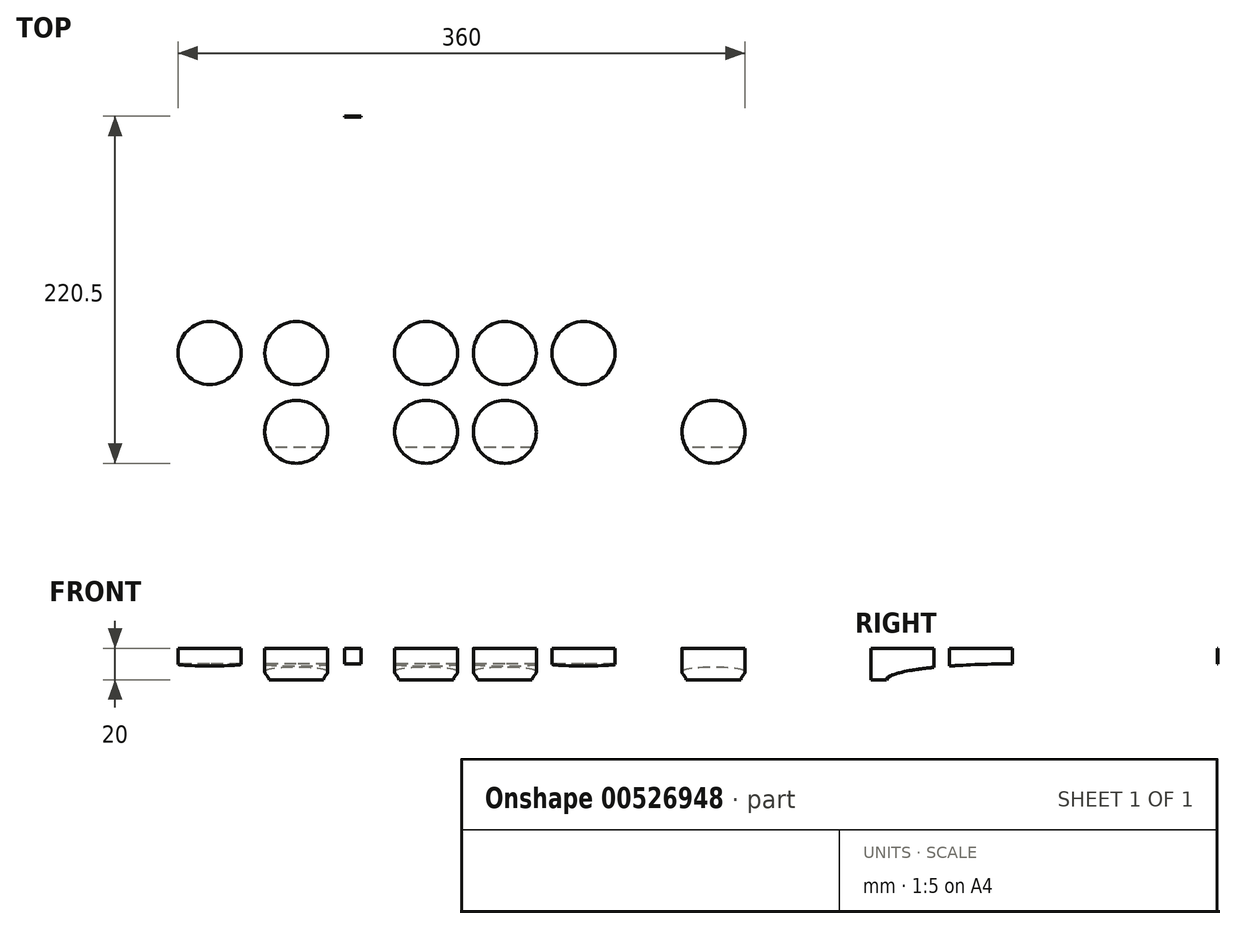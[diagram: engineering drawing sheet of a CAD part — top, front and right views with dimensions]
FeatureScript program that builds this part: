
annotation { "Feature Type Name" : "Feature", "Feature Type Description" : "" }
export const myFeature = defineFeature(function(context is Context, id is Id, definition is map)
    precondition{}
    {
        {
            var Q0;
            Q0=qCreatedBy(makeId("Top.planeOp"),FACE);
            var sketch = newSketch(context, id + "F0", { "sketchPlane" : qUnion([Q0])});
            skLineSegment(sketch, "E0.bottom", {"start": v(-365, 200) * mm, "end": v(365, 200) * mm});
            skLineSegment(sketch, "E0.top", {"start": v(-365, -200) * mm, "end": v(365, -200) * mm});
            skLineSegment(sketch, "E0.left", {"start": v(-365, 200) * mm, "end": v(-365, -200) * mm});
            skLineSegment(sketch, "E0.right", {"start": v(365, 200) * mm, "end": v(365, -200) * mm});
            skPoint(sketch, "E0.middle", {"position": v(0, 0) * mm});
            skEllipticalArc(sketch, "E1", {});
            skEllipticalArc(sketch, "E2.MirrorCS", {});
            skEllipticalArc(sketch, "E3.MirrorCS", {});
            skEllipticalArc(sketch, "E4.MirrorCS", {});
            skLineSegment(sketch, "E5", {"start": v(-365, 200) * mm, "end": v(-105, 200) * mm});
            skLineSegment(sketch, "E6", {"start": v(-365, 200) * mm, "end": v(-365, 50) * mm});
            skLineSegment(sketch, "E7", {"start": v(-365, -200) * mm, "end": v(-365, -50) * mm});
            skLineSegment(sketch, "E8", {"start": v(-365, -200) * mm, "end": v(-182.5, -200) * mm});
            skLineSegment(sketch, "E9", {"start": v(365, 200) * mm, "end": v(105, 200) * mm});
            skLineSegment(sketch, "E10", {"start": v(182.5, -200.11) * mm, "end": v(365, -200) * mm});
            skPoint(sketch, "E11", {"position": v(0, 200) * mm});
            skLineSegment(sketch, "E12", {"start": v(0, 200) * mm, "end": v(-130, 200) * mm});
            skLineSegment(sketch, "E13.MirrorCS", {"start": v(0, -200) * mm, "end": v(-130, -200) * mm});
            skLineSegment(sketch, "E14.MirrorCS", {"start": v(5, 200) * mm, "end": v(130, 200) * mm});
            skLineSegment(sketch, "E15.MirrorCS", {"start": v(-72.5, -200) * mm, "end": v(52.5, -200) * mm});
            skCircle(sketch, "E16", {"center": v(-278.75, 100) * mm, "radius": 20 * mm});
            skCircle(sketch, "E17", {"center": v(-223.75, 150) * mm, "radius": 20 * mm});
            skCircle(sketch, "E18", {"center": v(-223.75, 100) * mm, "radius": 20 * mm});
            skCircle(sketch, "E19", {"center": v(-141.25, 100) * mm, "radius": 20 * mm});
            skCircle(sketch, "E20", {"center": v(-141.25, 150) * mm, "radius": 20 * mm});
            skCircle(sketch, "E21", {"center": v(-91.25, 100) * mm, "radius": 20 * mm});
            skCircle(sketch, "E22", {"center": v(-91.25, 150) * mm, "radius": 20 * mm});
            skCircle(sketch, "E23", {"center": v(-41.25, 100) * mm, "radius": 20 * mm});
            skCircle(sketch, "E24.MirrorC", {"center": v(-41.25, 150) * mm, "radius": 20 * mm});
            skCircle(sketch, "E25.MirrorC", {"center": v(-278.75, -100) * mm, "radius": 20 * mm});
            skCircle(sketch, "E26.MirrorC", {"center": v(-223.75, -150) * mm, "radius": 20 * mm});
            skCircle(sketch, "E27.MirrorC", {"center": v(-223.75, -100) * mm, "radius": 20 * mm});
            skCircle(sketch, "E28.MirrorC", {"center": v(-141.25, -100) * mm, "radius": 20 * mm});
            skCircle(sketch, "E29.MirrorC", {"center": v(-141.25, -150) * mm, "radius": 20 * mm});
            skCircle(sketch, "E30.MirrorC", {"center": v(-91.25, -100) * mm, "radius": 20 * mm});
            skCircle(sketch, "E31.MirrorC", {"center": v(-41.25, -100) * mm, "radius": 20 * mm});
            skCircle(sketch, "E32.MirrorC", {"center": v(-91.25, -150) * mm, "radius": 20 * mm});
            skCircle(sketch, "E33.MirrorC", {"center": v(-41.25, -150) * mm, "radius": 20 * mm});
            skCircle(sketch, "E34.MirrorC", {"center": v(-222.5, -10) * mm, "radius": 20 * mm});
            skLineSegment(sketch, "E35.bottom", {"start": v(210, 15) * mm, "end": v(-210, 15) * mm});
            skLineSegment(sketch, "E35.top", {"start": v(210, -15) * mm, "end": v(-210, -15) * mm});
            skLineSegment(sketch, "E35.left", {"start": v(210, 15) * mm, "end": v(210, -15) * mm});
            skLineSegment(sketch, "E35.right", {"start": v(-210, 15) * mm, "end": v(-210, -15) * mm});
            skLineSegment(sketch, "E36", {"start": v(-365, -50) * mm, "end": v(365, -50) * mm});
            skLineSegment(sketch, "E37", {"start": v(-365, 50) * mm, "end": v(365, 50) * mm});
            skLineSegment(sketch, "E38", {"start": v(-182.5, -200) * mm, "end": v(-182.5, -40.61) * mm});
            skLineSegment(sketch, "E39", {"start": v(0, -200) * mm, "end": v(0, -50) * mm});
            skLineSegment(sketch, "E40", {"start": v(182.5, -200.11) * mm, "end": v(182.4, -40.7) * mm});
            skLineSegment(sketch, "E41.trimOffspring", {"start": v(-182.5, 40.61) * mm, "end": v(-182.5, 200) * mm});
            skLineSegment(sketch, "E42.trimOffspring", {"start": v(-182.5, -15) * mm, "end": v(-182.5, 15) * mm});
            skLineSegment(sketch, "E43.trimOffspring", {"start": v(182.39, -15) * mm, "end": v(182.37, 15) * mm});
            skLineSegment(sketch, "E44.trimOffspring", {"start": v(182.35, 40.73) * mm, "end": v(182.25, 200) * mm});
            skCircle(sketch, "E45", {"center": v(-272.5, 10) * mm, "radius": 20 * mm});
            skCircle(sketch, "E46.MirrorC", {"center": v(-322.5, -8.74) * mm, "radius": 20 * mm});
            skCircle(sketch, "E47.MirrorC", {"center": v(-142.5, -10) * mm, "radius": 20 * mm});
            skCircle(sketch, "E48.MirrorC", {"center": v(-92.5, 10) * mm, "radius": 20 * mm});
            skCircle(sketch, "E49.MirrorC", {"center": v(-42.5, -8.74) * mm, "radius": 20 * mm});
            skCircle(sketch, "E50.MirrorC", {"center": v(42.5, -8.74) * mm, "radius": 20 * mm});
            skCircle(sketch, "E51.MirrorC", {"center": v(142.5, -10) * mm, "radius": 20 * mm});
            skCircle(sketch, "E52.MirrorC", {"center": v(92.5, 10) * mm, "radius": 20 * mm});
            skCircle(sketch, "E53.MirrorC", {"center": v(222.5, -10) * mm, "radius": 20 * mm});
            skCircle(sketch, "E54.MirrorC", {"center": v(272.5, 10) * mm, "radius": 20 * mm});
            skCircle(sketch, "E55.MirrorC", {"center": v(322.5, -8.74) * mm, "radius": 20 * mm});
            skCircle(sketch, "E56.MirrorC", {"center": v(223.75, -100) * mm, "radius": 20 * mm});
            skCircle(sketch, "E57.MirrorC", {"center": v(223.75, -150) * mm, "radius": 20 * mm});
            skCircle(sketch, "E58.MirrorC", {"center": v(278.75, -100) * mm, "radius": 20 * mm});
            skCircle(sketch, "E59.MirrorC", {"center": v(141.25, -100) * mm, "radius": 20 * mm});
            skCircle(sketch, "E60.MirrorC", {"center": v(141.25, -150) * mm, "radius": 20 * mm});
            skCircle(sketch, "E61.MirrorC", {"center": v(91.25, -150) * mm, "radius": 20 * mm});
            skCircle(sketch, "E62.MirrorC", {"center": v(91.25, -100) * mm, "radius": 20 * mm});
            skCircle(sketch, "E63.MirrorC", {"center": v(41.25, -100) * mm, "radius": 20 * mm});
            skCircle(sketch, "E64.MirrorC", {"center": v(41.25, -150) * mm, "radius": 20 * mm});
            skCircle(sketch, "E65.MirrorC", {"center": v(41.25, 100) * mm, "radius": 20 * mm});
            skCircle(sketch, "E66.MirrorC", {"center": v(91.25, 100) * mm, "radius": 20 * mm});
            skCircle(sketch, "E67.MirrorC", {"center": v(141.25, 100) * mm, "radius": 20 * mm});
            skCircle(sketch, "E68.MirrorC", {"center": v(223.75, 100) * mm, "radius": 20 * mm});
            skCircle(sketch, "E69.MirrorC", {"center": v(278.75, 100) * mm, "radius": 20 * mm});
            skCircle(sketch, "E70.MirrorC", {"center": v(223.75, 150) * mm, "radius": 20 * mm});
            skCircle(sketch, "E71.MirrorC", {"center": v(141.25, 150) * mm, "radius": 20 * mm});
            skCircle(sketch, "E72.MirrorC", {"center": v(91.25, 150) * mm, "radius": 20 * mm});
            skCircle(sketch, "E73.MirrorC", {"center": v(41.25, 150) * mm, "radius": 20 * mm});
            const initialGuessF0  = {"E1": [0.215000023161019, -0.00011114199246731203, 0, -1, 0.20000000103052606, 0.15, 6.249845643425636, 1.5707963267948966], "E2.MirrorCS": [-0.215, -0.00011114199246737072, 0, -1, 0.2, 0.15, 4.711833270393751, 0.03333950926130193], "E3.MirrorCS": [-0.215, 0.00011114199246727815, 0, 1, 0.2, 0.15, 6.249845797918284, 1.5707963267948966], "E4.MirrorCS": [0.215, 0.00011114199246735796, 0, 1, 0.2, 0.15, 4.711277560231201, 0.03333950926130226]};
            skSetInitialGuess(sketch, initialGuessF0);
            skSolve(sketch);
        }
        {
            var Q0;
            Q0=qCreatedBy(makeId("Top.planeOp"),FACE);
            cPlane(context, id + "F1", {"entities" : qUnion([Q0]), "cplaneType" : CPlaneType.OFFSET, "offset" : 20 * mm, "width" : 150 * mm, "height" : 150 * mm});
        }
        {
            var Q0;
            Q0=qCreatedBy(id+"F1.planeOp",FACE);
            var sketch = newSketch(context, id + "F2", { "sketchPlane" : qUnion([Q0])});
            skLineSegment(sketch, "E74.bottom", {"start": v(0, 0) * mm, "end": v(365, 0) * mm});
            skLineSegment(sketch, "E74.top", {"start": v(0, -200) * mm, "end": v(210, -200) * mm});
            skLineSegment(sketch, "E74.left", {"start": v(0, 0) * mm, "end": v(0, -200) * mm});
            skLineSegment(sketch, "E75", {"start": v(0, -15) * mm, "end": v(364.58, -15) * mm});
            skLineSegment(sketch, "E76", {"start": v(0, -170) * mm, "end": v(294.02, -170) * mm});
            skLineSegment(sketch, "E77", {"start": v(330, 0) * mm, "end": v(330, -128.4) * mm});
            skLineSegment(sketch, "E78", {"start": v(215, 0) * mm, "end": v(215, -200) * mm});
            skPoint(sketch, "E79", {"position": v(215, -200) * mm});
            skPoint(sketch, "E80", {"position": v(365, 0) * mm});
            skLineSegment(sketch, "E81", {"start": v(275, 0) * mm, "end": v(275, -183.3) * mm});
            skLineSegment(sketch, "E82", {"start": v(275, -140) * mm, "end": v(322.12, -140) * mm});
            skPoint(sketch, "E83", {"position": v(215, -170) * mm});
            skPoint(sketch, "E84", {"position": v(330, 0) * mm});
            skPoint(sketch, "E85", {"position": v(275, -140) * mm});
            skPoint(sketch, "E86", {"position": v(330, -140) * mm});
            skPoint(sketch, "E87", {"position": v(275, -185) * mm});
            skLineSegment(sketch, "E88", {"start": v(315, -149.07) * mm, "end": v(315, 0) * mm});
            skLineSegment(sketch, "E89", {"start": v(210, 0) * mm, "end": v(210, -200) * mm});
            skEllipticalArc(sketch, "E90.trimOffspring", {});
            skEllipticalArc(sketch, "E91", {});
            skPoint(sketch, "E92.orphan", {"position": v(365, -170) * mm});
            skPoint(sketch, "E93.trimOffspring.end.orphan", {"position": v(330, -200) * mm});
            skPoint(sketch, "E94.orphan", {"position": v(365, -200) * mm});
            skPoint(sketch, "E95.orphan", {"position": v(365, -15) * mm});
            skLineSegment(sketch, "E96.MirrorCS", {"start": v(0, 0) * mm, "end": v(-365, 0) * mm});
            skLineSegment(sketch, "E97.MirrorCS", {"start": v(0, -15) * mm, "end": v(-364.58, -15) * mm});
            skLineSegment(sketch, "E98.MirrorCS", {"start": v(0, -170) * mm, "end": v(-294.02, -170) * mm});
            skLineSegment(sketch, "E99.MirrorCS", {"start": v(0, -200) * mm, "end": v(-210, -200) * mm});
            skLineSegment(sketch, "E100.MirrorCS", {"start": v(-210, 0) * mm, "end": v(-210, -200) * mm});
            skLineSegment(sketch, "E101.MirrorCS", {"start": v(-215, 0) * mm, "end": v(-215, -200) * mm});
            skEllipticalArc(sketch, "E102.MirrorCS", {});
            skEllipticalArc(sketch, "E103.MirrorCS", {});
            skLineSegment(sketch, "E104.MirrorCS", {"start": v(-275, 0) * mm, "end": v(-275, -183.3) * mm});
            skLineSegment(sketch, "E105.MirrorCS", {"start": v(-275, -140) * mm, "end": v(-322.12, -140) * mm});
            skLineSegment(sketch, "E106.MirrorCS", {"start": v(-315, -149.07) * mm, "end": v(-315, 0) * mm});
            skLineSegment(sketch, "E107.MirrorCS", {"start": v(-330, 0) * mm, "end": v(-330, -128.4) * mm});
            skLineSegment(sketch, "E108.MirrorCS", {"start": v(0, 15) * mm, "end": v(-364.58, 15) * mm});
            skLineSegment(sketch, "E109.MirrorCS", {"start": v(0, 15) * mm, "end": v(364.58, 15) * mm});
            skEllipticalArc(sketch, "E110.MirrorCS", {});
            skLineSegment(sketch, "E111.MirrorCS", {"start": v(-330, 0) * mm, "end": v(-330, 128.4) * mm});
            skLineSegment(sketch, "E112.MirrorCS", {"start": v(-315, 149.07) * mm, "end": v(-315, 0) * mm});
            skLineSegment(sketch, "E113.MirrorCS", {"start": v(-275, 0) * mm, "end": v(-275, 183.3) * mm});
            skLineSegment(sketch, "E114.MirrorCS", {"start": v(-215, 0) * mm, "end": v(-215, 200) * mm});
            skLineSegment(sketch, "E115.MirrorCS", {"start": v(-210, 0) * mm, "end": v(-210, 200) * mm});
            skLineSegment(sketch, "E116.MirrorCS", {"start": v(0, 0) * mm, "end": v(0, 200) * mm});
            skLineSegment(sketch, "E117.MirrorCS", {"start": v(210, 0) * mm, "end": v(210, 200) * mm});
            skLineSegment(sketch, "E118.MirrorCS", {"start": v(215, 0) * mm, "end": v(215, 200) * mm});
            skLineSegment(sketch, "E119.MirrorCS", {"start": v(275, 0) * mm, "end": v(275, 183.3) * mm});
            skLineSegment(sketch, "E120.MirrorCS", {"start": v(315, 149.07) * mm, "end": v(315, 0) * mm});
            skLineSegment(sketch, "E121.MirrorCS", {"start": v(330, 0) * mm, "end": v(330, 128.4) * mm});
            skEllipticalArc(sketch, "E122.MirrorCS", {});
            skEllipticalArc(sketch, "E123.MirrorCS", {});
            skEllipticalArc(sketch, "E124.MirrorCS", {});
            skLineSegment(sketch, "E125.MirrorCS", {"start": v(-275, 140) * mm, "end": v(-322.12, 140) * mm});
            skLineSegment(sketch, "E126.MirrorCS", {"start": v(0, 170) * mm, "end": v(-294.02, 170) * mm});
            skLineSegment(sketch, "E127.MirrorCS", {"start": v(0, 170) * mm, "end": v(294.02, 170) * mm});
            skLineSegment(sketch, "E128.MirrorCS", {"start": v(0, 200) * mm, "end": v(210, 200) * mm});
            skLineSegment(sketch, "E129.MirrorCS", {"start": v(0, 200) * mm, "end": v(-210, 200) * mm});
            skLineSegment(sketch, "E130.MirrorCS", {"start": v(275, 140) * mm, "end": v(322.12, 140) * mm});
            const initialGuessF2  = {"E90.trimOffspring": [0.215, 0, 1, 0, 0.115, 0.17, 4.71238898038469, 6.283185307179586], "E91": [0.215, 0, 0, -1, 0.2, 0.15, 6.249845797918284, 1.5707963267948966], "E102.MirrorCS": [-0.215, 0, -1, 0, 0.115, 0.17, 6.283185307179586, 1.5707963267948966], "E103.MirrorCS": [-0.215, 0, 0, -1, 0.2, 0.15, 4.71238898038469, 0.03333950926130225], "E110.MirrorCS": [-0.215, 0, 0, 1, 0.2, 0.15, 6.249845797918284, 1.5707963267948966], "E122.MirrorCS": [0.215, 0, 0, 1, 0.2, 0.15, 4.71238898038469, 0.03333950926130225], "E123.MirrorCS": [0.215, 0, 1, 0, 0.115, 0.17, 6.283185307179586, 1.5707963267948966], "E124.MirrorCS": [-0.215, 0, -1, 0, 0.115, 0.17, 4.71238898038469, 6.283185307179586]};
            skSetInitialGuess(sketch, initialGuessF2);
            skSolve(sketch);
        }
        {
            var Q0;
            Q0=qCreatedBy(makeId("Right.planeOp"),FACE);
            var sketch = newSketch(context, id + "F3", { "sketchPlane" : qUnion([Q0])});
            skPoint(sketch, "E131.middle", {"position": v(0, 20) * mm});
            skPoint(sketch, "E132", {"position": v(170, 0) * mm});
            skPoint(sketch, "E133", {"position": v(160, 0) * mm});
            skLineSegment(sketch, "E134.bottom", {"start": v(15, 10.07) * mm, "end": v(80, 10.07) * mm});
            skPoint(sketch, "E135", {"position": v(80, 10.07) * mm});
            skEllipticalArc(sketch, "E136", {});
            skEllipticalArc(sketch, "E137", {});
            skLineSegment(sketch, "E138", {"start": v(0, 20) * mm, "end": v(0, 10.04) * mm});
            skLineSegment(sketch, "E139", {"start": v(0, 20) * mm, "end": v(200, 20) * mm});
            skLineSegment(sketch, "E140", {"start": v(200, 20) * mm, "end": v(0, 20) * mm});
            skLineSegment(sketch, "E141", {"start": v(160, 0) * mm, "end": v(170, 0) * mm});
            skPoint(sketch, "E142.orphan", {"position": v(-200, 20) * mm});
            skLineSegment(sketch, "E143.MirrorCS", {"start": v(-200, 20) * mm, "end": v(0, 20) * mm});
            skLineSegment(sketch, "E144.MirrorCS", {"start": v(-15, 10.07) * mm, "end": v(-80, 10.07) * mm});
            skEllipticalArc(sketch, "E145.MirrorCS", {});
            skLineSegment(sketch, "E146.MirrorCS", {"start": v(-160, 0) * mm, "end": v(-170, 0) * mm});
            skEllipticalArc(sketch, "E147.MirrorCS", {});
            skLineSegment(sketch, "E148.top", {"start": v(-15, 12) * mm, "end": v(15, 12) * mm});
            skLineSegment(sketch, "E148.left", {"start": v(-15, 10.07) * mm, "end": v(-15, 12) * mm});
            skLineSegment(sketch, "E148.right", {"start": v(15, 10.07) * mm, "end": v(15, 12) * mm});
            skLineSegment(sketch, "E149.bottom", {"start": v(15, 18) * mm, "end": v(-15, 18) * mm});
            skLineSegment(sketch, "E149.top", {"start": v(15, 12) * mm, "end": v(-15, 12) * mm});
            skLineSegment(sketch, "E149.left", {"start": v(15, 18) * mm, "end": v(15, 12) * mm});
            skLineSegment(sketch, "E149.right", {"start": v(-15, 18) * mm, "end": v(-15, 12) * mm});
            skLineSegment(sketch, "E150", {"start": v(170, 0) * mm, "end": v(170.12, 20) * mm});
            skLineSegment(sketch, "E151", {"start": v(-170, 0) * mm, "end": v(-170.12, 20) * mm});
            skLineSegment(sketch, "E152", {"start": v(-15, 12) * mm, "end": v(-15, 10.07) * mm});
            skLineSegment(sketch, "E153.bottom", {"start": v(-200, 20) * mm, "end": v(-170, 20) * mm});
            skLineSegment(sketch, "E153.top", {"start": v(-200, 0) * mm, "end": v(-170, 0) * mm});
            skLineSegment(sketch, "E153.left", {"start": v(-200, 20) * mm, "end": v(-200, 0) * mm});
            skLineSegment(sketch, "E153.right", {"start": v(-170, 20) * mm, "end": v(-170, 0) * mm});
            skLineSegment(sketch, "E154.MirrorCS", {"start": v(200, 0) * mm, "end": v(170, 0) * mm});
            skLineSegment(sketch, "E155.MirrorCS", {"start": v(200, 20) * mm, "end": v(200, 0) * mm});
            skLineSegment(sketch, "E156", {"start": v(80, 10.07) * mm, "end": v(80, 20) * mm});
            skLineSegment(sketch, "E157", {"start": v(160, 0) * mm, "end": v(160, 20) * mm});
            skLineSegment(sketch, "E158", {"start": v(149.2, 20) * mm, "end": v(149.2, 5.05) * mm});
            skLineSegment(sketch, "E159", {"start": v(140.08, 20) * mm, "end": v(140.08, 6.65) * mm});
            skLineSegment(sketch, "E160", {"start": v(128.23, 20) * mm, "end": v(128.23, 8.04) * mm});
            skLineSegment(sketch, "E161", {"start": v(102.69, 20) * mm, "end": v(102.69, 9.66) * mm});
            skLineSegment(sketch, "E162.MirrorCS", {"start": v(-80, 10.07) * mm, "end": v(-80, 20) * mm});
            skLineSegment(sketch, "E163.MirrorCS", {"start": v(-102.69, 20) * mm, "end": v(-102.69, 9.66) * mm});
            skLineSegment(sketch, "E164.MirrorCS", {"start": v(-128.23, 20) * mm, "end": v(-128.23, 8.04) * mm});
            skLineSegment(sketch, "E165.MirrorCS", {"start": v(-140.08, 20) * mm, "end": v(-140.08, 6.65) * mm});
            skLineSegment(sketch, "E166.MirrorCS", {"start": v(-149.2, 20) * mm, "end": v(-149.2, 5.05) * mm});
            skLineSegment(sketch, "E167.MirrorCS", {"start": v(-160, 0) * mm, "end": v(-160, 20) * mm});
            skLineSegment(sketch, "E168", {"start": v(45, 20) * mm, "end": v(45, 10.07) * mm});
            skLineSegment(sketch, "E169.MirrorCS", {"start": v(-45, 20) * mm, "end": v(-45, 10.07) * mm});
            const initialGuessF3  = {"E136": [0.17012490332126617, 0.02, -0.006245044279577429, -0.9999804995208388, 0.020000390017188747, 0.02987581400604767, 6.283185307179586, 1.580124845260153], "E137": [0.08, 0, 0, 1, 0.01007139225942586, 0.08, 4.71238898038469, 6.283185307179586], "E145.MirrorCS": [-0.08, 0, 0, 1, 0.01007139225942586, 0.08, 6.283185307179586, 1.5707963267948966], "E147.MirrorCS": [-0.17012490332126617, 0.02, 0.006245044279579518, -0.9999804995208388, 0.020000390017188747, 0.02987581400604767, 4.703060461919433, 6.283185307179586]};
            skSetInitialGuess(sketch, initialGuessF3);
            skSolve(sketch);
        }
        {
            var Q0;
            Q0=qCreatedBy(makeId("Front.planeOp"),FACE);
            var sketch = newSketch(context, id + "F4", { "sketchPlane" : qUnion([Q0])});
            skLineSegment(sketch, "E170", {"start": v(0, 20) * mm, "end": v(365, 20) * mm});
            skPoint(sketch, "E171", {"position": v(210, 20) * mm});
            skLineSegment(sketch, "E172", {"start": v(210, 18) * mm, "end": v(210, 12) * mm});
            skPoint(sketch, "E173", {"position": v(315, 20) * mm});
            skLineSegment(sketch, "E174", {"start": v(315, 18) * mm, "end": v(315, 0) * mm});
            skLineSegment(sketch, "E175", {"start": v(0, 12) * mm, "end": v(0, 20) * mm});
            skLineSegment(sketch, "E176", {"start": v(210, 12) * mm, "end": v(0, 12) * mm});
            skPoint(sketch, "E177", {"position": v(365.07, 0) * mm});
            skPoint(sketch, "E178", {"position": v(365, 20) * mm});
            skEllipticalArc(sketch, "E179", {});
            skLineSegment(sketch, "E180", {"start": v(315, 18) * mm, "end": v(210, 18) * mm});
            skLineSegment(sketch, "E181.MirrorCS", {"start": v(0, 20) * mm, "end": v(-365, 20) * mm});
            skLineSegment(sketch, "E182.MirrorCS", {"start": v(-210, 12) * mm, "end": v(0, 12) * mm});
            skLineSegment(sketch, "E183.MirrorCS", {"start": v(-210, 18) * mm, "end": v(-210, 12) * mm});
            skLineSegment(sketch, "E184.MirrorCS", {"start": v(-315, 18) * mm, "end": v(-210, 18) * mm});
            skLineSegment(sketch, "E185.MirrorCS", {"start": v(-315, 18) * mm, "end": v(-315, 0) * mm});
            skEllipticalArc(sketch, "E186.MirrorCS", {});
            skPoint(sketch, "E187", {"position": v(245, 20) * mm});
            skPoint(sketch, "E188", {"position": v(245, 10.07) * mm});
            skPoint(sketch, "E189", {"position": v(325, 20) * mm});
            skPoint(sketch, "E190", {"position": v(335, 20) * mm});
            skLineSegment(sketch, "E191", {"start": v(335, 20) * mm, "end": v(335, 10.07) * mm});
            skLineSegment(sketch, "E192", {"start": v(335, 10.07) * mm, "end": v(0, 10.07) * mm});
            skLineSegment(sketch, "E193.MirrorCS", {"start": v(-335, 10.07) * mm, "end": v(0, 10.07) * mm});
            skLineSegment(sketch, "E194.MirrorCS", {"start": v(-335, 20) * mm, "end": v(-335, 10.07) * mm});
            skLineSegment(sketch, "E195", {"start": v(365, 20) * mm, "end": v(365.07, 0) * mm});
            skLineSegment(sketch, "E196", {"start": v(315, 0) * mm, "end": v(365.07, 0) * mm});
            skLineSegment(sketch, "E197.MirrorCS", {"start": v(-365, 20) * mm, "end": v(-365.07, 0) * mm});
            skLineSegment(sketch, "E198.MirrorCS", {"start": v(-315, 0) * mm, "end": v(-365.07, 0) * mm});
            skLineSegment(sketch, "E199", {"start": v(335, 10.07) * mm, "end": v(335, 1.67) * mm});
            skLineSegment(sketch, "E200.MirrorCS", {"start": v(-335, 10.07) * mm, "end": v(-335, 1.67) * mm});
            skLineSegment(sketch, "E201", {"start": v(-315, 18) * mm, "end": v(-315, 20) * mm});
            skLineSegment(sketch, "E202", {"start": v(-210, 18) * mm, "end": v(-210, 20) * mm});
            skLineSegment(sketch, "E203.MirrorCS", {"start": v(210, 18) * mm, "end": v(210, 20) * mm});
            skLineSegment(sketch, "E204.MirrorCS", {"start": v(315, 18) * mm, "end": v(315, 20) * mm});
            skPoint(sketch, "E205", {"position": v(275, 20) * mm});
            skPoint(sketch, "E206.MirrorP", {"position": v(-275, 20) * mm});
            skLineSegment(sketch, "E207", {"start": v(275, 20) * mm, "end": v(275, 18) * mm});
            skLineSegment(sketch, "E208.MirrorCS", {"start": v(-275, 20) * mm, "end": v(-275, 18) * mm});
            skPoint(sketch, "E209", {"position": v(-333.25, 14.9) * mm});
            skPoint(sketch, "E210", {"position": v(-218.12, 14.9) * mm});
            skPoint(sketch, "E211", {"position": v(-78.75, 14.9) * mm});
            const initialGuessF4  = {"E179": [0.315, 0.02, 1, 0, 0.05, 0.02, 4.71238898038469, 0], "E186.MirrorCS": [-0.315, 0.02, -1, 0, 0.05, 0.02, 0, 1.5707963267948966]};
            skSetInitialGuess(sketch, initialGuessF4);
            skSolve(sketch);
        }
        {
            var Q0;
            Q0=qSketchRegion(id+"F2",true);
            var Q1;
            {var subQ0=sQuery(id+"F2.wireOp",EDGE,"E125.MirrorCS");var subQ1=sQuery(id+"F2.wireOp",EDGE,"E112.MirrorCS");var subQ2=makeQuery(id+"F2.imprint","INTERSECT",VERTEX,{"derivedFrom":[subQ1,subQ0]});Q1=makeQuery(id+"F2.imprint","IMPRINT",FACE,{"disambiguationData":[TD([[makeQuery(id+"F2.imprint","IMPRINT",EDGE,{"disambiguationData":[TD([[subQ2,-1.0]])],"derivedFrom":subQ1}),1.0]])]});}
            var Q2;
            {var subQ0=sQuery(id+"F2.wireOp",EDGE,"E124.MirrorCS");var subQ1=sQuery(id+"F2.wireOp",EDGE,"E113.MirrorCS");var subQ2=makeQuery(id+"F2.imprint","INTERSECT",VERTEX,{"derivedFrom":[subQ1,subQ0]});Q2=makeQuery(id+"F2.imprint","IMPRINT",FACE,{"disambiguationData":[TD([[makeQuery(id+"F2.imprint","IMPRINT",EDGE,{"disambiguationData":[TD([[subQ2,-1.0]])],"derivedFrom":subQ1}),-1.0]])]});}
            var Q3;
            {var subQ0=sQuery(id+"F2.wireOp",EDGE,"E123.MirrorCS");var subQ1=sQuery(id+"F2.wireOp",EDGE,"E119.MirrorCS");var subQ2=makeQuery(id+"F2.imprint","INTERSECT",VERTEX,{"derivedFrom":[subQ1,subQ0]});Q3=makeQuery(id+"F2.imprint","IMPRINT",FACE,{"disambiguationData":[TD([[makeQuery(id+"F2.imprint","IMPRINT",EDGE,{"disambiguationData":[TD([[subQ2,-1.0]])],"derivedFrom":subQ1}),1.0]])]});}
            var Q4;
            {var subQ0=sQuery(id+"F2.wireOp",EDGE,"E130.MirrorCS");var subQ1=sQuery(id+"F2.wireOp",EDGE,"E120.MirrorCS");var subQ2=makeQuery(id+"F2.imprint","INTERSECT",VERTEX,{"derivedFrom":[subQ1,subQ0]});Q4=makeQuery(id+"F2.imprint","IMPRINT",FACE,{"disambiguationData":[TD([[makeQuery(id+"F2.imprint","IMPRINT",EDGE,{"disambiguationData":[TD([[subQ2,-1.0]])],"derivedFrom":subQ1}),-1.0]])]});}
            var Q5;
            {var subQ0=sQuery(id+"F2.wireOp",EDGE,"E90.trimOffspring");var subQ1=sQuery(id+"F2.wireOp",EDGE,"E82");var subQ2=makeQuery(id+"F2.imprint","INTERSECT",VERTEX,{"derivedFrom":[subQ1,subQ0]});Q5=makeQuery(id+"F2.imprint","IMPRINT",FACE,{"disambiguationData":[TD([[makeQuery(id+"F2.imprint","IMPRINT",EDGE,{"disambiguationData":[TD([[subQ2,-1.0]])],"derivedFrom":subQ1}),1.0]])]});}
            var Q6;
            {var subQ1=sQuery(id+"F2.wireOp",EDGE,"E76");var subQ3=sQuery(id+"F2.wireOp",EDGE,"E81");var subQ4=makeQuery(id+"F2.imprint","INTERSECT",VERTEX,{"derivedFrom":[subQ1,subQ3]});Q6=makeQuery(id+"F2.imprint","IMPRINT",FACE,{"disambiguationData":[TD([[makeQuery(id+"F2.imprint","IMPRINT",EDGE,{"disambiguationData":[TD([[subQ4,1.0]])],"derivedFrom":subQ3}),-1.0]])]});}
            var Q7;
            {var subQ1=sQuery(id+"F2.wireOp",EDGE,"E98.MirrorCS");var subQ3=sQuery(id+"F2.wireOp",EDGE,"E104.MirrorCS");var subQ4=makeQuery(id+"F2.imprint","INTERSECT",VERTEX,{"derivedFrom":[subQ1,subQ3]});Q7=makeQuery(id+"F2.imprint","IMPRINT",FACE,{"disambiguationData":[TD([[makeQuery(id+"F2.imprint","IMPRINT",EDGE,{"disambiguationData":[TD([[subQ4,1.0]])],"derivedFrom":subQ3}),1.0]])]});}
            var Q8;
            {var subQ0=sQuery(id+"F2.wireOp",EDGE,"E106.MirrorCS");var subQ1=sQuery(id+"F2.wireOp",EDGE,"E102.MirrorCS");var subQ2=makeQuery(id+"F2.imprint","INTERSECT",VERTEX,{"derivedFrom":[subQ1,subQ0]});Q8=makeQuery(id+"F2.imprint","IMPRINT",FACE,{"disambiguationData":[TD([[makeQuery(id+"F2.imprint","IMPRINT",EDGE,{"disambiguationData":[TD([[subQ2,-1.0]])],"derivedFrom":subQ1}),-1.0]])]});}
            extrude(context, id + "F5", {"entities" : qUnion([Q0, Q1, Q2, Q3, Q4, Q5, Q6, Q7, Q8]), "oppositeDirection" : true, "depth" : 20 * mm, "offsetDistance" : 25 * mm});
        }
        {
            var Q0;
            {var subQ0=sQuery(id+"F3.wireOp",EDGE,"E149.right");Q0=makeQuery(id+"F3.imprint","IMPRINT",FACE,{"disambiguationData":[TD([[makeQuery(id+"F3.imprint","IMPRINT",EDGE,{"derivedFrom":subQ0}),-1.0]])]});}
            var Q1;
            {var subQ0=sQuery(id+"F3.wireOp",EDGE,"E149.left");Q1=makeQuery(id+"F3.imprint","IMPRINT",FACE,{"disambiguationData":[TD([[makeQuery(id+"F3.imprint","IMPRINT",EDGE,{"derivedFrom":subQ0}),1.0]])]});}
            extrude(context, id + "F6", {"entities" : qUnion([Q0, Q1]), "operationType" : NewBodyOperationType.ADD, "depth" : 420 * mm, "offsetDistance" : 25 * mm, "symmetric" : true});
        }
        {
            var Q0;
            {var subQ0=sQuery(id+"F3.wireOp",EDGE,"E156");Q0=makeQuery(id+"F3.imprint","IMPRINT",FACE,{"disambiguationData":[TD([[makeQuery(id+"F3.imprint","IMPRINT",EDGE,{"derivedFrom":subQ0}),-1.0]])]});}
            var Q1;
            {var subQ0=sQuery(id+"F3.wireOp",EDGE,"E160");Q1=makeQuery(id+"F3.imprint","IMPRINT",FACE,{"disambiguationData":[TD([[makeQuery(id+"F3.imprint","IMPRINT",EDGE,{"derivedFrom":subQ0}),-1.0]])]});}
            var Q2;
            {var subQ0=sQuery(id+"F3.wireOp",EDGE,"E159");Q2=makeQuery(id+"F3.imprint","IMPRINT",FACE,{"disambiguationData":[TD([[makeQuery(id+"F3.imprint","IMPRINT",EDGE,{"derivedFrom":subQ0}),-1.0]])]});}
            var Q3;
            {var subQ0=sQuery(id+"F3.wireOp",EDGE,"E158");Q3=makeQuery(id+"F3.imprint","IMPRINT",FACE,{"disambiguationData":[TD([[makeQuery(id+"F3.imprint","IMPRINT",EDGE,{"derivedFrom":subQ0}),-1.0]])]});}
            var Q4;
            {var subQ0=sQuery(id+"F3.wireOp",EDGE,"E157");Q4=makeQuery(id+"F3.imprint","IMPRINT",FACE,{"disambiguationData":[TD([[makeQuery(id+"F3.imprint","IMPRINT",EDGE,{"derivedFrom":subQ0}),1.0]])]});}
            var Q5;
            Q5=makeQuery(id+"F3.imprint","IMPRINT",FACE,{"disambiguationData":[TD([[makeQuery(id+"F3.imprint","IMPRINT",EDGE,{"derivedFrom":sQuery(id+"F3.wireOp",EDGE,"E141")}),1.0]])]});
            var Q6;
            {var subQ0=sQuery(id+"F3.wireOp",EDGE,"E162.MirrorCS");Q6=makeQuery(id+"F3.imprint","IMPRINT",FACE,{"disambiguationData":[TD([[makeQuery(id+"F3.imprint","IMPRINT",EDGE,{"derivedFrom":subQ0}),1.0]])]});}
            var Q7;
            {var subQ0=sQuery(id+"F3.wireOp",EDGE,"E163.MirrorCS");Q7=makeQuery(id+"F3.imprint","IMPRINT",FACE,{"disambiguationData":[TD([[makeQuery(id+"F3.imprint","IMPRINT",EDGE,{"derivedFrom":subQ0}),-1.0]])]});}
            var Q8;
            {var subQ0=sQuery(id+"F3.wireOp",EDGE,"E164.MirrorCS");Q8=makeQuery(id+"F3.imprint","IMPRINT",FACE,{"disambiguationData":[TD([[makeQuery(id+"F3.imprint","IMPRINT",EDGE,{"derivedFrom":subQ0}),-1.0]])]});}
            var Q9;
            {var subQ0=sQuery(id+"F3.wireOp",EDGE,"E165.MirrorCS");Q9=makeQuery(id+"F3.imprint","IMPRINT",FACE,{"disambiguationData":[TD([[makeQuery(id+"F3.imprint","IMPRINT",EDGE,{"derivedFrom":subQ0}),-1.0]])]});}
            var Q10;
            {var subQ0=sQuery(id+"F3.wireOp",EDGE,"E166.MirrorCS");Q10=makeQuery(id+"F3.imprint","IMPRINT",FACE,{"disambiguationData":[TD([[makeQuery(id+"F3.imprint","IMPRINT",EDGE,{"derivedFrom":subQ0}),-1.0]])]});}
            var Q11;
            Q11=makeQuery(id+"F3.imprint","IMPRINT",FACE,{"disambiguationData":[TD([[makeQuery(id+"F3.imprint","IMPRINT",EDGE,{"derivedFrom":sQuery(id+"F3.wireOp",EDGE,"E146.MirrorCS")}),-1.0]])]});
            var Q12;
            {var subQ0=sQuery(id+"F3.wireOp",EDGE,"E156");Q12=makeQuery(id+"F3.imprint","IMPRINT",FACE,{"disambiguationData":[TD([[makeQuery(id+"F3.imprint","IMPRINT",EDGE,{"derivedFrom":subQ0}),1.0]])]});}
            var Q13;
            {var subQ0=sQuery(id+"F3.wireOp",EDGE,"E162.MirrorCS");Q13=makeQuery(id+"F3.imprint","IMPRINT",FACE,{"disambiguationData":[TD([[makeQuery(id+"F3.imprint","IMPRINT",EDGE,{"derivedFrom":subQ0}),-1.0]])]});}
            extrude(context, id + "F7", {"entities" : qUnion([Q0, Q1, Q2, Q3, Q4, Q5, Q6, Q7, Q8, Q9, Q10, Q11, Q12, Q13]), "operationType" : NewBodyOperationType.ADD, "depth" : 520 * mm, "offsetDistance" : 25 * mm, "symmetric" : true});
        }
        {
            var Q0;
            Q0=makeQuery(id+"F4.imprint","IMPRINT",FACE,{"disambiguationData":[TD([[makeQuery(id+"F4.imprint","IMPRINT",EDGE,{"derivedFrom":sQuery(id+"F4.wireOp",EDGE,"E172")}),-1.0]])]});
            var Q1;
            {var subQ1=sQuery(id+"F4.wireOp",EDGE,"E179");Q1=makeQuery(id+"F4.imprint","IMPRINT",FACE,{"disambiguationData":[TD([[makeQuery(id+"F4.imprint","IMPRINT",EDGE,{"derivedFrom":subQ1}),1.0]])]});}
            var Q2;
            {var subQ2=sQuery(id+"F4.wireOp",EDGE,"E175");Q2=makeQuery(id+"F4.imprint","IMPRINT",FACE,{"disambiguationData":[TD([[makeQuery(id+"F4.imprint","IMPRINT",EDGE,{"derivedFrom":subQ2}),1.0]])]});}
            var Q3;
            {var subQ0=sQuery(id+"F4.wireOp",EDGE,"E186.MirrorCS");Q3=makeQuery(id+"F4.imprint","IMPRINT",FACE,{"disambiguationData":[TD([[makeQuery(id+"F4.imprint","IMPRINT",EDGE,{"derivedFrom":subQ0}),1.0]])]});}
            extrude(context, id + "F8", {"entities" : qUnion([Q0, Q1, Q2, Q3]), "operationType" : NewBodyOperationType.ADD, "depth" : 30 * mm, "offsetDistance" : 25 * mm, "symmetric" : true});
        }
        {
            var Q0;
            {var subQ0=sQuery(id+"F3.wireOp",EDGE,"E153.left");var subQ1=sQuery(id+"F3.wireOp",EDGE,"E147.MirrorCS");var subQ2=makeQuery(id+"F3.imprint","INTERSECT",VERTEX,{"derivedFrom":[subQ1,subQ0]});Q0=makeQuery(id+"F3.imprint","IMPRINT",FACE,{"disambiguationData":[TD([[makeQuery(id+"F3.imprint","IMPRINT",EDGE,{"disambiguationData":[TD([[subQ2,-1.0]])],"derivedFrom":subQ1}),-1.0]])]});}
            var Q1;
            {var subQ0=sQuery(id+"F3.wireOp",EDGE,"E155.MirrorCS");var subQ1=sQuery(id+"F3.wireOp",EDGE,"E136");var subQ2=makeQuery(id+"F3.imprint","INTERSECT",VERTEX,{"derivedFrom":[subQ1,subQ0]});Q1=makeQuery(id+"F3.imprint","IMPRINT",FACE,{"disambiguationData":[TD([[makeQuery(id+"F3.imprint","IMPRINT",EDGE,{"disambiguationData":[TD([[subQ2,1.0]])],"derivedFrom":subQ1}),-1.0]])]});}
            var Q2;
            Q2=sQuery(id+"F3.wireOp",EDGE,"E153.left");
            var Q3;
            Q3=sQuery(id+"F3.wireOp",EDGE,"E153.top");
            var Q4;
            Q4=sQuery(id+"F3.wireOp",EDGE,"E147.MirrorCS");
            extrude(context, id + "F9", {"entities" : qUnion([Q0, Q1]), "operationType" : NewBodyOperationType.REMOVE, "surfaceEntities" : qUnion([Q2, Q3, Q4]), "oppositeDirection" : true, "depth" : 730 * mm, "offsetDistance" : 25 * mm, "symmetric" : true});
        }
        {
            var Q0;
            Q0=makeQuery(id+"F4.imprint","IMPRINT",FACE,{"disambiguationData":[TD([[makeQuery(id+"F4.imprint","IMPRINT",EDGE,{"derivedFrom":sQuery(id+"F4.wireOp",EDGE,"E186.MirrorCS")}),-1.0]])]});
            var Q1;
            Q1=makeQuery(id+"F4.imprint","IMPRINT",FACE,{"disambiguationData":[TD([[makeQuery(id+"F4.imprint","IMPRINT",EDGE,{"derivedFrom":sQuery(id+"F4.wireOp",EDGE,"E179")}),-1.0]])]});
            extrude(context, id + "F10", {"entities" : qUnion([Q0, Q1]), "operationType" : NewBodyOperationType.REMOVE, "oppositeDirection" : true, "depth" : 400 * mm, "offsetDistance" : 25 * mm, "symmetric" : true});
        }
        {
            var Q0;
            Q0=makeQuery(id+"F4.imprint","IMPRINT",FACE,{"disambiguationData":[TD([[makeQuery(id+"F4.imprint","IMPRINT",EDGE,{"derivedFrom":sQuery(id+"F4.wireOp",EDGE,"E172")}),-1.0]])]});
            var Q1;
            {var subQ5=sQuery(id+"F4.wireOp",EDGE,"E199");Q1=makeQuery(id+"F4.imprint","IMPRINT",FACE,{"disambiguationData":[TD([[makeQuery(id+"F4.imprint","IMPRINT",EDGE,{"derivedFrom":subQ5}),-1.0]])]});}
            var Q2;
            {var subQ5=sQuery(id+"F4.wireOp",EDGE,"E200.MirrorCS");Q2=makeQuery(id+"F4.imprint","IMPRINT",FACE,{"disambiguationData":[TD([[makeQuery(id+"F4.imprint","IMPRINT",EDGE,{"derivedFrom":subQ5}),1.0]])]});}
            var Q3;
            {var subQ2=sQuery(id+"F4.wireOp",EDGE,"E175");Q3=makeQuery(id+"F4.imprint","IMPRINT",FACE,{"disambiguationData":[TD([[makeQuery(id+"F4.imprint","IMPRINT",EDGE,{"derivedFrom":subQ2}),1.0]])]});}
            var Q4;
            {var subQ0=sQuery(id+"F4.wireOp",EDGE,"E194.MirrorCS");Q4=makeQuery(id+"F4.imprint","IMPRINT",FACE,{"disambiguationData":[TD([[makeQuery(id+"F4.imprint","IMPRINT",EDGE,{"derivedFrom":subQ0}),1.0]])]});}
            var Q5;
            {var subQ1=sQuery(id+"F4.wireOp",EDGE,"E191");Q5=makeQuery(id+"F4.imprint","IMPRINT",FACE,{"disambiguationData":[TD([[makeQuery(id+"F4.imprint","IMPRINT",EDGE,{"derivedFrom":subQ1}),-1.0]])]});}
            extrude(context, id + "F11", {"entities" : qUnion([Q0, Q1, Q2, Q3, Q4, Q5]), "operationType" : NewBodyOperationType.ADD, "depth" : 169 * mm, "offsetDistance" : 25 * mm, "symmetric" : true});
        }
        {
            var Q0;
            Q0=makeQuery(id+"F4.imprint","IMPRINT",FACE,{"disambiguationData":[TD([[makeQuery(id+"F4.imprint","IMPRINT",EDGE,{"derivedFrom":sQuery(id+"F4.wireOp",EDGE,"E180")}),-1.0]])]});
            var Q1;
            Q1=makeQuery(id+"F4.imprint","IMPRINT",FACE,{"disambiguationData":[TD([[makeQuery(id+"F4.imprint","IMPRINT",EDGE,{"derivedFrom":sQuery(id+"F4.wireOp",EDGE,"E184.MirrorCS")}),1.0]])]});
            extrude(context, id + "F12", {"entities" : qUnion([Q0, Q1]), "operationType" : NewBodyOperationType.ADD, "depth" : 295 * mm, "offsetDistance" : 25 * mm, "symmetric" : true});
        }
        {
            var Q0;
            {var subQ0=sQuery(id+"F4.wireOp",EDGE,"E203.MirrorCS");Q0=makeQuery(id+"F4.imprint","IMPRINT",FACE,{"disambiguationData":[TD([[makeQuery(id+"F4.imprint","IMPRINT",EDGE,{"derivedFrom":subQ0}),-1.0]])]});}
            var Q1;
            {var subQ0=sQuery(id+"F4.wireOp",EDGE,"E202");Q1=makeQuery(id+"F4.imprint","IMPRINT",FACE,{"disambiguationData":[TD([[makeQuery(id+"F4.imprint","IMPRINT",EDGE,{"derivedFrom":subQ0}),1.0]])]});}
            extrude(context, id + "F13", {"entities" : qUnion([Q0, Q1]), "operationType" : NewBodyOperationType.ADD, "depth" : 350 * mm, "offsetDistance" : 25 * mm, "symmetric" : true});
        }
        {
            var Q0;
            {var subQ0=sQuery(id+"F2.wireOp",EDGE,"E122.MirrorCS");var subQ1=sQuery(id+"F2.wireOp",EDGE,"E91");Q0=makeQuery(id+"F10.boolean.opBoolean","SPLIT",EDGE,{"disambiguationData":[TD([makeQuery(id+"F9.boolean.opBoolean","COPY",FACE,{"derivedFrom":makeQuery(id+"F9.opExtrude","SWEPT_FACE",FACE,{"disambiguationData":[OSD([sQuery(id+"F3.wireOp",EDGE,"E136")])]})})])],"derivedFrom":makeQuery(id+"F5.opExtrude","CAP_EDGE",EDGE,{"disambiguationData":[OSD([subQ1,subQ0])],"isStart":false})});}
            var Q1;
            {var subQ0=sQuery(id+"F2.wireOp",EDGE,"E122.MirrorCS");var subQ1=sQuery(id+"F2.wireOp",EDGE,"E91");Q1=makeQuery(id+"F10.boolean.opBoolean","SPLIT",EDGE,{"disambiguationData":[TD([makeQuery(id+"F9.boolean.opBoolean","COPY",FACE,{"derivedFrom":makeQuery(id+"F9.opExtrude","SWEPT_FACE",FACE,{"disambiguationData":[OSD([sQuery(id+"F3.wireOp",EDGE,"E147.MirrorCS")])]})})])],"derivedFrom":makeQuery(id+"F5.opExtrude","CAP_EDGE",EDGE,{"disambiguationData":[OSD([subQ1,subQ0])],"isStart":false})});}
            var Q2;
            {var subQ0=sQuery(id+"F2.wireOp",EDGE,"E110.MirrorCS");var subQ1=sQuery(id+"F2.wireOp",EDGE,"E103.MirrorCS");Q2=makeQuery(id+"F10.boolean.opBoolean","SPLIT",EDGE,{"disambiguationData":[TD([makeQuery(id+"F9.boolean.opBoolean","COPY",FACE,{"derivedFrom":makeQuery(id+"F9.opExtrude","SWEPT_FACE",FACE,{"disambiguationData":[OSD([sQuery(id+"F3.wireOp",EDGE,"E147.MirrorCS")])]})})])],"derivedFrom":makeQuery(id+"F5.opExtrude","CAP_EDGE",EDGE,{"disambiguationData":[OSD([subQ1,subQ0])],"isStart":false})});}
            var Q3;
            {var subQ0=sQuery(id+"F2.wireOp",EDGE,"E110.MirrorCS");var subQ1=sQuery(id+"F2.wireOp",EDGE,"E103.MirrorCS");Q3=makeQuery(id+"F10.boolean.opBoolean","SPLIT",EDGE,{"disambiguationData":[TD([makeQuery(id+"F9.boolean.opBoolean","COPY",FACE,{"derivedFrom":makeQuery(id+"F9.opExtrude","SWEPT_FACE",FACE,{"disambiguationData":[OSD([sQuery(id+"F3.wireOp",EDGE,"E136")])]})})])],"derivedFrom":makeQuery(id+"F5.opExtrude","CAP_EDGE",EDGE,{"disambiguationData":[OSD([subQ1,subQ0])],"isStart":false})});}
            fillet(context, id + "F14", {"entities" : qUnion([Q0, Q1, Q2, Q3]), "radius" : 18 * mm, "tangentPropagation" : true, "allowEdgeOverflow" : false});
        }
        {
            var Q0;
            {var subQ0=sQuery(id+"F3.wireOp",EDGE,"E162.MirrorCS");Q0=makeQuery(id+"F3.imprint","IMPRINT",FACE,{"disambiguationData":[TD([[makeQuery(id+"F3.imprint","IMPRINT",EDGE,{"derivedFrom":subQ0}),-1.0]])]});}
            var Q1;
            {var subQ0=sQuery(id+"F3.wireOp",EDGE,"E156");Q1=makeQuery(id+"F3.imprint","IMPRINT",FACE,{"disambiguationData":[TD([[makeQuery(id+"F3.imprint","IMPRINT",EDGE,{"derivedFrom":subQ0}),1.0]])]});}
            extrude(context, id + "F15", {"entities" : qUnion([Q0, Q1]), "operationType" : NewBodyOperationType.ADD, "depth" : 670 * mm, "offsetDistance" : 25 * mm, "symmetric" : true});
        }
        {
            var Q0;
            {var subQ0=sQuery(id+"F3.wireOp",EDGE,"E156");Q0=makeQuery(id+"F3.imprint","IMPRINT",FACE,{"disambiguationData":[TD([[makeQuery(id+"F3.imprint","IMPRINT",EDGE,{"derivedFrom":subQ0}),-1.0]])]});}
            var Q1;
            {var subQ0=sQuery(id+"F3.wireOp",EDGE,"E162.MirrorCS");Q1=makeQuery(id+"F3.imprint","IMPRINT",FACE,{"disambiguationData":[TD([[makeQuery(id+"F3.imprint","IMPRINT",EDGE,{"derivedFrom":subQ0}),1.0]])]});}
            extrude(context, id + "F16", {"entities" : qUnion([Q0, Q1]), "operationType" : NewBodyOperationType.ADD, "depth" : 630 * mm, "offsetDistance" : 25 * mm, "symmetric" : true});
        }
        {
            var Q0;
            {var subQ0=sQuery(id+"F3.wireOp",EDGE,"E166.MirrorCS");Q0=makeQuery(id+"F3.imprint","IMPRINT",FACE,{"disambiguationData":[TD([[makeQuery(id+"F3.imprint","IMPRINT",EDGE,{"derivedFrom":subQ0}),-1.0]])]});}
            var Q1;
            {var subQ0=sQuery(id+"F3.wireOp",EDGE,"E157");Q1=makeQuery(id+"F3.imprint","IMPRINT",FACE,{"disambiguationData":[TD([[makeQuery(id+"F3.imprint","IMPRINT",EDGE,{"derivedFrom":subQ0}),1.0]])]});}
            extrude(context, id + "F17", {"entities" : qUnion([Q0, Q1]), "operationType" : NewBodyOperationType.ADD, "depth" : 550 * mm, "offsetDistance" : 25 * mm, "symmetric" : true});
        }
        {
            var Q0;
            {var subQ0=sQuery(id+"F3.wireOp",EDGE,"E158");Q0=makeQuery(id+"F3.imprint","IMPRINT",FACE,{"disambiguationData":[TD([[makeQuery(id+"F3.imprint","IMPRINT",EDGE,{"derivedFrom":subQ0}),-1.0]])]});}
            var Q1;
            {var subQ0=sQuery(id+"F3.wireOp",EDGE,"E165.MirrorCS");Q1=makeQuery(id+"F3.imprint","IMPRINT",FACE,{"disambiguationData":[TD([[makeQuery(id+"F3.imprint","IMPRINT",EDGE,{"derivedFrom":subQ0}),-1.0]])]});}
            extrude(context, id + "F18", {"entities" : qUnion([Q0, Q1]), "operationType" : NewBodyOperationType.ADD, "depth" : 600 * mm, "offsetDistance" : 25 * mm, "symmetric" : true});
        }
        {
            var Q0;
            {var subQ0=sQuery(id+"F3.wireOp",EDGE,"E159");Q0=makeQuery(id+"F3.imprint","IMPRINT",FACE,{"disambiguationData":[TD([[makeQuery(id+"F3.imprint","IMPRINT",EDGE,{"derivedFrom":subQ0}),-1.0]])]});}
            var Q1;
            {var subQ0=sQuery(id+"F3.wireOp",EDGE,"E164.MirrorCS");Q1=makeQuery(id+"F3.imprint","IMPRINT",FACE,{"disambiguationData":[TD([[makeQuery(id+"F3.imprint","IMPRINT",EDGE,{"derivedFrom":subQ0}),-1.0]])]});}
            extrude(context, id + "F19", {"entities" : qUnion([Q0, Q1]), "operationType" : NewBodyOperationType.ADD, "depth" : 620 * mm, "offsetDistance" : 25 * mm, "symmetric" : true});
        }
        {
            var Q0;
            {var subQ0=sQuery(id+"F3.wireOp",EDGE,"E163.MirrorCS");Q0=makeQuery(id+"F3.imprint","IMPRINT",FACE,{"disambiguationData":[TD([[makeQuery(id+"F3.imprint","IMPRINT",EDGE,{"derivedFrom":subQ0}),-1.0]])]});}
            var Q1;
            {var subQ0=sQuery(id+"F3.wireOp",EDGE,"E160");Q1=makeQuery(id+"F3.imprint","IMPRINT",FACE,{"disambiguationData":[TD([[makeQuery(id+"F3.imprint","IMPRINT",EDGE,{"derivedFrom":subQ0}),-1.0]])]});}
            extrude(context, id + "F20", {"entities" : qUnion([Q0, Q1]), "operationType" : NewBodyOperationType.ADD, "depth" : 620 * mm, "offsetDistance" : 25 * mm, "symmetric" : true});
        }
        {
            var Q0;
            Q0=makeQuery(id+"F5.opExtrude","CAP_EDGE",EDGE,{"disambiguationData":[OSD([sQuery(id+"F2.wireOp",EDGE,"E124.MirrorCS")])],"isStart":false});
            var Q1;
            Q1=makeQuery(id+"F5.opExtrude","CAP_EDGE",EDGE,{"disambiguationData":[OSD([sQuery(id+"F2.wireOp",EDGE,"E123.MirrorCS")])],"isStart":false});
            var Q2;
            Q2=makeQuery(id+"F5.opExtrude","CAP_EDGE",EDGE,{"disambiguationData":[OSD([sQuery(id+"F2.wireOp",EDGE,"E90.trimOffspring")])],"isStart":false});
            var Q3;
            Q3=makeQuery(id+"F5.opExtrude","CAP_EDGE",EDGE,{"disambiguationData":[OSD([sQuery(id+"F2.wireOp",EDGE,"E102.MirrorCS")])],"isStart":false});
            chamfer(context, id + "F21", {"entities" : qUnion([Q0, Q1, Q2, Q3]), "chamferType" : ChamferType.OFFSET_ANGLE, "width" : 15 * mm, "oppositeDirection" : false, "angle" : 35 * degree, "tangentPropagation" : true});
        }
        {
            var Q0;
            {var subQ0=sQuery(id+"F4.wireOp",EDGE,"E198.MirrorCS");var subQ1=sQuery(id+"F4.wireOp",EDGE,"E186.MirrorCS");var subQ2=sQuery(id+"F4.wireOp",EDGE,"E185.MirrorCS");Q0=makeQuery(id+"F11.boolean.opBoolean","MERGE",EDGE,{"derivedFrom":[makeQuery(id+"F8.opExtrude","SWEPT_EDGE",EDGE,{"disambiguationData":[OSD([subQ2,subQ1,subQ0])]}),makeQuery(id+"F11.opExtrude","SWEPT_EDGE",EDGE,{"disambiguationData":[OSD([subQ2,subQ1,subQ0])]})]});}
            chamfer(context, id + "F22", {"entities" : qUnion([Q0]), "chamferType" : ChamferType.OFFSET_ANGLE, "width" : 10 * mm, "oppositeDirection" : false, "angle" : 42 * degree, "tangentPropagation" : true});
        }
        {
            var Q0;
            {var subQ0=sQuery(id+"F4.wireOp",EDGE,"E196");var subQ1=sQuery(id+"F4.wireOp",EDGE,"E179");var subQ2=sQuery(id+"F4.wireOp",EDGE,"E174");Q0=makeQuery(id+"F11.boolean.opBoolean","MERGE",EDGE,{"derivedFrom":[makeQuery(id+"F8.opExtrude","SWEPT_EDGE",EDGE,{"disambiguationData":[OSD([subQ2,subQ1,subQ0])]}),makeQuery(id+"F11.opExtrude","SWEPT_EDGE",EDGE,{"disambiguationData":[OSD([subQ2,subQ1,subQ0])]})]});}
            chamfer(context, id + "F23", {"entities" : qUnion([Q0]), "chamferType" : ChamferType.OFFSET_ANGLE, "width" : 10 * mm, "oppositeDirection" : false, "angle" : 42 * degree, "tangentPropagation" : true});
        }
        {
            var Q0;
            {var subQ0=sQuery(id+"F0.wireOp",EDGE,"E35.top");var subQ1=sQuery(id+"F0.wireOp",EDGE,"E34.MirrorC");var subQ2=makeQuery(id+"F0.imprint","INTERSECT",VERTEX,{"derivedFrom":[subQ1,subQ0]});Q0=makeQuery(id+"F0.imprint","IMPRINT",FACE,{"disambiguationData":[TD([[makeQuery(id+"F0.imprint","IMPRINT",EDGE,{"disambiguationData":[TD([[subQ2,1.0]])],"derivedFrom":subQ1}),1.0]])]});}
            var Q1;
            {var subQ0=sQuery(id+"F0.wireOp",EDGE,"E10");var subQ3=sQuery(id+"F0.wireOp",EDGE,"E1");var subQ5=makeQuery(id+"F0.imprint","INTERSECT",VERTEX,{"disambiguationData":[OD(0.0)],"derivedFrom":[subQ3,subQ0]});Q1=makeQuery(id+"F0.imprint","IMPRINT",FACE,{"disambiguationData":[TD([[makeQuery(id+"F0.imprint","IMPRINT",EDGE,{"disambiguationData":[TD([[subQ5,-1.0]])],"derivedFrom":subQ3}),-1.0]])]});}
            var Q2;
            {var subQ0=sQuery(id+"F0.wireOp",EDGE,"E36");var subQ1=sQuery(id+"F0.wireOp",EDGE,"E0.right");var subQ2=makeQuery(id+"F0.imprint","INTERSECT",VERTEX,{"derivedFrom":[subQ1,subQ0]});Q2=makeQuery(id+"F0.imprint","IMPRINT",FACE,{"disambiguationData":[TD([[makeQuery(id+"F0.imprint","IMPRINT",EDGE,{"disambiguationData":[TD([[subQ2,1.0]])],"derivedFrom":subQ1}),-1.0]])]});}
            var Q3;
            {var subQ1=sQuery(id+"F0.wireOp",EDGE,"E0.left");var subQ3=sQuery(id+"F0.wireOp",EDGE,"E2.MirrorCS");var subQ4=makeQuery(id+"F0.imprint","INTERSECT",VERTEX,{"disambiguationData":[OD(1.0)],"derivedFrom":[subQ1,subQ3]});Q3=makeQuery(id+"F0.imprint","IMPRINT",FACE,{"disambiguationData":[TD([[makeQuery(id+"F0.imprint","IMPRINT",EDGE,{"disambiguationData":[TD([[subQ4,-1.0]])],"derivedFrom":subQ3}),-1.0]])]});}
            var Q4;
            {var subQ1=sQuery(id+"F0.wireOp",EDGE,"E0.left");var subQ3=sQuery(id+"F0.wireOp",EDGE,"E3.MirrorCS");var subQ4=makeQuery(id+"F0.imprint","INTERSECT",VERTEX,{"derivedFrom":[subQ1,subQ3]});Q4=makeQuery(id+"F0.imprint","IMPRINT",FACE,{"disambiguationData":[TD([[makeQuery(id+"F0.imprint","IMPRINT",EDGE,{"disambiguationData":[TD([[subQ4,1.0]])],"derivedFrom":subQ3}),-1.0]])]});}
            var Q5;
            {var subQ0=sQuery(id+"F0.wireOp",EDGE,"E9");var subQ1=sQuery(id+"F0.wireOp",EDGE,"E0.right");var subQ2=makeQuery(id+"F0.imprint","INTERSECT",VERTEX,{"derivedFrom":[subQ1,subQ0]});Q5=makeQuery(id+"F0.imprint","IMPRINT",FACE,{"disambiguationData":[TD([[makeQuery(id+"F0.imprint","IMPRINT",EDGE,{"disambiguationData":[TD([[subQ2,-1.0]])],"derivedFrom":subQ1}),-1.0]])]});}
            var Q6;
            Q6=makeQuery(id+"F0.imprint","IMPRINT",FACE,{"disambiguationData":[TD([[makeQuery(id+"F0.imprint","IMPRINT",EDGE,{"derivedFrom":sQuery(id+"F0.wireOp",EDGE,"E23")}),1.0]])]});
            var Q7;
            Q7=makeQuery(id+"F0.imprint","IMPRINT",FACE,{"disambiguationData":[TD([[makeQuery(id+"F0.imprint","IMPRINT",EDGE,{"derivedFrom":sQuery(id+"F0.wireOp",EDGE,"E21")}),1.0]])]});
            var Q8;
            Q8=makeQuery(id+"F0.imprint","IMPRINT",FACE,{"disambiguationData":[TD([[makeQuery(id+"F0.imprint","IMPRINT",EDGE,{"derivedFrom":sQuery(id+"F0.wireOp",EDGE,"E22")}),1.0]])]});
            var Q9;
            Q9=makeQuery(id+"F0.imprint","IMPRINT",FACE,{"disambiguationData":[TD([[makeQuery(id+"F0.imprint","IMPRINT",EDGE,{"derivedFrom":sQuery(id+"F0.wireOp",EDGE,"E24.MirrorC")}),-1.0]])]});
            var Q10;
            Q10=makeQuery(id+"F0.imprint","IMPRINT",FACE,{"disambiguationData":[TD([[makeQuery(id+"F0.imprint","IMPRINT",EDGE,{"derivedFrom":sQuery(id+"F0.wireOp",EDGE,"E30.MirrorC")}),-1.0]])]});
            var Q11;
            Q11=makeQuery(id+"F0.imprint","IMPRINT",FACE,{"disambiguationData":[TD([[makeQuery(id+"F0.imprint","IMPRINT",EDGE,{"derivedFrom":sQuery(id+"F0.wireOp",EDGE,"E31.MirrorC")}),-1.0]])]});
            var Q12;
            Q12=makeQuery(id+"F0.imprint","IMPRINT",FACE,{"disambiguationData":[TD([[makeQuery(id+"F0.imprint","IMPRINT",EDGE,{"derivedFrom":sQuery(id+"F0.wireOp",EDGE,"E33.MirrorC")}),1.0]])]});
            var Q13;
            Q13=makeQuery(id+"F0.imprint","IMPRINT",FACE,{"disambiguationData":[TD([[makeQuery(id+"F0.imprint","IMPRINT",EDGE,{"derivedFrom":sQuery(id+"F0.wireOp",EDGE,"E32.MirrorC")}),-1.0]])]});
            var Q14;
            Q14=makeQuery(id+"F0.imprint","IMPRINT",FACE,{"disambiguationData":[TD([[makeQuery(id+"F0.imprint","IMPRINT",EDGE,{"derivedFrom":sQuery(id+"F0.wireOp",EDGE,"E19")}),1.0]])]});
            var Q15;
            Q15=makeQuery(id+"F0.imprint","IMPRINT",FACE,{"disambiguationData":[TD([[makeQuery(id+"F0.imprint","IMPRINT",EDGE,{"derivedFrom":sQuery(id+"F0.wireOp",EDGE,"E20")}),1.0]])]});
            var Q16;
            Q16=makeQuery(id+"F0.imprint","IMPRINT",FACE,{"disambiguationData":[TD([[makeQuery(id+"F0.imprint","IMPRINT",EDGE,{"derivedFrom":sQuery(id+"F0.wireOp",EDGE,"E17")}),1.0]])]});
            var Q17;
            Q17=makeQuery(id+"F0.imprint","IMPRINT",FACE,{"disambiguationData":[TD([[makeQuery(id+"F0.imprint","IMPRINT",EDGE,{"derivedFrom":sQuery(id+"F0.wireOp",EDGE,"E18")}),1.0]])]});
            var Q18;
            Q18=makeQuery(id+"F0.imprint","IMPRINT",FACE,{"disambiguationData":[TD([[makeQuery(id+"F0.imprint","IMPRINT",EDGE,{"derivedFrom":sQuery(id+"F0.wireOp",EDGE,"E16")}),1.0]])]});
            var Q19;
            Q19=makeQuery(id+"F0.imprint","IMPRINT",FACE,{"disambiguationData":[TD([[makeQuery(id+"F0.imprint","IMPRINT",EDGE,{"derivedFrom":sQuery(id+"F0.wireOp",EDGE,"E28.MirrorC")}),-1.0]])]});
            var Q20;
            Q20=makeQuery(id+"F0.imprint","IMPRINT",FACE,{"disambiguationData":[TD([[makeQuery(id+"F0.imprint","IMPRINT",EDGE,{"derivedFrom":sQuery(id+"F0.wireOp",EDGE,"E27.MirrorC")}),-1.0]])]});
            var Q21;
            Q21=makeQuery(id+"F0.imprint","IMPRINT",FACE,{"disambiguationData":[TD([[makeQuery(id+"F0.imprint","IMPRINT",EDGE,{"derivedFrom":sQuery(id+"F0.wireOp",EDGE,"E25.MirrorC")}),-1.0]])]});
            var Q22;
            Q22=makeQuery(id+"F0.imprint","IMPRINT",FACE,{"disambiguationData":[TD([[makeQuery(id+"F0.imprint","IMPRINT",EDGE,{"derivedFrom":sQuery(id+"F0.wireOp",EDGE,"E26.MirrorC")}),-1.0]])]});
            var Q23;
            Q23=makeQuery(id+"F0.imprint","IMPRINT",FACE,{"disambiguationData":[TD([[makeQuery(id+"F0.imprint","IMPRINT",EDGE,{"derivedFrom":sQuery(id+"F0.wireOp",EDGE,"E29.MirrorC")}),-1.0]])]});
            var Q24;
            {var subQ5=sQuery(id+"F0.wireOp",EDGE,"E7");Q24=makeQuery(id+"F0.imprint","IMPRINT",FACE,{"disambiguationData":[TD([[makeQuery(id+"F0.imprint","IMPRINT",EDGE,{"derivedFrom":subQ5}),-1.0]])]});}
            var Q25;
            {var subQ0=sQuery(id+"F0.wireOp",EDGE,"E37");var subQ1=sQuery(id+"F0.wireOp",EDGE,"E0.right");var subQ2=makeQuery(id+"F0.imprint","INTERSECT",VERTEX,{"derivedFrom":[subQ1,subQ0]});Q25=makeQuery(id+"F0.imprint","IMPRINT",FACE,{"disambiguationData":[TD([[makeQuery(id+"F0.imprint","IMPRINT",EDGE,{"disambiguationData":[TD([[subQ2,-1.0]])],"derivedFrom":subQ1}),-1.0]])]});}
            var Q26;
            {var subQ5=sQuery(id+"F0.wireOp",EDGE,"E6");Q26=makeQuery(id+"F0.imprint","IMPRINT",FACE,{"disambiguationData":[TD([[makeQuery(id+"F0.imprint","IMPRINT",EDGE,{"derivedFrom":subQ5}),1.0]])]});}
            var Q27;
            Q27=makeQuery(id+"F0.imprint","IMPRINT",FACE,{"disambiguationData":[TD([[makeQuery(id+"F0.imprint","IMPRINT",EDGE,{"derivedFrom":sQuery(id+"F0.wireOp",EDGE,"E46.MirrorC")}),-1.0]])]});
            var Q28;
            Q28=makeQuery(id+"F0.imprint","IMPRINT",FACE,{"disambiguationData":[TD([[makeQuery(id+"F0.imprint","IMPRINT",EDGE,{"derivedFrom":sQuery(id+"F0.wireOp",EDGE,"E45")}),1.0]])]});
            var Q29;
            {var subQ0=sQuery(id+"F0.wireOp",EDGE,"E47.MirrorC");var subQ1=sQuery(id+"F0.wireOp",EDGE,"E35.top");var subQ2=makeQuery(id+"F0.imprint","INTERSECT",VERTEX,{"disambiguationData":[OD(0.0)],"derivedFrom":[subQ1,subQ0]});Q29=makeQuery(id+"F0.imprint","IMPRINT",FACE,{"disambiguationData":[TD([[makeQuery(id+"F0.imprint","IMPRINT",EDGE,{"disambiguationData":[TD([[subQ2,-1.0]])],"derivedFrom":subQ1}),1.0]])]});}
            var Q30;
            {var subQ0=sQuery(id+"F0.wireOp",EDGE,"E48.MirrorC");var subQ1=sQuery(id+"F0.wireOp",EDGE,"E35.bottom");var subQ2=makeQuery(id+"F0.imprint","INTERSECT",VERTEX,{"disambiguationData":[OD(0.0)],"derivedFrom":[subQ1,subQ0]});Q30=makeQuery(id+"F0.imprint","IMPRINT",FACE,{"disambiguationData":[TD([[makeQuery(id+"F0.imprint","IMPRINT",EDGE,{"disambiguationData":[TD([[subQ2,-1.0]])],"derivedFrom":subQ1}),-1.0]])]});}
            var Q31;
            {var subQ0=sQuery(id+"F0.wireOp",EDGE,"E49.MirrorC");var subQ1=sQuery(id+"F0.wireOp",EDGE,"E35.top");var subQ2=makeQuery(id+"F0.imprint","INTERSECT",VERTEX,{"disambiguationData":[OD(0.0)],"derivedFrom":[subQ1,subQ0]});Q31=makeQuery(id+"F0.imprint","IMPRINT",FACE,{"disambiguationData":[TD([[makeQuery(id+"F0.imprint","IMPRINT",EDGE,{"disambiguationData":[TD([[subQ2,-1.0]])],"derivedFrom":subQ1}),1.0]])]});}
            var Q32;
            {var subQ0=sQuery(id+"F0.wireOp",EDGE,"E50.MirrorC");var subQ1=sQuery(id+"F0.wireOp",EDGE,"E35.top");var subQ2=makeQuery(id+"F0.imprint","INTERSECT",VERTEX,{"disambiguationData":[OD(0.0)],"derivedFrom":[subQ1,subQ0]});Q32=makeQuery(id+"F0.imprint","IMPRINT",FACE,{"disambiguationData":[TD([[makeQuery(id+"F0.imprint","IMPRINT",EDGE,{"disambiguationData":[TD([[subQ2,-1.0]])],"derivedFrom":subQ1}),1.0]])]});}
            var Q33;
            {var subQ0=sQuery(id+"F0.wireOp",EDGE,"E52.MirrorC");var subQ1=sQuery(id+"F0.wireOp",EDGE,"E35.bottom");var subQ2=makeQuery(id+"F0.imprint","INTERSECT",VERTEX,{"disambiguationData":[OD(0.0)],"derivedFrom":[subQ1,subQ0]});Q33=makeQuery(id+"F0.imprint","IMPRINT",FACE,{"disambiguationData":[TD([[makeQuery(id+"F0.imprint","IMPRINT",EDGE,{"disambiguationData":[TD([[subQ2,-1.0]])],"derivedFrom":subQ1}),-1.0]])]});}
            var Q34;
            {var subQ0=sQuery(id+"F0.wireOp",EDGE,"E51.MirrorC");var subQ1=sQuery(id+"F0.wireOp",EDGE,"E35.top");var subQ2=makeQuery(id+"F0.imprint","INTERSECT",VERTEX,{"disambiguationData":[OD(0.0)],"derivedFrom":[subQ1,subQ0]});Q34=makeQuery(id+"F0.imprint","IMPRINT",FACE,{"disambiguationData":[TD([[makeQuery(id+"F0.imprint","IMPRINT",EDGE,{"disambiguationData":[TD([[subQ2,-1.0]])],"derivedFrom":subQ1}),1.0]])]});}
            var Q35;
            {var subQ0=sQuery(id+"F0.wireOp",EDGE,"E35.left");var subQ1=sQuery(id+"F0.wireOp",EDGE,"E35.top");var subQ2=makeQuery(id+"F0.imprint","INTERSECT",VERTEX,{"derivedFrom":[subQ1,subQ0]});Q35=makeQuery(id+"F0.imprint","IMPRINT",FACE,{"disambiguationData":[TD([[makeQuery(id+"F0.imprint","IMPRINT",EDGE,{"disambiguationData":[TD([[subQ2,-1.0]])],"derivedFrom":subQ1}),1.0]])]});}
            var Q36;
            Q36=makeQuery(id+"F0.imprint","IMPRINT",FACE,{"disambiguationData":[TD([[makeQuery(id+"F0.imprint","IMPRINT",EDGE,{"derivedFrom":sQuery(id+"F0.wireOp",EDGE,"E54.MirrorC")}),-1.0]])]});
            var Q37;
            Q37=makeQuery(id+"F0.imprint","IMPRINT",FACE,{"disambiguationData":[TD([[makeQuery(id+"F0.imprint","IMPRINT",EDGE,{"derivedFrom":sQuery(id+"F0.wireOp",EDGE,"E55.MirrorC")}),1.0]])]});
            var Q38;
            Q38=makeQuery(id+"F0.imprint","IMPRINT",FACE,{"disambiguationData":[TD([[makeQuery(id+"F0.imprint","IMPRINT",EDGE,{"derivedFrom":sQuery(id+"F0.wireOp",EDGE,"E64.MirrorC")}),-1.0]])]});
            var Q39;
            Q39=makeQuery(id+"F0.imprint","IMPRINT",FACE,{"disambiguationData":[TD([[makeQuery(id+"F0.imprint","IMPRINT",EDGE,{"derivedFrom":sQuery(id+"F0.wireOp",EDGE,"E63.MirrorC")}),1.0]])]});
            var Q40;
            Q40=makeQuery(id+"F0.imprint","IMPRINT",FACE,{"disambiguationData":[TD([[makeQuery(id+"F0.imprint","IMPRINT",EDGE,{"derivedFrom":sQuery(id+"F0.wireOp",EDGE,"E62.MirrorC")}),1.0]])]});
            var Q41;
            Q41=makeQuery(id+"F0.imprint","IMPRINT",FACE,{"disambiguationData":[TD([[makeQuery(id+"F0.imprint","IMPRINT",EDGE,{"derivedFrom":sQuery(id+"F0.wireOp",EDGE,"E61.MirrorC")}),1.0]])]});
            var Q42;
            Q42=makeQuery(id+"F0.imprint","IMPRINT",FACE,{"disambiguationData":[TD([[makeQuery(id+"F0.imprint","IMPRINT",EDGE,{"derivedFrom":sQuery(id+"F0.wireOp",EDGE,"E60.MirrorC")}),1.0]])]});
            var Q43;
            Q43=makeQuery(id+"F0.imprint","IMPRINT",FACE,{"disambiguationData":[TD([[makeQuery(id+"F0.imprint","IMPRINT",EDGE,{"derivedFrom":sQuery(id+"F0.wireOp",EDGE,"E59.MirrorC")}),1.0]])]});
            var Q44;
            Q44=makeQuery(id+"F0.imprint","IMPRINT",FACE,{"disambiguationData":[TD([[makeQuery(id+"F0.imprint","IMPRINT",EDGE,{"derivedFrom":sQuery(id+"F0.wireOp",EDGE,"E57.MirrorC")}),1.0]])]});
            var Q45;
            Q45=makeQuery(id+"F0.imprint","IMPRINT",FACE,{"disambiguationData":[TD([[makeQuery(id+"F0.imprint","IMPRINT",EDGE,{"derivedFrom":sQuery(id+"F0.wireOp",EDGE,"E56.MirrorC")}),1.0]])]});
            var Q46;
            Q46=makeQuery(id+"F0.imprint","IMPRINT",FACE,{"disambiguationData":[TD([[makeQuery(id+"F0.imprint","IMPRINT",EDGE,{"derivedFrom":sQuery(id+"F0.wireOp",EDGE,"E58.MirrorC")}),1.0]])]});
            var Q47;
            Q47=makeQuery(id+"F0.imprint","IMPRINT",FACE,{"disambiguationData":[TD([[makeQuery(id+"F0.imprint","IMPRINT",EDGE,{"derivedFrom":sQuery(id+"F0.wireOp",EDGE,"E69.MirrorC")}),-1.0]])]});
            var Q48;
            Q48=makeQuery(id+"F0.imprint","IMPRINT",FACE,{"disambiguationData":[TD([[makeQuery(id+"F0.imprint","IMPRINT",EDGE,{"derivedFrom":sQuery(id+"F0.wireOp",EDGE,"E68.MirrorC")}),-1.0]])]});
            var Q49;
            Q49=makeQuery(id+"F0.imprint","IMPRINT",FACE,{"disambiguationData":[TD([[makeQuery(id+"F0.imprint","IMPRINT",EDGE,{"derivedFrom":sQuery(id+"F0.wireOp",EDGE,"E70.MirrorC")}),-1.0]])]});
            var Q50;
            Q50=makeQuery(id+"F0.imprint","IMPRINT",FACE,{"disambiguationData":[TD([[makeQuery(id+"F0.imprint","IMPRINT",EDGE,{"derivedFrom":sQuery(id+"F0.wireOp",EDGE,"E67.MirrorC")}),-1.0]])]});
            var Q51;
            Q51=makeQuery(id+"F0.imprint","IMPRINT",FACE,{"disambiguationData":[TD([[makeQuery(id+"F0.imprint","IMPRINT",EDGE,{"derivedFrom":sQuery(id+"F0.wireOp",EDGE,"E71.MirrorC")}),-1.0]])]});
            var Q52;
            Q52=makeQuery(id+"F0.imprint","IMPRINT",FACE,{"disambiguationData":[TD([[makeQuery(id+"F0.imprint","IMPRINT",EDGE,{"derivedFrom":sQuery(id+"F0.wireOp",EDGE,"E72.MirrorC")}),-1.0]])]});
            var Q53;
            Q53=makeQuery(id+"F0.imprint","IMPRINT",FACE,{"disambiguationData":[TD([[makeQuery(id+"F0.imprint","IMPRINT",EDGE,{"derivedFrom":sQuery(id+"F0.wireOp",EDGE,"E66.MirrorC")}),-1.0]])]});
            var Q54;
            Q54=makeQuery(id+"F0.imprint","IMPRINT",FACE,{"disambiguationData":[TD([[makeQuery(id+"F0.imprint","IMPRINT",EDGE,{"derivedFrom":sQuery(id+"F0.wireOp",EDGE,"E65.MirrorC")}),-1.0]])]});
            var Q55;
            Q55=makeQuery(id+"F0.imprint","IMPRINT",FACE,{"disambiguationData":[TD([[makeQuery(id+"F0.imprint","IMPRINT",EDGE,{"derivedFrom":sQuery(id+"F0.wireOp",EDGE,"E73.MirrorC")}),1.0]])]});
            extrude(context, id + "F24", {"entities" : qUnion([Q0, Q1, Q2, Q3, Q4, Q5, Q6, Q7, Q8, Q9, Q10, Q11, Q12, Q13, Q14, Q15, Q16, Q17, Q18, Q19, Q20, Q21, Q22, Q23, Q24, Q25, Q26, Q27, Q28, Q29, Q30, Q31, Q32, Q33, Q34, Q35, Q36, Q37, Q38, Q39, Q40, Q41, Q42, Q43, Q44, Q45, Q46, Q47, Q48, Q49, Q50, Q51, Q52, Q53, Q54, Q55]), "operationType" : NewBodyOperationType.REMOVE, "depth" : 25 * mm, "offsetDistance" : 25 * mm});
        }
        {
            var Q0;
            Q0=qCreatedBy(makeId("Top.planeOp"),FACE);
            var sketch = newSketch(context, id + "F25", { "sketchPlane" : qUnion([Q0])});
            skLineSegment(sketch, "E212.bottom", {"start": v(-365, -200) * mm, "end": v(365, -200) * mm});
            skLineSegment(sketch, "E212.top", {"start": v(-365, 200) * mm, "end": v(365, 200) * mm});
            skLineSegment(sketch, "E212.left", {"start": v(-365, -200) * mm, "end": v(-365, 200) * mm});
            skLineSegment(sketch, "E212.right", {"start": v(365, -200) * mm, "end": v(365, 200) * mm});
            skPoint(sketch, "E213", {"position": v(0, -200) * mm});
            skPoint(sketch, "E214", {"position": v(-182.5, -200) * mm});
            skPoint(sketch, "E215", {"position": v(182.5, -200) * mm});
            skPoint(sketch, "E216", {"position": v(-365, -50) * mm});
            skPoint(sketch, "E217", {"position": v(-365, 50) * mm});
            skPoint(sketch, "E218", {"position": v(-365, 0) * mm});
            skPoint(sketch, "E219", {"position": v(-365, -125) * mm});
            skPoint(sketch, "E220", {"position": v(-365, -162.5) * mm});
            skPoint(sketch, "E221", {"position": v(-365, -87.5) * mm});
            skLineSegment(sketch, "E222.bottom", {"start": v(-193, 0) * mm, "end": v(-172, 0) * mm});
            skLineSegment(sketch, "E222.right", {"start": v(0, 0) * mm, "end": v(0, -0.5) * mm});
            skLineSegment(sketch, "E223.right", {"start": v(0, -20) * mm, "end": v(0, -20.5) * mm});
            skLineSegment(sketch, "E224.right", {"start": v(0, -20) * mm, "end": v(0, -19.5) * mm});
            skPoint(sketch, "E225", {"position": v(-192.5, -200) * mm});
            skPoint(sketch, "E226", {"position": v(-172.5, -200) * mm});
            skPoint(sketch, "E227", {"position": v(-10, -200) * mm});
            skPoint(sketch, "E228", {"position": v(-365, -60) * mm});
            skPoint(sketch, "E229", {"position": v(-365, -40) * mm});
            skPoint(sketch, "E230", {"position": v(-365, 40) * mm});
            skPoint(sketch, "E231", {"position": v(-365, 60) * mm});
            skLineSegment(sketch, "E232.bottom", {"start": v(-365, -40) * mm, "end": v(-274.25, -40) * mm});
            skLineSegment(sketch, "E232.top", {"start": v(-365, -39.5) * mm, "end": v(-318.88, -39.5) * mm});
            skLineSegment(sketch, "E232.left", {"start": v(-365, -40) * mm, "end": v(-365, -39.5) * mm});
            skLineSegment(sketch, "E232.right", {"start": v(0, -40) * mm, "end": v(0, -39.5) * mm});
            skLineSegment(sketch, "E233.bottom", {"start": v(-193, 0) * mm, "end": v(0, 0) * mm});
            skLineSegment(sketch, "E233.right", {"start": v(0, 0) * mm, "end": v(0, 0.5) * mm});
            skLineSegment(sketch, "E234.bottom", {"start": v(-365, -40) * mm, "end": v(-318.88, -40) * mm});
            skLineSegment(sketch, "E234.top", {"start": v(-365, -40.5) * mm, "end": v(-318.88, -40.5) * mm});
            skLineSegment(sketch, "E234.left", {"start": v(-365, -40) * mm, "end": v(-365, -40.5) * mm});
            skLineSegment(sketch, "E234.right", {"start": v(0, -40) * mm, "end": v(0, -40.5) * mm});
            skLineSegment(sketch, "E235.bottom", {"start": v(-319.87, -60) * mm, "end": v(-273.25, -60) * mm});
            skLineSegment(sketch, "E235.top", {"start": v(-319.87, -59.5) * mm, "end": v(-228.62, -59.5) * mm});
            skLineSegment(sketch, "E235.left", {"start": v(-365, -60) * mm, "end": v(-365, -59.5) * mm});
            skLineSegment(sketch, "E235.right", {"start": v(0, -60) * mm, "end": v(0, -59.5) * mm});
            skLineSegment(sketch, "E236.bottom", {"start": v(-319.87, -60) * mm, "end": v(-228.62, -60) * mm});
            skLineSegment(sketch, "E236.top", {"start": v(-319.87, -60.5) * mm, "end": v(-228.62, -60.5) * mm});
            skLineSegment(sketch, "E236.left", {"start": v(-365, -60) * mm, "end": v(-365, -60.5) * mm});
            skLineSegment(sketch, "E236.right", {"start": v(0, -60) * mm, "end": v(0, -60.5) * mm});
            skLineSegment(sketch, "E237.left", {"start": v(-365, -87.5) * mm, "end": v(-365, -87) * mm});
            skLineSegment(sketch, "E237.right", {"start": v(0, -87.5) * mm, "end": v(0, -87) * mm});
            skLineSegment(sketch, "E238.left", {"start": v(-365, -87.5) * mm, "end": v(-365, -88) * mm});
            skLineSegment(sketch, "E238.right", {"start": v(0, -87.5) * mm, "end": v(0, -88) * mm});
            skLineSegment(sketch, "E239.left", {"start": v(-365, -125) * mm, "end": v(-365, -124.5) * mm});
            skLineSegment(sketch, "E239.right", {"start": v(0, -125) * mm, "end": v(0, -124.5) * mm});
            skLineSegment(sketch, "E240.left", {"start": v(-365, -125) * mm, "end": v(-365, -125.5) * mm});
            skLineSegment(sketch, "E240.right", {"start": v(0, -125) * mm, "end": v(0, -125.5) * mm});
            skLineSegment(sketch, "E241.left", {"start": v(-365, -162.5) * mm, "end": v(-365, -162) * mm});
            skLineSegment(sketch, "E241.right", {"start": v(0, -162.5) * mm, "end": v(0, -162) * mm});
            skLineSegment(sketch, "E242.left", {"start": v(-365, -162.5) * mm, "end": v(-365, -163) * mm});
            skLineSegment(sketch, "E242.right", {"start": v(0, -162.5) * mm, "end": v(0, -163) * mm});
            skLineSegment(sketch, "E243.bottom", {"start": v(-192.5, -200) * mm, "end": v(-193, -200) * mm});
            skLineSegment(sketch, "E243.top", {"start": v(-192.5, 0) * mm, "end": v(-193, 0) * mm});
            skLineSegment(sketch, "E243.left", {"start": v(-192.5, -200) * mm, "end": v(-192.5, -87) * mm});
            skLineSegment(sketch, "E243.right", {"start": v(-193, -200) * mm, "end": v(-193, -87) * mm});
            skLineSegment(sketch, "E244.bottom", {"start": v(-192.5, -200) * mm, "end": v(-192, -200) * mm});
            skLineSegment(sketch, "E244.top", {"start": v(-192.5, 0) * mm, "end": v(-192, 0) * mm});
            skLineSegment(sketch, "E244.right", {"start": v(-192, -200) * mm, "end": v(-192, -87) * mm});
            skLineSegment(sketch, "E245.bottom", {"start": v(-182.5, -200) * mm, "end": v(-183, -200) * mm});
            skLineSegment(sketch, "E245.top", {"start": v(-182.5, 0) * mm, "end": v(-183, 0) * mm});
            skLineSegment(sketch, "E245.left", {"start": v(-182.5, -200) * mm, "end": v(-182.5, -87) * mm});
            skLineSegment(sketch, "E245.right", {"start": v(-183, -200) * mm, "end": v(-183, -87.5) * mm});
            skLineSegment(sketch, "E246.bottom", {"start": v(-182.5, -200) * mm, "end": v(-182, -200) * mm});
            skLineSegment(sketch, "E246.top", {"start": v(-182.5, 0) * mm, "end": v(-182, 0) * mm});
            skLineSegment(sketch, "E246.right", {"start": v(-182, -200) * mm, "end": v(-182, -87) * mm});
            skLineSegment(sketch, "E247.bottom", {"start": v(-172.5, -200) * mm, "end": v(-173, -200) * mm});
            skLineSegment(sketch, "E247.top", {"start": v(-172.5, 0) * mm, "end": v(-173, 0) * mm});
            skLineSegment(sketch, "E247.left", {"start": v(-172.5, -200) * mm, "end": v(-172.5, -59.5) * mm});
            skLineSegment(sketch, "E248.bottom", {"start": v(-172.5, -200) * mm, "end": v(-172, -200) * mm});
            skLineSegment(sketch, "E248.top", {"start": v(-172.5, 0) * mm, "end": v(-172, 0) * mm});
            skLineSegment(sketch, "E248.left", {"start": v(-172.5, -163.05) * mm, "end": v(-172.5, -60) * mm});
            skLineSegment(sketch, "E248.right", {"start": v(-172, -200) * mm, "end": v(-172, -59.5) * mm});
            skLineSegment(sketch, "E249.bottom", {"start": v(0, -200) * mm, "end": v(-0.5, -200) * mm});
            skLineSegment(sketch, "E249.top", {"start": v(0, 0) * mm, "end": v(-0.5, 0) * mm});
            skLineSegment(sketch, "E249.left", {"start": v(0, -200) * mm, "end": v(0, 0) * mm});
            skLineSegment(sketch, "E249.right", {"start": v(-0.5, -200) * mm, "end": v(-0.5, 0) * mm});
            skLineSegment(sketch, "E250.bottom", {"start": v(-10, -200) * mm, "end": v(-9.5, -200) * mm});
            skLineSegment(sketch, "E250.top", {"start": v(-10, 0) * mm, "end": v(-9.5, 0) * mm});
            skLineSegment(sketch, "E250.left", {"start": v(-10, -200) * mm, "end": v(-10, 0) * mm});
            skLineSegment(sketch, "E250.right", {"start": v(-9.5, -200) * mm, "end": v(-9.5, 0) * mm});
            skLineSegment(sketch, "E251.bottom", {"start": v(-10, -200) * mm, "end": v(-10.5, -200) * mm});
            skLineSegment(sketch, "E251.top", {"start": v(-10, 0) * mm, "end": v(-10.5, 0) * mm});
            skLineSegment(sketch, "E251.right", {"start": v(-10.5, -200) * mm, "end": v(-10.5, 0) * mm});
            skLineSegment(sketch, "E252.top", {"start": v(-319.87, -50.5) * mm, "end": v(-318.87, -50.5) * mm});
            skLineSegment(sketch, "E252.left", {"start": v(-365, -50) * mm, "end": v(-365, -50.5) * mm});
            skLineSegment(sketch, "E252.right", {"start": v(0, -50) * mm, "end": v(0, -50.5) * mm});
            skLineSegment(sketch, "E253.bottom", {"start": v(-319.87, -50) * mm, "end": v(-318.87, -50) * mm});
            skLineSegment(sketch, "E253.top", {"start": v(-319.87, -49.5) * mm, "end": v(-318.87, -49.5) * mm});
            skLineSegment(sketch, "E253.left", {"start": v(-365, -50) * mm, "end": v(-365, -49.5) * mm});
            skLineSegment(sketch, "E253.right", {"start": v(0, -50) * mm, "end": v(0, -49.5) * mm});
            skLineSegment(sketch, "E254.trimOffspring", {"start": v(-318.87, -60.5) * mm, "end": v(-318.88, -39.5) * mm});
            skLineSegment(sketch, "E255.trimOffspring", {"start": v(-319.87, -60.5) * mm, "end": v(-319.88, -39.5) * mm});
            skLineSegment(sketch, "E256.trimOffspring", {"start": v(-319.37, -60.5) * mm, "end": v(-319.37, -39.5) * mm});
            skLineSegment(sketch, "E257.trimOffspring", {"start": v(-274.25, -60.5) * mm, "end": v(-274.25, -39.5) * mm});
            skLineSegment(sketch, "E258.trimOffspring", {"start": v(-273.25, -60.5) * mm, "end": v(-273.25, -39.5) * mm});
            skLineSegment(sketch, "E259.trimOffspring", {"start": v(-273.75, -60.5) * mm, "end": v(-273.75, -39.5) * mm});
            skLineSegment(sketch, "E260.trimOffspring", {"start": v(-227.62, -60.5) * mm, "end": v(-227.62, -39.5) * mm});
            skLineSegment(sketch, "E261.trimOffspring", {"start": v(-228.12, -60.5) * mm, "end": v(-228.12, -39.5) * mm});
            skLineSegment(sketch, "E262.trimOffspring", {"start": v(-228.62, -60.5) * mm, "end": v(-228.62, -39.5) * mm});
            skLineSegment(sketch, "E263.trimOffspring", {"start": v(-193, -20.5) * mm, "end": v(-172.5, -20.5) * mm});
            skLineSegment(sketch, "E264.trimOffspring", {"start": v(-193, -19.5) * mm, "end": v(-172, -19.5) * mm});
            skLineSegment(sketch, "E265.trimOffspring", {"start": v(-193, -0.5) * mm, "end": v(-172, -0.5) * mm});
            skLineSegment(sketch, "E266.trimOffspring", {"start": v(-193, -20) * mm, "end": v(-172, -20) * mm});
            skLineSegment(sketch, "E267.trimOffspring", {"start": v(-193, -163) * mm, "end": v(-172, -163) * mm});
            skLineSegment(sketch, "E268.trimOffspring", {"start": v(-193, -162.5) * mm, "end": v(-172, -162.5) * mm});
            skLineSegment(sketch, "E269.trimOffspring", {"start": v(-193, -162) * mm, "end": v(-172, -162) * mm});
            skLineSegment(sketch, "E270.trimOffspring", {"start": v(-193, -125) * mm, "end": v(-172, -125) * mm});
            skLineSegment(sketch, "E271.trimOffspring", {"start": v(-193, -124.5) * mm, "end": v(-172, -124.5) * mm});
            skLineSegment(sketch, "E272.trimOffspring", {"start": v(-193, -88) * mm, "end": v(-172, -88) * mm});
            skLineSegment(sketch, "E273.trimOffspring", {"start": v(-193, -87.5) * mm, "end": v(-172, -87.5) * mm});
            skLineSegment(sketch, "E274.trimOffspring", {"start": v(-193, -125.5) * mm, "end": v(-172, -125.5) * mm});
            skLineSegment(sketch, "E275.trimOffspring", {"start": v(-193, -87) * mm, "end": v(-172, -87) * mm});
            skLineSegment(sketch, "E276.trimOffspring", {"start": v(-137.37, -60.5) * mm, "end": v(-137.37, -39.5) * mm});
            skLineSegment(sketch, "E277.trimOffspring", {"start": v(-136.87, -60.5) * mm, "end": v(-136.87, -39.5) * mm});
            skLineSegment(sketch, "E278.trimOffspring", {"start": v(-91.25, -60.5) * mm, "end": v(-91.25, -40) * mm});
            skLineSegment(sketch, "E279.trimOffspring", {"start": v(-90.75, -60.5) * mm, "end": v(-90.75, -39.5) * mm});
            skLineSegment(sketch, "E280.trimOffspring", {"start": v(-91.75, -60.5) * mm, "end": v(-91.75, -39.5) * mm});
            skLineSegment(sketch, "E281.trimOffspring", {"start": v(-136.38, -60.5) * mm, "end": v(-136.38, -39.5) * mm});
            skLineSegment(sketch, "E282.trimOffspring", {"start": v(-91.25, -60.5) * mm, "end": v(-91.25, -39.5) * mm});
            skLineSegment(sketch, "E283.trimOffspring", {"start": v(-10.5, -19.5) * mm, "end": v(0, -19.5) * mm});
            skLineSegment(sketch, "E284.trimOffspring", {"start": v(-10.5, -0.5) * mm, "end": v(0, -0.5) * mm});
            skLineSegment(sketch, "E285.trimOffspring", {"start": v(-10.5, -20.5) * mm, "end": v(0, -20.5) * mm});
            skLineSegment(sketch, "E286.trimOffspring", {"start": v(-10.5, -20) * mm, "end": v(0, -20) * mm});
            skLineSegment(sketch, "E287.trimOffspring", {"start": v(-46.12, -60.5) * mm, "end": v(-46.12, -39.5) * mm});
            skLineSegment(sketch, "E288.trimOffspring", {"start": v(-10.5, -163) * mm, "end": v(0, -163) * mm});
            skLineSegment(sketch, "E289.trimOffspring", {"start": v(-10.5, -162) * mm, "end": v(0, -162) * mm});
            skLineSegment(sketch, "E290.trimOffspring", {"start": v(-45.62, -60.5) * mm, "end": v(-45.62, -39.5) * mm});
            skLineSegment(sketch, "E291.trimOffspring", {"start": v(-45.13, -60.5) * mm, "end": v(-45.13, -39.5) * mm});
            skLineSegment(sketch, "E292.trimOffspring", {"start": v(-10.5, -162.5) * mm, "end": v(0, -162.5) * mm});
            skLineSegment(sketch, "E293.trimOffspring", {"start": v(-10.5, -125.5) * mm, "end": v(0, -125.5) * mm});
            skLineSegment(sketch, "E294.trimOffspring", {"start": v(-10.5, -124.5) * mm, "end": v(0, -124.5) * mm});
            skLineSegment(sketch, "E295.trimOffspring", {"start": v(-10.5, -88) * mm, "end": v(0, -88) * mm});
            skLineSegment(sketch, "E296.trimOffspring", {"start": v(-10.5, -87.5) * mm, "end": v(0, -87.5) * mm});
            skLineSegment(sketch, "E297.trimOffspring", {"start": v(-10.5, -125) * mm, "end": v(0, -125) * mm});
            skLineSegment(sketch, "E298.trimOffspring", {"start": v(-10.5, -87) * mm, "end": v(0, -87) * mm});
            skLineSegment(sketch, "E299.MirrorCS", {"start": v(172.5, -200) * mm, "end": v(173, -200) * mm});
            skLineSegment(sketch, "E300.MirrorCS", {"start": v(182.5, -200) * mm, "end": v(183, -200) * mm});
            skLineSegment(sketch, "E301.MirrorCS", {"start": v(365, -40) * mm, "end": v(365, -39.5) * mm});
            skLineSegment(sketch, "E302.MirrorCS", {"start": v(182.5, -200) * mm, "end": v(182, -200) * mm});
            skLineSegment(sketch, "E303.MirrorCS", {"start": v(192.5, -200) * mm, "end": v(192, -200) * mm});
            skLineSegment(sketch, "E304.MirrorCS", {"start": v(172.5, -200) * mm, "end": v(172, -200) * mm});
            skLineSegment(sketch, "E305.MirrorCS", {"start": v(192.5, -200) * mm, "end": v(193, -200) * mm});
            skLineSegment(sketch, "E306.MirrorCS", {"start": v(365, -40) * mm, "end": v(365, -40.5) * mm});
            skLineSegment(sketch, "E307.MirrorCS", {"start": v(365, -50) * mm, "end": v(365, -49.5) * mm});
            skLineSegment(sketch, "E308.MirrorCS", {"start": v(365, -50) * mm, "end": v(365, -50.5) * mm});
            skLineSegment(sketch, "E309.MirrorCS", {"start": v(10, -200) * mm, "end": v(10.5, -200) * mm});
            skLineSegment(sketch, "E310.MirrorCS", {"start": v(365, -60) * mm, "end": v(365, -60.5) * mm});
            skLineSegment(sketch, "E311.MirrorCS", {"start": v(0, 0) * mm, "end": v(0.5, 0) * mm});
            skLineSegment(sketch, "E312.MirrorCS", {"start": v(10, -200) * mm, "end": v(9.5, -200) * mm});
            skLineSegment(sketch, "E313.MirrorCS", {"start": v(365, -60) * mm, "end": v(365, -59.5) * mm});
            skLineSegment(sketch, "E314.MirrorCS", {"start": v(10.5, -0.5) * mm, "end": v(0, -0.5) * mm});
            skLineSegment(sketch, "E315.MirrorCS", {"start": v(10, 0) * mm, "end": v(9.5, 0) * mm});
            skLineSegment(sketch, "E316.MirrorCS", {"start": v(10, 0) * mm, "end": v(10.5, 0) * mm});
            skLineSegment(sketch, "E317.MirrorCS", {"start": v(365, -125) * mm, "end": v(365, -125.5) * mm});
            skLineSegment(sketch, "E318.MirrorCS", {"start": v(0, -200) * mm, "end": v(0.5, -200) * mm});
            skLineSegment(sketch, "E319.MirrorCS", {"start": v(365, -87.5) * mm, "end": v(365, -87) * mm});
            skLineSegment(sketch, "E320.MirrorCS", {"start": v(365, -162.5) * mm, "end": v(365, -162) * mm});
            skLineSegment(sketch, "E321.MirrorCS", {"start": v(365, -87.5) * mm, "end": v(365, -88) * mm});
            skLineSegment(sketch, "E322.MirrorCS", {"start": v(365, -125) * mm, "end": v(365, -124.5) * mm});
            skLineSegment(sketch, "E323.MirrorCS", {"start": v(365, -162.5) * mm, "end": v(365, -163) * mm});
            skLineSegment(sketch, "E324.MirrorCS", {"start": v(10.5, -19.5) * mm, "end": v(0, -19.5) * mm});
            skLineSegment(sketch, "E325.MirrorCS", {"start": v(365, -40) * mm, "end": v(0, -40) * mm});
            skLineSegment(sketch, "E326.MirrorCS", {"start": v(318.87, -60.5) * mm, "end": v(318.87, -39.5) * mm});
            skLineSegment(sketch, "E327.MirrorCS", {"start": v(172, -200) * mm, "end": v(172, -39.5) * mm});
            skLineSegment(sketch, "E328.MirrorCS", {"start": v(192, -200) * mm, "end": v(192, -39.5) * mm});
            skLineSegment(sketch, "E329.MirrorCS", {"start": v(193, -88) * mm, "end": v(172, -88) * mm});
            skLineSegment(sketch, "E330.MirrorCS", {"start": v(45.62, -60.5) * mm, "end": v(45.62, -39.5) * mm});
            skLineSegment(sketch, "E331.MirrorCS", {"start": v(193, -125) * mm, "end": v(172, -125) * mm});
            skLineSegment(sketch, "E332.MirrorCS", {"start": v(193, -163) * mm, "end": v(172, -163) * mm});
            skLineSegment(sketch, "E333.MirrorCS", {"start": v(182.5, -200) * mm, "end": v(182.5, -40.5) * mm});
            skLineSegment(sketch, "E334.MirrorCS", {"start": v(10, -200) * mm, "end": v(10, 0) * mm});
            skLineSegment(sketch, "E335.MirrorCS", {"start": v(365, -40.5) * mm, "end": v(0, -40.5) * mm});
            skLineSegment(sketch, "E336.MirrorCS", {"start": v(273.25, -60.5) * mm, "end": v(273.25, -39.5) * mm});
            skLineSegment(sketch, "E337.MirrorCS", {"start": v(192.5, -200) * mm, "end": v(192.5, -40) * mm});
            skLineSegment(sketch, "E338.MirrorCS", {"start": v(172.5, -200) * mm, "end": v(172.5, -40.5) * mm});
            skLineSegment(sketch, "E339.MirrorCS", {"start": v(10.5, -125.5) * mm, "end": v(0, -125.5) * mm});
            skLineSegment(sketch, "E340.MirrorCS", {"start": v(193, -162.5) * mm, "end": v(172, -162.5) * mm});
            skLineSegment(sketch, "E341.MirrorCS", {"start": v(10.5, -163) * mm, "end": v(0, -163) * mm});
            skLineSegment(sketch, "E342.MirrorCS", {"start": v(183, -200) * mm, "end": v(183, -39.5) * mm});
            skLineSegment(sketch, "E343.MirrorCS", {"start": v(136.87, -60.5) * mm, "end": v(136.87, -39.5) * mm});
            skLineSegment(sketch, "E344.MirrorCS", {"start": v(365, -60) * mm, "end": v(0, -60) * mm});
            skLineSegment(sketch, "E345.MirrorCS", {"start": v(193, -87.5) * mm, "end": v(172, -87.5) * mm});
            skLineSegment(sketch, "E346.MirrorCS", {"start": v(45.12, -60.5) * mm, "end": v(45.12, -39.5) * mm});
            skLineSegment(sketch, "E347.MirrorCS", {"start": v(10.5, -88) * mm, "end": v(0, -88) * mm});
            skLineSegment(sketch, "E348.MirrorCS", {"start": v(365, -50) * mm, "end": v(0, -50) * mm});
            skLineSegment(sketch, "E349.MirrorCS", {"start": v(10.5, -20.5) * mm, "end": v(0, -20.5) * mm});
            skLineSegment(sketch, "E350.MirrorCS", {"start": v(228.12, -60.5) * mm, "end": v(228.12, -39.5) * mm});
            skLineSegment(sketch, "E351.MirrorCS", {"start": v(319.87, -60.5) * mm, "end": v(319.87, -39.5) * mm});
            skLineSegment(sketch, "E352.MirrorCS", {"start": v(91.25, -60.5) * mm, "end": v(91.25, -40) * mm});
            skLineSegment(sketch, "E353.MirrorCS", {"start": v(91.75, -60.5) * mm, "end": v(91.75, -39.5) * mm});
            skLineSegment(sketch, "E354.MirrorCS", {"start": v(193, -87) * mm, "end": v(172, -87) * mm});
            skLineSegment(sketch, "E355.MirrorCS", {"start": v(193, -124.5) * mm, "end": v(172, -124.5) * mm});
            skLineSegment(sketch, "E356.MirrorCS", {"start": v(10.5, -162.5) * mm, "end": v(0, -162.5) * mm});
            skLineSegment(sketch, "E357.MirrorCS", {"start": v(319.37, -60.5) * mm, "end": v(319.37, -39.5) * mm});
            skLineSegment(sketch, "E358.MirrorCS", {"start": v(193, -200) * mm, "end": v(193, -39.5) * mm});
            skLineSegment(sketch, "E359.MirrorCS", {"start": v(182.5, -200) * mm, "end": v(182.5, -39.5) * mm});
            skLineSegment(sketch, "E360.MirrorCS", {"start": v(273.75, -60.5) * mm, "end": v(273.75, -39.5) * mm});
            skLineSegment(sketch, "E361.MirrorCS", {"start": v(10.5, -125) * mm, "end": v(0, -125) * mm});
            skLineSegment(sketch, "E362.MirrorCS", {"start": v(10.5, -20) * mm, "end": v(0, -20) * mm});
            skLineSegment(sketch, "E363.MirrorCS", {"start": v(193, -125.5) * mm, "end": v(172, -125.5) * mm});
            skLineSegment(sketch, "E364.MirrorCS", {"start": v(173, -200) * mm, "end": v(173, -39.5) * mm});
            skLineSegment(sketch, "E365.MirrorCS", {"start": v(9.5, -200) * mm, "end": v(9.5, 0) * mm});
            skLineSegment(sketch, "E366.MirrorCS", {"start": v(10.5, -87.5) * mm, "end": v(0, -87.5) * mm});
            skLineSegment(sketch, "E367.MirrorCS", {"start": v(193, -162) * mm, "end": v(172, -162) * mm});
            skLineSegment(sketch, "E368.MirrorCS", {"start": v(365, -39.5) * mm, "end": v(0, -39.5) * mm});
            skLineSegment(sketch, "E369.MirrorCS", {"start": v(365, -49.5) * mm, "end": v(0, -49.5) * mm});
            skLineSegment(sketch, "E370.MirrorCS", {"start": v(90.75, -60.5) * mm, "end": v(90.75, -39.5) * mm});
            skPoint(sketch, "E371.MirrorP", {"position": v(365, 0) * mm});
            skLineSegment(sketch, "E372.MirrorCS", {"start": v(10.5, -124.5) * mm, "end": v(0, -124.5) * mm});
            skLineSegment(sketch, "E373.MirrorCS", {"start": v(365, -59.5) * mm, "end": v(0, -59.5) * mm});
            skLineSegment(sketch, "E374.MirrorCS", {"start": v(10.5, -162) * mm, "end": v(0, -162) * mm});
            skPoint(sketch, "E375.MirrorP", {"position": v(365, -60) * mm});
            skPoint(sketch, "E376.MirrorP", {"position": v(172.5, -200) * mm});
            skPoint(sketch, "E377.MirrorP", {"position": v(365, -50) * mm});
            skLineSegment(sketch, "E378.MirrorCS", {"start": v(365, -50.5) * mm, "end": v(0, -50.5) * mm});
            skPoint(sketch, "E379.MirrorP", {"position": v(365, -40) * mm});
            skLineSegment(sketch, "E380.MirrorCS", {"start": v(137.37, -60.5) * mm, "end": v(137.37, -39.5) * mm});
            skPoint(sketch, "E381.MirrorP", {"position": v(192.5, -200) * mm});
            skPoint(sketch, "E382.MirrorP", {"position": v(365, -87.5) * mm});
            skLineSegment(sketch, "E383.MirrorCS", {"start": v(228.62, -60.5) * mm, "end": v(228.62, -39.5) * mm});
            skLineSegment(sketch, "E384.MirrorCS", {"start": v(365, -60.5) * mm, "end": v(0, -60.5) * mm});
            skLineSegment(sketch, "E385.MirrorCS", {"start": v(46.12, -60.5) * mm, "end": v(46.12, -39.5) * mm});
            skLineSegment(sketch, "E386.MirrorCS", {"start": v(10.5, -200) * mm, "end": v(10.5, 0) * mm});
            skLineSegment(sketch, "E387.MirrorCS", {"start": v(0.5, -200) * mm, "end": v(0.5, 0) * mm});
            skLineSegment(sketch, "E388.MirrorCS", {"start": v(182, -200) * mm, "end": v(182, -39.5) * mm});
            skLineSegment(sketch, "E389.MirrorCS", {"start": v(91.25, -60.5) * mm, "end": v(91.25, -39.5) * mm});
            skLineSegment(sketch, "E390.MirrorCS", {"start": v(136.38, -60.5) * mm, "end": v(136.38, -39.5) * mm});
            skLineSegment(sketch, "E391.MirrorCS", {"start": v(192.5, -200) * mm, "end": v(192.5, -39.5) * mm});
            skLineSegment(sketch, "E392.MirrorCS", {"start": v(172.5, -200) * mm, "end": v(172.5, -39.5) * mm});
            skLineSegment(sketch, "E393.MirrorCS", {"start": v(227.62, -60.5) * mm, "end": v(227.62, -39.5) * mm});
            skLineSegment(sketch, "E394.MirrorCS", {"start": v(274.25, -60.5) * mm, "end": v(274.25, -39.5) * mm});
            skPoint(sketch, "E395.MirrorP", {"position": v(365, -162.5) * mm});
            skPoint(sketch, "E396.MirrorP", {"position": v(365, -125) * mm});
            skPoint(sketch, "E397.MirrorP", {"position": v(10, -200) * mm});
            skLineSegment(sketch, "E398.MirrorCS", {"start": v(10.5, -87) * mm, "end": v(0, -87) * mm});
            skLineSegment(sketch, "E399.MirrorCS", {"start": v(0, 50) * mm, "end": v(0, 50.5) * mm});
            skLineSegment(sketch, "E400.MirrorCS", {"start": v(0, 50) * mm, "end": v(0, 49.5) * mm});
            skLineSegment(sketch, "E401.MirrorCS", {"start": v(0, 40) * mm, "end": v(0, 40.5) * mm});
            skLineSegment(sketch, "E402.MirrorCS", {"start": v(0, 60) * mm, "end": v(0, 59.5) * mm});
            skLineSegment(sketch, "E403.MirrorCS", {"start": v(0, 20) * mm, "end": v(0, 20.5) * mm});
            skLineSegment(sketch, "E404.MirrorCS", {"start": v(0, 20) * mm, "end": v(0, 19.5) * mm});
            skLineSegment(sketch, "E405.MirrorCS", {"start": v(0, 40) * mm, "end": v(0, 39.5) * mm});
            skLineSegment(sketch, "E406.MirrorCS", {"start": v(0, 60) * mm, "end": v(0, 60.5) * mm});
            skLineSegment(sketch, "E407.MirrorCS", {"start": v(-365, 40) * mm, "end": v(-365, 40.5) * mm});
            skLineSegment(sketch, "E408.MirrorCS", {"start": v(-365, 50) * mm, "end": v(-365, 49.5) * mm});
            skLineSegment(sketch, "E409.MirrorCS", {"start": v(10.5, 0.5) * mm, "end": v(0, 0.5) * mm});
            skLineSegment(sketch, "E410.MirrorCS", {"start": v(-365, 60) * mm, "end": v(-365, 59.5) * mm});
            skLineSegment(sketch, "E411.MirrorCS", {"start": v(-365, 50) * mm, "end": v(-365, 50.5) * mm});
            skLineSegment(sketch, "E412.MirrorCS", {"start": v(-365, 60) * mm, "end": v(-365, 60.5) * mm});
            skLineSegment(sketch, "E413.MirrorCS", {"start": v(-365, 40) * mm, "end": v(-365, 39.5) * mm});
            skLineSegment(sketch, "E414.MirrorCS", {"start": v(-193, 0.5) * mm, "end": v(-172, 0.5) * mm});
            skLineSegment(sketch, "E415.MirrorCS", {"start": v(-10.5, 0.5) * mm, "end": v(0, 0.5) * mm});
            skLineSegment(sketch, "E416.MirrorCS", {"start": v(-10.5, 20.5) * mm, "end": v(0, 20.5) * mm});
            skLineSegment(sketch, "E417.MirrorCS", {"start": v(10.5, 20) * mm, "end": v(0, 20) * mm});
            skLineSegment(sketch, "E418.MirrorCS", {"start": v(-10.5, 20) * mm, "end": v(0, 20) * mm});
            skLineSegment(sketch, "E419.MirrorCS", {"start": v(10.5, 20.5) * mm, "end": v(0, 20.5) * mm});
            skLineSegment(sketch, "E420.MirrorCS", {"start": v(10.5, 19.5) * mm, "end": v(0, 19.5) * mm});
            skLineSegment(sketch, "E421.MirrorCS", {"start": v(-10.5, 19.5) * mm, "end": v(0, 19.5) * mm});
            skLineSegment(sketch, "E422.MirrorCS", {"start": v(-91.25, 60.5) * mm, "end": v(-91.25, 40) * mm});
            skLineSegment(sketch, "E423.MirrorCS", {"start": v(-137.37, 60.5) * mm, "end": v(-137.37, 39.5) * mm});
            skLineSegment(sketch, "E424.MirrorCS", {"start": v(-274.25, 60.5) * mm, "end": v(-274.25, 39.5) * mm});
            skLineSegment(sketch, "E425.MirrorCS", {"start": v(-318.87, 60.5) * mm, "end": v(-318.88, 39.5) * mm});
            skLineSegment(sketch, "E426.MirrorCS", {"start": v(-319.88, 40) * mm, "end": v(-228.62, 40) * mm});
            skLineSegment(sketch, "E427.MirrorCS", {"start": v(-136.87, 60.5) * mm, "end": v(-136.87, 39.5) * mm});
            skLineSegment(sketch, "E428.MirrorCS", {"start": v(-319.87, 60.5) * mm, "end": v(-319.88, 39.5) * mm});
            skLineSegment(sketch, "E429.MirrorCS", {"start": v(-273.25, 60.5) * mm, "end": v(-273.25, 39.5) * mm});
            skLineSegment(sketch, "E430.MirrorCS", {"start": v(-319.87, 50) * mm, "end": v(-318.87, 50) * mm});
            skLineSegment(sketch, "E431.MirrorCS", {"start": v(-90.75, 60.5) * mm, "end": v(-90.75, 39.5) * mm});
            skLineSegment(sketch, "E432.MirrorCS", {"start": v(-365, 60) * mm, "end": v(-318.87, 60) * mm});
            skLineSegment(sketch, "E433.MirrorCS", {"start": v(-193, 20.5) * mm, "end": v(-172, 20.5) * mm});
            skLineSegment(sketch, "E434.MirrorCS", {"start": v(-228.12, 60.5) * mm, "end": v(-228.12, 39.5) * mm});
            skLineSegment(sketch, "E435.MirrorCS", {"start": v(-45.62, 60.5) * mm, "end": v(-45.62, 39.5) * mm});
            skLineSegment(sketch, "E436.MirrorCS", {"start": v(-319.37, 40.5) * mm, "end": v(-228.62, 40.5) * mm});
            skLineSegment(sketch, "E437.MirrorCS", {"start": v(-319.37, 60.5) * mm, "end": v(-319.37, 39.5) * mm});
            skLineSegment(sketch, "E438.MirrorCS", {"start": v(-365, 59.5) * mm, "end": v(-318.87, 59.5) * mm});
            skLineSegment(sketch, "E439.MirrorCS", {"start": v(-273.75, 60.5) * mm, "end": v(-273.75, 39.5) * mm});
            skLineSegment(sketch, "E440.MirrorCS", {"start": v(-91.75, 60.5) * mm, "end": v(-91.75, 39.5) * mm});
            skLineSegment(sketch, "E441.MirrorCS", {"start": v(-193, 20) * mm, "end": v(-172, 20) * mm});
            skLineSegment(sketch, "E442.MirrorCS", {"start": v(-319.87, 49.5) * mm, "end": v(-318.87, 49.5) * mm});
            skLineSegment(sketch, "E443.MirrorCS", {"start": v(-227.62, 60.5) * mm, "end": v(-227.62, 39.5) * mm});
            skLineSegment(sketch, "E444.MirrorCS", {"start": v(-45.13, 60.5) * mm, "end": v(-45.13, 39.5) * mm});
            skLineSegment(sketch, "E445.MirrorCS", {"start": v(-228.62, 60.5) * mm, "end": v(-228.62, 39.5) * mm});
            skLineSegment(sketch, "E446.MirrorCS", {"start": v(-46.12, 60.5) * mm, "end": v(-46.12, 39.5) * mm});
            skLineSegment(sketch, "E447.MirrorCS", {"start": v(-365, 60.5) * mm, "end": v(-318.87, 60.5) * mm});
            skLineSegment(sketch, "E448.MirrorCS", {"start": v(-91.25, 60.5) * mm, "end": v(-91.25, 39.5) * mm});
            skLineSegment(sketch, "E449.MirrorCS", {"start": v(-319.88, 39.5) * mm, "end": v(-273.25, 39.5) * mm});
            skLineSegment(sketch, "E450.MirrorCS", {"start": v(-319.37, 40) * mm, "end": v(-273.25, 40) * mm});
            skLineSegment(sketch, "E451.MirrorCS", {"start": v(-136.38, 60.5) * mm, "end": v(-136.38, 39.5) * mm});
            skLineSegment(sketch, "E452.MirrorCS", {"start": v(-319.87, 50.5) * mm, "end": v(-318.87, 50.5) * mm});
            skLineSegment(sketch, "E453.MirrorCS", {"start": v(-365, 60) * mm, "end": v(-274.25, 60) * mm});
            skLineSegment(sketch, "E454.MirrorCS", {"start": v(-193, 19.5) * mm, "end": v(-172, 19.5) * mm});
            skLineSegment(sketch, "E455.MirrorCS", {"start": v(0, 60.5) * mm, "end": v(0, 0) * mm});
            skLineSegment(sketch, "E456.MirrorCS", {"start": v(-193, 20.5) * mm, "end": v(-172.5, 20.5) * mm});
            skLineSegment(sketch, "E457.MirrorCS", {"start": v(-319.88, 40) * mm, "end": v(-273.25, 40) * mm});
            skLineSegment(sketch, "E458.MirrorCS", {"start": v(10.5, 40) * mm, "end": v(0, 40) * mm});
            skLineSegment(sketch, "E459.MirrorCS", {"start": v(10.5, 60) * mm, "end": v(0, 60) * mm});
            skLineSegment(sketch, "E460.MirrorCS", {"start": v(-319.88, 40.5) * mm, "end": v(-273.25, 40.5) * mm});
            skLineSegment(sketch, "E461.MirrorCS", {"start": v(10.5, 50) * mm, "end": v(0, 50) * mm});
            skLineSegment(sketch, "E462.MirrorCS", {"start": v(-365, 59.5) * mm, "end": v(-274.25, 59.5) * mm});
            skLineSegment(sketch, "E463.MirrorCS", {"start": v(-365, 60.5) * mm, "end": v(-274.25, 60.5) * mm});
            skLineSegment(sketch, "E464.MirrorCS", {"start": v(-319.88, 39.5) * mm, "end": v(-228.62, 39.5) * mm});
            skLineSegment(sketch, "E465.MirrorCS", {"start": v(10.5, 49.5) * mm, "end": v(0, 49.5) * mm});
            skLineSegment(sketch, "E466.MirrorCS", {"start": v(10.5, 50.5) * mm, "end": v(0, 50.5) * mm});
            skLineSegment(sketch, "E467.MirrorCS", {"start": v(10.5, 59.5) * mm, "end": v(0, 59.5) * mm});
            skLineSegment(sketch, "E468.MirrorCS", {"start": v(10.5, 39.5) * mm, "end": v(0, 39.5) * mm});
            skLineSegment(sketch, "E469.MirrorCS", {"start": v(10.5, 60.5) * mm, "end": v(0, 60.5) * mm});
            skLineSegment(sketch, "E470.MirrorCS", {"start": v(-365, 60) * mm, "end": v(-319.37, 60) * mm});
            skLineSegment(sketch, "E471.MirrorCS", {"start": v(-319.87, 50) * mm, "end": v(-319.37, 50) * mm});
            skLineSegment(sketch, "E472.MirrorCS", {"start": v(10.5, 40.5) * mm, "end": v(0, 40.5) * mm});
            skLineSegment(sketch, "E473.trimOffspring", {"start": v(-10.5, 60.5) * mm, "end": v(-10.5, 0) * mm});
            skLineSegment(sketch, "E474.trimOffspring", {"start": v(-10, 60.5) * mm, "end": v(-10, 0) * mm});
            skLineSegment(sketch, "E475.trimOffspring", {"start": v(-0.5, 60.5) * mm, "end": v(-0.5, 0) * mm});
            skLineSegment(sketch, "E476.trimOffspring", {"start": v(-9.5, 60.5) * mm, "end": v(-9.5, 0) * mm});
            skLineSegment(sketch, "E477.trimOffspring", {"start": v(0.5, 60.5) * mm, "end": v(0.5, 0) * mm});
            skLineSegment(sketch, "E478.trimOffspring", {"start": v(10.5, 60.5) * mm, "end": v(10.5, 49.5) * mm});
            skLineSegment(sketch, "E479.trimOffspring", {"start": v(10, 60.5) * mm, "end": v(10, 49.5) * mm});
            skLineSegment(sketch, "E480.trimOffspring", {"start": v(9.5, 60.5) * mm, "end": v(9.5, 49.5) * mm});
            skLineSegment(sketch, "E481.trimOffspring", {"start": v(-173, 60.5) * mm, "end": v(-173, 49.5) * mm});
            skLineSegment(sketch, "E482.trimOffspring", {"start": v(-172.5, 60.5) * mm, "end": v(-172.5, 50) * mm});
            skLineSegment(sketch, "E483.trimOffspring", {"start": v(-172, 60.5) * mm, "end": v(-172, 49.5) * mm});
            skLineSegment(sketch, "E484.trimOffspring", {"start": v(-172.5, 60.5) * mm, "end": v(-172.5, 49.5) * mm});
            skPoint(sketch, "E485.orphan", {"position": v(365, 60.5) * mm});
            skPoint(sketch, "E486.orphan", {"position": v(365, 59.5) * mm});
            skPoint(sketch, "E487.orphan", {"position": v(365, 60) * mm});
            skPoint(sketch, "E488.orphan", {"position": v(365, 40) * mm});
            skPoint(sketch, "E489.orphan", {"position": v(365, 39.5) * mm});
            skPoint(sketch, "E490.orphan", {"position": v(365, 49.5) * mm});
            skPoint(sketch, "E491.orphan", {"position": v(365, 50) * mm});
            skPoint(sketch, "E492.orphan", {"position": v(365, 50.5) * mm});
            skPoint(sketch, "E493.orphan", {"position": v(365, 40.5) * mm});
            skPoint(sketch, "E494.orphan", {"position": v(0, 200) * mm});
            skLineSegment(sketch, "E495.trimOffspring", {"start": v(-10.5, 0) * mm, "end": v(0, 0) * mm});
            skLineSegment(sketch, "E496.trimOffspring", {"start": v(-318.88, -39.5) * mm, "end": v(-227.62, -39.5) * mm});
            skLineSegment(sketch, "E497.trimOffspring", {"start": v(-318.88, -40.5) * mm, "end": v(-227.62, -40.5) * mm});
            skLineSegment(sketch, "E498.trimOffspring", {"start": v(-274.25, -40) * mm, "end": v(-227.62, -40) * mm});
            skLineSegment(sketch, "E499.trimOffspring", {"start": v(-274.25, -49.5) * mm, "end": v(-273.25, -49.5) * mm});
            skLineSegment(sketch, "E500.trimOffspring", {"start": v(-274.25, -50) * mm, "end": v(-273.25, -50) * mm});
            skLineSegment(sketch, "E501.trimOffspring", {"start": v(-228.62, -60.5) * mm, "end": v(-192, -60.5) * mm});
            skLineSegment(sketch, "E502.trimOffspring", {"start": v(-228.62, -60) * mm, "end": v(-192, -60) * mm});
            skLineSegment(sketch, "E503.trimOffspring", {"start": v(-228.62, -59.5) * mm, "end": v(-192, -59.5) * mm});
            skLineSegment(sketch, "E504.trimOffspring", {"start": v(-228.62, -60) * mm, "end": v(-192.5, -60) * mm});
            skLineSegment(sketch, "E505.trimOffspring", {"start": v(-228.62, -50.5) * mm, "end": v(-227.62, -50.5) * mm});
            skLineSegment(sketch, "E506.trimOffspring", {"start": v(-228.62, -50) * mm, "end": v(-227.62, -50) * mm});
            skLineSegment(sketch, "E507.trimOffspring", {"start": v(-193, -50.5) * mm, "end": v(0, -50.5) * mm});
            skLineSegment(sketch, "E508.trimOffspring", {"start": v(-193, -39.5) * mm, "end": v(-182, -39.5) * mm});
            skLineSegment(sketch, "E509.trimOffspring", {"start": v(-193, -40) * mm, "end": v(-182, -40) * mm});
            skLineSegment(sketch, "E510.trimOffspring", {"start": v(-193, -49.5) * mm, "end": v(0, -49.5) * mm});
            skLineSegment(sketch, "E511.trimOffspring", {"start": v(-228.62, -49.5) * mm, "end": v(-227.62, -49.5) * mm});
            skLineSegment(sketch, "E512.trimOffspring", {"start": v(-193, -50) * mm, "end": v(0, -50) * mm});
            skLineSegment(sketch, "E513.trimOffspring", {"start": v(-193, -40.5) * mm, "end": v(-182, -40.5) * mm});
            skLineSegment(sketch, "E514.trimOffspring", {"start": v(-193, -40.5) * mm, "end": v(-193, 0) * mm});
            skLineSegment(sketch, "E515.trimOffspring", {"start": v(-192.5, -40.5) * mm, "end": v(-192.5, 0) * mm});
            skLineSegment(sketch, "E516.trimOffspring", {"start": v(-192, -40.5) * mm, "end": v(-192, 0) * mm});
            skLineSegment(sketch, "E517.trimOffspring", {"start": v(-183, -60.5) * mm, "end": v(0, -60.5) * mm});
            skLineSegment(sketch, "E518.trimOffspring", {"start": v(-183, -59.5) * mm, "end": v(0, -59.5) * mm});
            skLineSegment(sketch, "E519.trimOffspring", {"start": v(-183, -60) * mm, "end": v(0, -60) * mm});
            skLineSegment(sketch, "E520.trimOffspring", {"start": v(-172.5, -50.5) * mm, "end": v(-172.5, -39.5) * mm});
            skLineSegment(sketch, "E521.trimOffspring", {"start": v(-172.5, -40) * mm, "end": v(0, -40) * mm});
            skLineSegment(sketch, "E522.trimOffspring", {"start": v(-173, -40.5) * mm, "end": v(0, -40.5) * mm});
            skLineSegment(sketch, "E523.trimOffspring", {"start": v(-172, -50.5) * mm, "end": v(-172, -39.5) * mm});
            skLineSegment(sketch, "E524.trimOffspring", {"start": v(-173, -40) * mm, "end": v(0, -40) * mm});
            skLineSegment(sketch, "E525.trimOffspring", {"start": v(-172.5, -39.5) * mm, "end": v(0, -39.5) * mm});
            skLineSegment(sketch, "E526.trimOffspring", {"start": v(-192.5, -60.5) * mm, "end": v(-192.5, -50) * mm});
            skLineSegment(sketch, "E527.trimOffspring", {"start": v(-182.5, -60.5) * mm, "end": v(-182.5, 0) * mm});
            skLineSegment(sketch, "E528.trimOffspring", {"start": v(-172.5, -20.5) * mm, "end": v(-172.5, 0) * mm});
            skLineSegment(sketch, "E529.trimOffspring", {"start": v(-193, -60.5) * mm, "end": v(-193, -49.5) * mm});
            skLineSegment(sketch, "E530.trimOffspring", {"start": v(-192.5, -60.5) * mm, "end": v(-192.5, -49.5) * mm});
            skLineSegment(sketch, "E531.trimOffspring", {"start": v(-192, -60.5) * mm, "end": v(-192, -49.5) * mm});
            skLineSegment(sketch, "E532.trimOffspring", {"start": v(-183, -60.5) * mm, "end": v(-183, 0) * mm});
            skLineSegment(sketch, "E533.trimOffspring", {"start": v(-182, -60.5) * mm, "end": v(-182, 0) * mm});
            skLineSegment(sketch, "E534.MirrorCS", {"start": v(-173, -200) * mm, "end": v(-173, -59.5) * mm});
            skLineSegment(sketch, "E535.trimOffspring", {"start": v(-173, -50.5) * mm, "end": v(-173, -39.5) * mm});
            skLineSegment(sketch, "E536.trimOffspring", {"start": v(-172, -20) * mm, "end": v(-172, 0) * mm});
            skLineSegment(sketch, "E537.MirrorCS", {"start": v(-172, -39.5) * mm, "end": v(-173, -39.5) * mm});
            skLineSegment(sketch, "E538.trimOffspring", {"start": v(-173, -20.5) * mm, "end": v(-173, 0) * mm});
            skLineSegment(sketch, "E539.MirrorCS", {"start": v(-172, -40.5) * mm, "end": v(-172, -39.5) * mm});
            skLineSegment(sketch, "E540.MirrorCS", {"start": v(-172, -20.5) * mm, "end": v(-192.5, -20.5) * mm});
            skLineSegment(sketch, "E541.trimOffspring", {"start": v(-182, -39.5) * mm, "end": v(-183, -39.5) * mm});
            skLineSegment(sketch, "E542.trimOffspring", {"start": v(-172, -20.5) * mm, "end": v(-172, 0) * mm});
            skPoint(sketch, "E543.orphan", {"position": v(-365, 39.5) * mm});
            skLineSegment(sketch, "E544.trimOffspring", {"start": v(-274.25, 60) * mm, "end": v(-228.12, 60) * mm});
            skLineSegment(sketch, "E545.trimOffspring", {"start": v(-274.25, 50) * mm, "end": v(-273.25, 50) * mm});
            skPoint(sketch, "E546.orphan", {"position": v(-365, 40.5) * mm});
            skLineSegment(sketch, "E547.trimOffspring", {"start": v(-228.62, 50) * mm, "end": v(-227.62, 50) * mm});
            skLineSegment(sketch, "E548.trimOffspring", {"start": v(-228.62, 40) * mm, "end": v(-193, 40) * mm});
            skLineSegment(sketch, "E549.trimOffspring", {"start": v(-228.62, 50) * mm, "end": v(-228.12, 50) * mm});
            skPoint(sketch, "E550.orphan", {"position": v(-365, 49.5) * mm});
            skPoint(sketch, "E551.orphan", {"position": v(-365, 50.5) * mm});
            skLineSegment(sketch, "E552.trimOffspring", {"start": v(-274.25, 59.5) * mm, "end": v(-227.62, 59.5) * mm});
            skLineSegment(sketch, "E553.trimOffspring", {"start": v(-274.25, 49.5) * mm, "end": v(-273.25, 49.5) * mm});
            skLineSegment(sketch, "E554.trimOffspring", {"start": v(-274.25, 50.5) * mm, "end": v(-273.25, 50.5) * mm});
            skLineSegment(sketch, "E555.trimOffspring", {"start": v(-274.25, 60) * mm, "end": v(-227.62, 60) * mm});
            skLineSegment(sketch, "E556.trimOffspring", {"start": v(-274.25, 60.5) * mm, "end": v(-228.12, 60.5) * mm});
            skLineSegment(sketch, "E557.trimOffspring", {"start": v(-228.62, 49.5) * mm, "end": v(-227.62, 49.5) * mm});
            skLineSegment(sketch, "E558.trimOffspring", {"start": v(-228.62, 40) * mm, "end": v(-192, 40) * mm});
            skLineSegment(sketch, "E559.trimOffspring", {"start": v(-228.62, 39.5) * mm, "end": v(-192, 39.5) * mm});
            skLineSegment(sketch, "E560.trimOffspring", {"start": v(-228.62, 40.5) * mm, "end": v(-192, 40.5) * mm});
            skLineSegment(sketch, "E561.trimOffspring", {"start": v(-228.62, 50.5) * mm, "end": v(-228.12, 50.5) * mm});
            skLineSegment(sketch, "E562.trimOffspring", {"start": v(-274.25, 60.5) * mm, "end": v(-227.62, 60.5) * mm});
            skLineSegment(sketch, "E563.trimOffspring", {"start": v(-228.62, 49.5) * mm, "end": v(-228.12, 49.5) * mm});
            skLineSegment(sketch, "E564.trimOffspring", {"start": v(-228.62, 50.5) * mm, "end": v(-227.62, 50.5) * mm});
            skLineSegment(sketch, "E565.trimOffspring", {"start": v(-193, 49.5) * mm, "end": v(0, 49.5) * mm});
            skLineSegment(sketch, "E566.trimOffspring", {"start": v(-193, 50.5) * mm, "end": v(0, 50.5) * mm});
            skLineSegment(sketch, "E567.trimOffspring", {"start": v(-193, 50) * mm, "end": v(0, 50) * mm});
            skLineSegment(sketch, "E568.trimOffspring", {"start": v(-193, 49.5) * mm, "end": v(-173, 49.5) * mm});
            skLineSegment(sketch, "E569.trimOffspring", {"start": v(-193, 50) * mm, "end": v(-172, 50) * mm});
            skLineSegment(sketch, "E570.trimOffspring", {"start": v(-193, 50.5) * mm, "end": v(-172, 50.5) * mm});
            skLineSegment(sketch, "E571.trimOffspring", {"start": v(-193, 50.5) * mm, "end": v(-193, 39.5) * mm});
            skLineSegment(sketch, "E572.trimOffspring", {"start": v(-192.5, 50.5) * mm, "end": v(-192.5, 39.5) * mm});
            skLineSegment(sketch, "E573.trimOffspring", {"start": v(-183, 39.5) * mm, "end": v(-172.5, 39.5) * mm});
            skLineSegment(sketch, "E574.trimOffspring", {"start": v(-192, 20.5) * mm, "end": v(-192, 0) * mm});
            skLineSegment(sketch, "E575.trimOffspring", {"start": v(-183, 40) * mm, "end": v(-172, 40) * mm});
            skLineSegment(sketch, "E576.trimOffspring", {"start": v(-183, 39.5) * mm, "end": v(-172, 39.5) * mm});
            skLineSegment(sketch, "E577.trimOffspring", {"start": v(-193, 20.5) * mm, "end": v(-193, 0) * mm});
            skLineSegment(sketch, "E578.trimOffspring", {"start": v(-192.5, 20.5) * mm, "end": v(-192.5, 0) * mm});
            skLineSegment(sketch, "E579.trimOffspring", {"start": v(-182.5, 20.5) * mm, "end": v(-182.5, 0) * mm});
            skLineSegment(sketch, "E580.trimOffspring", {"start": v(-183, 20.5) * mm, "end": v(-183, 0) * mm});
            skLineSegment(sketch, "E581.trimOffspring", {"start": v(-182, 20.5) * mm, "end": v(-182, 0) * mm});
            skLineSegment(sketch, "E582.trimOffspring", {"start": v(-183, 40.5) * mm, "end": v(-172, 40.5) * mm});
            skLineSegment(sketch, "E583.trimOffspring", {"start": v(-192, 50.5) * mm, "end": v(-192, 39.5) * mm});
            skLineSegment(sketch, "E584.trimOffspring", {"start": v(-173, 59.5) * mm, "end": v(-9.5, 59.5) * mm});
            skLineSegment(sketch, "E585.trimOffspring", {"start": v(-173, 40.5) * mm, "end": v(-173, 0) * mm});
            skLineSegment(sketch, "E586.trimOffspring", {"start": v(-172.5, 40.5) * mm, "end": v(-172.5, 0) * mm});
            skLineSegment(sketch, "E587.trimOffspring", {"start": v(-173, 60) * mm, "end": v(-10, 60) * mm});
            skLineSegment(sketch, "E588.trimOffspring", {"start": v(-183, 40) * mm, "end": v(0, 40) * mm});
            skLineSegment(sketch, "E589.trimOffspring", {"start": v(-172, 40.5) * mm, "end": v(-172, 0.5) * mm});
            skLineSegment(sketch, "E590.trimOffspring", {"start": v(-137.37, 49.5) * mm, "end": v(0, 49.5) * mm});
            skLineSegment(sketch, "E591.trimOffspring", {"start": v(-137.37, 39.5) * mm, "end": v(0, 39.5) * mm});
            skLineSegment(sketch, "E592.trimOffspring", {"start": v(-183, 40) * mm, "end": v(-172.5, 40) * mm});
            skLineSegment(sketch, "E593.trimOffspring", {"start": v(-137.37, 40.5) * mm, "end": v(0, 40.5) * mm});
            skLineSegment(sketch, "E594.trimOffspring", {"start": v(-137.37, 50.5) * mm, "end": v(-136.38, 50.5) * mm});
            skLineSegment(sketch, "E595.trimOffspring", {"start": v(-137.37, 40) * mm, "end": v(0, 40) * mm});
            skLineSegment(sketch, "E596.trimOffspring", {"start": v(-183, 50.5) * mm, "end": v(-183, 39.5) * mm});
            skLineSegment(sketch, "E597.trimOffspring", {"start": v(-182, 50.5) * mm, "end": v(-182, 39.5) * mm});
            skLineSegment(sketch, "E598.trimOffspring", {"start": v(-182.5, 50.5) * mm, "end": v(-182.5, 39.5) * mm});
            skLineSegment(sketch, "E599.trimOffspring", {"start": v(-173, 59.5) * mm, "end": v(-136.38, 59.5) * mm});
            skLineSegment(sketch, "E600.trimOffspring", {"start": v(-173, 60.5) * mm, "end": v(-9.5, 60.5) * mm});
            skLineSegment(sketch, "E601.trimOffspring", {"start": v(-91.75, 50) * mm, "end": v(0, 50) * mm});
            skLineSegment(sketch, "E602.trimOffspring", {"start": v(-91.75, 50.5) * mm, "end": v(0, 50.5) * mm});
            skLineSegment(sketch, "E603.trimOffspring", {"start": v(-91.75, 59.5) * mm, "end": v(-9.5, 59.5) * mm});
            skLineSegment(sketch, "E604.trimOffspring", {"start": v(-91.75, 60) * mm, "end": v(-9.5, 60) * mm});
            skLineSegment(sketch, "E605.trimOffspring", {"start": v(-91.75, 60.5) * mm, "end": v(-9.5, 60.5) * mm});
            skLineSegment(sketch, "E606.trimOffspring", {"start": v(-173, 60) * mm, "end": v(-136.38, 60) * mm});
            skLineSegment(sketch, "E607.trimOffspring", {"start": v(-173, 60.5) * mm, "end": v(-136.38, 60.5) * mm});
            skLineSegment(sketch, "E608.trimOffspring", {"start": v(-173, 60) * mm, "end": v(-9.5, 60) * mm});
            skPoint(sketch, "E609.orphan", {"position": v(-172.5, -163) * mm});
            skPoint(sketch, "E610.orphan", {"position": v(-172.5, -125.5) * mm});
            skPoint(sketch, "E611.orphan", {"position": v(-172.5, -124.5) * mm});
            skPoint(sketch, "E612.orphan", {"position": v(-172.5, 20.5) * mm});
            skPoint(sketch, "E613.orphan", {"position": v(172.5, -125.5) * mm});
            skPoint(sketch, "E614.orphan", {"position": v(172.5, -124.5) * mm});
            skPoint(sketch, "E615.orphan", {"position": v(172.5, -163) * mm});
            skLineSegment(sketch, "E616.trimOffspring", {"start": v(9.5, 40.5) * mm, "end": v(9.5, 0) * mm});
            skLineSegment(sketch, "E617.trimOffspring", {"start": v(10, 40.5) * mm, "end": v(10, 0) * mm});
            skLineSegment(sketch, "E618.trimOffspring", {"start": v(10.5, 40.5) * mm, "end": v(10.5, 0) * mm});
            skLineSegment(sketch, "E619.trimOffspring", {"start": v(-0.5, 59.5) * mm, "end": v(0, 59.5) * mm});
            skLineSegment(sketch, "E620.trimOffspring", {"start": v(-0.5, 60) * mm, "end": v(0, 60) * mm});
            skLineSegment(sketch, "E621.trimOffspring", {"start": v(-0.5, 60.5) * mm, "end": v(0, 60.5) * mm});
            skLineSegment(sketch, "E622", {"start": v(-172, 0.5) * mm, "end": v(-172, 0) * mm});
            skSolve(sketch);
        }
        {
            var Q0;
            Q0=qCreatedBy(id+"F1.planeOp",FACE);
            var sketch = newSketch(context, id + "F26", { "sketchPlane" : qUnion([Q0])});
            skLineSegment(sketch, "E623.bottom", {"start": v(-365, 200) * mm, "end": v(365, 200) * mm});
            skLineSegment(sketch, "E623.top", {"start": v(-365, -200) * mm, "end": v(365, -200) * mm});
            skLineSegment(sketch, "E623.left", {"start": v(-365, 200) * mm, "end": v(-365, -200) * mm});
            skLineSegment(sketch, "E623.right", {"start": v(365, 200) * mm, "end": v(365, -200) * mm});
            skPoint(sketch, "E623.middle", {"position": v(0, 0) * mm});
            skLineSegment(sketch, "E624.bottom", {"start": v(0, 0) * mm, "end": v(-365, 0) * mm});
            skLineSegment(sketch, "E624.top", {"start": v(0, -200) * mm, "end": v(-365, -200) * mm});
            skLineSegment(sketch, "E624.left", {"start": v(0, 0) * mm, "end": v(0, -200) * mm});
            skLineSegment(sketch, "E624.right", {"start": v(-365, 0) * mm, "end": v(-365, -200) * mm});
            skLineSegment(sketch, "E625.top", {"start": v(0, 50) * mm, "end": v(-365, 50) * mm});
            skLineSegment(sketch, "E625.left", {"start": v(0, 0) * mm, "end": v(0, 50) * mm});
            skLineSegment(sketch, "E625.right", {"start": v(-365, 0) * mm, "end": v(-365, 50) * mm});
            skLineSegment(sketch, "E626.bottom", {"start": v(0, 0) * mm, "end": v(-182.5, 0) * mm});
            skLineSegment(sketch, "E626.top", {"start": v(0, -50) * mm, "end": v(-182.5, -50) * mm});
            skLineSegment(sketch, "E626.left", {"start": v(0, 0) * mm, "end": v(0, -50) * mm});
            skLineSegment(sketch, "E626.right", {"start": v(-182.5, 0) * mm, "end": v(-182.5, -50) * mm});
            skPoint(sketch, "E627", {"position": v(-319.37, 0) * mm});
            skPoint(sketch, "E628", {"position": v(-273.75, 0) * mm});
            skPoint(sketch, "E629", {"position": v(-228.12, 0) * mm});
            skPoint(sketch, "E630", {"position": v(-192.5, 0) * mm});
            skPoint(sketch, "E631", {"position": v(-172.5, 0) * mm});
            skPoint(sketch, "E632", {"position": v(-136.88, 0) * mm});
            skPoint(sketch, "E633", {"position": v(-91.25, 0) * mm});
            skPoint(sketch, "E634", {"position": v(-45.62, 0) * mm});
            skPoint(sketch, "E635", {"position": v(-10, 0) * mm});
            skPoint(sketch, "E636", {"position": v(10, 0) * mm});
            skPoint(sketch, "E637", {"position": v(-365, -20) * mm});
            skPoint(sketch, "E638", {"position": v(-365, -40) * mm});
            skPoint(sketch, "E639", {"position": v(-365, -60) * mm});
            skPoint(sketch, "E640", {"position": v(-365, -87.5) * mm});
            skPoint(sketch, "E641", {"position": v(-365, -125) * mm});
            skPoint(sketch, "E642", {"position": v(-365, -162.5) * mm});
            skLineSegment(sketch, "E643.bottom", {"start": v(-365, 0) * mm, "end": v(0, 0) * mm});
            skLineSegment(sketch, "E643.top", {"start": v(-365, -0.5) * mm, "end": v(0, -0.5) * mm});
            skLineSegment(sketch, "E643.left", {"start": v(-365, 0) * mm, "end": v(-365, -0.5) * mm});
            skLineSegment(sketch, "E643.right", {"start": v(0, 0) * mm, "end": v(0, -0.5) * mm});
            skLineSegment(sketch, "E644.bottom", {"start": v(-365, -20) * mm, "end": v(0, -20) * mm});
            skLineSegment(sketch, "E644.top", {"start": v(-365, -20.5) * mm, "end": v(0, -20.5) * mm});
            skLineSegment(sketch, "E644.left", {"start": v(-365, -20) * mm, "end": v(-365, -20.5) * mm});
            skLineSegment(sketch, "E644.right", {"start": v(0, -20) * mm, "end": v(0, -20.5) * mm});
            skLineSegment(sketch, "E645.top", {"start": v(-365, -19.5) * mm, "end": v(0, -19.5) * mm});
            skLineSegment(sketch, "E645.left", {"start": v(-365, -20) * mm, "end": v(-365, -19.5) * mm});
            skLineSegment(sketch, "E645.right", {"start": v(0, -20) * mm, "end": v(0, -19.5) * mm});
            skLineSegment(sketch, "E646.bottom", {"start": v(-365, -40) * mm, "end": v(0, -40) * mm});
            skLineSegment(sketch, "E646.top", {"start": v(-365, -39.5) * mm, "end": v(0, -39.5) * mm});
            skLineSegment(sketch, "E646.left", {"start": v(-365, -40) * mm, "end": v(-365, -39.5) * mm});
            skLineSegment(sketch, "E646.right", {"start": v(0, -40) * mm, "end": v(0, -39.5) * mm});
            skLineSegment(sketch, "E647.top", {"start": v(-365, -40.5) * mm, "end": v(0, -40.5) * mm});
            skLineSegment(sketch, "E647.left", {"start": v(-365, -40) * mm, "end": v(-365, -40.5) * mm});
            skLineSegment(sketch, "E647.right", {"start": v(0, -40) * mm, "end": v(0, -40.5) * mm});
            skLineSegment(sketch, "E648.bottom", {"start": v(-365, -50) * mm, "end": v(0, -50) * mm});
            skLineSegment(sketch, "E648.top", {"start": v(-365, -49.5) * mm, "end": v(0, -49.5) * mm});
            skLineSegment(sketch, "E648.left", {"start": v(-365, -50) * mm, "end": v(-365, -49.5) * mm});
            skLineSegment(sketch, "E648.right", {"start": v(0, -50) * mm, "end": v(0, -49.5) * mm});
            skLineSegment(sketch, "E649.top", {"start": v(-365, -50.5) * mm, "end": v(0, -50.5) * mm});
            skLineSegment(sketch, "E649.left", {"start": v(-365, -50) * mm, "end": v(-365, -50.5) * mm});
            skLineSegment(sketch, "E649.right", {"start": v(0, -50) * mm, "end": v(0, -50.5) * mm});
            skLineSegment(sketch, "E650.bottom", {"start": v(-365, -60) * mm, "end": v(0, -60) * mm});
            skLineSegment(sketch, "E650.top", {"start": v(-365, -59.5) * mm, "end": v(0, -59.5) * mm});
            skLineSegment(sketch, "E650.left", {"start": v(-365, -60) * mm, "end": v(-365, -59.5) * mm});
            skLineSegment(sketch, "E650.right", {"start": v(0, -60) * mm, "end": v(0, -59.5) * mm});
            skLineSegment(sketch, "E651.top", {"start": v(-365, -60.5) * mm, "end": v(0, -60.5) * mm});
            skLineSegment(sketch, "E651.left", {"start": v(-365, -60) * mm, "end": v(-365, -60.5) * mm});
            skLineSegment(sketch, "E651.right", {"start": v(0, -60) * mm, "end": v(0, -60.5) * mm});
            skLineSegment(sketch, "E652.bottom", {"start": v(-365, -87.5) * mm, "end": v(0, -87.5) * mm});
            skLineSegment(sketch, "E652.top", {"start": v(-365, -87) * mm, "end": v(0, -87) * mm});
            skLineSegment(sketch, "E652.left", {"start": v(-365, -87.5) * mm, "end": v(-365, -87) * mm});
            skLineSegment(sketch, "E652.right", {"start": v(0, -87.5) * mm, "end": v(0, -87) * mm});
            skLineSegment(sketch, "E653.top", {"start": v(-365, -88) * mm, "end": v(0, -88) * mm});
            skLineSegment(sketch, "E653.left", {"start": v(-365, -87.5) * mm, "end": v(-365, -88) * mm});
            skLineSegment(sketch, "E653.right", {"start": v(0, -87.5) * mm, "end": v(0, -88) * mm});
            skLineSegment(sketch, "E654.bottom", {"start": v(-365, -125) * mm, "end": v(0, -125) * mm});
            skLineSegment(sketch, "E654.top", {"start": v(-365, -124.5) * mm, "end": v(0, -124.5) * mm});
            skLineSegment(sketch, "E654.left", {"start": v(-365, -125) * mm, "end": v(-365, -124.5) * mm});
            skLineSegment(sketch, "E654.right", {"start": v(0, -125) * mm, "end": v(0, -124.5) * mm});
            skLineSegment(sketch, "E655.top", {"start": v(-365, -125.5) * mm, "end": v(0, -125.5) * mm});
            skLineSegment(sketch, "E655.left", {"start": v(-365, -125) * mm, "end": v(-365, -125.5) * mm});
            skLineSegment(sketch, "E655.right", {"start": v(0, -125) * mm, "end": v(0, -125.5) * mm});
            skLineSegment(sketch, "E656.bottom", {"start": v(-365, -162.5) * mm, "end": v(0, -162.5) * mm});
            skLineSegment(sketch, "E656.top", {"start": v(-365, -162) * mm, "end": v(0, -162) * mm});
            skLineSegment(sketch, "E656.left", {"start": v(-365, -162.5) * mm, "end": v(-365, -162) * mm});
            skLineSegment(sketch, "E656.right", {"start": v(0, -162.5) * mm, "end": v(0, -162) * mm});
            skLineSegment(sketch, "E657.top", {"start": v(-365, -163) * mm, "end": v(0, -163) * mm});
            skLineSegment(sketch, "E657.left", {"start": v(-365, -162.5) * mm, "end": v(-365, -163) * mm});
            skLineSegment(sketch, "E657.right", {"start": v(0, -162.5) * mm, "end": v(0, -163) * mm});
            skLineSegment(sketch, "E658.bottom", {"start": v(-319.37, 0) * mm, "end": v(-319.87, 0) * mm});
            skLineSegment(sketch, "E658.top", {"start": v(-319.37, -200) * mm, "end": v(-319.87, -200) * mm});
            skLineSegment(sketch, "E658.left", {"start": v(-319.37, 0) * mm, "end": v(-319.37, -200) * mm});
            skLineSegment(sketch, "E658.right", {"start": v(-319.87, 0) * mm, "end": v(-319.87, -200) * mm});
            skLineSegment(sketch, "E659.bottom", {"start": v(-319.37, 0) * mm, "end": v(-318.87, 0) * mm});
            skLineSegment(sketch, "E659.top", {"start": v(-319.37, -200) * mm, "end": v(-318.87, -200) * mm});
            skLineSegment(sketch, "E659.right", {"start": v(-318.87, 0) * mm, "end": v(-318.87, -200) * mm});
            skLineSegment(sketch, "E660.bottom", {"start": v(-273.75, 0) * mm, "end": v(-274.25, 0) * mm});
            skLineSegment(sketch, "E660.top", {"start": v(-273.75, -200) * mm, "end": v(-274.25, -200) * mm});
            skLineSegment(sketch, "E660.left", {"start": v(-273.75, 0) * mm, "end": v(-273.75, -200) * mm});
            skLineSegment(sketch, "E660.right", {"start": v(-274.25, 0) * mm, "end": v(-274.25, -200) * mm});
            skLineSegment(sketch, "E661.bottom", {"start": v(-273.75, 0) * mm, "end": v(-273.25, 0) * mm});
            skLineSegment(sketch, "E661.top", {"start": v(-273.75, -200) * mm, "end": v(-273.25, -200) * mm});
            skLineSegment(sketch, "E661.right", {"start": v(-273.25, 0) * mm, "end": v(-273.25, -200) * mm});
            skLineSegment(sketch, "E662.bottom", {"start": v(-228.12, 0) * mm, "end": v(-228.62, 0) * mm});
            skLineSegment(sketch, "E662.top", {"start": v(-228.12, -200) * mm, "end": v(-228.62, -200) * mm});
            skLineSegment(sketch, "E662.left", {"start": v(-228.12, 0) * mm, "end": v(-228.12, -200) * mm});
            skLineSegment(sketch, "E662.right", {"start": v(-228.62, 0) * mm, "end": v(-228.62, -200) * mm});
            skLineSegment(sketch, "E663.bottom", {"start": v(-228.12, 0) * mm, "end": v(-227.62, 0) * mm});
            skLineSegment(sketch, "E663.top", {"start": v(-228.12, -200) * mm, "end": v(-227.62, -200) * mm});
            skLineSegment(sketch, "E663.right", {"start": v(-227.62, 0) * mm, "end": v(-227.62, -200) * mm});
            skLineSegment(sketch, "E664.bottom", {"start": v(-192.5, 0) * mm, "end": v(-193, 0) * mm});
            skLineSegment(sketch, "E664.top", {"start": v(-192.5, -200) * mm, "end": v(-193, -200) * mm});
            skLineSegment(sketch, "E664.left", {"start": v(-192.5, 0) * mm, "end": v(-192.5, -200) * mm});
            skLineSegment(sketch, "E664.right", {"start": v(-193, 0) * mm, "end": v(-193, -200) * mm});
            skLineSegment(sketch, "E665.bottom", {"start": v(-192.5, 0) * mm, "end": v(-192, 0) * mm});
            skLineSegment(sketch, "E665.top", {"start": v(-192.5, -200) * mm, "end": v(-192, -200) * mm});
            skLineSegment(sketch, "E665.right", {"start": v(-192, 0) * mm, "end": v(-192, -200) * mm});
            skLineSegment(sketch, "E666.bottom", {"start": v(-182.5, 0) * mm, "end": v(-183, 0) * mm});
            skLineSegment(sketch, "E666.top", {"start": v(-182.5, -200) * mm, "end": v(-183, -200) * mm});
            skLineSegment(sketch, "E666.left", {"start": v(-182.5, 0) * mm, "end": v(-182.5, -200) * mm});
            skLineSegment(sketch, "E666.right", {"start": v(-183, 0) * mm, "end": v(-183, -200) * mm});
            skLineSegment(sketch, "E667.bottom", {"start": v(-182.5, 0) * mm, "end": v(-182, 0) * mm});
            skLineSegment(sketch, "E667.top", {"start": v(-182.5, -200) * mm, "end": v(-182, -200) * mm});
            skLineSegment(sketch, "E667.right", {"start": v(-182, 0) * mm, "end": v(-182, -200) * mm});
            skLineSegment(sketch, "E668.bottom", {"start": v(-172.5, 0) * mm, "end": v(-173, 0) * mm});
            skLineSegment(sketch, "E668.top", {"start": v(-172.5, -200) * mm, "end": v(-173, -200) * mm});
            skLineSegment(sketch, "E668.left", {"start": v(-172.5, 0) * mm, "end": v(-172.5, -200) * mm});
            skLineSegment(sketch, "E668.right", {"start": v(-173, 0) * mm, "end": v(-173, -200) * mm});
            skLineSegment(sketch, "E669.bottom", {"start": v(-172.5, 0) * mm, "end": v(-172, 0) * mm});
            skLineSegment(sketch, "E669.top", {"start": v(-172.5, -200) * mm, "end": v(-172, -200) * mm});
            skLineSegment(sketch, "E669.right", {"start": v(-172, 0) * mm, "end": v(-172, -200) * mm});
            skLineSegment(sketch, "E670.bottom", {"start": v(-136.88, 0) * mm, "end": v(-137.38, 0) * mm});
            skLineSegment(sketch, "E670.top", {"start": v(-136.87, -200) * mm, "end": v(-137.37, -200) * mm});
            skLineSegment(sketch, "E670.left", {"start": v(-136.88, 0) * mm, "end": v(-136.88, -200) * mm});
            skLineSegment(sketch, "E670.right", {"start": v(-137.38, 0) * mm, "end": v(-137.37, -200) * mm});
            skLineSegment(sketch, "E671.bottom", {"start": v(-136.88, 0) * mm, "end": v(-136.38, 0) * mm});
            skLineSegment(sketch, "E671.top", {"start": v(-136.88, -200) * mm, "end": v(-136.38, -200) * mm});
            skLineSegment(sketch, "E671.right", {"start": v(-136.38, 0) * mm, "end": v(-136.38, -200) * mm});
            skLineSegment(sketch, "E672.bottom", {"start": v(-91.25, 0) * mm, "end": v(-91.75, 0) * mm});
            skLineSegment(sketch, "E672.top", {"start": v(-91.25, -200) * mm, "end": v(-91.75, -200) * mm});
            skLineSegment(sketch, "E672.left", {"start": v(-91.25, 0) * mm, "end": v(-91.25, -200) * mm});
            skLineSegment(sketch, "E672.right", {"start": v(-91.75, 0) * mm, "end": v(-91.75, -200) * mm});
            skLineSegment(sketch, "E673.bottom", {"start": v(-91.25, 0) * mm, "end": v(-90.75, 0) * mm});
            skLineSegment(sketch, "E673.top", {"start": v(-91.25, -200) * mm, "end": v(-90.75, -200) * mm});
            skLineSegment(sketch, "E673.right", {"start": v(-90.75, 0) * mm, "end": v(-90.75, -200) * mm});
            skLineSegment(sketch, "E674.bottom", {"start": v(-45.62, 0) * mm, "end": v(-46.12, 0) * mm});
            skLineSegment(sketch, "E674.top", {"start": v(-45.62, -200) * mm, "end": v(-46.12, -200) * mm});
            skLineSegment(sketch, "E674.left", {"start": v(-45.62, 0) * mm, "end": v(-45.62, -200) * mm});
            skLineSegment(sketch, "E674.right", {"start": v(-46.12, 0) * mm, "end": v(-46.12, -200) * mm});
            skLineSegment(sketch, "E675.bottom", {"start": v(-45.62, 0) * mm, "end": v(-45.12, 0) * mm});
            skLineSegment(sketch, "E675.top", {"start": v(-45.62, -200) * mm, "end": v(-45.12, -200) * mm});
            skLineSegment(sketch, "E675.right", {"start": v(-45.12, 0) * mm, "end": v(-45.12, -200) * mm});
            skLineSegment(sketch, "E676.bottom", {"start": v(0, 0) * mm, "end": v(-0.5, 0) * mm});
            skLineSegment(sketch, "E676.top", {"start": v(0, -200) * mm, "end": v(-0.5, -200) * mm});
            skLineSegment(sketch, "E676.right", {"start": v(-0.5, 0) * mm, "end": v(-0.5, -200) * mm});
            skLineSegment(sketch, "E677.bottom", {"start": v(-10, 0) * mm, "end": v(-9.5, 0) * mm});
            skLineSegment(sketch, "E677.top", {"start": v(-10, -200) * mm, "end": v(-9.5, -200) * mm});
            skLineSegment(sketch, "E677.left", {"start": v(-10, 0) * mm, "end": v(-10, -200) * mm});
            skLineSegment(sketch, "E677.right", {"start": v(-9.5, 0) * mm, "end": v(-9.5, -200) * mm});
            skLineSegment(sketch, "E678.bottom", {"start": v(-10, 0) * mm, "end": v(-10.5, 0) * mm});
            skLineSegment(sketch, "E678.top", {"start": v(-10, -200) * mm, "end": v(-10.5, -200) * mm});
            skLineSegment(sketch, "E678.right", {"start": v(-10.5, 0) * mm, "end": v(-10.5, -200) * mm});
            skLineSegment(sketch, "E679.MirrorCS", {"start": v(365, 0) * mm, "end": v(0, 0) * mm});
            skLineSegment(sketch, "E680.MirrorCS", {"start": v(365, -0.5) * mm, "end": v(0, -0.5) * mm});
            skLineSegment(sketch, "E681.MirrorCS", {"start": v(365, -19.5) * mm, "end": v(0, -19.5) * mm});
            skLineSegment(sketch, "E682.MirrorCS", {"start": v(365, -20) * mm, "end": v(0, -20) * mm});
            skLineSegment(sketch, "E683.MirrorCS", {"start": v(365, -20.5) * mm, "end": v(0, -20.5) * mm});
            skLineSegment(sketch, "E684.MirrorCS", {"start": v(0.5, 0) * mm, "end": v(0.5, -200) * mm});
            skLineSegment(sketch, "E685.MirrorCS", {"start": v(365, -39.5) * mm, "end": v(0, -39.5) * mm});
            skLineSegment(sketch, "E686.MirrorCS", {"start": v(365, -40) * mm, "end": v(0, -40) * mm});
            skLineSegment(sketch, "E687.MirrorCS", {"start": v(365, -40.5) * mm, "end": v(0, -40.5) * mm});
            skLineSegment(sketch, "E688.MirrorCS", {"start": v(365, -49.5) * mm, "end": v(0, -49.5) * mm});
            skLineSegment(sketch, "E689.MirrorCS", {"start": v(0, -50) * mm, "end": v(182.5, -50) * mm});
            skLineSegment(sketch, "E690.MirrorCS", {"start": v(365, -50.5) * mm, "end": v(0, -50.5) * mm});
            skLineSegment(sketch, "E691.MirrorCS", {"start": v(365, -59.5) * mm, "end": v(0, -59.5) * mm});
            skLineSegment(sketch, "E692.MirrorCS", {"start": v(365, -60) * mm, "end": v(0, -60) * mm});
            skLineSegment(sketch, "E693.MirrorCS", {"start": v(365, -60.5) * mm, "end": v(0, -60.5) * mm});
            skLineSegment(sketch, "E694.MirrorCS", {"start": v(365, -87) * mm, "end": v(0, -87) * mm});
            skLineSegment(sketch, "E695.MirrorCS", {"start": v(365, -87.5) * mm, "end": v(0, -87.5) * mm});
            skLineSegment(sketch, "E696.MirrorCS", {"start": v(365, -88) * mm, "end": v(0, -88) * mm});
            skLineSegment(sketch, "E697.MirrorCS", {"start": v(365, -124.5) * mm, "end": v(0, -124.5) * mm});
            skLineSegment(sketch, "E698.MirrorCS", {"start": v(365, -125) * mm, "end": v(0, -125) * mm});
            skLineSegment(sketch, "E699.MirrorCS", {"start": v(365, -125.5) * mm, "end": v(0, -125.5) * mm});
            skLineSegment(sketch, "E700.MirrorCS", {"start": v(365, -162) * mm, "end": v(0, -162) * mm});
            skLineSegment(sketch, "E701.MirrorCS", {"start": v(365, -162.5) * mm, "end": v(0, -162.5) * mm});
            skLineSegment(sketch, "E702.MirrorCS", {"start": v(365, -163) * mm, "end": v(0, -163) * mm});
            skLineSegment(sketch, "E703.MirrorCS", {"start": v(9.5, 0) * mm, "end": v(9.5, -200) * mm});
            skLineSegment(sketch, "E704.MirrorCS", {"start": v(10, 0) * mm, "end": v(10, -200) * mm});
            skLineSegment(sketch, "E705.MirrorCS", {"start": v(10.5, 0) * mm, "end": v(10.5, -200) * mm});
            skLineSegment(sketch, "E706.MirrorCS", {"start": v(45.12, 0) * mm, "end": v(45.12, -200) * mm});
            skLineSegment(sketch, "E707.MirrorCS", {"start": v(45.62, 0) * mm, "end": v(45.62, -200) * mm});
            skLineSegment(sketch, "E708.MirrorCS", {"start": v(46.12, 0) * mm, "end": v(46.12, -200) * mm});
            skLineSegment(sketch, "E709.MirrorCS", {"start": v(90.75, 0) * mm, "end": v(90.75, -200) * mm});
            skLineSegment(sketch, "E710.MirrorCS", {"start": v(91.25, 0) * mm, "end": v(91.25, -200) * mm});
            skLineSegment(sketch, "E711.MirrorCS", {"start": v(91.75, 0) * mm, "end": v(91.75, -200) * mm});
            skLineSegment(sketch, "E712.MirrorCS", {"start": v(136.38, 0) * mm, "end": v(136.38, -200) * mm});
            skLineSegment(sketch, "E713.MirrorCS", {"start": v(136.88, 0) * mm, "end": v(136.88, -200) * mm});
            skLineSegment(sketch, "E714.MirrorCS", {"start": v(137.38, 0) * mm, "end": v(137.37, -200) * mm});
            skLineSegment(sketch, "E715.MirrorCS", {"start": v(172, 0) * mm, "end": v(172, -200) * mm});
            skLineSegment(sketch, "E716.MirrorCS", {"start": v(172.5, 0) * mm, "end": v(172.5, -200) * mm});
            skLineSegment(sketch, "E717.MirrorCS", {"start": v(173, 0) * mm, "end": v(173, -200) * mm});
            skLineSegment(sketch, "E718.MirrorCS", {"start": v(182, 0) * mm, "end": v(182, -200) * mm});
            skLineSegment(sketch, "E719.MirrorCS", {"start": v(183, 0) * mm, "end": v(183, -200) * mm});
            skLineSegment(sketch, "E720.MirrorCS", {"start": v(192, 0) * mm, "end": v(192, -200) * mm});
            skLineSegment(sketch, "E721.MirrorCS", {"start": v(192.5, 0) * mm, "end": v(192.5, -200) * mm});
            skLineSegment(sketch, "E722.MirrorCS", {"start": v(193, 0) * mm, "end": v(193, -200) * mm});
            skLineSegment(sketch, "E723.MirrorCS", {"start": v(319.87, 0) * mm, "end": v(319.87, -200) * mm});
            skLineSegment(sketch, "E724.MirrorCS", {"start": v(319.37, 0) * mm, "end": v(319.37, -200) * mm});
            skLineSegment(sketch, "E725.MirrorCS", {"start": v(318.87, 0) * mm, "end": v(318.87, -200) * mm});
            skLineSegment(sketch, "E726.MirrorCS", {"start": v(274.25, 0) * mm, "end": v(274.25, -200) * mm});
            skLineSegment(sketch, "E727.MirrorCS", {"start": v(273.75, 0) * mm, "end": v(273.75, -200) * mm});
            skLineSegment(sketch, "E728.MirrorCS", {"start": v(273.25, 0) * mm, "end": v(273.25, -200) * mm});
            skLineSegment(sketch, "E729.MirrorCS", {"start": v(228.62, 0) * mm, "end": v(228.62, -200) * mm});
            skLineSegment(sketch, "E730.MirrorCS", {"start": v(228.12, 0) * mm, "end": v(228.12, -200) * mm});
            skLineSegment(sketch, "E731.MirrorCS", {"start": v(227.62, 0) * mm, "end": v(227.62, -200) * mm});
            skLineSegment(sketch, "E732.MirrorCS", {"start": v(-365, 0.5) * mm, "end": v(0, 0.5) * mm});
            skLineSegment(sketch, "E733.MirrorCS", {"start": v(365, 0.5) * mm, "end": v(0, 0.5) * mm});
            skLineSegment(sketch, "E734.MirrorCS", {"start": v(-365, 39.5) * mm, "end": v(0, 39.5) * mm});
            skLineSegment(sketch, "E735.MirrorCS", {"start": v(-365, 40.5) * mm, "end": v(0, 40.5) * mm});
            skLineSegment(sketch, "E736.MirrorCS", {"start": v(-365, 49.5) * mm, "end": v(0, 49.5) * mm});
            skLineSegment(sketch, "E737.MirrorCS", {"start": v(-365, 50.5) * mm, "end": v(0, 50.5) * mm});
            skLineSegment(sketch, "E738.MirrorCS", {"start": v(-365, 59.5) * mm, "end": v(0, 59.5) * mm});
            skLineSegment(sketch, "E739.MirrorCS", {"start": v(-365, 60.5) * mm, "end": v(0, 60.5) * mm});
            skLineSegment(sketch, "E740.MirrorCS", {"start": v(-365, 19.5) * mm, "end": v(0, 19.5) * mm});
            skLineSegment(sketch, "E741.MirrorCS", {"start": v(-365, 20.5) * mm, "end": v(0, 20.5) * mm});
            skLineSegment(sketch, "E742.MirrorCS", {"start": v(-319.87, 0) * mm, "end": v(-319.87, 200) * mm});
            skLineSegment(sketch, "E743.MirrorCS", {"start": v(-318.87, 0) * mm, "end": v(-318.87, 200) * mm});
            skLineSegment(sketch, "E744.MirrorCS", {"start": v(-274.25, 0) * mm, "end": v(-274.25, 200) * mm});
            skLineSegment(sketch, "E745.MirrorCS", {"start": v(-273.25, 0) * mm, "end": v(-273.25, 200) * mm});
            skLineSegment(sketch, "E746.MirrorCS", {"start": v(-228.62, 0) * mm, "end": v(-228.62, 200) * mm});
            skLineSegment(sketch, "E747.MirrorCS", {"start": v(-227.62, 0) * mm, "end": v(-227.62, 200) * mm});
            skLineSegment(sketch, "E748.MirrorCS", {"start": v(-193, 0) * mm, "end": v(-193, 200) * mm});
            skLineSegment(sketch, "E749.MirrorCS", {"start": v(-192, 0) * mm, "end": v(-192, 200) * mm});
            skLineSegment(sketch, "E750.MirrorCS", {"start": v(-183, 0) * mm, "end": v(-183, 200) * mm});
            skLineSegment(sketch, "E751.MirrorCS", {"start": v(-182, 0) * mm, "end": v(-182, 200) * mm});
            skLineSegment(sketch, "E752.MirrorCS", {"start": v(-173, 0) * mm, "end": v(-173, 200) * mm});
            skLineSegment(sketch, "E753.MirrorCS", {"start": v(-172, 0) * mm, "end": v(-172, 200) * mm});
            skLineSegment(sketch, "E754.MirrorCS", {"start": v(-137.38, 0) * mm, "end": v(-137.37, 200) * mm});
            skLineSegment(sketch, "E755.MirrorCS", {"start": v(-136.38, 0) * mm, "end": v(-136.38, 200) * mm});
            skLineSegment(sketch, "E756.MirrorCS", {"start": v(-91.75, 0) * mm, "end": v(-91.75, 200) * mm});
            skLineSegment(sketch, "E757.MirrorCS", {"start": v(-90.75, 0) * mm, "end": v(-90.75, 200) * mm});
            skLineSegment(sketch, "E758.MirrorCS", {"start": v(-46.12, 0) * mm, "end": v(-46.12, 200) * mm});
            skLineSegment(sketch, "E759.MirrorCS", {"start": v(-45.12, 0) * mm, "end": v(-45.12, 200) * mm});
            skLineSegment(sketch, "E760.MirrorCS", {"start": v(-10.5, 0) * mm, "end": v(-10.5, 200) * mm});
            skLineSegment(sketch, "E761.MirrorCS", {"start": v(-9.5, 0) * mm, "end": v(-9.5, 200) * mm});
            skLineSegment(sketch, "E762.MirrorCS", {"start": v(-0.5, 0) * mm, "end": v(-0.5, 200) * mm});
            skLineSegment(sketch, "E763.MirrorCS", {"start": v(0.5, 0) * mm, "end": v(0.5, 200) * mm});
            skLineSegment(sketch, "E764.MirrorCS", {"start": v(9.5, 0) * mm, "end": v(9.5, 200) * mm});
            skLineSegment(sketch, "E765.MirrorCS", {"start": v(10.5, 0) * mm, "end": v(10.5, 200) * mm});
            skLineSegment(sketch, "E766.MirrorCS", {"start": v(365, 19.5) * mm, "end": v(0, 19.5) * mm});
            skLineSegment(sketch, "E767.MirrorCS", {"start": v(365, 20.5) * mm, "end": v(0, 20.5) * mm});
            skLineSegment(sketch, "E768.MirrorCS", {"start": v(365, 39.5) * mm, "end": v(0, 39.5) * mm});
            skLineSegment(sketch, "E769.MirrorCS", {"start": v(365, 40.5) * mm, "end": v(0, 40.5) * mm});
            skLineSegment(sketch, "E770.MirrorCS", {"start": v(365, 49.5) * mm, "end": v(0, 49.5) * mm});
            skLineSegment(sketch, "E771.MirrorCS", {"start": v(365, 50.5) * mm, "end": v(0, 50.5) * mm});
            skLineSegment(sketch, "E772.MirrorCS", {"start": v(365, 59.5) * mm, "end": v(0, 59.5) * mm});
            skLineSegment(sketch, "E773.MirrorCS", {"start": v(365, 60.5) * mm, "end": v(0, 60.5) * mm});
            skSolve(sketch);
        }
        {
            var Q0;
            Q0=qCreatedBy(makeId("Right.planeOp"),FACE);
            cPlane(context, id + "F27", {"entities" : qUnion([Q0]), "cplaneType" : CPlaneType.OFFSET, "offset" : 182.5 * mm, "width" : 150 * mm, "height" : 150 * mm});
        }
        {
            var Q0;
            Q0=qCreatedBy(makeId("Front.planeOp"),FACE);
            cPlane(context, id + "F28", {"entities" : qUnion([Q0]), "cplaneType" : CPlaneType.OFFSET, "offset" : 50 * mm, "width" : 150 * mm, "height" : 150 * mm});
        }
        {
            var Q0;
            Q0=qCreatedBy(makeId("Right.planeOp"),FACE);
            cPlane(context, id + "F29", {"entities" : qUnion([Q0]), "cplaneType" : CPlaneType.OFFSET, "offset" : 172.5 * mm, "oppositeDirection" : true, "width" : 150 * mm, "height" : 150 * mm});
        }
        {
            var Q0;
            Q0=qCreatedBy(makeId("Front.planeOp"),FACE);
            cPlane(context, id + "F30", {"entities" : qUnion([Q0]), "cplaneType" : CPlaneType.OFFSET, "offset" : 50 * mm, "oppositeDirection" : true, "width" : 150 * mm, "height" : 150 * mm});
        }
        {
            var Q0;
            Q0=qCreatedBy(makeId("Right.planeOp"),FACE);
            var sketch = newSketch(context, id + "F31", { "sketchPlane" : qUnion([Q0])});
            skLineSegment(sketch, "E774", {"start": v(0, 20) * mm, "end": v(-200, 20) * mm});
            skPoint(sketch, "E775", {"position": v(-20, 20) * mm});
            skPoint(sketch, "E776", {"position": v(-40, 20) * mm});
            skPoint(sketch, "E777", {"position": v(-165, 20) * mm});
            skPoint(sketch, "E778", {"position": v(-60, 20) * mm});
            skPoint(sketch, "E779", {"position": v(-95, 20) * mm});
            skPoint(sketch, "E780", {"position": v(-130, 20) * mm});
            skPoint(sketch, "E781", {"position": v(-100, 20) * mm});
            skPoint(sketch, "E782.MirrorP", {"position": v(20, 20) * mm});
            skPoint(sketch, "E783.MirrorP", {"position": v(40, 20) * mm});
            skLineSegment(sketch, "E784", {"start": v(40, 20) * mm, "end": v(0, 20) * mm});
            skLineSegment(sketch, "E785.bottom", {"start": v(40, 20) * mm, "end": v(-200, 20) * mm});
            skLineSegment(sketch, "E785.top", {"start": v(40, 10) * mm, "end": v(-200, 10) * mm});
            skLineSegment(sketch, "E785.left", {"start": v(40, 20) * mm, "end": v(40, 10) * mm});
            skLineSegment(sketch, "E785.right", {"start": v(-200, 20) * mm, "end": v(-200, 10) * mm});
            skLineSegment(sketch, "E786", {"start": v(20, 20) * mm, "end": v(20, 10) * mm});
            skLineSegment(sketch, "E787", {"start": v(40, 15) * mm, "end": v(-200, 15) * mm});
            skLineSegment(sketch, "E788", {"start": v(-20, 20) * mm, "end": v(-20, 10) * mm});
            skLineSegment(sketch, "E789", {"start": v(0, 20) * mm, "end": v(0, 10) * mm});
            skLineSegment(sketch, "E790", {"start": v(-40, 20) * mm, "end": v(-40, 10) * mm});
            skLineSegment(sketch, "E791", {"start": v(-60, 20) * mm, "end": v(-60, 10) * mm});
            skLineSegment(sketch, "E792", {"start": v(-95, 20) * mm, "end": v(-95, 10) * mm});
            skLineSegment(sketch, "E793", {"start": v(-130, 20) * mm, "end": v(-130, 10) * mm});
            skLineSegment(sketch, "E794", {"start": v(-165, 20) * mm, "end": v(-165, 10) * mm});
            skLineSegment(sketch, "E795.bottom", {"start": v(-200, 10) * mm, "end": v(40, 10) * mm});
            skLineSegment(sketch, "E795.top", {"start": v(-200, 0) * mm, "end": v(40, 0) * mm});
            skLineSegment(sketch, "E795.left", {"start": v(-200, 10) * mm, "end": v(-200, 0) * mm});
            skLineSegment(sketch, "E795.right", {"start": v(40, 10) * mm, "end": v(40, 0) * mm});
            skLineSegment(sketch, "E796.bottom", {"start": v(200, 10.5) * mm, "end": v(-200, 10.5) * mm});
            skLineSegment(sketch, "E796.top", {"start": v(200, 9.5) * mm, "end": v(-200, 9.5) * mm});
            skLineSegment(sketch, "E796.left", {"start": v(200, 10.5) * mm, "end": v(200, 9.5) * mm});
            skLineSegment(sketch, "E796.right", {"start": v(-200, 10.5) * mm, "end": v(-200, 9.5) * mm});
            skPoint(sketch, "E796.middle", {"position": v(0, 10) * mm});
            skLineSegment(sketch, "E797.bottom", {"start": v(200, 14.5) * mm, "end": v(-200, 14.5) * mm});
            skLineSegment(sketch, "E797.top", {"start": v(200, 15.5) * mm, "end": v(-200, 15.5) * mm});
            skLineSegment(sketch, "E797.left", {"start": v(200, 14.5) * mm, "end": v(200, 15.5) * mm});
            skLineSegment(sketch, "E797.right", {"start": v(-200, 14.5) * mm, "end": v(-200, 15.5) * mm});
            skPoint(sketch, "E797.middle", {"position": v(0, 15) * mm});
            skLineSegment(sketch, "E798.bottom", {"start": v(-200, 19.5) * mm, "end": v(200, 19.5) * mm});
            skLineSegment(sketch, "E798.top", {"start": v(-200, 20.5) * mm, "end": v(200, 20.5) * mm});
            skLineSegment(sketch, "E798.left", {"start": v(-200, 19.5) * mm, "end": v(-200, 20.5) * mm});
            skLineSegment(sketch, "E798.right", {"start": v(200, 19.5) * mm, "end": v(200, 20.5) * mm});
            skPoint(sketch, "E798.middle", {"position": v(0, 20) * mm});
            skLineSegment(sketch, "E799.bottom", {"start": v(40.5, 20) * mm, "end": v(39.5, 20) * mm});
            skLineSegment(sketch, "E799.top", {"start": v(40.5, 10) * mm, "end": v(39.5, 10) * mm});
            skLineSegment(sketch, "E799.left", {"start": v(40.5, 20) * mm, "end": v(40.5, 10) * mm});
            skLineSegment(sketch, "E799.right", {"start": v(39.5, 20) * mm, "end": v(39.5, 10) * mm});
            skPoint(sketch, "E799.middle", {"position": v(40, 15) * mm});
            skLineSegment(sketch, "E800.bottom", {"start": v(20.5, 20) * mm, "end": v(19.5, 20) * mm});
            skLineSegment(sketch, "E800.top", {"start": v(20.5, 10) * mm, "end": v(19.5, 10) * mm});
            skLineSegment(sketch, "E800.left", {"start": v(20.5, 20) * mm, "end": v(20.5, 10) * mm});
            skLineSegment(sketch, "E800.right", {"start": v(19.5, 20) * mm, "end": v(19.5, 10) * mm});
            skPoint(sketch, "E800.middle", {"position": v(20, 15) * mm});
            skLineSegment(sketch, "E801.bottom", {"start": v(0.5, 20) * mm, "end": v(-0.5, 20) * mm});
            skLineSegment(sketch, "E801.top", {"start": v(0.5, 10) * mm, "end": v(-0.5, 10) * mm});
            skLineSegment(sketch, "E801.left", {"start": v(0.5, 20) * mm, "end": v(0.5, 10) * mm});
            skLineSegment(sketch, "E801.right", {"start": v(-0.5, 20) * mm, "end": v(-0.5, 10) * mm});
            skLineSegment(sketch, "E802.bottom", {"start": v(-19.5, 20) * mm, "end": v(-20.5, 20) * mm});
            skLineSegment(sketch, "E802.top", {"start": v(-19.5, 10) * mm, "end": v(-20.5, 10) * mm});
            skLineSegment(sketch, "E802.left", {"start": v(-19.5, 20) * mm, "end": v(-19.5, 10) * mm});
            skLineSegment(sketch, "E802.right", {"start": v(-20.5, 20) * mm, "end": v(-20.5, 10) * mm});
            skPoint(sketch, "E802.middle", {"position": v(-20, 15) * mm});
            skLineSegment(sketch, "E803.bottom", {"start": v(-39.5, 20) * mm, "end": v(-40.5, 20) * mm});
            skLineSegment(sketch, "E803.top", {"start": v(-39.5, 10) * mm, "end": v(-40.5, 10) * mm});
            skLineSegment(sketch, "E803.left", {"start": v(-39.5, 20) * mm, "end": v(-39.5, 10) * mm});
            skLineSegment(sketch, "E803.right", {"start": v(-40.5, 20) * mm, "end": v(-40.5, 10) * mm});
            skPoint(sketch, "E803.middle", {"position": v(-40, 15) * mm});
            skLineSegment(sketch, "E804.bottom", {"start": v(-59.5, 20) * mm, "end": v(-60.5, 20) * mm});
            skLineSegment(sketch, "E804.top", {"start": v(-59.5, 10) * mm, "end": v(-60.5, 10) * mm});
            skLineSegment(sketch, "E804.left", {"start": v(-59.5, 20) * mm, "end": v(-59.5, 10) * mm});
            skLineSegment(sketch, "E804.right", {"start": v(-60.5, 20) * mm, "end": v(-60.5, 10) * mm});
            skPoint(sketch, "E804.middle", {"position": v(-60, 15) * mm});
            skLineSegment(sketch, "E805.bottom", {"start": v(-95.5, 20) * mm, "end": v(-94.5, 20) * mm});
            skLineSegment(sketch, "E805.top", {"start": v(-95.5, 10) * mm, "end": v(-94.5, 10) * mm});
            skLineSegment(sketch, "E805.left", {"start": v(-95.5, 20) * mm, "end": v(-95.5, 10) * mm});
            skLineSegment(sketch, "E805.right", {"start": v(-94.5, 20) * mm, "end": v(-94.5, 10) * mm});
            skPoint(sketch, "E805.middle", {"position": v(-95, 15) * mm});
            skLineSegment(sketch, "E806.bottom", {"start": v(-129.5, 20) * mm, "end": v(-130.5, 20) * mm});
            skLineSegment(sketch, "E806.top", {"start": v(-129.5, 10) * mm, "end": v(-130.5, 10) * mm});
            skLineSegment(sketch, "E806.left", {"start": v(-129.5, 20) * mm, "end": v(-129.5, 10) * mm});
            skLineSegment(sketch, "E806.right", {"start": v(-130.5, 20) * mm, "end": v(-130.5, 10) * mm});
            skPoint(sketch, "E806.middle", {"position": v(-130, 15) * mm});
            skLineSegment(sketch, "E807.bottom", {"start": v(-164.5, 20) * mm, "end": v(-165.5, 20) * mm});
            skLineSegment(sketch, "E807.top", {"start": v(-164.5, 10) * mm, "end": v(-165.5, 10) * mm});
            skLineSegment(sketch, "E807.left", {"start": v(-164.5, 20) * mm, "end": v(-164.5, 10) * mm});
            skLineSegment(sketch, "E807.right", {"start": v(-165.5, 20) * mm, "end": v(-165.5, 10) * mm});
            skPoint(sketch, "E807.middle", {"position": v(-165, 15) * mm});
            skSolve(sketch);
        }
        {
            var Q0;
            Q0=qCreatedBy(id+"F28.planeOp",FACE);
            var sketch = newSketch(context, id + "F32", { "sketchPlane" : qUnion([Q0])});
            skLineSegment(sketch, "E808.bottom", {"start": v(-365, 20) * mm, "end": v(365, 20) * mm});
            skLineSegment(sketch, "E808.top", {"start": v(-365, 0) * mm, "end": v(365, 0) * mm});
            skLineSegment(sketch, "E808.left", {"start": v(-365, 20) * mm, "end": v(-365, 0) * mm});
            skLineSegment(sketch, "E808.right", {"start": v(365, 20) * mm, "end": v(365, 0) * mm});
            skLineSegment(sketch, "E809", {"start": v(-365, 10) * mm, "end": v(365, 10) * mm});
            skLineSegment(sketch, "E810", {"start": v(-365, 15) * mm, "end": v(365, 15) * mm});
            skPoint(sketch, "E811", {"position": v(10, 20) * mm});
            skPoint(sketch, "E812", {"position": v(50.63, 20) * mm});
            skPoint(sketch, "E813", {"position": v(91.25, 20) * mm});
            skPoint(sketch, "E814", {"position": v(131.88, 20) * mm});
            skPoint(sketch, "E815", {"position": v(172.5, 20) * mm});
            skPoint(sketch, "E816", {"position": v(321.88, 20) * mm});
            skPoint(sketch, "E817", {"position": v(192.5, 20) * mm});
            skPoint(sketch, "E818", {"position": v(235.63, 20) * mm});
            skPoint(sketch, "E819", {"position": v(278.75, 20) * mm});
            skLineSegment(sketch, "E820", {"start": v(10, 20) * mm, "end": v(10, 10) * mm});
            skLineSegment(sketch, "E821", {"start": v(50.63, 20) * mm, "end": v(50.63, 10) * mm});
            skLineSegment(sketch, "E822", {"start": v(91.25, 20) * mm, "end": v(91.25, 10) * mm});
            skLineSegment(sketch, "E823", {"start": v(131.88, 20) * mm, "end": v(131.88, 10) * mm});
            skLineSegment(sketch, "E824", {"start": v(172.5, 20) * mm, "end": v(172.5, 10) * mm});
            skLineSegment(sketch, "E825", {"start": v(192.5, 20) * mm, "end": v(192.5, 10) * mm});
            skLineSegment(sketch, "E826", {"start": v(235.63, 20) * mm, "end": v(235.63, 10) * mm});
            skLineSegment(sketch, "E827", {"start": v(278.75, 20) * mm, "end": v(278.75, 10) * mm});
            skLineSegment(sketch, "E828", {"start": v(321.88, 20) * mm, "end": v(321.88, 10) * mm});
            skLineSegment(sketch, "E829.MirrorCS", {"start": v(-10, 20) * mm, "end": v(-10, 10) * mm});
            skLineSegment(sketch, "E830.MirrorCS", {"start": v(-50.63, 20) * mm, "end": v(-50.63, 10) * mm});
            skLineSegment(sketch, "E831.MirrorCS", {"start": v(-91.25, 20) * mm, "end": v(-91.25, 10) * mm});
            skLineSegment(sketch, "E832.MirrorCS", {"start": v(-131.88, 20) * mm, "end": v(-131.88, 10) * mm});
            skLineSegment(sketch, "E833.MirrorCS", {"start": v(-172.5, 20) * mm, "end": v(-172.5, 10) * mm});
            skLineSegment(sketch, "E834.MirrorCS", {"start": v(-192.5, 20) * mm, "end": v(-192.5, 10) * mm});
            skLineSegment(sketch, "E835.MirrorCS", {"start": v(-235.63, 20) * mm, "end": v(-235.63, 10) * mm});
            skLineSegment(sketch, "E836.MirrorCS", {"start": v(-278.75, 20) * mm, "end": v(-278.75, 10) * mm});
            skLineSegment(sketch, "E837.MirrorCS", {"start": v(-321.88, 20) * mm, "end": v(-321.88, 10) * mm});
            skLineSegment(sketch, "E838.bottom", {"start": v(-365, 10.5) * mm, "end": v(365, 10.5) * mm});
            skLineSegment(sketch, "E838.top", {"start": v(-365, 9.5) * mm, "end": v(365, 9.5) * mm});
            skLineSegment(sketch, "E838.left", {"start": v(-365, 10.5) * mm, "end": v(-365, 9.5) * mm});
            skLineSegment(sketch, "E838.right", {"start": v(365, 10.5) * mm, "end": v(365, 9.5) * mm});
            skPoint(sketch, "E838.middle", {"position": v(0, 10) * mm});
            skLineSegment(sketch, "E839.bottom", {"start": v(-365, 15.5) * mm, "end": v(365, 15.5) * mm});
            skLineSegment(sketch, "E839.top", {"start": v(-365, 14.5) * mm, "end": v(365, 14.5) * mm});
            skLineSegment(sketch, "E839.left", {"start": v(-365, 15.5) * mm, "end": v(-365, 14.5) * mm});
            skLineSegment(sketch, "E839.right", {"start": v(365, 15.5) * mm, "end": v(365, 14.5) * mm});
            skPoint(sketch, "E839.middle", {"position": v(0, 15) * mm});
            skLineSegment(sketch, "E840.bottom", {"start": v(-365, 20.5) * mm, "end": v(365, 20.5) * mm});
            skLineSegment(sketch, "E840.top", {"start": v(-365, 19.5) * mm, "end": v(365, 19.5) * mm});
            skLineSegment(sketch, "E840.left", {"start": v(-365, 20.5) * mm, "end": v(-365, 19.5) * mm});
            skLineSegment(sketch, "E840.right", {"start": v(365, 20.5) * mm, "end": v(365, 19.5) * mm});
            skPoint(sketch, "E840.middle", {"position": v(0, 20) * mm});
            skLineSegment(sketch, "E841.bottom", {"start": v(-10.5, 20) * mm, "end": v(-9.5, 20) * mm});
            skLineSegment(sketch, "E841.top", {"start": v(-10.5, 10) * mm, "end": v(-9.5, 10) * mm});
            skLineSegment(sketch, "E841.left", {"start": v(-10.5, 20) * mm, "end": v(-10.5, 10) * mm});
            skLineSegment(sketch, "E841.right", {"start": v(-9.5, 20) * mm, "end": v(-9.5, 10) * mm});
            skPoint(sketch, "E841.middle", {"position": v(-10, 15) * mm});
            skLineSegment(sketch, "E842.bottom", {"start": v(-0.5, 20) * mm, "end": v(0.5, 20) * mm});
            skLineSegment(sketch, "E842.top", {"start": v(-0.5, 10) * mm, "end": v(0.5, 10) * mm});
            skLineSegment(sketch, "E842.left", {"start": v(-0.5, 20) * mm, "end": v(-0.5, 10) * mm});
            skLineSegment(sketch, "E842.right", {"start": v(0.5, 20) * mm, "end": v(0.5, 10) * mm});
            skLineSegment(sketch, "E843.bottom", {"start": v(-51.13, 20) * mm, "end": v(-50.13, 20) * mm});
            skLineSegment(sketch, "E843.top", {"start": v(-51.13, 10) * mm, "end": v(-50.13, 10) * mm});
            skLineSegment(sketch, "E843.left", {"start": v(-51.13, 20) * mm, "end": v(-51.13, 10) * mm});
            skLineSegment(sketch, "E843.right", {"start": v(-50.13, 20) * mm, "end": v(-50.13, 10) * mm});
            skPoint(sketch, "E843.middle", {"position": v(-50.63, 15) * mm});
            skLineSegment(sketch, "E844.bottom", {"start": v(-91.75, 20) * mm, "end": v(-90.75, 20) * mm});
            skLineSegment(sketch, "E844.top", {"start": v(-91.75, 10) * mm, "end": v(-90.75, 10) * mm});
            skLineSegment(sketch, "E844.left", {"start": v(-91.75, 20) * mm, "end": v(-91.75, 10) * mm});
            skLineSegment(sketch, "E844.right", {"start": v(-90.75, 20) * mm, "end": v(-90.75, 10) * mm});
            skPoint(sketch, "E844.middle", {"position": v(-91.25, 15) * mm});
            skLineSegment(sketch, "E845.bottom", {"start": v(-131.38, 20) * mm, "end": v(-132.38, 20) * mm});
            skLineSegment(sketch, "E845.top", {"start": v(-131.38, 10) * mm, "end": v(-132.38, 10) * mm});
            skLineSegment(sketch, "E845.left", {"start": v(-131.38, 20) * mm, "end": v(-131.38, 10) * mm});
            skLineSegment(sketch, "E845.right", {"start": v(-132.38, 20) * mm, "end": v(-132.38, 10) * mm});
            skPoint(sketch, "E845.middle", {"position": v(-131.88, 15) * mm});
            skLineSegment(sketch, "E846.bottom", {"start": v(-173, 20) * mm, "end": v(-172, 20) * mm});
            skLineSegment(sketch, "E846.top", {"start": v(-173, 10) * mm, "end": v(-172, 10) * mm});
            skLineSegment(sketch, "E846.left", {"start": v(-173, 20) * mm, "end": v(-173, 10) * mm});
            skLineSegment(sketch, "E846.right", {"start": v(-172, 20) * mm, "end": v(-172, 10) * mm});
            skPoint(sketch, "E846.middle", {"position": v(-172.5, 15) * mm});
            skLineSegment(sketch, "E847.bottom", {"start": v(-192, 20) * mm, "end": v(-193, 20) * mm});
            skLineSegment(sketch, "E847.top", {"start": v(-192, 10) * mm, "end": v(-193, 10) * mm});
            skLineSegment(sketch, "E847.left", {"start": v(-192, 20) * mm, "end": v(-192, 10) * mm});
            skLineSegment(sketch, "E847.right", {"start": v(-193, 20) * mm, "end": v(-193, 10) * mm});
            skPoint(sketch, "E847.middle", {"position": v(-192.5, 15) * mm});
            skLineSegment(sketch, "E848.bottom", {"start": v(-235.13, 20) * mm, "end": v(-236.13, 20) * mm});
            skLineSegment(sketch, "E848.top", {"start": v(-235.13, 10) * mm, "end": v(-236.13, 10) * mm});
            skLineSegment(sketch, "E848.left", {"start": v(-235.13, 20) * mm, "end": v(-235.13, 10) * mm});
            skLineSegment(sketch, "E848.right", {"start": v(-236.13, 20) * mm, "end": v(-236.13, 10) * mm});
            skPoint(sketch, "E848.middle", {"position": v(-235.63, 15) * mm});
            skLineSegment(sketch, "E849.bottom", {"start": v(-278.25, 20) * mm, "end": v(-279.25, 20) * mm});
            skLineSegment(sketch, "E849.top", {"start": v(-278.25, 10) * mm, "end": v(-279.25, 10) * mm});
            skLineSegment(sketch, "E849.left", {"start": v(-278.25, 20) * mm, "end": v(-278.25, 10) * mm});
            skLineSegment(sketch, "E849.right", {"start": v(-279.25, 20) * mm, "end": v(-279.25, 10) * mm});
            skPoint(sketch, "E849.middle", {"position": v(-278.75, 15) * mm});
            skLineSegment(sketch, "E850.bottom", {"start": v(-321.38, 20) * mm, "end": v(-322.38, 20) * mm});
            skLineSegment(sketch, "E850.top", {"start": v(-321.38, 10) * mm, "end": v(-322.38, 10) * mm});
            skLineSegment(sketch, "E850.left", {"start": v(-321.38, 20) * mm, "end": v(-321.38, 10) * mm});
            skLineSegment(sketch, "E850.right", {"start": v(-322.38, 20) * mm, "end": v(-322.38, 10) * mm});
            skPoint(sketch, "E850.middle", {"position": v(-321.88, 15) * mm});
            skLineSegment(sketch, "E851.MirrorCS", {"start": v(9.5, 20) * mm, "end": v(9.5, 10) * mm});
            skLineSegment(sketch, "E852.MirrorCS", {"start": v(10.5, 20) * mm, "end": v(10.5, 10) * mm});
            skLineSegment(sketch, "E853.MirrorCS", {"start": v(50.13, 20) * mm, "end": v(50.13, 10) * mm});
            skLineSegment(sketch, "E854.MirrorCS", {"start": v(51.13, 20) * mm, "end": v(51.13, 10) * mm});
            skLineSegment(sketch, "E855.MirrorCS", {"start": v(90.75, 20) * mm, "end": v(90.75, 10) * mm});
            skLineSegment(sketch, "E856.MirrorCS", {"start": v(91.75, 20) * mm, "end": v(91.75, 10) * mm});
            skLineSegment(sketch, "E857.MirrorCS", {"start": v(132.38, 20) * mm, "end": v(132.38, 10) * mm});
            skLineSegment(sketch, "E858.MirrorCS", {"start": v(131.38, 20) * mm, "end": v(131.38, 10) * mm});
            skLineSegment(sketch, "E859.MirrorCS", {"start": v(172, 20) * mm, "end": v(172, 10) * mm});
            skLineSegment(sketch, "E860.MirrorCS", {"start": v(173, 20) * mm, "end": v(173, 10) * mm});
            skLineSegment(sketch, "E861.MirrorCS", {"start": v(192, 20) * mm, "end": v(192, 10) * mm});
            skLineSegment(sketch, "E862.MirrorCS", {"start": v(193, 20) * mm, "end": v(193, 10) * mm});
            skLineSegment(sketch, "E863.MirrorCS", {"start": v(235.13, 20) * mm, "end": v(235.13, 10) * mm});
            skLineSegment(sketch, "E864.MirrorCS", {"start": v(236.13, 20) * mm, "end": v(236.13, 10) * mm});
            skLineSegment(sketch, "E865.MirrorCS", {"start": v(321.38, 20) * mm, "end": v(321.38, 10) * mm});
            skLineSegment(sketch, "E866.MirrorCS", {"start": v(322.38, 20) * mm, "end": v(322.38, 10) * mm});
            skSolve(sketch);
        }
        {
            var Q0;
            {var subQ76=sQuery(id+"F25.wireOp",EDGE,"E212.top");Q0=makeQuery(id+"F25.imprint","IMPRINT",FACE,{"disambiguationData":[TD([[makeQuery(id+"F25.imprint","IMPRINT",EDGE,{"derivedFrom":subQ76}),-1.0]])]});}
            extrude(context, id + "F33", {"entities" : qUnion([Q0]), "operationType" : NewBodyOperationType.REMOVE, "depth" : 25 * mm, "offsetDistance" : 25 * mm});
        }
        {
            var Q0;
            {var subQ0=sQuery(id+"F25.wireOp",EDGE,"E533.trimOffspring");var subQ1=sQuery(id+"F25.wireOp",EDGE,"E517.trimOffspring");var subQ2=makeQuery(id+"F25.imprint","INTERSECT",VERTEX,{"derivedFrom":[subQ1,subQ0]});Q0=makeQuery(id+"F25.imprint","IMPRINT",FACE,{"disambiguationData":[TD([[makeQuery(id+"F25.imprint","IMPRINT",EDGE,{"disambiguationData":[TD([[subQ2,-1.0]])],"derivedFrom":subQ1}),1.0]])]});}
            var Q1;
            {var subQ1=sQuery(id+"F25.wireOp",EDGE,"E248.left");var subQ3=sQuery(id+"F25.wireOp",EDGE,"E517.trimOffspring");var subQ4=makeQuery(id+"F25.imprint","INTERSECT",VERTEX,{"derivedFrom":[subQ1,subQ3]});Q1=makeQuery(id+"F25.imprint","IMPRINT",FACE,{"disambiguationData":[TD([[makeQuery(id+"F25.imprint","IMPRINT",EDGE,{"disambiguationData":[TD([[subQ4,1.0]])],"derivedFrom":subQ3}),1.0]])]});}
            var Q2;
            {var subQ0=sQuery(id+"F25.wireOp",EDGE,"E275.trimOffspring");var subQ1=sQuery(id+"F25.wireOp",EDGE,"E248.left");var subQ2=makeQuery(id+"F25.imprint","INTERSECT",VERTEX,{"derivedFrom":[subQ1,subQ0]});Q2=makeQuery(id+"F25.imprint","IMPRINT",FACE,{"disambiguationData":[TD([[makeQuery(id+"F25.imprint","IMPRINT",EDGE,{"disambiguationData":[TD([[subQ2,-1.0]])],"derivedFrom":subQ1}),1.0]])]});}
            var Q3;
            {var subQ0=sQuery(id+"F25.wireOp",EDGE,"E273.trimOffspring");var subQ1=sQuery(id+"F25.wireOp",EDGE,"E248.left");var subQ2=makeQuery(id+"F25.imprint","INTERSECT",VERTEX,{"derivedFrom":[subQ1,subQ0]});Q3=makeQuery(id+"F25.imprint","IMPRINT",FACE,{"disambiguationData":[TD([[makeQuery(id+"F25.imprint","IMPRINT",EDGE,{"disambiguationData":[TD([[subQ2,-1.0]])],"derivedFrom":subQ1}),1.0]])]});}
            var Q4;
            {var subQ0=sQuery(id+"F25.wireOp",EDGE,"E272.trimOffspring");var subQ1=sQuery(id+"F25.wireOp",EDGE,"E248.left");var subQ2=makeQuery(id+"F25.imprint","INTERSECT",VERTEX,{"derivedFrom":[subQ1,subQ0]});Q4=makeQuery(id+"F25.imprint","IMPRINT",FACE,{"disambiguationData":[TD([[makeQuery(id+"F25.imprint","IMPRINT",EDGE,{"disambiguationData":[TD([[subQ2,-1.0]])],"derivedFrom":subQ1}),1.0]])]});}
            var Q5;
            {var subQ0=sQuery(id+"F25.wireOp",EDGE,"E274.trimOffspring");var subQ1=sQuery(id+"F25.wireOp",EDGE,"E248.left");var subQ2=makeQuery(id+"F25.imprint","INTERSECT",VERTEX,{"derivedFrom":[subQ1,subQ0]});Q5=makeQuery(id+"F25.imprint","IMPRINT",FACE,{"disambiguationData":[TD([[makeQuery(id+"F25.imprint","IMPRINT",EDGE,{"disambiguationData":[TD([[subQ2,-1.0]])],"derivedFrom":subQ1}),1.0]])]});}
            var Q6;
            {var subQ0=sQuery(id+"F25.wireOp",EDGE,"E270.trimOffspring");var subQ1=sQuery(id+"F25.wireOp",EDGE,"E248.left");var subQ2=makeQuery(id+"F25.imprint","INTERSECT",VERTEX,{"derivedFrom":[subQ1,subQ0]});Q6=makeQuery(id+"F25.imprint","IMPRINT",FACE,{"disambiguationData":[TD([[makeQuery(id+"F25.imprint","IMPRINT",EDGE,{"disambiguationData":[TD([[subQ2,-1.0]])],"derivedFrom":subQ1}),1.0]])]});}
            var Q7;
            {var subQ0=sQuery(id+"F25.wireOp",EDGE,"E268.trimOffspring");var subQ1=sQuery(id+"F25.wireOp",EDGE,"E248.left");var subQ2=makeQuery(id+"F25.imprint","INTERSECT",VERTEX,{"derivedFrom":[subQ1,subQ0]});Q7=makeQuery(id+"F25.imprint","IMPRINT",FACE,{"disambiguationData":[TD([[makeQuery(id+"F25.imprint","IMPRINT",EDGE,{"disambiguationData":[TD([[subQ2,-1.0]])],"derivedFrom":subQ1}),1.0]])]});}
            var Q8;
            {var subQ0=sQuery(id+"F25.wireOp",EDGE,"E268.trimOffspring");var subQ1=sQuery(id+"F25.wireOp",EDGE,"E246.right");var subQ2=makeQuery(id+"F25.imprint","INTERSECT",VERTEX,{"derivedFrom":[subQ1,subQ0]});Q8=makeQuery(id+"F25.imprint","IMPRINT",FACE,{"disambiguationData":[TD([[makeQuery(id+"F25.imprint","IMPRINT",EDGE,{"disambiguationData":[TD([[subQ2,-1.0]])],"derivedFrom":subQ1}),-1.0]])]});}
            var Q9;
            {var subQ0=sQuery(id+"F25.wireOp",EDGE,"E268.trimOffspring");var subQ1=sQuery(id+"F25.wireOp",EDGE,"E245.right");var subQ2=makeQuery(id+"F25.imprint","INTERSECT",VERTEX,{"derivedFrom":[subQ1,subQ0]});Q9=makeQuery(id+"F25.imprint","IMPRINT",FACE,{"disambiguationData":[TD([[makeQuery(id+"F25.imprint","IMPRINT",EDGE,{"disambiguationData":[TD([[subQ2,-1.0]])],"derivedFrom":subQ1}),-1.0]])]});}
            var Q10;
            {var subQ0=sQuery(id+"F25.wireOp",EDGE,"E268.trimOffspring");var subQ1=sQuery(id+"F25.wireOp",EDGE,"E245.left");var subQ2=makeQuery(id+"F25.imprint","INTERSECT",VERTEX,{"derivedFrom":[subQ1,subQ0]});Q10=makeQuery(id+"F25.imprint","IMPRINT",FACE,{"disambiguationData":[TD([[makeQuery(id+"F25.imprint","IMPRINT",EDGE,{"disambiguationData":[TD([[subQ2,-1.0]])],"derivedFrom":subQ1}),-1.0]])]});}
            var Q11;
            {var subQ0=sQuery(id+"F25.wireOp",EDGE,"E268.trimOffspring");var subQ1=sQuery(id+"F25.wireOp",EDGE,"E244.right");var subQ2=makeQuery(id+"F25.imprint","INTERSECT",VERTEX,{"derivedFrom":[subQ1,subQ0]});Q11=makeQuery(id+"F25.imprint","IMPRINT",FACE,{"disambiguationData":[TD([[makeQuery(id+"F25.imprint","IMPRINT",EDGE,{"disambiguationData":[TD([[subQ2,-1.0]])],"derivedFrom":subQ1}),-1.0]])]});}
            var Q12;
            {var subQ0=sQuery(id+"F25.wireOp",EDGE,"E268.trimOffspring");var subQ1=sQuery(id+"F25.wireOp",EDGE,"E243.left");var subQ2=makeQuery(id+"F25.imprint","INTERSECT",VERTEX,{"derivedFrom":[subQ1,subQ0]});Q12=makeQuery(id+"F25.imprint","IMPRINT",FACE,{"disambiguationData":[TD([[makeQuery(id+"F25.imprint","IMPRINT",EDGE,{"disambiguationData":[TD([[subQ2,-1.0]])],"derivedFrom":subQ1}),-1.0]])]});}
            var Q13;
            {var subQ0=sQuery(id+"F25.wireOp",EDGE,"E269.trimOffspring");var subQ1=sQuery(id+"F25.wireOp",EDGE,"E243.right");var subQ2=makeQuery(id+"F25.imprint","INTERSECT",VERTEX,{"derivedFrom":[subQ1,subQ0]});Q13=makeQuery(id+"F25.imprint","IMPRINT",FACE,{"disambiguationData":[TD([[makeQuery(id+"F25.imprint","IMPRINT",EDGE,{"disambiguationData":[TD([[subQ2,1.0]])],"derivedFrom":subQ1}),-1.0]])]});}
            var Q14;
            {var subQ0=sQuery(id+"F25.wireOp",EDGE,"E267.trimOffspring");var subQ1=sQuery(id+"F25.wireOp",EDGE,"E243.right");var subQ2=makeQuery(id+"F25.imprint","INTERSECT",VERTEX,{"derivedFrom":[subQ1,subQ0]});Q14=makeQuery(id+"F25.imprint","IMPRINT",FACE,{"disambiguationData":[TD([[makeQuery(id+"F25.imprint","IMPRINT",EDGE,{"disambiguationData":[TD([[subQ2,-1.0]])],"derivedFrom":subQ1}),-1.0]])]});}
            var Q15;
            {var subQ0=sQuery(id+"F25.wireOp",EDGE,"E243.bottom");Q15=makeQuery(id+"F25.imprint","IMPRINT",FACE,{"disambiguationData":[TD([[makeQuery(id+"F25.imprint","IMPRINT",EDGE,{"derivedFrom":subQ0}),-1.0]])]});}
            var Q16;
            {var subQ0=sQuery(id+"F25.wireOp",EDGE,"E533.trimOffspring");var subQ1=sQuery(id+"F25.wireOp",EDGE,"E517.trimOffspring");var subQ2=makeQuery(id+"F25.imprint","INTERSECT",VERTEX,{"derivedFrom":[subQ1,subQ0]});Q16=makeQuery(id+"F25.imprint","IMPRINT",FACE,{"disambiguationData":[TD([[makeQuery(id+"F25.imprint","IMPRINT",EDGE,{"disambiguationData":[TD([[subQ2,1.0]])],"derivedFrom":subQ1}),1.0]])]});}
            var Q17;
            {var subQ0=sQuery(id+"F25.wireOp",EDGE,"E532.trimOffspring");var subQ1=sQuery(id+"F25.wireOp",EDGE,"E517.trimOffspring");var subQ2=makeQuery(id+"F25.imprint","INTERSECT",VERTEX,{"derivedFrom":[subQ1,subQ0]});Q17=makeQuery(id+"F25.imprint","IMPRINT",FACE,{"disambiguationData":[TD([[makeQuery(id+"F25.imprint","IMPRINT",EDGE,{"disambiguationData":[TD([[subQ2,-1.0]])],"derivedFrom":subQ1}),1.0]])]});}
            var Q18;
            {var subQ0=sQuery(id+"F25.wireOp",EDGE,"E532.trimOffspring");var subQ1=sQuery(id+"F25.wireOp",EDGE,"E518.trimOffspring");var subQ2=makeQuery(id+"F25.imprint","INTERSECT",VERTEX,{"derivedFrom":[subQ1,subQ0]});Q18=makeQuery(id+"F25.imprint","IMPRINT",FACE,{"disambiguationData":[TD([[makeQuery(id+"F25.imprint","IMPRINT",EDGE,{"disambiguationData":[TD([[subQ2,-1.0]])],"derivedFrom":subQ1}),-1.0]])]});}
            var Q19;
            {var subQ0=sQuery(id+"F25.wireOp",EDGE,"E532.trimOffspring");var subQ1=sQuery(id+"F25.wireOp",EDGE,"E507.trimOffspring");var subQ2=makeQuery(id+"F25.imprint","INTERSECT",VERTEX,{"derivedFrom":[subQ1,subQ0]});Q19=makeQuery(id+"F25.imprint","IMPRINT",FACE,{"disambiguationData":[TD([[makeQuery(id+"F25.imprint","IMPRINT",EDGE,{"disambiguationData":[TD([[subQ2,-1.0]])],"derivedFrom":subQ1}),-1.0]])]});}
            var Q20;
            {var subQ0=sQuery(id+"F25.wireOp",EDGE,"E532.trimOffspring");var subQ1=sQuery(id+"F25.wireOp",EDGE,"E517.trimOffspring");var subQ2=makeQuery(id+"F25.imprint","INTERSECT",VERTEX,{"derivedFrom":[subQ1,subQ0]});Q20=makeQuery(id+"F25.imprint","IMPRINT",FACE,{"disambiguationData":[TD([[makeQuery(id+"F25.imprint","IMPRINT",EDGE,{"disambiguationData":[TD([[subQ2,-1.0]])],"derivedFrom":subQ1}),1.0]])]});}
            var Q21;
            {var subQ0=sQuery(id+"F25.wireOp",EDGE,"E518.trimOffspring");var subQ1=sQuery(id+"F25.wireOp",EDGE,"E247.left");var subQ2=makeQuery(id+"F25.imprint","INTERSECT",VERTEX,{"derivedFrom":[subQ1,subQ0]});Q21=makeQuery(id+"F25.imprint","IMPRINT",FACE,{"disambiguationData":[TD([[makeQuery(id+"F25.imprint","IMPRINT",EDGE,{"disambiguationData":[TD([[subQ2,1.0]])],"derivedFrom":subQ0}),-1.0]])]});}
            var Q22;
            {var subQ0=sQuery(id+"F25.wireOp",EDGE,"E534.MirrorCS");var subQ1=sQuery(id+"F25.wireOp",EDGE,"E518.trimOffspring");var subQ2=makeQuery(id+"F25.imprint","INTERSECT",VERTEX,{"derivedFrom":[subQ1,subQ0]});Q22=makeQuery(id+"F25.imprint","IMPRINT",FACE,{"disambiguationData":[TD([[makeQuery(id+"F25.imprint","IMPRINT",EDGE,{"disambiguationData":[TD([[subQ2,1.0]])],"derivedFrom":subQ1}),-1.0]])]});}
            var Q23;
            {var subQ0=sQuery(id+"F25.wireOp",EDGE,"E527.trimOffspring");var subQ1=sQuery(id+"F25.wireOp",EDGE,"E518.trimOffspring");var subQ2=makeQuery(id+"F25.imprint","INTERSECT",VERTEX,{"derivedFrom":[subQ1,subQ0]});Q23=makeQuery(id+"F25.imprint","IMPRINT",FACE,{"disambiguationData":[TD([[makeQuery(id+"F25.imprint","IMPRINT",EDGE,{"disambiguationData":[TD([[subQ2,-1.0]])],"derivedFrom":subQ1}),-1.0]])]});}
            var Q24;
            {var subQ0=sQuery(id+"F25.wireOp",EDGE,"E532.trimOffspring");var subQ1=sQuery(id+"F25.wireOp",EDGE,"E507.trimOffspring");var subQ2=makeQuery(id+"F25.imprint","INTERSECT",VERTEX,{"derivedFrom":[subQ1,subQ0]});Q24=makeQuery(id+"F25.imprint","IMPRINT",FACE,{"disambiguationData":[TD([[makeQuery(id+"F25.imprint","IMPRINT",EDGE,{"disambiguationData":[TD([[subQ2,-1.0]])],"derivedFrom":subQ1}),1.0]])]});}
            var Q25;
            {var subQ0=sQuery(id+"F25.wireOp",EDGE,"E527.trimOffspring");var subQ1=sQuery(id+"F25.wireOp",EDGE,"E507.trimOffspring");var subQ2=makeQuery(id+"F25.imprint","INTERSECT",VERTEX,{"derivedFrom":[subQ1,subQ0]});Q25=makeQuery(id+"F25.imprint","IMPRINT",FACE,{"disambiguationData":[TD([[makeQuery(id+"F25.imprint","IMPRINT",EDGE,{"disambiguationData":[TD([[subQ2,-1.0]])],"derivedFrom":subQ1}),1.0]])]});}
            var Q26;
            {var subQ0=sQuery(id+"F25.wireOp",EDGE,"E535.trimOffspring");var subQ1=sQuery(id+"F25.wireOp",EDGE,"E507.trimOffspring");var subQ2=makeQuery(id+"F25.imprint","INTERSECT",VERTEX,{"derivedFrom":[subQ1,subQ0]});Q26=makeQuery(id+"F25.imprint","IMPRINT",FACE,{"disambiguationData":[TD([[makeQuery(id+"F25.imprint","IMPRINT",EDGE,{"disambiguationData":[TD([[subQ2,1.0]])],"derivedFrom":subQ1}),1.0]])]});}
            var Q27;
            {var subQ0=sQuery(id+"F25.wireOp",EDGE,"E527.trimOffspring");var subQ1=sQuery(id+"F25.wireOp",EDGE,"E507.trimOffspring");var subQ2=makeQuery(id+"F25.imprint","INTERSECT",VERTEX,{"derivedFrom":[subQ1,subQ0]});Q27=makeQuery(id+"F25.imprint","IMPRINT",FACE,{"disambiguationData":[TD([[makeQuery(id+"F25.imprint","IMPRINT",EDGE,{"disambiguationData":[TD([[subQ2,-1.0]])],"derivedFrom":subQ1}),-1.0]])]});}
            var Q28;
            {var subQ0=sQuery(id+"F25.wireOp",EDGE,"E520.trimOffspring");var subQ1=sQuery(id+"F25.wireOp",EDGE,"E507.trimOffspring");var subQ2=makeQuery(id+"F25.imprint","INTERSECT",VERTEX,{"derivedFrom":[subQ1,subQ0]});Q28=makeQuery(id+"F25.imprint","IMPRINT",FACE,{"disambiguationData":[TD([[makeQuery(id+"F25.imprint","IMPRINT",EDGE,{"disambiguationData":[TD([[subQ2,1.0]])],"derivedFrom":subQ1}),1.0]])]});}
            var Q29;
            {var subQ0=sQuery(id+"F25.wireOp",EDGE,"E523.trimOffspring");var subQ1=sQuery(id+"F25.wireOp",EDGE,"E507.trimOffspring");var subQ2=makeQuery(id+"F25.imprint","INTERSECT",VERTEX,{"derivedFrom":[subQ1,subQ0]});Q29=makeQuery(id+"F25.imprint","IMPRINT",FACE,{"disambiguationData":[TD([[makeQuery(id+"F25.imprint","IMPRINT",EDGE,{"disambiguationData":[TD([[subQ2,1.0]])],"derivedFrom":subQ1}),1.0]])]});}
            var Q30;
            {var subQ0=sQuery(id+"F25.wireOp",EDGE,"E532.trimOffspring");var subQ1=sQuery(id+"F25.wireOp",EDGE,"E510.trimOffspring");var subQ2=makeQuery(id+"F25.imprint","INTERSECT",VERTEX,{"derivedFrom":[subQ1,subQ0]});Q30=makeQuery(id+"F25.imprint","IMPRINT",FACE,{"disambiguationData":[TD([[makeQuery(id+"F25.imprint","IMPRINT",EDGE,{"disambiguationData":[TD([[subQ2,-1.0]])],"derivedFrom":subQ1}),-1.0]])]});}
            var Q31;
            {var subQ0=sQuery(id+"F25.wireOp",EDGE,"E527.trimOffspring");var subQ1=sQuery(id+"F25.wireOp",EDGE,"E510.trimOffspring");var subQ2=makeQuery(id+"F25.imprint","INTERSECT",VERTEX,{"derivedFrom":[subQ1,subQ0]});Q31=makeQuery(id+"F25.imprint","IMPRINT",FACE,{"disambiguationData":[TD([[makeQuery(id+"F25.imprint","IMPRINT",EDGE,{"disambiguationData":[TD([[subQ2,-1.0]])],"derivedFrom":subQ1}),-1.0]])]});}
            var Q32;
            {var subQ0=sQuery(id+"F25.wireOp",EDGE,"E533.trimOffspring");var subQ1=sQuery(id+"F25.wireOp",EDGE,"E510.trimOffspring");var subQ2=makeQuery(id+"F25.imprint","INTERSECT",VERTEX,{"derivedFrom":[subQ1,subQ0]});Q32=makeQuery(id+"F25.imprint","IMPRINT",FACE,{"disambiguationData":[TD([[makeQuery(id+"F25.imprint","IMPRINT",EDGE,{"disambiguationData":[TD([[subQ2,-1.0]])],"derivedFrom":subQ1}),-1.0]])]});}
            var Q33;
            {var subQ0=sQuery(id+"F25.wireOp",EDGE,"E532.trimOffspring");var subQ1=sQuery(id+"F25.wireOp",EDGE,"E510.trimOffspring");var subQ2=makeQuery(id+"F25.imprint","INTERSECT",VERTEX,{"derivedFrom":[subQ1,subQ0]});Q33=makeQuery(id+"F25.imprint","IMPRINT",FACE,{"disambiguationData":[TD([[makeQuery(id+"F25.imprint","IMPRINT",EDGE,{"disambiguationData":[TD([[subQ2,-1.0]])],"derivedFrom":subQ1}),-1.0]])]});}
            var Q34;
            {var subQ0=sQuery(id+"F25.wireOp",EDGE,"E535.trimOffspring");var subQ1=sQuery(id+"F25.wireOp",EDGE,"E510.trimOffspring");var subQ2=makeQuery(id+"F25.imprint","INTERSECT",VERTEX,{"derivedFrom":[subQ1,subQ0]});Q34=makeQuery(id+"F25.imprint","IMPRINT",FACE,{"disambiguationData":[TD([[makeQuery(id+"F25.imprint","IMPRINT",EDGE,{"disambiguationData":[TD([[subQ2,-1.0]])],"derivedFrom":subQ1}),-1.0]])]});}
            var Q35;
            {var subQ0=sQuery(id+"F25.wireOp",EDGE,"E520.trimOffspring");var subQ1=sQuery(id+"F25.wireOp",EDGE,"E510.trimOffspring");var subQ2=makeQuery(id+"F25.imprint","INTERSECT",VERTEX,{"derivedFrom":[subQ1,subQ0]});Q35=makeQuery(id+"F25.imprint","IMPRINT",FACE,{"disambiguationData":[TD([[makeQuery(id+"F25.imprint","IMPRINT",EDGE,{"disambiguationData":[TD([[subQ2,-1.0]])],"derivedFrom":subQ1}),-1.0]])]});}
            var Q36;
            {var subQ0=sQuery(id+"F25.wireOp",EDGE,"E518.trimOffspring");var subQ5=sQuery(id+"F25.wireOp",EDGE,"E248.right");var subQ7=makeQuery(id+"F25.imprint","INTERSECT",VERTEX,{"derivedFrom":[subQ5,subQ0]});Q36=makeQuery(id+"F25.imprint","IMPRINT",FACE,{"disambiguationData":[TD([[makeQuery(id+"F25.imprint","IMPRINT",EDGE,{"disambiguationData":[TD([[subQ7,1.0]])],"derivedFrom":subQ5}),1.0]])]});}
            var Q37;
            {var subQ3=sQuery(id+"F25.wireOp",EDGE,"E517.trimOffspring");var subQ5=sQuery(id+"F25.wireOp",EDGE,"E248.right");var subQ6=makeQuery(id+"F25.imprint","INTERSECT",VERTEX,{"derivedFrom":[subQ5,subQ3]});Q37=makeQuery(id+"F25.imprint","IMPRINT",FACE,{"disambiguationData":[TD([[makeQuery(id+"F25.imprint","IMPRINT",EDGE,{"disambiguationData":[TD([[subQ6,-1.0]])],"derivedFrom":subQ5}),1.0]])]});}
            var Q38;
            {var subQ0=sQuery(id+"F25.wireOp",EDGE,"E275.trimOffspring");var subQ1=sQuery(id+"F25.wireOp",EDGE,"E248.left");var subQ2=makeQuery(id+"F25.imprint","INTERSECT",VERTEX,{"derivedFrom":[subQ1,subQ0]});Q38=makeQuery(id+"F25.imprint","IMPRINT",FACE,{"disambiguationData":[TD([[makeQuery(id+"F25.imprint","IMPRINT",EDGE,{"disambiguationData":[TD([[subQ2,-1.0]])],"derivedFrom":subQ1}),-1.0]])]});}
            var Q39;
            {var subQ0=sQuery(id+"F25.wireOp",EDGE,"E273.trimOffspring");var subQ1=sQuery(id+"F25.wireOp",EDGE,"E248.left");var subQ2=makeQuery(id+"F25.imprint","INTERSECT",VERTEX,{"derivedFrom":[subQ1,subQ0]});Q39=makeQuery(id+"F25.imprint","IMPRINT",FACE,{"disambiguationData":[TD([[makeQuery(id+"F25.imprint","IMPRINT",EDGE,{"disambiguationData":[TD([[subQ2,-1.0]])],"derivedFrom":subQ1}),-1.0]])]});}
            var Q40;
            {var subQ0=sQuery(id+"F25.wireOp",EDGE,"E272.trimOffspring");var subQ1=sQuery(id+"F25.wireOp",EDGE,"E248.left");var subQ2=makeQuery(id+"F25.imprint","INTERSECT",VERTEX,{"derivedFrom":[subQ1,subQ0]});Q40=makeQuery(id+"F25.imprint","IMPRINT",FACE,{"disambiguationData":[TD([[makeQuery(id+"F25.imprint","IMPRINT",EDGE,{"disambiguationData":[TD([[subQ2,-1.0]])],"derivedFrom":subQ1}),-1.0]])]});}
            var Q41;
            {var subQ0=sQuery(id+"F25.wireOp",EDGE,"E272.trimOffspring");var subQ1=sQuery(id+"F25.wireOp",EDGE,"E246.right");var subQ2=makeQuery(id+"F25.imprint","INTERSECT",VERTEX,{"derivedFrom":[subQ1,subQ0]});Q41=makeQuery(id+"F25.imprint","IMPRINT",FACE,{"disambiguationData":[TD([[makeQuery(id+"F25.imprint","IMPRINT",EDGE,{"disambiguationData":[TD([[subQ2,-1.0]])],"derivedFrom":subQ1}),-1.0]])]});}
            var Q42;
            {var subQ0=sQuery(id+"F25.wireOp",EDGE,"E272.trimOffspring");var subQ1=sQuery(id+"F25.wireOp",EDGE,"E245.left");var subQ2=makeQuery(id+"F25.imprint","INTERSECT",VERTEX,{"derivedFrom":[subQ1,subQ0]});Q42=makeQuery(id+"F25.imprint","IMPRINT",FACE,{"disambiguationData":[TD([[makeQuery(id+"F25.imprint","IMPRINT",EDGE,{"disambiguationData":[TD([[subQ2,-1.0]])],"derivedFrom":subQ1}),-1.0]])]});}
            var Q43;
            {var subQ0=sQuery(id+"F25.wireOp",EDGE,"E273.trimOffspring");var subQ1=sQuery(id+"F25.wireOp",EDGE,"E245.right");var subQ2=makeQuery(id+"F25.imprint","INTERSECT",VERTEX,{"derivedFrom":[subQ1,subQ0]});Q43=makeQuery(id+"F25.imprint","IMPRINT",FACE,{"disambiguationData":[TD([[makeQuery(id+"F25.imprint","IMPRINT",EDGE,{"disambiguationData":[TD([[subQ2,1.0]])],"derivedFrom":subQ1}),-1.0]])]});}
            var Q44;
            {var subQ0=sQuery(id+"F25.wireOp",EDGE,"E272.trimOffspring");var subQ1=sQuery(id+"F25.wireOp",EDGE,"E244.right");var subQ2=makeQuery(id+"F25.imprint","INTERSECT",VERTEX,{"derivedFrom":[subQ1,subQ0]});Q44=makeQuery(id+"F25.imprint","IMPRINT",FACE,{"disambiguationData":[TD([[makeQuery(id+"F25.imprint","IMPRINT",EDGE,{"disambiguationData":[TD([[subQ2,-1.0]])],"derivedFrom":subQ1}),-1.0]])]});}
            var Q45;
            {var subQ0=sQuery(id+"F25.wireOp",EDGE,"E272.trimOffspring");var subQ1=sQuery(id+"F25.wireOp",EDGE,"E243.left");var subQ2=makeQuery(id+"F25.imprint","INTERSECT",VERTEX,{"derivedFrom":[subQ1,subQ0]});Q45=makeQuery(id+"F25.imprint","IMPRINT",FACE,{"disambiguationData":[TD([[makeQuery(id+"F25.imprint","IMPRINT",EDGE,{"disambiguationData":[TD([[subQ2,-1.0]])],"derivedFrom":subQ1}),-1.0]])]});}
            var Q46;
            {var subQ0=sQuery(id+"F25.wireOp",EDGE,"E271.trimOffspring");var subQ1=sQuery(id+"F25.wireOp",EDGE,"E243.left");var subQ2=makeQuery(id+"F25.imprint","INTERSECT",VERTEX,{"derivedFrom":[subQ1,subQ0]});Q46=makeQuery(id+"F25.imprint","IMPRINT",FACE,{"disambiguationData":[TD([[makeQuery(id+"F25.imprint","IMPRINT",EDGE,{"disambiguationData":[TD([[subQ2,-1.0]])],"derivedFrom":subQ1}),-1.0]])]});}
            var Q47;
            {var subQ0=sQuery(id+"F25.wireOp",EDGE,"E270.trimOffspring");var subQ1=sQuery(id+"F25.wireOp",EDGE,"E243.left");var subQ2=makeQuery(id+"F25.imprint","INTERSECT",VERTEX,{"derivedFrom":[subQ1,subQ0]});Q47=makeQuery(id+"F25.imprint","IMPRINT",FACE,{"disambiguationData":[TD([[makeQuery(id+"F25.imprint","IMPRINT",EDGE,{"disambiguationData":[TD([[subQ2,-1.0]])],"derivedFrom":subQ1}),-1.0]])]});}
            var Q48;
            {var subQ0=sQuery(id+"F25.wireOp",EDGE,"E274.trimOffspring");var subQ1=sQuery(id+"F25.wireOp",EDGE,"E243.left");var subQ2=makeQuery(id+"F25.imprint","INTERSECT",VERTEX,{"derivedFrom":[subQ1,subQ0]});Q48=makeQuery(id+"F25.imprint","IMPRINT",FACE,{"disambiguationData":[TD([[makeQuery(id+"F25.imprint","IMPRINT",EDGE,{"disambiguationData":[TD([[subQ2,-1.0]])],"derivedFrom":subQ1}),-1.0]])]});}
            var Q49;
            {var subQ0=sQuery(id+"F25.wireOp",EDGE,"E269.trimOffspring");var subQ1=sQuery(id+"F25.wireOp",EDGE,"E243.left");var subQ2=makeQuery(id+"F25.imprint","INTERSECT",VERTEX,{"derivedFrom":[subQ1,subQ0]});Q49=makeQuery(id+"F25.imprint","IMPRINT",FACE,{"disambiguationData":[TD([[makeQuery(id+"F25.imprint","IMPRINT",EDGE,{"disambiguationData":[TD([[subQ2,-1.0]])],"derivedFrom":subQ1}),-1.0]])]});}
            var Q50;
            {var subQ0=sQuery(id+"F25.wireOp",EDGE,"E274.trimOffspring");var subQ1=sQuery(id+"F25.wireOp",EDGE,"E244.right");var subQ2=makeQuery(id+"F25.imprint","INTERSECT",VERTEX,{"derivedFrom":[subQ1,subQ0]});Q50=makeQuery(id+"F25.imprint","IMPRINT",FACE,{"disambiguationData":[TD([[makeQuery(id+"F25.imprint","IMPRINT",EDGE,{"disambiguationData":[TD([[subQ2,-1.0]])],"derivedFrom":subQ1}),-1.0]])]});}
            var Q51;
            {var subQ0=sQuery(id+"F25.wireOp",EDGE,"E270.trimOffspring");var subQ1=sQuery(id+"F25.wireOp",EDGE,"E244.right");var subQ2=makeQuery(id+"F25.imprint","INTERSECT",VERTEX,{"derivedFrom":[subQ1,subQ0]});Q51=makeQuery(id+"F25.imprint","IMPRINT",FACE,{"disambiguationData":[TD([[makeQuery(id+"F25.imprint","IMPRINT",EDGE,{"disambiguationData":[TD([[subQ2,-1.0]])],"derivedFrom":subQ1}),-1.0]])]});}
            var Q52;
            {var subQ0=sQuery(id+"F25.wireOp",EDGE,"E274.trimOffspring");var subQ1=sQuery(id+"F25.wireOp",EDGE,"E245.right");var subQ2=makeQuery(id+"F25.imprint","INTERSECT",VERTEX,{"derivedFrom":[subQ1,subQ0]});Q52=makeQuery(id+"F25.imprint","IMPRINT",FACE,{"disambiguationData":[TD([[makeQuery(id+"F25.imprint","IMPRINT",EDGE,{"disambiguationData":[TD([[subQ2,-1.0]])],"derivedFrom":subQ1}),-1.0]])]});}
            var Q53;
            {var subQ0=sQuery(id+"F25.wireOp",EDGE,"E270.trimOffspring");var subQ1=sQuery(id+"F25.wireOp",EDGE,"E245.right");var subQ2=makeQuery(id+"F25.imprint","INTERSECT",VERTEX,{"derivedFrom":[subQ1,subQ0]});Q53=makeQuery(id+"F25.imprint","IMPRINT",FACE,{"disambiguationData":[TD([[makeQuery(id+"F25.imprint","IMPRINT",EDGE,{"disambiguationData":[TD([[subQ2,-1.0]])],"derivedFrom":subQ1}),-1.0]])]});}
            var Q54;
            {var subQ0=sQuery(id+"F25.wireOp",EDGE,"E274.trimOffspring");var subQ1=sQuery(id+"F25.wireOp",EDGE,"E245.left");var subQ2=makeQuery(id+"F25.imprint","INTERSECT",VERTEX,{"derivedFrom":[subQ1,subQ0]});Q54=makeQuery(id+"F25.imprint","IMPRINT",FACE,{"disambiguationData":[TD([[makeQuery(id+"F25.imprint","IMPRINT",EDGE,{"disambiguationData":[TD([[subQ2,-1.0]])],"derivedFrom":subQ1}),-1.0]])]});}
            var Q55;
            {var subQ0=sQuery(id+"F25.wireOp",EDGE,"E270.trimOffspring");var subQ1=sQuery(id+"F25.wireOp",EDGE,"E245.left");var subQ2=makeQuery(id+"F25.imprint","INTERSECT",VERTEX,{"derivedFrom":[subQ1,subQ0]});Q55=makeQuery(id+"F25.imprint","IMPRINT",FACE,{"disambiguationData":[TD([[makeQuery(id+"F25.imprint","IMPRINT",EDGE,{"disambiguationData":[TD([[subQ2,-1.0]])],"derivedFrom":subQ1}),-1.0]])]});}
            var Q56;
            {var subQ0=sQuery(id+"F25.wireOp",EDGE,"E274.trimOffspring");var subQ1=sQuery(id+"F25.wireOp",EDGE,"E246.right");var subQ2=makeQuery(id+"F25.imprint","INTERSECT",VERTEX,{"derivedFrom":[subQ1,subQ0]});Q56=makeQuery(id+"F25.imprint","IMPRINT",FACE,{"disambiguationData":[TD([[makeQuery(id+"F25.imprint","IMPRINT",EDGE,{"disambiguationData":[TD([[subQ2,-1.0]])],"derivedFrom":subQ1}),-1.0]])]});}
            var Q57;
            {var subQ0=sQuery(id+"F25.wireOp",EDGE,"E270.trimOffspring");var subQ1=sQuery(id+"F25.wireOp",EDGE,"E246.right");var subQ2=makeQuery(id+"F25.imprint","INTERSECT",VERTEX,{"derivedFrom":[subQ1,subQ0]});Q57=makeQuery(id+"F25.imprint","IMPRINT",FACE,{"disambiguationData":[TD([[makeQuery(id+"F25.imprint","IMPRINT",EDGE,{"disambiguationData":[TD([[subQ2,-1.0]])],"derivedFrom":subQ1}),-1.0]])]});}
            var Q58;
            {var subQ0=sQuery(id+"F25.wireOp",EDGE,"E270.trimOffspring");var subQ1=sQuery(id+"F25.wireOp",EDGE,"E248.left");var subQ2=makeQuery(id+"F25.imprint","INTERSECT",VERTEX,{"derivedFrom":[subQ1,subQ0]});Q58=makeQuery(id+"F25.imprint","IMPRINT",FACE,{"disambiguationData":[TD([[makeQuery(id+"F25.imprint","IMPRINT",EDGE,{"disambiguationData":[TD([[subQ2,-1.0]])],"derivedFrom":subQ1}),-1.0]])]});}
            var Q59;
            {var subQ0=sQuery(id+"F25.wireOp",EDGE,"E274.trimOffspring");var subQ1=sQuery(id+"F25.wireOp",EDGE,"E248.left");var subQ2=makeQuery(id+"F25.imprint","INTERSECT",VERTEX,{"derivedFrom":[subQ1,subQ0]});Q59=makeQuery(id+"F25.imprint","IMPRINT",FACE,{"disambiguationData":[TD([[makeQuery(id+"F25.imprint","IMPRINT",EDGE,{"disambiguationData":[TD([[subQ2,-1.0]])],"derivedFrom":subQ1}),-1.0]])]});}
            var Q60;
            {var subQ0=sQuery(id+"F25.wireOp",EDGE,"E244.bottom");Q60=makeQuery(id+"F25.imprint","IMPRINT",FACE,{"disambiguationData":[TD([[makeQuery(id+"F25.imprint","IMPRINT",EDGE,{"derivedFrom":subQ0}),1.0]])]});}
            var Q61;
            {var subQ0=sQuery(id+"F25.wireOp",EDGE,"E267.trimOffspring");var subQ1=sQuery(id+"F25.wireOp",EDGE,"E243.left");var subQ2=makeQuery(id+"F25.imprint","INTERSECT",VERTEX,{"derivedFrom":[subQ1,subQ0]});Q61=makeQuery(id+"F25.imprint","IMPRINT",FACE,{"disambiguationData":[TD([[makeQuery(id+"F25.imprint","IMPRINT",EDGE,{"disambiguationData":[TD([[subQ2,-1.0]])],"derivedFrom":subQ1}),-1.0]])]});}
            var Q62;
            {var subQ0=sQuery(id+"F25.wireOp",EDGE,"E267.trimOffspring");var subQ1=sQuery(id+"F25.wireOp",EDGE,"E244.right");var subQ2=makeQuery(id+"F25.imprint","INTERSECT",VERTEX,{"derivedFrom":[subQ1,subQ0]});Q62=makeQuery(id+"F25.imprint","IMPRINT",FACE,{"disambiguationData":[TD([[makeQuery(id+"F25.imprint","IMPRINT",EDGE,{"disambiguationData":[TD([[subQ2,-1.0]])],"derivedFrom":subQ1}),-1.0]])]});}
            var Q63;
            {var subQ0=sQuery(id+"F25.wireOp",EDGE,"E267.trimOffspring");var subQ1=sQuery(id+"F25.wireOp",EDGE,"E245.right");var subQ2=makeQuery(id+"F25.imprint","INTERSECT",VERTEX,{"derivedFrom":[subQ1,subQ0]});Q63=makeQuery(id+"F25.imprint","IMPRINT",FACE,{"disambiguationData":[TD([[makeQuery(id+"F25.imprint","IMPRINT",EDGE,{"disambiguationData":[TD([[subQ2,-1.0]])],"derivedFrom":subQ1}),-1.0]])]});}
            var Q64;
            {var subQ0=sQuery(id+"F25.wireOp",EDGE,"E267.trimOffspring");var subQ1=sQuery(id+"F25.wireOp",EDGE,"E245.left");var subQ2=makeQuery(id+"F25.imprint","INTERSECT",VERTEX,{"derivedFrom":[subQ1,subQ0]});Q64=makeQuery(id+"F25.imprint","IMPRINT",FACE,{"disambiguationData":[TD([[makeQuery(id+"F25.imprint","IMPRINT",EDGE,{"disambiguationData":[TD([[subQ2,-1.0]])],"derivedFrom":subQ1}),-1.0]])]});}
            var Q65;
            {var subQ0=sQuery(id+"F25.wireOp",EDGE,"E267.trimOffspring");var subQ1=sQuery(id+"F25.wireOp",EDGE,"E246.right");var subQ2=makeQuery(id+"F25.imprint","INTERSECT",VERTEX,{"derivedFrom":[subQ1,subQ0]});Q65=makeQuery(id+"F25.imprint","IMPRINT",FACE,{"disambiguationData":[TD([[makeQuery(id+"F25.imprint","IMPRINT",EDGE,{"disambiguationData":[TD([[subQ2,-1.0]])],"derivedFrom":subQ1}),-1.0]])]});}
            var Q66;
            {var subQ0=sQuery(id+"F25.wireOp",EDGE,"E267.trimOffspring");var subQ1=sQuery(id+"F25.wireOp",EDGE,"E248.left");var subQ2=makeQuery(id+"F25.imprint","INTERSECT",VERTEX,{"derivedFrom":[subQ1,subQ0]});Q66=makeQuery(id+"F25.imprint","IMPRINT",FACE,{"disambiguationData":[TD([[makeQuery(id+"F25.imprint","IMPRINT",EDGE,{"disambiguationData":[TD([[subQ2,-1.0]])],"derivedFrom":subQ1}),1.0]])]});}
            var Q67;
            {var subQ0=sQuery(id+"F25.wireOp",EDGE,"E267.trimOffspring");var subQ1=sQuery(id+"F25.wireOp",EDGE,"E248.left");var subQ2=makeQuery(id+"F25.imprint","INTERSECT",VERTEX,{"derivedFrom":[subQ1,subQ0]});Q67=makeQuery(id+"F25.imprint","IMPRINT",FACE,{"disambiguationData":[TD([[makeQuery(id+"F25.imprint","IMPRINT",EDGE,{"disambiguationData":[TD([[subQ2,-1.0]])],"derivedFrom":subQ1}),-1.0]])]});}
            var Q68;
            {var subQ0=sQuery(id+"F25.wireOp",EDGE,"E268.trimOffspring");var subQ1=sQuery(id+"F25.wireOp",EDGE,"E248.left");var subQ2=makeQuery(id+"F25.imprint","INTERSECT",VERTEX,{"derivedFrom":[subQ1,subQ0]});Q68=makeQuery(id+"F25.imprint","IMPRINT",FACE,{"disambiguationData":[TD([[makeQuery(id+"F25.imprint","IMPRINT",EDGE,{"disambiguationData":[TD([[subQ2,-1.0]])],"derivedFrom":subQ1}),-1.0]])]});}
            var Q69;
            {var subQ0=sQuery(id+"F25.wireOp",EDGE,"E535.trimOffspring");var subQ1=sQuery(id+"F25.wireOp",EDGE,"E510.trimOffspring");var subQ2=makeQuery(id+"F25.imprint","INTERSECT",VERTEX,{"derivedFrom":[subQ1,subQ0]});Q69=makeQuery(id+"F25.imprint","IMPRINT",FACE,{"disambiguationData":[TD([[makeQuery(id+"F25.imprint","IMPRINT",EDGE,{"disambiguationData":[TD([[subQ2,-1.0]])],"derivedFrom":subQ1}),1.0]])]});}
            var Q70;
            {var subQ0=sQuery(id+"F25.wireOp",EDGE,"E520.trimOffspring");var subQ1=sQuery(id+"F25.wireOp",EDGE,"E510.trimOffspring");var subQ2=makeQuery(id+"F25.imprint","INTERSECT",VERTEX,{"derivedFrom":[subQ1,subQ0]});Q70=makeQuery(id+"F25.imprint","IMPRINT",FACE,{"disambiguationData":[TD([[makeQuery(id+"F25.imprint","IMPRINT",EDGE,{"disambiguationData":[TD([[subQ2,-1.0]])],"derivedFrom":subQ1}),1.0]])]});}
            var Q71;
            {var subQ0=sQuery(id+"F25.wireOp",EDGE,"E535.trimOffspring");var subQ1=sQuery(id+"F25.wireOp",EDGE,"E522.trimOffspring");var subQ2=makeQuery(id+"F25.imprint","INTERSECT",VERTEX,{"derivedFrom":[subQ1,subQ0]});Q71=makeQuery(id+"F25.imprint","IMPRINT",FACE,{"disambiguationData":[TD([[makeQuery(id+"F25.imprint","IMPRINT",EDGE,{"disambiguationData":[TD([[subQ2,-1.0]])],"derivedFrom":subQ1}),1.0]])]});}
            var Q72;
            {var subQ1=sQuery(id+"F25.wireOp",EDGE,"E522.trimOffspring");var subQ3=sQuery(id+"F25.wireOp",EDGE,"E520.trimOffspring");var subQ4=makeQuery(id+"F25.imprint","INTERSECT",VERTEX,{"derivedFrom":[subQ1,subQ3]});Q72=makeQuery(id+"F25.imprint","IMPRINT",FACE,{"disambiguationData":[TD([[makeQuery(id+"F25.imprint","IMPRINT",EDGE,{"disambiguationData":[TD([[subQ4,-1.0]])],"derivedFrom":subQ3}),-1.0]])]});}
            var Q73;
            {var subQ0=sQuery(id+"F25.wireOp",EDGE,"E537.MirrorCS");var subQ1=sQuery(id+"F25.wireOp",EDGE,"E520.trimOffspring");var subQ2=makeQuery(id+"F25.imprint","INTERSECT",VERTEX,{"derivedFrom":[subQ1,subQ0]});Q73=makeQuery(id+"F25.imprint","IMPRINT",FACE,{"disambiguationData":[TD([[makeQuery(id+"F25.imprint","IMPRINT",EDGE,{"disambiguationData":[TD([[subQ2,1.0]])],"derivedFrom":subQ1}),1.0]])]});}
            var Q74;
            {var subQ0=sQuery(id+"F25.wireOp",EDGE,"E537.MirrorCS");var subQ1=sQuery(id+"F25.wireOp",EDGE,"E520.trimOffspring");var subQ2=makeQuery(id+"F25.imprint","INTERSECT",VERTEX,{"derivedFrom":[subQ1,subQ0]});Q74=makeQuery(id+"F25.imprint","IMPRINT",FACE,{"disambiguationData":[TD([[makeQuery(id+"F25.imprint","IMPRINT",EDGE,{"disambiguationData":[TD([[subQ2,1.0]])],"derivedFrom":subQ1}),-1.0]])]});}
            var Q75;
            {var subQ0=sQuery(id+"F25.wireOp",EDGE,"E522.trimOffspring");var subQ1=sQuery(id+"F25.wireOp",EDGE,"E276.trimOffspring");var subQ2=makeQuery(id+"F25.imprint","INTERSECT",VERTEX,{"derivedFrom":[subQ1,subQ0]});Q75=makeQuery(id+"F25.imprint","IMPRINT",FACE,{"disambiguationData":[TD([[makeQuery(id+"F25.imprint","IMPRINT",EDGE,{"disambiguationData":[TD([[subQ2,-1.0]])],"derivedFrom":subQ1}),1.0]])]});}
            var Q76;
            {var subQ0=sQuery(id+"F25.wireOp",EDGE,"E525.trimOffspring");var subQ1=sQuery(id+"F25.wireOp",EDGE,"E276.trimOffspring");var subQ2=makeQuery(id+"F25.imprint","INTERSECT",VERTEX,{"derivedFrom":[subQ1,subQ0]});Q76=makeQuery(id+"F25.imprint","IMPRINT",FACE,{"disambiguationData":[TD([[makeQuery(id+"F25.imprint","IMPRINT",EDGE,{"disambiguationData":[TD([[subQ2,1.0]])],"derivedFrom":subQ1}),1.0]])]});}
            var Q77;
            {var subQ0=sQuery(id+"F25.wireOp",EDGE,"E517.trimOffspring");var subQ1=sQuery(id+"F25.wireOp",EDGE,"E276.trimOffspring");var subQ2=makeQuery(id+"F25.imprint","INTERSECT",VERTEX,{"derivedFrom":[subQ1,subQ0]});Q77=makeQuery(id+"F25.imprint","IMPRINT",FACE,{"disambiguationData":[TD([[makeQuery(id+"F25.imprint","IMPRINT",EDGE,{"disambiguationData":[TD([[subQ2,-1.0]])],"derivedFrom":subQ1}),-1.0]])]});}
            var Q78;
            {var subQ0=sQuery(id+"F25.wireOp",EDGE,"E517.trimOffspring");var subQ1=sQuery(id+"F25.wireOp",EDGE,"E277.trimOffspring");var subQ2=makeQuery(id+"F25.imprint","INTERSECT",VERTEX,{"derivedFrom":[subQ1,subQ0]});Q78=makeQuery(id+"F25.imprint","IMPRINT",FACE,{"disambiguationData":[TD([[makeQuery(id+"F25.imprint","IMPRINT",EDGE,{"disambiguationData":[TD([[subQ2,-1.0]])],"derivedFrom":subQ1}),-1.0]])]});}
            var Q79;
            {var subQ0=sQuery(id+"F25.wireOp",EDGE,"E519.trimOffspring");var subQ1=sQuery(id+"F25.wireOp",EDGE,"E277.trimOffspring");var subQ2=makeQuery(id+"F25.imprint","INTERSECT",VERTEX,{"derivedFrom":[subQ1,subQ0]});Q79=makeQuery(id+"F25.imprint","IMPRINT",FACE,{"disambiguationData":[TD([[makeQuery(id+"F25.imprint","IMPRINT",EDGE,{"disambiguationData":[TD([[subQ2,-1.0]])],"derivedFrom":subQ1}),-1.0]])]});}
            var Q80;
            {var subQ0=sQuery(id+"F25.wireOp",EDGE,"E519.trimOffspring");var subQ1=sQuery(id+"F25.wireOp",EDGE,"E276.trimOffspring");var subQ2=makeQuery(id+"F25.imprint","INTERSECT",VERTEX,{"derivedFrom":[subQ1,subQ0]});Q80=makeQuery(id+"F25.imprint","IMPRINT",FACE,{"disambiguationData":[TD([[makeQuery(id+"F25.imprint","IMPRINT",EDGE,{"disambiguationData":[TD([[subQ2,-1.0]])],"derivedFrom":subQ1}),-1.0]])]});}
            var Q81;
            {var subQ0=sQuery(id+"F25.wireOp",EDGE,"E518.trimOffspring");var subQ1=sQuery(id+"F25.wireOp",EDGE,"E276.trimOffspring");var subQ2=makeQuery(id+"F25.imprint","INTERSECT",VERTEX,{"derivedFrom":[subQ1,subQ0]});Q81=makeQuery(id+"F25.imprint","IMPRINT",FACE,{"disambiguationData":[TD([[makeQuery(id+"F25.imprint","IMPRINT",EDGE,{"disambiguationData":[TD([[subQ2,-1.0]])],"derivedFrom":subQ1}),-1.0]])]});}
            var Q82;
            {var subQ0=sQuery(id+"F25.wireOp",EDGE,"E518.trimOffspring");var subQ1=sQuery(id+"F25.wireOp",EDGE,"E277.trimOffspring");var subQ2=makeQuery(id+"F25.imprint","INTERSECT",VERTEX,{"derivedFrom":[subQ1,subQ0]});Q82=makeQuery(id+"F25.imprint","IMPRINT",FACE,{"disambiguationData":[TD([[makeQuery(id+"F25.imprint","IMPRINT",EDGE,{"disambiguationData":[TD([[subQ2,-1.0]])],"derivedFrom":subQ1}),-1.0]])]});}
            var Q83;
            {var subQ0=sQuery(id+"F25.wireOp",EDGE,"E507.trimOffspring");var subQ1=sQuery(id+"F25.wireOp",EDGE,"E276.trimOffspring");var subQ2=makeQuery(id+"F25.imprint","INTERSECT",VERTEX,{"derivedFrom":[subQ1,subQ0]});Q83=makeQuery(id+"F25.imprint","IMPRINT",FACE,{"disambiguationData":[TD([[makeQuery(id+"F25.imprint","IMPRINT",EDGE,{"disambiguationData":[TD([[subQ2,-1.0]])],"derivedFrom":subQ1}),-1.0]])]});}
            var Q84;
            {var subQ0=sQuery(id+"F25.wireOp",EDGE,"E507.trimOffspring");var subQ1=sQuery(id+"F25.wireOp",EDGE,"E277.trimOffspring");var subQ2=makeQuery(id+"F25.imprint","INTERSECT",VERTEX,{"derivedFrom":[subQ1,subQ0]});Q84=makeQuery(id+"F25.imprint","IMPRINT",FACE,{"disambiguationData":[TD([[makeQuery(id+"F25.imprint","IMPRINT",EDGE,{"disambiguationData":[TD([[subQ2,-1.0]])],"derivedFrom":subQ1}),-1.0]])]});}
            var Q85;
            {var subQ0=sQuery(id+"F25.wireOp",EDGE,"E512.trimOffspring");var subQ1=sQuery(id+"F25.wireOp",EDGE,"E276.trimOffspring");var subQ2=makeQuery(id+"F25.imprint","INTERSECT",VERTEX,{"derivedFrom":[subQ1,subQ0]});Q85=makeQuery(id+"F25.imprint","IMPRINT",FACE,{"disambiguationData":[TD([[makeQuery(id+"F25.imprint","IMPRINT",EDGE,{"disambiguationData":[TD([[subQ2,-1.0]])],"derivedFrom":subQ1}),-1.0]])]});}
            var Q86;
            {var subQ0=sQuery(id+"F25.wireOp",EDGE,"E512.trimOffspring");var subQ1=sQuery(id+"F25.wireOp",EDGE,"E277.trimOffspring");var subQ2=makeQuery(id+"F25.imprint","INTERSECT",VERTEX,{"derivedFrom":[subQ1,subQ0]});Q86=makeQuery(id+"F25.imprint","IMPRINT",FACE,{"disambiguationData":[TD([[makeQuery(id+"F25.imprint","IMPRINT",EDGE,{"disambiguationData":[TD([[subQ2,-1.0]])],"derivedFrom":subQ1}),-1.0]])]});}
            var Q87;
            {var subQ0=sQuery(id+"F25.wireOp",EDGE,"E510.trimOffspring");var subQ1=sQuery(id+"F25.wireOp",EDGE,"E277.trimOffspring");var subQ2=makeQuery(id+"F25.imprint","INTERSECT",VERTEX,{"derivedFrom":[subQ1,subQ0]});Q87=makeQuery(id+"F25.imprint","IMPRINT",FACE,{"disambiguationData":[TD([[makeQuery(id+"F25.imprint","IMPRINT",EDGE,{"disambiguationData":[TD([[subQ2,-1.0]])],"derivedFrom":subQ1}),-1.0]])]});}
            var Q88;
            {var subQ0=sQuery(id+"F25.wireOp",EDGE,"E510.trimOffspring");var subQ1=sQuery(id+"F25.wireOp",EDGE,"E276.trimOffspring");var subQ2=makeQuery(id+"F25.imprint","INTERSECT",VERTEX,{"derivedFrom":[subQ1,subQ0]});Q88=makeQuery(id+"F25.imprint","IMPRINT",FACE,{"disambiguationData":[TD([[makeQuery(id+"F25.imprint","IMPRINT",EDGE,{"disambiguationData":[TD([[subQ2,-1.0]])],"derivedFrom":subQ1}),-1.0]])]});}
            var Q89;
            {var subQ0=sQuery(id+"F25.wireOp",EDGE,"E522.trimOffspring");var subQ1=sQuery(id+"F25.wireOp",EDGE,"E276.trimOffspring");var subQ2=makeQuery(id+"F25.imprint","INTERSECT",VERTEX,{"derivedFrom":[subQ1,subQ0]});Q89=makeQuery(id+"F25.imprint","IMPRINT",FACE,{"disambiguationData":[TD([[makeQuery(id+"F25.imprint","IMPRINT",EDGE,{"disambiguationData":[TD([[subQ2,-1.0]])],"derivedFrom":subQ1}),-1.0]])]});}
            var Q90;
            {var subQ0=sQuery(id+"F25.wireOp",EDGE,"E522.trimOffspring");var subQ1=sQuery(id+"F25.wireOp",EDGE,"E277.trimOffspring");var subQ2=makeQuery(id+"F25.imprint","INTERSECT",VERTEX,{"derivedFrom":[subQ1,subQ0]});Q90=makeQuery(id+"F25.imprint","IMPRINT",FACE,{"disambiguationData":[TD([[makeQuery(id+"F25.imprint","IMPRINT",EDGE,{"disambiguationData":[TD([[subQ2,-1.0]])],"derivedFrom":subQ1}),-1.0]])]});}
            var Q91;
            {var subQ0=sQuery(id+"F25.wireOp",EDGE,"E525.trimOffspring");var subQ1=sQuery(id+"F25.wireOp",EDGE,"E277.trimOffspring");var subQ2=makeQuery(id+"F25.imprint","INTERSECT",VERTEX,{"derivedFrom":[subQ1,subQ0]});Q91=makeQuery(id+"F25.imprint","IMPRINT",FACE,{"disambiguationData":[TD([[makeQuery(id+"F25.imprint","IMPRINT",EDGE,{"disambiguationData":[TD([[subQ2,1.0]])],"derivedFrom":subQ1}),-1.0]])]});}
            var Q92;
            {var subQ0=sQuery(id+"F25.wireOp",EDGE,"E525.trimOffspring");var subQ1=sQuery(id+"F25.wireOp",EDGE,"E276.trimOffspring");var subQ2=makeQuery(id+"F25.imprint","INTERSECT",VERTEX,{"derivedFrom":[subQ1,subQ0]});Q92=makeQuery(id+"F25.imprint","IMPRINT",FACE,{"disambiguationData":[TD([[makeQuery(id+"F25.imprint","IMPRINT",EDGE,{"disambiguationData":[TD([[subQ2,1.0]])],"derivedFrom":subQ1}),-1.0]])]});}
            var Q93;
            {var subQ0=sQuery(id+"F25.wireOp",EDGE,"E522.trimOffspring");var subQ1=sQuery(id+"F25.wireOp",EDGE,"E280.trimOffspring");var subQ2=makeQuery(id+"F25.imprint","INTERSECT",VERTEX,{"derivedFrom":[subQ1,subQ0]});Q93=makeQuery(id+"F25.imprint","IMPRINT",FACE,{"disambiguationData":[TD([[makeQuery(id+"F25.imprint","IMPRINT",EDGE,{"disambiguationData":[TD([[subQ2,-1.0]])],"derivedFrom":subQ1}),1.0]])]});}
            var Q94;
            {var subQ0=sQuery(id+"F25.wireOp",EDGE,"E525.trimOffspring");var subQ1=sQuery(id+"F25.wireOp",EDGE,"E280.trimOffspring");var subQ2=makeQuery(id+"F25.imprint","INTERSECT",VERTEX,{"derivedFrom":[subQ1,subQ0]});Q94=makeQuery(id+"F25.imprint","IMPRINT",FACE,{"disambiguationData":[TD([[makeQuery(id+"F25.imprint","IMPRINT",EDGE,{"disambiguationData":[TD([[subQ2,1.0]])],"derivedFrom":subQ1}),1.0]])]});}
            var Q95;
            {var subQ0=sQuery(id+"F25.wireOp",EDGE,"E525.trimOffspring");var subQ1=sQuery(id+"F25.wireOp",EDGE,"E280.trimOffspring");var subQ2=makeQuery(id+"F25.imprint","INTERSECT",VERTEX,{"derivedFrom":[subQ1,subQ0]});Q95=makeQuery(id+"F25.imprint","IMPRINT",FACE,{"disambiguationData":[TD([[makeQuery(id+"F25.imprint","IMPRINT",EDGE,{"disambiguationData":[TD([[subQ2,1.0]])],"derivedFrom":subQ1}),-1.0]])]});}
            var Q96;
            {var subQ0=sQuery(id+"F25.wireOp",EDGE,"E525.trimOffspring");var subQ1=sQuery(id+"F25.wireOp",EDGE,"E279.trimOffspring");var subQ2=makeQuery(id+"F25.imprint","INTERSECT",VERTEX,{"derivedFrom":[subQ1,subQ0]});Q96=makeQuery(id+"F25.imprint","IMPRINT",FACE,{"disambiguationData":[TD([[makeQuery(id+"F25.imprint","IMPRINT",EDGE,{"disambiguationData":[TD([[subQ2,1.0]])],"derivedFrom":subQ1}),1.0]])]});}
            var Q97;
            {var subQ0=sQuery(id+"F25.wireOp",EDGE,"E522.trimOffspring");var subQ1=sQuery(id+"F25.wireOp",EDGE,"E280.trimOffspring");var subQ2=makeQuery(id+"F25.imprint","INTERSECT",VERTEX,{"derivedFrom":[subQ1,subQ0]});Q97=makeQuery(id+"F25.imprint","IMPRINT",FACE,{"disambiguationData":[TD([[makeQuery(id+"F25.imprint","IMPRINT",EDGE,{"disambiguationData":[TD([[subQ2,-1.0]])],"derivedFrom":subQ1}),-1.0]])]});}
            var Q98;
            {var subQ0=sQuery(id+"F25.wireOp",EDGE,"E510.trimOffspring");var subQ1=sQuery(id+"F25.wireOp",EDGE,"E280.trimOffspring");var subQ2=makeQuery(id+"F25.imprint","INTERSECT",VERTEX,{"derivedFrom":[subQ1,subQ0]});Q98=makeQuery(id+"F25.imprint","IMPRINT",FACE,{"disambiguationData":[TD([[makeQuery(id+"F25.imprint","IMPRINT",EDGE,{"disambiguationData":[TD([[subQ2,-1.0]])],"derivedFrom":subQ1}),-1.0]])]});}
            var Q99;
            {var subQ0=sQuery(id+"F25.wireOp",EDGE,"E510.trimOffspring");var subQ1=sQuery(id+"F25.wireOp",EDGE,"E279.trimOffspring");var subQ2=makeQuery(id+"F25.imprint","INTERSECT",VERTEX,{"derivedFrom":[subQ1,subQ0]});Q99=makeQuery(id+"F25.imprint","IMPRINT",FACE,{"disambiguationData":[TD([[makeQuery(id+"F25.imprint","IMPRINT",EDGE,{"disambiguationData":[TD([[subQ2,-1.0]])],"derivedFrom":subQ1}),1.0]])]});}
            var Q100;
            {var subQ0=sQuery(id+"F25.wireOp",EDGE,"E517.trimOffspring");var subQ1=sQuery(id+"F25.wireOp",EDGE,"E280.trimOffspring");var subQ2=makeQuery(id+"F25.imprint","INTERSECT",VERTEX,{"derivedFrom":[subQ1,subQ0]});Q100=makeQuery(id+"F25.imprint","IMPRINT",FACE,{"disambiguationData":[TD([[makeQuery(id+"F25.imprint","IMPRINT",EDGE,{"disambiguationData":[TD([[subQ2,-1.0]])],"derivedFrom":subQ1}),-1.0]])]});}
            var Q101;
            {var subQ0=sQuery(id+"F25.wireOp",EDGE,"E517.trimOffspring");var subQ1=sQuery(id+"F25.wireOp",EDGE,"E279.trimOffspring");var subQ2=makeQuery(id+"F25.imprint","INTERSECT",VERTEX,{"derivedFrom":[subQ1,subQ0]});Q101=makeQuery(id+"F25.imprint","IMPRINT",FACE,{"disambiguationData":[TD([[makeQuery(id+"F25.imprint","IMPRINT",EDGE,{"disambiguationData":[TD([[subQ2,-1.0]])],"derivedFrom":subQ1}),1.0]])]});}
            var Q102;
            {var subQ0=sQuery(id+"F25.wireOp",EDGE,"E519.trimOffspring");var subQ1=sQuery(id+"F25.wireOp",EDGE,"E279.trimOffspring");var subQ2=makeQuery(id+"F25.imprint","INTERSECT",VERTEX,{"derivedFrom":[subQ1,subQ0]});Q102=makeQuery(id+"F25.imprint","IMPRINT",FACE,{"disambiguationData":[TD([[makeQuery(id+"F25.imprint","IMPRINT",EDGE,{"disambiguationData":[TD([[subQ2,-1.0]])],"derivedFrom":subQ1}),1.0]])]});}
            var Q103;
            {var subQ0=sQuery(id+"F25.wireOp",EDGE,"E519.trimOffspring");var subQ1=sQuery(id+"F25.wireOp",EDGE,"E280.trimOffspring");var subQ2=makeQuery(id+"F25.imprint","INTERSECT",VERTEX,{"derivedFrom":[subQ1,subQ0]});Q103=makeQuery(id+"F25.imprint","IMPRINT",FACE,{"disambiguationData":[TD([[makeQuery(id+"F25.imprint","IMPRINT",EDGE,{"disambiguationData":[TD([[subQ2,-1.0]])],"derivedFrom":subQ1}),-1.0]])]});}
            var Q104;
            {var subQ0=sQuery(id+"F25.wireOp",EDGE,"E518.trimOffspring");var subQ1=sQuery(id+"F25.wireOp",EDGE,"E280.trimOffspring");var subQ2=makeQuery(id+"F25.imprint","INTERSECT",VERTEX,{"derivedFrom":[subQ1,subQ0]});Q104=makeQuery(id+"F25.imprint","IMPRINT",FACE,{"disambiguationData":[TD([[makeQuery(id+"F25.imprint","IMPRINT",EDGE,{"disambiguationData":[TD([[subQ2,-1.0]])],"derivedFrom":subQ1}),-1.0]])]});}
            var Q105;
            {var subQ0=sQuery(id+"F25.wireOp",EDGE,"E518.trimOffspring");var subQ1=sQuery(id+"F25.wireOp",EDGE,"E279.trimOffspring");var subQ2=makeQuery(id+"F25.imprint","INTERSECT",VERTEX,{"derivedFrom":[subQ1,subQ0]});Q105=makeQuery(id+"F25.imprint","IMPRINT",FACE,{"disambiguationData":[TD([[makeQuery(id+"F25.imprint","IMPRINT",EDGE,{"disambiguationData":[TD([[subQ2,-1.0]])],"derivedFrom":subQ1}),1.0]])]});}
            var Q106;
            {var subQ0=sQuery(id+"F25.wireOp",EDGE,"E507.trimOffspring");var subQ1=sQuery(id+"F25.wireOp",EDGE,"E280.trimOffspring");var subQ2=makeQuery(id+"F25.imprint","INTERSECT",VERTEX,{"derivedFrom":[subQ1,subQ0]});Q106=makeQuery(id+"F25.imprint","IMPRINT",FACE,{"disambiguationData":[TD([[makeQuery(id+"F25.imprint","IMPRINT",EDGE,{"disambiguationData":[TD([[subQ2,-1.0]])],"derivedFrom":subQ1}),-1.0]])]});}
            var Q107;
            {var subQ0=sQuery(id+"F25.wireOp",EDGE,"E507.trimOffspring");var subQ1=sQuery(id+"F25.wireOp",EDGE,"E279.trimOffspring");var subQ2=makeQuery(id+"F25.imprint","INTERSECT",VERTEX,{"derivedFrom":[subQ1,subQ0]});Q107=makeQuery(id+"F25.imprint","IMPRINT",FACE,{"disambiguationData":[TD([[makeQuery(id+"F25.imprint","IMPRINT",EDGE,{"disambiguationData":[TD([[subQ2,-1.0]])],"derivedFrom":subQ1}),1.0]])]});}
            var Q108;
            {var subQ0=sQuery(id+"F25.wireOp",EDGE,"E512.trimOffspring");var subQ1=sQuery(id+"F25.wireOp",EDGE,"E280.trimOffspring");var subQ2=makeQuery(id+"F25.imprint","INTERSECT",VERTEX,{"derivedFrom":[subQ1,subQ0]});Q108=makeQuery(id+"F25.imprint","IMPRINT",FACE,{"disambiguationData":[TD([[makeQuery(id+"F25.imprint","IMPRINT",EDGE,{"disambiguationData":[TD([[subQ2,-1.0]])],"derivedFrom":subQ1}),-1.0]])]});}
            var Q109;
            {var subQ0=sQuery(id+"F25.wireOp",EDGE,"E512.trimOffspring");var subQ1=sQuery(id+"F25.wireOp",EDGE,"E279.trimOffspring");var subQ2=makeQuery(id+"F25.imprint","INTERSECT",VERTEX,{"derivedFrom":[subQ1,subQ0]});Q109=makeQuery(id+"F25.imprint","IMPRINT",FACE,{"disambiguationData":[TD([[makeQuery(id+"F25.imprint","IMPRINT",EDGE,{"disambiguationData":[TD([[subQ2,-1.0]])],"derivedFrom":subQ1}),1.0]])]});}
            var Q110;
            {var subQ0=sQuery(id+"F25.wireOp",EDGE,"E522.trimOffspring");var subQ1=sQuery(id+"F25.wireOp",EDGE,"E279.trimOffspring");var subQ2=makeQuery(id+"F25.imprint","INTERSECT",VERTEX,{"derivedFrom":[subQ1,subQ0]});Q110=makeQuery(id+"F25.imprint","IMPRINT",FACE,{"disambiguationData":[TD([[makeQuery(id+"F25.imprint","IMPRINT",EDGE,{"disambiguationData":[TD([[subQ2,-1.0]])],"derivedFrom":subQ1}),1.0]])]});}
            var Q111;
            {var subQ0=sQuery(id+"F25.wireOp",EDGE,"E522.trimOffspring");var subQ1=sQuery(id+"F25.wireOp",EDGE,"E279.trimOffspring");var subQ2=makeQuery(id+"F25.imprint","INTERSECT",VERTEX,{"derivedFrom":[subQ1,subQ0]});Q111=makeQuery(id+"F25.imprint","IMPRINT",FACE,{"disambiguationData":[TD([[makeQuery(id+"F25.imprint","IMPRINT",EDGE,{"disambiguationData":[TD([[subQ2,-1.0]])],"derivedFrom":subQ1}),-1.0]])]});}
            var Q112;
            {var subQ0=sQuery(id+"F25.wireOp",EDGE,"E525.trimOffspring");var subQ1=sQuery(id+"F25.wireOp",EDGE,"E279.trimOffspring");var subQ2=makeQuery(id+"F25.imprint","INTERSECT",VERTEX,{"derivedFrom":[subQ1,subQ0]});Q112=makeQuery(id+"F25.imprint","IMPRINT",FACE,{"disambiguationData":[TD([[makeQuery(id+"F25.imprint","IMPRINT",EDGE,{"disambiguationData":[TD([[subQ2,1.0]])],"derivedFrom":subQ1}),-1.0]])]});}
            var Q113;
            {var subQ0=sQuery(id+"F25.wireOp",EDGE,"E525.trimOffspring");var subQ1=sQuery(id+"F25.wireOp",EDGE,"E287.trimOffspring");var subQ2=makeQuery(id+"F25.imprint","INTERSECT",VERTEX,{"derivedFrom":[subQ1,subQ0]});Q113=makeQuery(id+"F25.imprint","IMPRINT",FACE,{"disambiguationData":[TD([[makeQuery(id+"F25.imprint","IMPRINT",EDGE,{"disambiguationData":[TD([[subQ2,1.0]])],"derivedFrom":subQ1}),-1.0]])]});}
            var Q114;
            {var subQ0=sQuery(id+"F25.wireOp",EDGE,"E525.trimOffspring");var subQ1=sQuery(id+"F25.wireOp",EDGE,"E291.trimOffspring");var subQ2=makeQuery(id+"F25.imprint","INTERSECT",VERTEX,{"derivedFrom":[subQ1,subQ0]});Q114=makeQuery(id+"F25.imprint","IMPRINT",FACE,{"disambiguationData":[TD([[makeQuery(id+"F25.imprint","IMPRINT",EDGE,{"disambiguationData":[TD([[subQ2,1.0]])],"derivedFrom":subQ1}),1.0]])]});}
            var Q115;
            {var subQ0=sQuery(id+"F25.wireOp",EDGE,"E522.trimOffspring");var subQ1=sQuery(id+"F25.wireOp",EDGE,"E287.trimOffspring");var subQ2=makeQuery(id+"F25.imprint","INTERSECT",VERTEX,{"derivedFrom":[subQ1,subQ0]});Q115=makeQuery(id+"F25.imprint","IMPRINT",FACE,{"disambiguationData":[TD([[makeQuery(id+"F25.imprint","IMPRINT",EDGE,{"disambiguationData":[TD([[subQ2,-1.0]])],"derivedFrom":subQ1}),-1.0]])]});}
            var Q116;
            {var subQ0=sQuery(id+"F25.wireOp",EDGE,"E522.trimOffspring");var subQ1=sQuery(id+"F25.wireOp",EDGE,"E291.trimOffspring");var subQ2=makeQuery(id+"F25.imprint","INTERSECT",VERTEX,{"derivedFrom":[subQ1,subQ0]});Q116=makeQuery(id+"F25.imprint","IMPRINT",FACE,{"disambiguationData":[TD([[makeQuery(id+"F25.imprint","IMPRINT",EDGE,{"disambiguationData":[TD([[subQ2,-1.0]])],"derivedFrom":subQ1}),1.0]])]});}
            var Q117;
            {var subQ0=sQuery(id+"F25.wireOp",EDGE,"E510.trimOffspring");var subQ1=sQuery(id+"F25.wireOp",EDGE,"E287.trimOffspring");var subQ2=makeQuery(id+"F25.imprint","INTERSECT",VERTEX,{"derivedFrom":[subQ1,subQ0]});Q117=makeQuery(id+"F25.imprint","IMPRINT",FACE,{"disambiguationData":[TD([[makeQuery(id+"F25.imprint","IMPRINT",EDGE,{"disambiguationData":[TD([[subQ2,-1.0]])],"derivedFrom":subQ1}),-1.0]])]});}
            var Q118;
            {var subQ0=sQuery(id+"F25.wireOp",EDGE,"E510.trimOffspring");var subQ1=sQuery(id+"F25.wireOp",EDGE,"E291.trimOffspring");var subQ2=makeQuery(id+"F25.imprint","INTERSECT",VERTEX,{"derivedFrom":[subQ1,subQ0]});Q118=makeQuery(id+"F25.imprint","IMPRINT",FACE,{"disambiguationData":[TD([[makeQuery(id+"F25.imprint","IMPRINT",EDGE,{"disambiguationData":[TD([[subQ2,-1.0]])],"derivedFrom":subQ1}),1.0]])]});}
            var Q119;
            {var subQ0=sQuery(id+"F25.wireOp",EDGE,"E512.trimOffspring");var subQ1=sQuery(id+"F25.wireOp",EDGE,"E287.trimOffspring");var subQ2=makeQuery(id+"F25.imprint","INTERSECT",VERTEX,{"derivedFrom":[subQ1,subQ0]});Q119=makeQuery(id+"F25.imprint","IMPRINT",FACE,{"disambiguationData":[TD([[makeQuery(id+"F25.imprint","IMPRINT",EDGE,{"disambiguationData":[TD([[subQ2,-1.0]])],"derivedFrom":subQ1}),-1.0]])]});}
            var Q120;
            {var subQ0=sQuery(id+"F25.wireOp",EDGE,"E512.trimOffspring");var subQ1=sQuery(id+"F25.wireOp",EDGE,"E291.trimOffspring");var subQ2=makeQuery(id+"F25.imprint","INTERSECT",VERTEX,{"derivedFrom":[subQ1,subQ0]});Q120=makeQuery(id+"F25.imprint","IMPRINT",FACE,{"disambiguationData":[TD([[makeQuery(id+"F25.imprint","IMPRINT",EDGE,{"disambiguationData":[TD([[subQ2,-1.0]])],"derivedFrom":subQ1}),1.0]])]});}
            var Q121;
            {var subQ0=sQuery(id+"F25.wireOp",EDGE,"E507.trimOffspring");var subQ1=sQuery(id+"F25.wireOp",EDGE,"E291.trimOffspring");var subQ2=makeQuery(id+"F25.imprint","INTERSECT",VERTEX,{"derivedFrom":[subQ1,subQ0]});Q121=makeQuery(id+"F25.imprint","IMPRINT",FACE,{"disambiguationData":[TD([[makeQuery(id+"F25.imprint","IMPRINT",EDGE,{"disambiguationData":[TD([[subQ2,-1.0]])],"derivedFrom":subQ1}),1.0]])]});}
            var Q122;
            {var subQ0=sQuery(id+"F25.wireOp",EDGE,"E507.trimOffspring");var subQ1=sQuery(id+"F25.wireOp",EDGE,"E287.trimOffspring");var subQ2=makeQuery(id+"F25.imprint","INTERSECT",VERTEX,{"derivedFrom":[subQ1,subQ0]});Q122=makeQuery(id+"F25.imprint","IMPRINT",FACE,{"disambiguationData":[TD([[makeQuery(id+"F25.imprint","IMPRINT",EDGE,{"disambiguationData":[TD([[subQ2,-1.0]])],"derivedFrom":subQ1}),-1.0]])]});}
            var Q123;
            {var subQ0=sQuery(id+"F25.wireOp",EDGE,"E518.trimOffspring");var subQ1=sQuery(id+"F25.wireOp",EDGE,"E287.trimOffspring");var subQ2=makeQuery(id+"F25.imprint","INTERSECT",VERTEX,{"derivedFrom":[subQ1,subQ0]});Q123=makeQuery(id+"F25.imprint","IMPRINT",FACE,{"disambiguationData":[TD([[makeQuery(id+"F25.imprint","IMPRINT",EDGE,{"disambiguationData":[TD([[subQ2,-1.0]])],"derivedFrom":subQ1}),-1.0]])]});}
            var Q124;
            {var subQ0=sQuery(id+"F25.wireOp",EDGE,"E518.trimOffspring");var subQ1=sQuery(id+"F25.wireOp",EDGE,"E291.trimOffspring");var subQ2=makeQuery(id+"F25.imprint","INTERSECT",VERTEX,{"derivedFrom":[subQ1,subQ0]});Q124=makeQuery(id+"F25.imprint","IMPRINT",FACE,{"disambiguationData":[TD([[makeQuery(id+"F25.imprint","IMPRINT",EDGE,{"disambiguationData":[TD([[subQ2,-1.0]])],"derivedFrom":subQ1}),1.0]])]});}
            var Q125;
            {var subQ0=sQuery(id+"F25.wireOp",EDGE,"E519.trimOffspring");var subQ1=sQuery(id+"F25.wireOp",EDGE,"E287.trimOffspring");var subQ2=makeQuery(id+"F25.imprint","INTERSECT",VERTEX,{"derivedFrom":[subQ1,subQ0]});Q125=makeQuery(id+"F25.imprint","IMPRINT",FACE,{"disambiguationData":[TD([[makeQuery(id+"F25.imprint","IMPRINT",EDGE,{"disambiguationData":[TD([[subQ2,-1.0]])],"derivedFrom":subQ1}),-1.0]])]});}
            var Q126;
            {var subQ0=sQuery(id+"F25.wireOp",EDGE,"E517.trimOffspring");var subQ1=sQuery(id+"F25.wireOp",EDGE,"E287.trimOffspring");var subQ2=makeQuery(id+"F25.imprint","INTERSECT",VERTEX,{"derivedFrom":[subQ1,subQ0]});Q126=makeQuery(id+"F25.imprint","IMPRINT",FACE,{"disambiguationData":[TD([[makeQuery(id+"F25.imprint","IMPRINT",EDGE,{"disambiguationData":[TD([[subQ2,-1.0]])],"derivedFrom":subQ1}),-1.0]])]});}
            var Q127;
            {var subQ0=sQuery(id+"F25.wireOp",EDGE,"E517.trimOffspring");var subQ1=sQuery(id+"F25.wireOp",EDGE,"E291.trimOffspring");var subQ2=makeQuery(id+"F25.imprint","INTERSECT",VERTEX,{"derivedFrom":[subQ1,subQ0]});Q127=makeQuery(id+"F25.imprint","IMPRINT",FACE,{"disambiguationData":[TD([[makeQuery(id+"F25.imprint","IMPRINT",EDGE,{"disambiguationData":[TD([[subQ2,-1.0]])],"derivedFrom":subQ1}),1.0]])]});}
            var Q128;
            {var subQ0=sQuery(id+"F25.wireOp",EDGE,"E519.trimOffspring");var subQ1=sQuery(id+"F25.wireOp",EDGE,"E291.trimOffspring");var subQ2=makeQuery(id+"F25.imprint","INTERSECT",VERTEX,{"derivedFrom":[subQ1,subQ0]});Q128=makeQuery(id+"F25.imprint","IMPRINT",FACE,{"disambiguationData":[TD([[makeQuery(id+"F25.imprint","IMPRINT",EDGE,{"disambiguationData":[TD([[subQ2,-1.0]])],"derivedFrom":subQ1}),1.0]])]});}
            var Q129;
            {var subQ0=sQuery(id+"F25.wireOp",EDGE,"E517.trimOffspring");var subQ1=sQuery(id+"F25.wireOp",EDGE,"E251.right");var subQ2=makeQuery(id+"F25.imprint","INTERSECT",VERTEX,{"derivedFrom":[subQ1,subQ0]});Q129=makeQuery(id+"F25.imprint","IMPRINT",FACE,{"disambiguationData":[TD([[makeQuery(id+"F25.imprint","IMPRINT",EDGE,{"disambiguationData":[TD([[subQ2,-1.0]])],"derivedFrom":subQ1}),1.0]])]});}
            var Q130;
            {var subQ0=sQuery(id+"F25.wireOp",EDGE,"E519.trimOffspring");var subQ1=sQuery(id+"F25.wireOp",EDGE,"E251.right");var subQ2=makeQuery(id+"F25.imprint","INTERSECT",VERTEX,{"derivedFrom":[subQ1,subQ0]});Q130=makeQuery(id+"F25.imprint","IMPRINT",FACE,{"disambiguationData":[TD([[makeQuery(id+"F25.imprint","IMPRINT",EDGE,{"disambiguationData":[TD([[subQ2,-1.0]])],"derivedFrom":subQ1}),1.0]])]});}
            var Q131;
            {var subQ0=sQuery(id+"F25.wireOp",EDGE,"E519.trimOffspring");var subQ1=sQuery(id+"F25.wireOp",EDGE,"E250.left");var subQ2=makeQuery(id+"F25.imprint","INTERSECT",VERTEX,{"derivedFrom":[subQ1,subQ0]});Q131=makeQuery(id+"F25.imprint","IMPRINT",FACE,{"disambiguationData":[TD([[makeQuery(id+"F25.imprint","IMPRINT",EDGE,{"disambiguationData":[TD([[subQ2,-1.0]])],"derivedFrom":subQ1}),1.0]])]});}
            var Q132;
            {var subQ0=sQuery(id+"F25.wireOp",EDGE,"E517.trimOffspring");var subQ1=sQuery(id+"F25.wireOp",EDGE,"E250.left");var subQ2=makeQuery(id+"F25.imprint","INTERSECT",VERTEX,{"derivedFrom":[subQ1,subQ0]});Q132=makeQuery(id+"F25.imprint","IMPRINT",FACE,{"disambiguationData":[TD([[makeQuery(id+"F25.imprint","IMPRINT",EDGE,{"disambiguationData":[TD([[subQ2,-1.0]])],"derivedFrom":subQ1}),1.0]])]});}
            var Q133;
            {var subQ0=sQuery(id+"F25.wireOp",EDGE,"E517.trimOffspring");var subQ1=sQuery(id+"F25.wireOp",EDGE,"E250.right");var subQ2=makeQuery(id+"F25.imprint","INTERSECT",VERTEX,{"derivedFrom":[subQ1,subQ0]});Q133=makeQuery(id+"F25.imprint","IMPRINT",FACE,{"disambiguationData":[TD([[makeQuery(id+"F25.imprint","IMPRINT",EDGE,{"disambiguationData":[TD([[subQ2,-1.0]])],"derivedFrom":subQ1}),1.0]])]});}
            var Q134;
            {var subQ0=sQuery(id+"F25.wireOp",EDGE,"E519.trimOffspring");var subQ1=sQuery(id+"F25.wireOp",EDGE,"E250.right");var subQ2=makeQuery(id+"F25.imprint","INTERSECT",VERTEX,{"derivedFrom":[subQ1,subQ0]});Q134=makeQuery(id+"F25.imprint","IMPRINT",FACE,{"disambiguationData":[TD([[makeQuery(id+"F25.imprint","IMPRINT",EDGE,{"disambiguationData":[TD([[subQ2,-1.0]])],"derivedFrom":subQ1}),1.0]])]});}
            var Q135;
            {var subQ0=sQuery(id+"F25.wireOp",EDGE,"E518.trimOffspring");var subQ1=sQuery(id+"F25.wireOp",EDGE,"E250.right");var subQ2=makeQuery(id+"F25.imprint","INTERSECT",VERTEX,{"derivedFrom":[subQ1,subQ0]});Q135=makeQuery(id+"F25.imprint","IMPRINT",FACE,{"disambiguationData":[TD([[makeQuery(id+"F25.imprint","IMPRINT",EDGE,{"disambiguationData":[TD([[subQ2,-1.0]])],"derivedFrom":subQ1}),1.0]])]});}
            var Q136;
            {var subQ0=sQuery(id+"F25.wireOp",EDGE,"E518.trimOffspring");var subQ1=sQuery(id+"F25.wireOp",EDGE,"E250.left");var subQ2=makeQuery(id+"F25.imprint","INTERSECT",VERTEX,{"derivedFrom":[subQ1,subQ0]});Q136=makeQuery(id+"F25.imprint","IMPRINT",FACE,{"disambiguationData":[TD([[makeQuery(id+"F25.imprint","IMPRINT",EDGE,{"disambiguationData":[TD([[subQ2,-1.0]])],"derivedFrom":subQ1}),1.0]])]});}
            var Q137;
            {var subQ0=sQuery(id+"F25.wireOp",EDGE,"E507.trimOffspring");var subQ1=sQuery(id+"F25.wireOp",EDGE,"E250.left");var subQ2=makeQuery(id+"F25.imprint","INTERSECT",VERTEX,{"derivedFrom":[subQ1,subQ0]});Q137=makeQuery(id+"F25.imprint","IMPRINT",FACE,{"disambiguationData":[TD([[makeQuery(id+"F25.imprint","IMPRINT",EDGE,{"disambiguationData":[TD([[subQ2,-1.0]])],"derivedFrom":subQ1}),1.0]])]});}
            var Q138;
            {var subQ0=sQuery(id+"F25.wireOp",EDGE,"E507.trimOffspring");var subQ1=sQuery(id+"F25.wireOp",EDGE,"E250.right");var subQ2=makeQuery(id+"F25.imprint","INTERSECT",VERTEX,{"derivedFrom":[subQ1,subQ0]});Q138=makeQuery(id+"F25.imprint","IMPRINT",FACE,{"disambiguationData":[TD([[makeQuery(id+"F25.imprint","IMPRINT",EDGE,{"disambiguationData":[TD([[subQ2,-1.0]])],"derivedFrom":subQ1}),1.0]])]});}
            var Q139;
            {var subQ0=sQuery(id+"F25.wireOp",EDGE,"E512.trimOffspring");var subQ1=sQuery(id+"F25.wireOp",EDGE,"E250.left");var subQ2=makeQuery(id+"F25.imprint","INTERSECT",VERTEX,{"derivedFrom":[subQ1,subQ0]});Q139=makeQuery(id+"F25.imprint","IMPRINT",FACE,{"disambiguationData":[TD([[makeQuery(id+"F25.imprint","IMPRINT",EDGE,{"disambiguationData":[TD([[subQ2,-1.0]])],"derivedFrom":subQ1}),1.0]])]});}
            var Q140;
            {var subQ0=sQuery(id+"F25.wireOp",EDGE,"E512.trimOffspring");var subQ1=sQuery(id+"F25.wireOp",EDGE,"E250.right");var subQ2=makeQuery(id+"F25.imprint","INTERSECT",VERTEX,{"derivedFrom":[subQ1,subQ0]});Q140=makeQuery(id+"F25.imprint","IMPRINT",FACE,{"disambiguationData":[TD([[makeQuery(id+"F25.imprint","IMPRINT",EDGE,{"disambiguationData":[TD([[subQ2,-1.0]])],"derivedFrom":subQ1}),1.0]])]});}
            var Q141;
            {var subQ0=sQuery(id+"F25.wireOp",EDGE,"E512.trimOffspring");var subQ1=sQuery(id+"F25.wireOp",EDGE,"E249.right");var subQ2=makeQuery(id+"F25.imprint","INTERSECT",VERTEX,{"derivedFrom":[subQ1,subQ0]});Q141=makeQuery(id+"F25.imprint","IMPRINT",FACE,{"disambiguationData":[TD([[makeQuery(id+"F25.imprint","IMPRINT",EDGE,{"disambiguationData":[TD([[subQ2,-1.0]])],"derivedFrom":subQ1}),1.0]])]});}
            var Q142;
            {var subQ0=sQuery(id+"F25.wireOp",EDGE,"E507.trimOffspring");var subQ1=sQuery(id+"F25.wireOp",EDGE,"E249.right");var subQ2=makeQuery(id+"F25.imprint","INTERSECT",VERTEX,{"derivedFrom":[subQ1,subQ0]});Q142=makeQuery(id+"F25.imprint","IMPRINT",FACE,{"disambiguationData":[TD([[makeQuery(id+"F25.imprint","IMPRINT",EDGE,{"disambiguationData":[TD([[subQ2,-1.0]])],"derivedFrom":subQ1}),1.0]])]});}
            var Q143;
            {var subQ5=sQuery(id+"F25.wireOp",EDGE,"E253.right");Q143=makeQuery(id+"F25.imprint","IMPRINT",FACE,{"disambiguationData":[TD([[makeQuery(id+"F25.imprint","IMPRINT",EDGE,{"derivedFrom":subQ5}),1.0]])]});}
            var Q144;
            {var subQ5=sQuery(id+"F25.wireOp",EDGE,"E252.right");Q144=makeQuery(id+"F25.imprint","IMPRINT",FACE,{"disambiguationData":[TD([[makeQuery(id+"F25.imprint","IMPRINT",EDGE,{"derivedFrom":subQ5}),-1.0]])]});}
            var Q145;
            {var subQ0=sQuery(id+"F25.wireOp",EDGE,"E253.right");Q145=makeQuery(id+"F25.imprint","IMPRINT",FACE,{"disambiguationData":[TD([[makeQuery(id+"F25.imprint","IMPRINT",EDGE,{"derivedFrom":subQ0}),-1.0]])]});}
            var Q146;
            {var subQ0=sQuery(id+"F25.wireOp",EDGE,"E252.right");Q146=makeQuery(id+"F25.imprint","IMPRINT",FACE,{"disambiguationData":[TD([[makeQuery(id+"F25.imprint","IMPRINT",EDGE,{"derivedFrom":subQ0}),1.0]])]});}
            var Q147;
            {var subQ0=sQuery(id+"F25.wireOp",EDGE,"E518.trimOffspring");var subQ5=sQuery(id+"F25.wireOp",EDGE,"E249.right");var subQ7=makeQuery(id+"F25.imprint","INTERSECT",VERTEX,{"derivedFrom":[subQ5,subQ0]});Q147=makeQuery(id+"F25.imprint","IMPRINT",FACE,{"disambiguationData":[TD([[makeQuery(id+"F25.imprint","IMPRINT",EDGE,{"disambiguationData":[TD([[subQ7,-1.0]])],"derivedFrom":subQ5}),-1.0]])]});}
            var Q148;
            {var subQ0=sQuery(id+"F25.wireOp",EDGE,"E373.MirrorCS");var subQ5=sQuery(id+"F25.wireOp",EDGE,"E387.MirrorCS");var subQ6=makeQuery(id+"F25.imprint","INTERSECT",VERTEX,{"derivedFrom":[subQ0,subQ5]});Q148=makeQuery(id+"F25.imprint","IMPRINT",FACE,{"disambiguationData":[TD([[makeQuery(id+"F25.imprint","IMPRINT",EDGE,{"disambiguationData":[TD([[subQ6,-1.0]])],"derivedFrom":subQ5}),1.0]])]});}
            var Q149;
            {var subQ5=sQuery(id+"F25.wireOp",EDGE,"E236.right");Q149=makeQuery(id+"F25.imprint","IMPRINT",FACE,{"disambiguationData":[TD([[makeQuery(id+"F25.imprint","IMPRINT",EDGE,{"derivedFrom":subQ5}),-1.0]])]});}
            var Q150;
            {var subQ5=sQuery(id+"F25.wireOp",EDGE,"E235.right");Q150=makeQuery(id+"F25.imprint","IMPRINT",FACE,{"disambiguationData":[TD([[makeQuery(id+"F25.imprint","IMPRINT",EDGE,{"derivedFrom":subQ5}),1.0]])]});}
            var Q151;
            {var subQ0=sQuery(id+"F25.wireOp",EDGE,"E365.MirrorCS");var subQ1=sQuery(id+"F25.wireOp",EDGE,"E344.MirrorCS");var subQ2=makeQuery(id+"F25.imprint","INTERSECT",VERTEX,{"derivedFrom":[subQ1,subQ0]});Q151=makeQuery(id+"F25.imprint","IMPRINT",FACE,{"disambiguationData":[TD([[makeQuery(id+"F25.imprint","IMPRINT",EDGE,{"disambiguationData":[TD([[subQ2,-1.0]])],"derivedFrom":subQ1}),-1.0]])]});}
            var Q152;
            {var subQ0=sQuery(id+"F25.wireOp",EDGE,"E334.MirrorCS");var subQ1=sQuery(id+"F25.wireOp",EDGE,"E344.MirrorCS");var subQ2=makeQuery(id+"F25.imprint","INTERSECT",VERTEX,{"derivedFrom":[subQ1,subQ0]});Q152=makeQuery(id+"F25.imprint","IMPRINT",FACE,{"disambiguationData":[TD([[makeQuery(id+"F25.imprint","IMPRINT",EDGE,{"disambiguationData":[TD([[subQ2,-1.0]])],"derivedFrom":subQ1}),1.0]])]});}
            var Q153;
            {var subQ0=sQuery(id+"F25.wireOp",EDGE,"E334.MirrorCS");var subQ1=sQuery(id+"F25.wireOp",EDGE,"E344.MirrorCS");var subQ2=makeQuery(id+"F25.imprint","INTERSECT",VERTEX,{"derivedFrom":[subQ1,subQ0]});Q153=makeQuery(id+"F25.imprint","IMPRINT",FACE,{"disambiguationData":[TD([[makeQuery(id+"F25.imprint","IMPRINT",EDGE,{"disambiguationData":[TD([[subQ2,-1.0]])],"derivedFrom":subQ1}),-1.0]])]});}
            var Q154;
            {var subQ0=sQuery(id+"F25.wireOp",EDGE,"E386.MirrorCS");var subQ1=sQuery(id+"F25.wireOp",EDGE,"E344.MirrorCS");var subQ2=makeQuery(id+"F25.imprint","INTERSECT",VERTEX,{"derivedFrom":[subQ1,subQ0]});Q154=makeQuery(id+"F25.imprint","IMPRINT",FACE,{"disambiguationData":[TD([[makeQuery(id+"F25.imprint","IMPRINT",EDGE,{"disambiguationData":[TD([[subQ2,-1.0]])],"derivedFrom":subQ1}),-1.0]])]});}
            var Q155;
            {var subQ0=sQuery(id+"F25.wireOp",EDGE,"E386.MirrorCS");var subQ1=sQuery(id+"F25.wireOp",EDGE,"E344.MirrorCS");var subQ2=makeQuery(id+"F25.imprint","INTERSECT",VERTEX,{"derivedFrom":[subQ1,subQ0]});Q155=makeQuery(id+"F25.imprint","IMPRINT",FACE,{"disambiguationData":[TD([[makeQuery(id+"F25.imprint","IMPRINT",EDGE,{"disambiguationData":[TD([[subQ2,-1.0]])],"derivedFrom":subQ1}),1.0]])]});}
            var Q156;
            {var subQ0=sQuery(id+"F25.wireOp",EDGE,"E398.MirrorCS");var subQ1=sQuery(id+"F25.wireOp",EDGE,"E334.MirrorCS");var subQ2=makeQuery(id+"F25.imprint","INTERSECT",VERTEX,{"derivedFrom":[subQ1,subQ0]});Q156=makeQuery(id+"F25.imprint","IMPRINT",FACE,{"disambiguationData":[TD([[makeQuery(id+"F25.imprint","IMPRINT",EDGE,{"disambiguationData":[TD([[subQ2,-1.0]])],"derivedFrom":subQ1}),-1.0]])]});}
            var Q157;
            {var subQ0=sQuery(id+"F25.wireOp",EDGE,"E398.MirrorCS");var subQ1=sQuery(id+"F25.wireOp",EDGE,"E365.MirrorCS");var subQ2=makeQuery(id+"F25.imprint","INTERSECT",VERTEX,{"derivedFrom":[subQ1,subQ0]});Q157=makeQuery(id+"F25.imprint","IMPRINT",FACE,{"disambiguationData":[TD([[makeQuery(id+"F25.imprint","IMPRINT",EDGE,{"disambiguationData":[TD([[subQ2,-1.0]])],"derivedFrom":subQ1}),-1.0]])]});}
            var Q158;
            {var subQ0=sQuery(id+"F25.wireOp",EDGE,"E366.MirrorCS");var subQ1=sQuery(id+"F25.wireOp",EDGE,"E334.MirrorCS");var subQ2=makeQuery(id+"F25.imprint","INTERSECT",VERTEX,{"derivedFrom":[subQ1,subQ0]});Q158=makeQuery(id+"F25.imprint","IMPRINT",FACE,{"disambiguationData":[TD([[makeQuery(id+"F25.imprint","IMPRINT",EDGE,{"disambiguationData":[TD([[subQ2,-1.0]])],"derivedFrom":subQ1}),-1.0]])]});}
            var Q159;
            {var subQ0=sQuery(id+"F25.wireOp",EDGE,"E366.MirrorCS");var subQ1=sQuery(id+"F25.wireOp",EDGE,"E365.MirrorCS");var subQ2=makeQuery(id+"F25.imprint","INTERSECT",VERTEX,{"derivedFrom":[subQ1,subQ0]});Q159=makeQuery(id+"F25.imprint","IMPRINT",FACE,{"disambiguationData":[TD([[makeQuery(id+"F25.imprint","IMPRINT",EDGE,{"disambiguationData":[TD([[subQ2,-1.0]])],"derivedFrom":subQ1}),-1.0]])]});}
            var Q160;
            {var subQ0=sQuery(id+"F25.wireOp",EDGE,"E366.MirrorCS");var subQ1=sQuery(id+"F25.wireOp",EDGE,"E365.MirrorCS");var subQ2=makeQuery(id+"F25.imprint","INTERSECT",VERTEX,{"derivedFrom":[subQ1,subQ0]});Q160=makeQuery(id+"F25.imprint","IMPRINT",FACE,{"disambiguationData":[TD([[makeQuery(id+"F25.imprint","IMPRINT",EDGE,{"disambiguationData":[TD([[subQ2,-1.0]])],"derivedFrom":subQ1}),1.0]])]});}
            var Q161;
            {var subQ0=sQuery(id+"F25.wireOp",EDGE,"E365.MirrorCS");var subQ1=sQuery(id+"F25.wireOp",EDGE,"E347.MirrorCS");var subQ2=makeQuery(id+"F25.imprint","INTERSECT",VERTEX,{"derivedFrom":[subQ1,subQ0]});Q161=makeQuery(id+"F25.imprint","IMPRINT",FACE,{"disambiguationData":[TD([[makeQuery(id+"F25.imprint","IMPRINT",EDGE,{"disambiguationData":[TD([[subQ2,-1.0]])],"derivedFrom":subQ1}),-1.0]])]});}
            var Q162;
            {var subQ0=sQuery(id+"F25.wireOp",EDGE,"E334.MirrorCS");var subQ1=sQuery(id+"F25.wireOp",EDGE,"E347.MirrorCS");var subQ2=makeQuery(id+"F25.imprint","INTERSECT",VERTEX,{"derivedFrom":[subQ1,subQ0]});Q162=makeQuery(id+"F25.imprint","IMPRINT",FACE,{"disambiguationData":[TD([[makeQuery(id+"F25.imprint","IMPRINT",EDGE,{"disambiguationData":[TD([[subQ2,-1.0]])],"derivedFrom":subQ1}),-1.0]])]});}
            var Q163;
            {var subQ0=sQuery(id+"F25.wireOp",EDGE,"E386.MirrorCS");var subQ1=sQuery(id+"F25.wireOp",EDGE,"E347.MirrorCS");var subQ2=makeQuery(id+"F25.imprint","INTERSECT",VERTEX,{"derivedFrom":[subQ1,subQ0]});Q163=makeQuery(id+"F25.imprint","IMPRINT",FACE,{"disambiguationData":[TD([[makeQuery(id+"F25.imprint","IMPRINT",EDGE,{"disambiguationData":[TD([[subQ2,-1.0]])],"derivedFrom":subQ1}),-1.0]])]});}
            var Q164;
            {var subQ0=sQuery(id+"F25.wireOp",EDGE,"E386.MirrorCS");var subQ1=sQuery(id+"F25.wireOp",EDGE,"E347.MirrorCS");var subQ2=makeQuery(id+"F25.imprint","INTERSECT",VERTEX,{"derivedFrom":[subQ1,subQ0]});Q164=makeQuery(id+"F25.imprint","IMPRINT",FACE,{"disambiguationData":[TD([[makeQuery(id+"F25.imprint","IMPRINT",EDGE,{"disambiguationData":[TD([[subQ2,-1.0]])],"derivedFrom":subQ1}),1.0]])]});}
            var Q165;
            {var subQ0=sQuery(id+"F25.wireOp",EDGE,"E334.MirrorCS");var subQ1=sQuery(id+"F25.wireOp",EDGE,"E347.MirrorCS");var subQ2=makeQuery(id+"F25.imprint","INTERSECT",VERTEX,{"derivedFrom":[subQ1,subQ0]});Q165=makeQuery(id+"F25.imprint","IMPRINT",FACE,{"disambiguationData":[TD([[makeQuery(id+"F25.imprint","IMPRINT",EDGE,{"disambiguationData":[TD([[subQ2,-1.0]])],"derivedFrom":subQ1}),1.0]])]});}
            var Q166;
            {var subQ0=sQuery(id+"F25.wireOp",EDGE,"E237.right");Q166=makeQuery(id+"F25.imprint","IMPRINT",FACE,{"disambiguationData":[TD([[makeQuery(id+"F25.imprint","IMPRINT",EDGE,{"derivedFrom":subQ0}),-1.0]])]});}
            var Q167;
            {var subQ0=sQuery(id+"F25.wireOp",EDGE,"E238.right");Q167=makeQuery(id+"F25.imprint","IMPRINT",FACE,{"disambiguationData":[TD([[makeQuery(id+"F25.imprint","IMPRINT",EDGE,{"derivedFrom":subQ0}),1.0]])]});}
            var Q168;
            {var subQ0=sQuery(id+"F25.wireOp",EDGE,"E236.right");Q168=makeQuery(id+"F25.imprint","IMPRINT",FACE,{"disambiguationData":[TD([[makeQuery(id+"F25.imprint","IMPRINT",EDGE,{"derivedFrom":subQ0}),1.0]])]});}
            var Q169;
            {var subQ0=sQuery(id+"F25.wireOp",EDGE,"E365.MirrorCS");var subQ1=sQuery(id+"F25.wireOp",EDGE,"E344.MirrorCS");var subQ2=makeQuery(id+"F25.imprint","INTERSECT",VERTEX,{"derivedFrom":[subQ1,subQ0]});Q169=makeQuery(id+"F25.imprint","IMPRINT",FACE,{"disambiguationData":[TD([[makeQuery(id+"F25.imprint","IMPRINT",EDGE,{"disambiguationData":[TD([[subQ2,-1.0]])],"derivedFrom":subQ1}),1.0]])]});}
            var Q170;
            {var subQ5=sQuery(id+"F25.wireOp",EDGE,"E237.right");Q170=makeQuery(id+"F25.imprint","IMPRINT",FACE,{"disambiguationData":[TD([[makeQuery(id+"F25.imprint","IMPRINT",EDGE,{"derivedFrom":subQ5}),1.0]])]});}
            var Q171;
            {var subQ5=sQuery(id+"F25.wireOp",EDGE,"E238.right");Q171=makeQuery(id+"F25.imprint","IMPRINT",FACE,{"disambiguationData":[TD([[makeQuery(id+"F25.imprint","IMPRINT",EDGE,{"derivedFrom":subQ5}),-1.0]])]});}
            var Q172;
            {var subQ0=sQuery(id+"F25.wireOp",EDGE,"E295.trimOffspring");var subQ1=sQuery(id+"F25.wireOp",EDGE,"E249.right");var subQ2=makeQuery(id+"F25.imprint","INTERSECT",VERTEX,{"derivedFrom":[subQ1,subQ0]});Q172=makeQuery(id+"F25.imprint","IMPRINT",FACE,{"disambiguationData":[TD([[makeQuery(id+"F25.imprint","IMPRINT",EDGE,{"disambiguationData":[TD([[subQ2,-1.0]])],"derivedFrom":subQ1}),1.0]])]});}
            var Q173;
            {var subQ0=sQuery(id+"F25.wireOp",EDGE,"E296.trimOffspring");var subQ1=sQuery(id+"F25.wireOp",EDGE,"E249.right");var subQ2=makeQuery(id+"F25.imprint","INTERSECT",VERTEX,{"derivedFrom":[subQ1,subQ0]});Q173=makeQuery(id+"F25.imprint","IMPRINT",FACE,{"disambiguationData":[TD([[makeQuery(id+"F25.imprint","IMPRINT",EDGE,{"disambiguationData":[TD([[subQ2,-1.0]])],"derivedFrom":subQ1}),1.0]])]});}
            var Q174;
            {var subQ0=sQuery(id+"F25.wireOp",EDGE,"E296.trimOffspring");var subQ1=sQuery(id+"F25.wireOp",EDGE,"E250.right");var subQ2=makeQuery(id+"F25.imprint","INTERSECT",VERTEX,{"derivedFrom":[subQ1,subQ0]});Q174=makeQuery(id+"F25.imprint","IMPRINT",FACE,{"disambiguationData":[TD([[makeQuery(id+"F25.imprint","IMPRINT",EDGE,{"disambiguationData":[TD([[subQ2,-1.0]])],"derivedFrom":subQ1}),1.0]])]});}
            var Q175;
            {var subQ0=sQuery(id+"F25.wireOp",EDGE,"E296.trimOffspring");var subQ1=sQuery(id+"F25.wireOp",EDGE,"E250.left");var subQ2=makeQuery(id+"F25.imprint","INTERSECT",VERTEX,{"derivedFrom":[subQ1,subQ0]});Q175=makeQuery(id+"F25.imprint","IMPRINT",FACE,{"disambiguationData":[TD([[makeQuery(id+"F25.imprint","IMPRINT",EDGE,{"disambiguationData":[TD([[subQ2,-1.0]])],"derivedFrom":subQ1}),1.0]])]});}
            var Q176;
            {var subQ0=sQuery(id+"F25.wireOp",EDGE,"E295.trimOffspring");var subQ1=sQuery(id+"F25.wireOp",EDGE,"E250.left");var subQ2=makeQuery(id+"F25.imprint","INTERSECT",VERTEX,{"derivedFrom":[subQ1,subQ0]});Q176=makeQuery(id+"F25.imprint","IMPRINT",FACE,{"disambiguationData":[TD([[makeQuery(id+"F25.imprint","IMPRINT",EDGE,{"disambiguationData":[TD([[subQ2,-1.0]])],"derivedFrom":subQ1}),1.0]])]});}
            var Q177;
            {var subQ0=sQuery(id+"F25.wireOp",EDGE,"E295.trimOffspring");var subQ1=sQuery(id+"F25.wireOp",EDGE,"E250.right");var subQ2=makeQuery(id+"F25.imprint","INTERSECT",VERTEX,{"derivedFrom":[subQ1,subQ0]});Q177=makeQuery(id+"F25.imprint","IMPRINT",FACE,{"disambiguationData":[TD([[makeQuery(id+"F25.imprint","IMPRINT",EDGE,{"disambiguationData":[TD([[subQ2,-1.0]])],"derivedFrom":subQ1}),1.0]])]});}
            var Q178;
            {var subQ0=sQuery(id+"F25.wireOp",EDGE,"E251.bottom");Q178=makeQuery(id+"F25.imprint","IMPRINT",FACE,{"disambiguationData":[TD([[makeQuery(id+"F25.imprint","IMPRINT",EDGE,{"derivedFrom":subQ0}),-1.0]])]});}
            var Q179;
            {var subQ0=sQuery(id+"F25.wireOp",EDGE,"E250.bottom");Q179=makeQuery(id+"F25.imprint","IMPRINT",FACE,{"disambiguationData":[TD([[makeQuery(id+"F25.imprint","IMPRINT",EDGE,{"derivedFrom":subQ0}),1.0]])]});}
            var Q180;
            {var subQ0=sQuery(id+"F25.wireOp",EDGE,"E288.trimOffspring");var subQ1=sQuery(id+"F25.wireOp",EDGE,"E250.left");var subQ2=makeQuery(id+"F25.imprint","INTERSECT",VERTEX,{"derivedFrom":[subQ1,subQ0]});Q180=makeQuery(id+"F25.imprint","IMPRINT",FACE,{"disambiguationData":[TD([[makeQuery(id+"F25.imprint","IMPRINT",EDGE,{"disambiguationData":[TD([[subQ2,-1.0]])],"derivedFrom":subQ1}),1.0]])]});}
            var Q181;
            {var subQ0=sQuery(id+"F25.wireOp",EDGE,"E292.trimOffspring");var subQ1=sQuery(id+"F25.wireOp",EDGE,"E250.left");var subQ2=makeQuery(id+"F25.imprint","INTERSECT",VERTEX,{"derivedFrom":[subQ1,subQ0]});Q181=makeQuery(id+"F25.imprint","IMPRINT",FACE,{"disambiguationData":[TD([[makeQuery(id+"F25.imprint","IMPRINT",EDGE,{"disambiguationData":[TD([[subQ2,-1.0]])],"derivedFrom":subQ1}),1.0]])]});}
            var Q182;
            {var subQ0=sQuery(id+"F25.wireOp",EDGE,"E288.trimOffspring");var subQ1=sQuery(id+"F25.wireOp",EDGE,"E250.right");var subQ2=makeQuery(id+"F25.imprint","INTERSECT",VERTEX,{"derivedFrom":[subQ1,subQ0]});Q182=makeQuery(id+"F25.imprint","IMPRINT",FACE,{"disambiguationData":[TD([[makeQuery(id+"F25.imprint","IMPRINT",EDGE,{"disambiguationData":[TD([[subQ2,-1.0]])],"derivedFrom":subQ1}),1.0]])]});}
            var Q183;
            {var subQ0=sQuery(id+"F25.wireOp",EDGE,"E292.trimOffspring");var subQ1=sQuery(id+"F25.wireOp",EDGE,"E250.right");var subQ2=makeQuery(id+"F25.imprint","INTERSECT",VERTEX,{"derivedFrom":[subQ1,subQ0]});Q183=makeQuery(id+"F25.imprint","IMPRINT",FACE,{"disambiguationData":[TD([[makeQuery(id+"F25.imprint","IMPRINT",EDGE,{"disambiguationData":[TD([[subQ2,-1.0]])],"derivedFrom":subQ1}),1.0]])]});}
            var Q184;
            {var subQ0=sQuery(id+"F25.wireOp",EDGE,"E288.trimOffspring");var subQ1=sQuery(id+"F25.wireOp",EDGE,"E249.right");var subQ2=makeQuery(id+"F25.imprint","INTERSECT",VERTEX,{"derivedFrom":[subQ1,subQ0]});Q184=makeQuery(id+"F25.imprint","IMPRINT",FACE,{"disambiguationData":[TD([[makeQuery(id+"F25.imprint","IMPRINT",EDGE,{"disambiguationData":[TD([[subQ2,-1.0]])],"derivedFrom":subQ1}),1.0]])]});}
            var Q185;
            {var subQ0=sQuery(id+"F25.wireOp",EDGE,"E292.trimOffspring");var subQ1=sQuery(id+"F25.wireOp",EDGE,"E249.right");var subQ2=makeQuery(id+"F25.imprint","INTERSECT",VERTEX,{"derivedFrom":[subQ1,subQ0]});Q185=makeQuery(id+"F25.imprint","IMPRINT",FACE,{"disambiguationData":[TD([[makeQuery(id+"F25.imprint","IMPRINT",EDGE,{"disambiguationData":[TD([[subQ2,-1.0]])],"derivedFrom":subQ1}),1.0]])]});}
            var Q186;
            {var subQ5=sQuery(id+"F25.wireOp",EDGE,"E242.right");Q186=makeQuery(id+"F25.imprint","IMPRINT",FACE,{"disambiguationData":[TD([[makeQuery(id+"F25.imprint","IMPRINT",EDGE,{"derivedFrom":subQ5}),-1.0]])]});}
            var Q187;
            {var subQ0=sQuery(id+"F25.wireOp",EDGE,"E242.right");Q187=makeQuery(id+"F25.imprint","IMPRINT",FACE,{"disambiguationData":[TD([[makeQuery(id+"F25.imprint","IMPRINT",EDGE,{"derivedFrom":subQ0}),1.0]])]});}
            var Q188;
            {var subQ5=sQuery(id+"F25.wireOp",EDGE,"E241.right");Q188=makeQuery(id+"F25.imprint","IMPRINT",FACE,{"disambiguationData":[TD([[makeQuery(id+"F25.imprint","IMPRINT",EDGE,{"derivedFrom":subQ5}),1.0]])]});}
            var Q189;
            {var subQ0=sQuery(id+"F25.wireOp",EDGE,"E241.right");Q189=makeQuery(id+"F25.imprint","IMPRINT",FACE,{"disambiguationData":[TD([[makeQuery(id+"F25.imprint","IMPRINT",EDGE,{"derivedFrom":subQ0}),-1.0]])]});}
            var Q190;
            {var subQ0=sQuery(id+"F25.wireOp",EDGE,"E365.MirrorCS");var subQ1=sQuery(id+"F25.wireOp",EDGE,"E341.MirrorCS");var subQ2=makeQuery(id+"F25.imprint","INTERSECT",VERTEX,{"derivedFrom":[subQ1,subQ0]});Q190=makeQuery(id+"F25.imprint","IMPRINT",FACE,{"disambiguationData":[TD([[makeQuery(id+"F25.imprint","IMPRINT",EDGE,{"disambiguationData":[TD([[subQ2,-1.0]])],"derivedFrom":subQ1}),-1.0]])]});}
            var Q191;
            {var subQ0=sQuery(id+"F25.wireOp",EDGE,"E356.MirrorCS");var subQ1=sQuery(id+"F25.wireOp",EDGE,"E365.MirrorCS");var subQ2=makeQuery(id+"F25.imprint","INTERSECT",VERTEX,{"derivedFrom":[subQ1,subQ0]});Q191=makeQuery(id+"F25.imprint","IMPRINT",FACE,{"disambiguationData":[TD([[makeQuery(id+"F25.imprint","IMPRINT",EDGE,{"disambiguationData":[TD([[subQ2,-1.0]])],"derivedFrom":subQ1}),1.0]])]});}
            var Q192;
            {var subQ0=sQuery(id+"F25.wireOp",EDGE,"E334.MirrorCS");var subQ1=sQuery(id+"F25.wireOp",EDGE,"E341.MirrorCS");var subQ2=makeQuery(id+"F25.imprint","INTERSECT",VERTEX,{"derivedFrom":[subQ1,subQ0]});Q192=makeQuery(id+"F25.imprint","IMPRINT",FACE,{"disambiguationData":[TD([[makeQuery(id+"F25.imprint","IMPRINT",EDGE,{"disambiguationData":[TD([[subQ2,-1.0]])],"derivedFrom":subQ1}),-1.0]])]});}
            var Q193;
            {var subQ0=sQuery(id+"F25.wireOp",EDGE,"E356.MirrorCS");var subQ1=sQuery(id+"F25.wireOp",EDGE,"E365.MirrorCS");var subQ2=makeQuery(id+"F25.imprint","INTERSECT",VERTEX,{"derivedFrom":[subQ1,subQ0]});Q193=makeQuery(id+"F25.imprint","IMPRINT",FACE,{"disambiguationData":[TD([[makeQuery(id+"F25.imprint","IMPRINT",EDGE,{"disambiguationData":[TD([[subQ2,-1.0]])],"derivedFrom":subQ1}),-1.0]])]});}
            var Q194;
            {var subQ0=sQuery(id+"F25.wireOp",EDGE,"E386.MirrorCS");var subQ1=sQuery(id+"F25.wireOp",EDGE,"E341.MirrorCS");var subQ2=makeQuery(id+"F25.imprint","INTERSECT",VERTEX,{"derivedFrom":[subQ1,subQ0]});Q194=makeQuery(id+"F25.imprint","IMPRINT",FACE,{"disambiguationData":[TD([[makeQuery(id+"F25.imprint","IMPRINT",EDGE,{"disambiguationData":[TD([[subQ2,-1.0]])],"derivedFrom":subQ1}),-1.0]])]});}
            var Q195;
            {var subQ0=sQuery(id+"F25.wireOp",EDGE,"E356.MirrorCS");var subQ1=sQuery(id+"F25.wireOp",EDGE,"E334.MirrorCS");var subQ2=makeQuery(id+"F25.imprint","INTERSECT",VERTEX,{"derivedFrom":[subQ1,subQ0]});Q195=makeQuery(id+"F25.imprint","IMPRINT",FACE,{"disambiguationData":[TD([[makeQuery(id+"F25.imprint","IMPRINT",EDGE,{"disambiguationData":[TD([[subQ2,-1.0]])],"derivedFrom":subQ1}),-1.0]])]});}
            var Q196;
            {var subQ0=sQuery(id+"F25.wireOp",EDGE,"E386.MirrorCS");var subQ1=sQuery(id+"F25.wireOp",EDGE,"E339.MirrorCS");var subQ2=makeQuery(id+"F25.imprint","INTERSECT",VERTEX,{"derivedFrom":[subQ1,subQ0]});Q196=makeQuery(id+"F25.imprint","IMPRINT",FACE,{"disambiguationData":[TD([[makeQuery(id+"F25.imprint","IMPRINT",EDGE,{"disambiguationData":[TD([[subQ2,-1.0]])],"derivedFrom":subQ1}),1.0]])]});}
            var Q197;
            {var subQ0=sQuery(id+"F25.wireOp",EDGE,"E334.MirrorCS");var subQ1=sQuery(id+"F25.wireOp",EDGE,"E339.MirrorCS");var subQ2=makeQuery(id+"F25.imprint","INTERSECT",VERTEX,{"derivedFrom":[subQ1,subQ0]});Q197=makeQuery(id+"F25.imprint","IMPRINT",FACE,{"disambiguationData":[TD([[makeQuery(id+"F25.imprint","IMPRINT",EDGE,{"disambiguationData":[TD([[subQ2,-1.0]])],"derivedFrom":subQ1}),1.0]])]});}
            var Q198;
            {var subQ0=sQuery(id+"F25.wireOp",EDGE,"E334.MirrorCS");var subQ1=sQuery(id+"F25.wireOp",EDGE,"E339.MirrorCS");var subQ2=makeQuery(id+"F25.imprint","INTERSECT",VERTEX,{"derivedFrom":[subQ1,subQ0]});Q198=makeQuery(id+"F25.imprint","IMPRINT",FACE,{"disambiguationData":[TD([[makeQuery(id+"F25.imprint","IMPRINT",EDGE,{"disambiguationData":[TD([[subQ2,-1.0]])],"derivedFrom":subQ1}),-1.0]])]});}
            var Q199;
            {var subQ0=sQuery(id+"F25.wireOp",EDGE,"E361.MirrorCS");var subQ1=sQuery(id+"F25.wireOp",EDGE,"E365.MirrorCS");var subQ2=makeQuery(id+"F25.imprint","INTERSECT",VERTEX,{"derivedFrom":[subQ1,subQ0]});Q199=makeQuery(id+"F25.imprint","IMPRINT",FACE,{"disambiguationData":[TD([[makeQuery(id+"F25.imprint","IMPRINT",EDGE,{"disambiguationData":[TD([[subQ2,-1.0]])],"derivedFrom":subQ1}),-1.0]])]});}
            var Q200;
            {var subQ0=sQuery(id+"F25.wireOp",EDGE,"E361.MirrorCS");var subQ1=sQuery(id+"F25.wireOp",EDGE,"E334.MirrorCS");var subQ2=makeQuery(id+"F25.imprint","INTERSECT",VERTEX,{"derivedFrom":[subQ1,subQ0]});Q200=makeQuery(id+"F25.imprint","IMPRINT",FACE,{"disambiguationData":[TD([[makeQuery(id+"F25.imprint","IMPRINT",EDGE,{"disambiguationData":[TD([[subQ2,-1.0]])],"derivedFrom":subQ1}),-1.0]])]});}
            var Q201;
            {var subQ0=sQuery(id+"F25.wireOp",EDGE,"E386.MirrorCS");var subQ1=sQuery(id+"F25.wireOp",EDGE,"E339.MirrorCS");var subQ2=makeQuery(id+"F25.imprint","INTERSECT",VERTEX,{"derivedFrom":[subQ1,subQ0]});Q201=makeQuery(id+"F25.imprint","IMPRINT",FACE,{"disambiguationData":[TD([[makeQuery(id+"F25.imprint","IMPRINT",EDGE,{"disambiguationData":[TD([[subQ2,-1.0]])],"derivedFrom":subQ1}),-1.0]])]});}
            var Q202;
            {var subQ0=sQuery(id+"F25.wireOp",EDGE,"E361.MirrorCS");var subQ1=sQuery(id+"F25.wireOp",EDGE,"E365.MirrorCS");var subQ2=makeQuery(id+"F25.imprint","INTERSECT",VERTEX,{"derivedFrom":[subQ1,subQ0]});Q202=makeQuery(id+"F25.imprint","IMPRINT",FACE,{"disambiguationData":[TD([[makeQuery(id+"F25.imprint","IMPRINT",EDGE,{"disambiguationData":[TD([[subQ2,-1.0]])],"derivedFrom":subQ1}),1.0]])]});}
            var Q203;
            {var subQ0=sQuery(id+"F25.wireOp",EDGE,"E365.MirrorCS");var subQ1=sQuery(id+"F25.wireOp",EDGE,"E339.MirrorCS");var subQ2=makeQuery(id+"F25.imprint","INTERSECT",VERTEX,{"derivedFrom":[subQ1,subQ0]});Q203=makeQuery(id+"F25.imprint","IMPRINT",FACE,{"disambiguationData":[TD([[makeQuery(id+"F25.imprint","IMPRINT",EDGE,{"disambiguationData":[TD([[subQ2,-1.0]])],"derivedFrom":subQ1}),-1.0]])]});}
            var Q204;
            {var subQ0=sQuery(id+"F25.wireOp",EDGE,"E386.MirrorCS");var subQ1=sQuery(id+"F25.wireOp",EDGE,"E339.MirrorCS");var subQ2=makeQuery(id+"F25.imprint","INTERSECT",VERTEX,{"derivedFrom":[subQ1,subQ0]});Q204=makeQuery(id+"F25.imprint","IMPRINT",FACE,{"disambiguationData":[TD([[makeQuery(id+"F25.imprint","IMPRINT",EDGE,{"disambiguationData":[TD([[subQ2,-1.0]])],"derivedFrom":subQ1}),-1.0]])]});}
            var Q205;
            {var subQ0=sQuery(id+"F25.wireOp",EDGE,"E240.right");Q205=makeQuery(id+"F25.imprint","IMPRINT",FACE,{"disambiguationData":[TD([[makeQuery(id+"F25.imprint","IMPRINT",EDGE,{"derivedFrom":subQ0}),1.0]])]});}
            var Q206;
            {var subQ0=sQuery(id+"F25.wireOp",EDGE,"E239.right");Q206=makeQuery(id+"F25.imprint","IMPRINT",FACE,{"disambiguationData":[TD([[makeQuery(id+"F25.imprint","IMPRINT",EDGE,{"derivedFrom":subQ0}),-1.0]])]});}
            var Q207;
            {var subQ5=sQuery(id+"F25.wireOp",EDGE,"E239.right");Q207=makeQuery(id+"F25.imprint","IMPRINT",FACE,{"disambiguationData":[TD([[makeQuery(id+"F25.imprint","IMPRINT",EDGE,{"derivedFrom":subQ5}),1.0]])]});}
            var Q208;
            {var subQ5=sQuery(id+"F25.wireOp",EDGE,"E240.right");Q208=makeQuery(id+"F25.imprint","IMPRINT",FACE,{"disambiguationData":[TD([[makeQuery(id+"F25.imprint","IMPRINT",EDGE,{"derivedFrom":subQ5}),-1.0]])]});}
            var Q209;
            {var subQ0=sQuery(id+"F25.wireOp",EDGE,"E293.trimOffspring");var subQ1=sQuery(id+"F25.wireOp",EDGE,"E249.right");var subQ2=makeQuery(id+"F25.imprint","INTERSECT",VERTEX,{"derivedFrom":[subQ1,subQ0]});Q209=makeQuery(id+"F25.imprint","IMPRINT",FACE,{"disambiguationData":[TD([[makeQuery(id+"F25.imprint","IMPRINT",EDGE,{"disambiguationData":[TD([[subQ2,-1.0]])],"derivedFrom":subQ1}),1.0]])]});}
            var Q210;
            {var subQ0=sQuery(id+"F25.wireOp",EDGE,"E297.trimOffspring");var subQ1=sQuery(id+"F25.wireOp",EDGE,"E249.right");var subQ2=makeQuery(id+"F25.imprint","INTERSECT",VERTEX,{"derivedFrom":[subQ1,subQ0]});Q210=makeQuery(id+"F25.imprint","IMPRINT",FACE,{"disambiguationData":[TD([[makeQuery(id+"F25.imprint","IMPRINT",EDGE,{"disambiguationData":[TD([[subQ2,-1.0]])],"derivedFrom":subQ1}),1.0]])]});}
            var Q211;
            {var subQ0=sQuery(id+"F25.wireOp",EDGE,"E297.trimOffspring");var subQ1=sQuery(id+"F25.wireOp",EDGE,"E250.right");var subQ2=makeQuery(id+"F25.imprint","INTERSECT",VERTEX,{"derivedFrom":[subQ1,subQ0]});Q211=makeQuery(id+"F25.imprint","IMPRINT",FACE,{"disambiguationData":[TD([[makeQuery(id+"F25.imprint","IMPRINT",EDGE,{"disambiguationData":[TD([[subQ2,-1.0]])],"derivedFrom":subQ1}),1.0]])]});}
            var Q212;
            {var subQ0=sQuery(id+"F25.wireOp",EDGE,"E297.trimOffspring");var subQ1=sQuery(id+"F25.wireOp",EDGE,"E250.left");var subQ2=makeQuery(id+"F25.imprint","INTERSECT",VERTEX,{"derivedFrom":[subQ1,subQ0]});Q212=makeQuery(id+"F25.imprint","IMPRINT",FACE,{"disambiguationData":[TD([[makeQuery(id+"F25.imprint","IMPRINT",EDGE,{"disambiguationData":[TD([[subQ2,-1.0]])],"derivedFrom":subQ1}),1.0]])]});}
            var Q213;
            {var subQ0=sQuery(id+"F25.wireOp",EDGE,"E293.trimOffspring");var subQ1=sQuery(id+"F25.wireOp",EDGE,"E250.left");var subQ2=makeQuery(id+"F25.imprint","INTERSECT",VERTEX,{"derivedFrom":[subQ1,subQ0]});Q213=makeQuery(id+"F25.imprint","IMPRINT",FACE,{"disambiguationData":[TD([[makeQuery(id+"F25.imprint","IMPRINT",EDGE,{"disambiguationData":[TD([[subQ2,-1.0]])],"derivedFrom":subQ1}),1.0]])]});}
            var Q214;
            {var subQ0=sQuery(id+"F25.wireOp",EDGE,"E293.trimOffspring");var subQ1=sQuery(id+"F25.wireOp",EDGE,"E250.right");var subQ2=makeQuery(id+"F25.imprint","INTERSECT",VERTEX,{"derivedFrom":[subQ1,subQ0]});Q214=makeQuery(id+"F25.imprint","IMPRINT",FACE,{"disambiguationData":[TD([[makeQuery(id+"F25.imprint","IMPRINT",EDGE,{"disambiguationData":[TD([[subQ2,-1.0]])],"derivedFrom":subQ1}),1.0]])]});}
            var Q215;
            {var subQ0=sQuery(id+"F25.wireOp",EDGE,"E232.left");Q215=makeQuery(id+"F25.imprint","IMPRINT",FACE,{"disambiguationData":[TD([[makeQuery(id+"F25.imprint","IMPRINT",EDGE,{"derivedFrom":subQ0}),-1.0]])]});}
            var Q216;
            {var subQ0=sQuery(id+"F25.wireOp",EDGE,"E255.trimOffspring");var subQ1=sQuery(id+"F25.wireOp",EDGE,"E232.top");var subQ2=makeQuery(id+"F25.imprint","INTERSECT",VERTEX,{"derivedFrom":[subQ1,subQ0]});Q216=makeQuery(id+"F25.imprint","IMPRINT",FACE,{"disambiguationData":[TD([[makeQuery(id+"F25.imprint","IMPRINT",EDGE,{"disambiguationData":[TD([[subQ2,-1.0]])],"derivedFrom":subQ1}),-1.0]])]});}
            var Q217;
            {var subQ1=sQuery(id+"F25.wireOp",EDGE,"E232.top");var subQ3=sQuery(id+"F25.wireOp",EDGE,"E256.trimOffspring");var subQ4=makeQuery(id+"F25.imprint","INTERSECT",VERTEX,{"derivedFrom":[subQ1,subQ3]});Q217=makeQuery(id+"F25.imprint","IMPRINT",FACE,{"disambiguationData":[TD([[makeQuery(id+"F25.imprint","IMPRINT",EDGE,{"disambiguationData":[TD([[subQ4,1.0]])],"derivedFrom":subQ3}),-1.0]])]});}
            var Q218;
            {var subQ1=sQuery(id+"F25.wireOp",EDGE,"E234.bottom");var subQ3=sQuery(id+"F25.wireOp",EDGE,"E256.trimOffspring");var subQ4=makeQuery(id+"F25.imprint","INTERSECT",VERTEX,{"derivedFrom":[subQ1,subQ3]});Q218=makeQuery(id+"F25.imprint","IMPRINT",FACE,{"disambiguationData":[TD([[makeQuery(id+"F25.imprint","IMPRINT",EDGE,{"disambiguationData":[TD([[subQ4,1.0]])],"derivedFrom":subQ3}),-1.0]])]});}
            var Q219;
            {var subQ0=sQuery(id+"F25.wireOp",EDGE,"E254.trimOffspring");var subQ5=sQuery(id+"F25.wireOp",EDGE,"E253.top");var subQ6=makeQuery(id+"F25.imprint","INTERSECT",VERTEX,{"derivedFrom":[subQ5,subQ0]});Q219=makeQuery(id+"F25.imprint","IMPRINT",FACE,{"disambiguationData":[TD([[makeQuery(id+"F25.imprint","IMPRINT",EDGE,{"disambiguationData":[TD([[subQ6,1.0]])],"derivedFrom":subQ5}),1.0]])]});}
            var Q220;
            {var subQ0=sQuery(id+"F25.wireOp",EDGE,"E254.trimOffspring");var subQ1=sQuery(id+"F25.wireOp",EDGE,"E253.bottom");var subQ2=makeQuery(id+"F25.imprint","INTERSECT",VERTEX,{"derivedFrom":[subQ1,subQ0]});Q220=makeQuery(id+"F25.imprint","IMPRINT",FACE,{"disambiguationData":[TD([[makeQuery(id+"F25.imprint","IMPRINT",EDGE,{"disambiguationData":[TD([[subQ2,1.0]])],"derivedFrom":subQ1}),1.0]])]});}
            var Q221;
            {var subQ0=sQuery(id+"F25.wireOp",EDGE,"E254.trimOffspring");var subQ1=sQuery(id+"F25.wireOp",EDGE,"E252.top");var subQ2=makeQuery(id+"F25.imprint","INTERSECT",VERTEX,{"derivedFrom":[subQ1,subQ0]});Q221=makeQuery(id+"F25.imprint","IMPRINT",FACE,{"disambiguationData":[TD([[makeQuery(id+"F25.imprint","IMPRINT",EDGE,{"disambiguationData":[TD([[subQ2,1.0]])],"derivedFrom":subQ1}),1.0]])]});}
            var Q222;
            {var subQ0=sQuery(id+"F25.wireOp",EDGE,"E256.trimOffspring");var subQ1=sQuery(id+"F25.wireOp",EDGE,"E235.top");var subQ2=makeQuery(id+"F25.imprint","INTERSECT",VERTEX,{"derivedFrom":[subQ1,subQ0]});Q222=makeQuery(id+"F25.imprint","IMPRINT",FACE,{"disambiguationData":[TD([[makeQuery(id+"F25.imprint","IMPRINT",EDGE,{"disambiguationData":[TD([[subQ2,-1.0]])],"derivedFrom":subQ1}),1.0]])]});}
            var Q223;
            {var subQ0=sQuery(id+"F25.wireOp",EDGE,"E256.trimOffspring");var subQ1=sQuery(id+"F25.wireOp",EDGE,"E235.top");var subQ2=makeQuery(id+"F25.imprint","INTERSECT",VERTEX,{"derivedFrom":[subQ1,subQ0]});Q223=makeQuery(id+"F25.imprint","IMPRINT",FACE,{"disambiguationData":[TD([[makeQuery(id+"F25.imprint","IMPRINT",EDGE,{"disambiguationData":[TD([[subQ2,-1.0]])],"derivedFrom":subQ1}),-1.0]])]});}
            var Q224;
            {var subQ0=sQuery(id+"F25.wireOp",EDGE,"E254.trimOffspring");var subQ1=sQuery(id+"F25.wireOp",EDGE,"E235.top");var subQ2=makeQuery(id+"F25.imprint","INTERSECT",VERTEX,{"derivedFrom":[subQ1,subQ0]});Q224=makeQuery(id+"F25.imprint","IMPRINT",FACE,{"disambiguationData":[TD([[makeQuery(id+"F25.imprint","IMPRINT",EDGE,{"disambiguationData":[TD([[subQ2,-1.0]])],"derivedFrom":subQ1}),-1.0]])]});}
            var Q225;
            {var subQ0=sQuery(id+"F25.wireOp",EDGE,"E257.trimOffspring");var subQ1=sQuery(id+"F25.wireOp",EDGE,"E235.top");var subQ2=makeQuery(id+"F25.imprint","INTERSECT",VERTEX,{"derivedFrom":[subQ1,subQ0]});Q225=makeQuery(id+"F25.imprint","IMPRINT",FACE,{"disambiguationData":[TD([[makeQuery(id+"F25.imprint","IMPRINT",EDGE,{"disambiguationData":[TD([[subQ2,-1.0]])],"derivedFrom":subQ1}),-1.0]])]});}
            var Q226;
            {var subQ0=sQuery(id+"F25.wireOp",EDGE,"E259.trimOffspring");var subQ1=sQuery(id+"F25.wireOp",EDGE,"E235.top");var subQ2=makeQuery(id+"F25.imprint","INTERSECT",VERTEX,{"derivedFrom":[subQ1,subQ0]});Q226=makeQuery(id+"F25.imprint","IMPRINT",FACE,{"disambiguationData":[TD([[makeQuery(id+"F25.imprint","IMPRINT",EDGE,{"disambiguationData":[TD([[subQ2,-1.0]])],"derivedFrom":subQ1}),-1.0]])]});}
            var Q227;
            {var subQ1=sQuery(id+"F25.wireOp",EDGE,"E235.top");var subQ3=sQuery(id+"F25.wireOp",EDGE,"E258.trimOffspring");var subQ4=makeQuery(id+"F25.imprint","INTERSECT",VERTEX,{"derivedFrom":[subQ1,subQ3]});Q227=makeQuery(id+"F25.imprint","IMPRINT",FACE,{"disambiguationData":[TD([[makeQuery(id+"F25.imprint","IMPRINT",EDGE,{"disambiguationData":[TD([[subQ4,1.0]])],"derivedFrom":subQ3}),-1.0]])]});}
            var Q228;
            {var subQ0=sQuery(id+"F25.wireOp",EDGE,"E257.trimOffspring");var subQ1=sQuery(id+"F25.wireOp",EDGE,"E235.top");var subQ2=makeQuery(id+"F25.imprint","INTERSECT",VERTEX,{"derivedFrom":[subQ1,subQ0]});Q228=makeQuery(id+"F25.imprint","IMPRINT",FACE,{"disambiguationData":[TD([[makeQuery(id+"F25.imprint","IMPRINT",EDGE,{"disambiguationData":[TD([[subQ2,-1.0]])],"derivedFrom":subQ1}),1.0]])]});}
            var Q229;
            {var subQ0=sQuery(id+"F25.wireOp",EDGE,"E259.trimOffspring");var subQ1=sQuery(id+"F25.wireOp",EDGE,"E235.top");var subQ2=makeQuery(id+"F25.imprint","INTERSECT",VERTEX,{"derivedFrom":[subQ1,subQ0]});Q229=makeQuery(id+"F25.imprint","IMPRINT",FACE,{"disambiguationData":[TD([[makeQuery(id+"F25.imprint","IMPRINT",EDGE,{"disambiguationData":[TD([[subQ2,-1.0]])],"derivedFrom":subQ1}),1.0]])]});}
            var Q230;
            {var subQ0=sQuery(id+"F25.wireOp",EDGE,"E499.trimOffspring");var subQ1=sQuery(id+"F25.wireOp",EDGE,"E257.trimOffspring");var subQ2=makeQuery(id+"F25.imprint","INTERSECT",VERTEX,{"derivedFrom":[subQ1,subQ0]});Q230=makeQuery(id+"F25.imprint","IMPRINT",FACE,{"disambiguationData":[TD([[makeQuery(id+"F25.imprint","IMPRINT",EDGE,{"disambiguationData":[TD([[subQ2,1.0]])],"derivedFrom":subQ1}),-1.0]])]});}
            var Q231;
            {var subQ0=sQuery(id+"F25.wireOp",EDGE,"E499.trimOffspring");var subQ1=sQuery(id+"F25.wireOp",EDGE,"E258.trimOffspring");var subQ2=makeQuery(id+"F25.imprint","INTERSECT",VERTEX,{"derivedFrom":[subQ1,subQ0]});Q231=makeQuery(id+"F25.imprint","IMPRINT",FACE,{"disambiguationData":[TD([[makeQuery(id+"F25.imprint","IMPRINT",EDGE,{"disambiguationData":[TD([[subQ2,1.0]])],"derivedFrom":subQ1}),1.0]])]});}
            var Q232;
            {var subQ0=sQuery(id+"F25.wireOp",EDGE,"E499.trimOffspring");var subQ1=sQuery(id+"F25.wireOp",EDGE,"E257.trimOffspring");var subQ2=makeQuery(id+"F25.imprint","INTERSECT",VERTEX,{"derivedFrom":[subQ1,subQ0]});Q232=makeQuery(id+"F25.imprint","IMPRINT",FACE,{"disambiguationData":[TD([[makeQuery(id+"F25.imprint","IMPRINT",EDGE,{"disambiguationData":[TD([[subQ2,-1.0]])],"derivedFrom":subQ1}),-1.0]])]});}
            var Q233;
            {var subQ0=sQuery(id+"F25.wireOp",EDGE,"E499.trimOffspring");var subQ1=sQuery(id+"F25.wireOp",EDGE,"E258.trimOffspring");var subQ2=makeQuery(id+"F25.imprint","INTERSECT",VERTEX,{"derivedFrom":[subQ1,subQ0]});Q233=makeQuery(id+"F25.imprint","IMPRINT",FACE,{"disambiguationData":[TD([[makeQuery(id+"F25.imprint","IMPRINT",EDGE,{"disambiguationData":[TD([[subQ2,-1.0]])],"derivedFrom":subQ1}),1.0]])]});}
            var Q234;
            {var subQ3=sQuery(id+"F25.wireOp",EDGE,"E497.trimOffspring");var subQ5=sQuery(id+"F25.wireOp",EDGE,"E259.trimOffspring");var subQ6=makeQuery(id+"F25.imprint","INTERSECT",VERTEX,{"derivedFrom":[subQ5,subQ3]});Q234=makeQuery(id+"F25.imprint","IMPRINT",FACE,{"disambiguationData":[TD([[makeQuery(id+"F25.imprint","IMPRINT",EDGE,{"disambiguationData":[TD([[subQ6,-1.0]])],"derivedFrom":subQ5}),1.0]])]});}
            var Q235;
            {var subQ0=sQuery(id+"F25.wireOp",EDGE,"E497.trimOffspring");var subQ1=sQuery(id+"F25.wireOp",EDGE,"E258.trimOffspring");var subQ2=makeQuery(id+"F25.imprint","INTERSECT",VERTEX,{"derivedFrom":[subQ1,subQ0]});Q235=makeQuery(id+"F25.imprint","IMPRINT",FACE,{"disambiguationData":[TD([[makeQuery(id+"F25.imprint","IMPRINT",EDGE,{"disambiguationData":[TD([[subQ2,-1.0]])],"derivedFrom":subQ1}),1.0]])]});}
            var Q236;
            {var subQ3=sQuery(id+"F25.wireOp",EDGE,"E496.trimOffspring");var subQ5=sQuery(id+"F25.wireOp",EDGE,"E259.trimOffspring");var subQ6=makeQuery(id+"F25.imprint","INTERSECT",VERTEX,{"derivedFrom":[subQ5,subQ3]});Q236=makeQuery(id+"F25.imprint","IMPRINT",FACE,{"disambiguationData":[TD([[makeQuery(id+"F25.imprint","IMPRINT",EDGE,{"disambiguationData":[TD([[subQ6,1.0]])],"derivedFrom":subQ5}),1.0]])]});}
            var Q237;
            {var subQ0=sQuery(id+"F25.wireOp",EDGE,"E496.trimOffspring");var subQ1=sQuery(id+"F25.wireOp",EDGE,"E258.trimOffspring");var subQ2=makeQuery(id+"F25.imprint","INTERSECT",VERTEX,{"derivedFrom":[subQ1,subQ0]});Q237=makeQuery(id+"F25.imprint","IMPRINT",FACE,{"disambiguationData":[TD([[makeQuery(id+"F25.imprint","IMPRINT",EDGE,{"disambiguationData":[TD([[subQ2,1.0]])],"derivedFrom":subQ1}),1.0]])]});}
            var Q238;
            {var subQ3=sQuery(id+"F25.wireOp",EDGE,"E504.trimOffspring");var subQ5=sQuery(id+"F25.wireOp",EDGE,"E261.trimOffspring");var subQ6=makeQuery(id+"F25.imprint","INTERSECT",VERTEX,{"derivedFrom":[subQ5,subQ3]});Q238=makeQuery(id+"F25.imprint","IMPRINT",FACE,{"disambiguationData":[TD([[makeQuery(id+"F25.imprint","IMPRINT",EDGE,{"disambiguationData":[TD([[subQ6,-1.0]])],"derivedFrom":subQ5}),1.0]])]});}
            var Q239;
            {var subQ0=sQuery(id+"F25.wireOp",EDGE,"E504.trimOffspring");var subQ1=sQuery(id+"F25.wireOp",EDGE,"E260.trimOffspring");var subQ2=makeQuery(id+"F25.imprint","INTERSECT",VERTEX,{"derivedFrom":[subQ1,subQ0]});Q239=makeQuery(id+"F25.imprint","IMPRINT",FACE,{"disambiguationData":[TD([[makeQuery(id+"F25.imprint","IMPRINT",EDGE,{"disambiguationData":[TD([[subQ2,-1.0]])],"derivedFrom":subQ1}),1.0]])]});}
            var Q240;
            {var subQ0=sQuery(id+"F25.wireOp",EDGE,"E504.trimOffspring");var subQ1=sQuery(id+"F25.wireOp",EDGE,"E260.trimOffspring");var subQ2=makeQuery(id+"F25.imprint","INTERSECT",VERTEX,{"derivedFrom":[subQ1,subQ0]});Q240=makeQuery(id+"F25.imprint","IMPRINT",FACE,{"disambiguationData":[TD([[makeQuery(id+"F25.imprint","IMPRINT",EDGE,{"disambiguationData":[TD([[subQ2,-1.0]])],"derivedFrom":subQ1}),-1.0]])]});}
            var Q241;
            {var subQ0=sQuery(id+"F25.wireOp",EDGE,"E503.trimOffspring");var subQ5=sQuery(id+"F25.wireOp",EDGE,"E261.trimOffspring");var subQ6=makeQuery(id+"F25.imprint","INTERSECT",VERTEX,{"derivedFrom":[subQ5,subQ0]});Q241=makeQuery(id+"F25.imprint","IMPRINT",FACE,{"disambiguationData":[TD([[makeQuery(id+"F25.imprint","IMPRINT",EDGE,{"disambiguationData":[TD([[subQ6,-1.0]])],"derivedFrom":subQ5}),1.0]])]});}
            var Q242;
            {var subQ0=sQuery(id+"F25.wireOp",EDGE,"E505.trimOffspring");var subQ1=sQuery(id+"F25.wireOp",EDGE,"E260.trimOffspring");var subQ2=makeQuery(id+"F25.imprint","INTERSECT",VERTEX,{"derivedFrom":[subQ1,subQ0]});Q242=makeQuery(id+"F25.imprint","IMPRINT",FACE,{"disambiguationData":[TD([[makeQuery(id+"F25.imprint","IMPRINT",EDGE,{"disambiguationData":[TD([[subQ2,1.0]])],"derivedFrom":subQ1}),1.0]])]});}
            var Q243;
            {var subQ0=sQuery(id+"F25.wireOp",EDGE,"E505.trimOffspring");var subQ1=sQuery(id+"F25.wireOp",EDGE,"E262.trimOffspring");var subQ2=makeQuery(id+"F25.imprint","INTERSECT",VERTEX,{"derivedFrom":[subQ1,subQ0]});Q243=makeQuery(id+"F25.imprint","IMPRINT",FACE,{"disambiguationData":[TD([[makeQuery(id+"F25.imprint","IMPRINT",EDGE,{"disambiguationData":[TD([[subQ2,-1.0]])],"derivedFrom":subQ1}),-1.0]])]});}
            var Q244;
            {var subQ0=sQuery(id+"F25.wireOp",EDGE,"E505.trimOffspring");var subQ1=sQuery(id+"F25.wireOp",EDGE,"E260.trimOffspring");var subQ2=makeQuery(id+"F25.imprint","INTERSECT",VERTEX,{"derivedFrom":[subQ1,subQ0]});Q244=makeQuery(id+"F25.imprint","IMPRINT",FACE,{"disambiguationData":[TD([[makeQuery(id+"F25.imprint","IMPRINT",EDGE,{"disambiguationData":[TD([[subQ2,-1.0]])],"derivedFrom":subQ1}),1.0]])]});}
            var Q245;
            {var subQ0=sQuery(id+"F25.wireOp",EDGE,"E511.trimOffspring");var subQ1=sQuery(id+"F25.wireOp",EDGE,"E262.trimOffspring");var subQ2=makeQuery(id+"F25.imprint","INTERSECT",VERTEX,{"derivedFrom":[subQ1,subQ0]});Q245=makeQuery(id+"F25.imprint","IMPRINT",FACE,{"disambiguationData":[TD([[makeQuery(id+"F25.imprint","IMPRINT",EDGE,{"disambiguationData":[TD([[subQ2,1.0]])],"derivedFrom":subQ1}),-1.0]])]});}
            var Q246;
            {var subQ0=sQuery(id+"F25.wireOp",EDGE,"E511.trimOffspring");var subQ1=sQuery(id+"F25.wireOp",EDGE,"E260.trimOffspring");var subQ2=makeQuery(id+"F25.imprint","INTERSECT",VERTEX,{"derivedFrom":[subQ1,subQ0]});Q246=makeQuery(id+"F25.imprint","IMPRINT",FACE,{"disambiguationData":[TD([[makeQuery(id+"F25.imprint","IMPRINT",EDGE,{"disambiguationData":[TD([[subQ2,1.0]])],"derivedFrom":subQ1}),1.0]])]});}
            var Q247;
            {var subQ0=sQuery(id+"F25.wireOp",EDGE,"E511.trimOffspring");var subQ1=sQuery(id+"F25.wireOp",EDGE,"E262.trimOffspring");var subQ2=makeQuery(id+"F25.imprint","INTERSECT",VERTEX,{"derivedFrom":[subQ1,subQ0]});Q247=makeQuery(id+"F25.imprint","IMPRINT",FACE,{"disambiguationData":[TD([[makeQuery(id+"F25.imprint","IMPRINT",EDGE,{"disambiguationData":[TD([[subQ2,-1.0]])],"derivedFrom":subQ1}),-1.0]])]});}
            var Q248;
            {var subQ0=sQuery(id+"F25.wireOp",EDGE,"E497.trimOffspring");var subQ1=sQuery(id+"F25.wireOp",EDGE,"E260.trimOffspring");var subQ2=makeQuery(id+"F25.imprint","INTERSECT",VERTEX,{"derivedFrom":[subQ1,subQ0]});Q248=makeQuery(id+"F25.imprint","IMPRINT",FACE,{"disambiguationData":[TD([[makeQuery(id+"F25.imprint","IMPRINT",EDGE,{"disambiguationData":[TD([[subQ2,1.0]])],"derivedFrom":subQ1}),1.0]])]});}
            var Q249;
            {var subQ0=sQuery(id+"F25.wireOp",EDGE,"E497.trimOffspring");var subQ1=sQuery(id+"F25.wireOp",EDGE,"E262.trimOffspring");var subQ2=makeQuery(id+"F25.imprint","INTERSECT",VERTEX,{"derivedFrom":[subQ1,subQ0]});Q249=makeQuery(id+"F25.imprint","IMPRINT",FACE,{"disambiguationData":[TD([[makeQuery(id+"F25.imprint","IMPRINT",EDGE,{"disambiguationData":[TD([[subQ2,-1.0]])],"derivedFrom":subQ1}),-1.0]])]});}
            var Q250;
            {var subQ0=sQuery(id+"F25.wireOp",EDGE,"E497.trimOffspring");var subQ1=sQuery(id+"F25.wireOp",EDGE,"E260.trimOffspring");var subQ2=makeQuery(id+"F25.imprint","INTERSECT",VERTEX,{"derivedFrom":[subQ1,subQ0]});Q250=makeQuery(id+"F25.imprint","IMPRINT",FACE,{"disambiguationData":[TD([[makeQuery(id+"F25.imprint","IMPRINT",EDGE,{"disambiguationData":[TD([[subQ2,-1.0]])],"derivedFrom":subQ1}),1.0]])]});}
            var Q251;
            {var subQ0=sQuery(id+"F25.wireOp",EDGE,"E496.trimOffspring");var subQ1=sQuery(id+"F25.wireOp",EDGE,"E262.trimOffspring");var subQ2=makeQuery(id+"F25.imprint","INTERSECT",VERTEX,{"derivedFrom":[subQ1,subQ0]});Q251=makeQuery(id+"F25.imprint","IMPRINT",FACE,{"disambiguationData":[TD([[makeQuery(id+"F25.imprint","IMPRINT",EDGE,{"disambiguationData":[TD([[subQ2,1.0]])],"derivedFrom":subQ1}),-1.0]])]});}
            var Q252;
            {var subQ0=sQuery(id+"F25.wireOp",EDGE,"E496.trimOffspring");var subQ1=sQuery(id+"F25.wireOp",EDGE,"E260.trimOffspring");var subQ2=makeQuery(id+"F25.imprint","INTERSECT",VERTEX,{"derivedFrom":[subQ1,subQ0]});Q252=makeQuery(id+"F25.imprint","IMPRINT",FACE,{"disambiguationData":[TD([[makeQuery(id+"F25.imprint","IMPRINT",EDGE,{"disambiguationData":[TD([[subQ2,1.0]])],"derivedFrom":subQ1}),1.0]])]});}
            var Q253;
            {var subQ0=sQuery(id+"F25.wireOp",EDGE,"E529.trimOffspring");var subQ1=sQuery(id+"F25.wireOp",EDGE,"E503.trimOffspring");var subQ2=makeQuery(id+"F25.imprint","INTERSECT",VERTEX,{"derivedFrom":[subQ1,subQ0]});Q253=makeQuery(id+"F25.imprint","IMPRINT",FACE,{"disambiguationData":[TD([[makeQuery(id+"F25.imprint","IMPRINT",EDGE,{"disambiguationData":[TD([[subQ2,-1.0]])],"derivedFrom":subQ1}),-1.0]])]});}
            var Q254;
            {var subQ0=sQuery(id+"F25.wireOp",EDGE,"E529.trimOffspring");var subQ1=sQuery(id+"F25.wireOp",EDGE,"E503.trimOffspring");var subQ2=makeQuery(id+"F25.imprint","INTERSECT",VERTEX,{"derivedFrom":[subQ1,subQ0]});Q254=makeQuery(id+"F25.imprint","IMPRINT",FACE,{"disambiguationData":[TD([[makeQuery(id+"F25.imprint","IMPRINT",EDGE,{"disambiguationData":[TD([[subQ2,-1.0]])],"derivedFrom":subQ1}),1.0]])]});}
            var Q255;
            {var subQ0=sQuery(id+"F25.wireOp",EDGE,"E529.trimOffspring");var subQ1=sQuery(id+"F25.wireOp",EDGE,"E507.trimOffspring");var subQ2=makeQuery(id+"F25.imprint","INTERSECT",VERTEX,{"derivedFrom":[subQ1,subQ0]});Q255=makeQuery(id+"F25.imprint","IMPRINT",FACE,{"disambiguationData":[TD([[makeQuery(id+"F25.imprint","IMPRINT",EDGE,{"disambiguationData":[TD([[subQ2,-1.0]])],"derivedFrom":subQ1}),1.0]])]});}
            var Q256;
            {var subQ0=sQuery(id+"F25.wireOp",EDGE,"E529.trimOffspring");var subQ1=sQuery(id+"F25.wireOp",EDGE,"E510.trimOffspring");var subQ2=makeQuery(id+"F25.imprint","INTERSECT",VERTEX,{"derivedFrom":[subQ1,subQ0]});Q256=makeQuery(id+"F25.imprint","IMPRINT",FACE,{"disambiguationData":[TD([[makeQuery(id+"F25.imprint","IMPRINT",EDGE,{"disambiguationData":[TD([[subQ2,-1.0]])],"derivedFrom":subQ1}),-1.0]])]});}
            var Q257;
            {var subQ0=sQuery(id+"F25.wireOp",EDGE,"E530.trimOffspring");var subQ1=sQuery(id+"F25.wireOp",EDGE,"E510.trimOffspring");var subQ2=makeQuery(id+"F25.imprint","INTERSECT",VERTEX,{"derivedFrom":[subQ1,subQ0]});Q257=makeQuery(id+"F25.imprint","IMPRINT",FACE,{"disambiguationData":[TD([[makeQuery(id+"F25.imprint","IMPRINT",EDGE,{"disambiguationData":[TD([[subQ2,-1.0]])],"derivedFrom":subQ1}),-1.0]])]});}
            var Q258;
            {var subQ0=sQuery(id+"F25.wireOp",EDGE,"E531.trimOffspring");var subQ1=sQuery(id+"F25.wireOp",EDGE,"E510.trimOffspring");var subQ2=makeQuery(id+"F25.imprint","INTERSECT",VERTEX,{"derivedFrom":[subQ1,subQ0]});Q258=makeQuery(id+"F25.imprint","IMPRINT",FACE,{"disambiguationData":[TD([[makeQuery(id+"F25.imprint","IMPRINT",EDGE,{"disambiguationData":[TD([[subQ2,-1.0]])],"derivedFrom":subQ1}),-1.0]])]});}
            var Q259;
            {var subQ0=sQuery(id+"F25.wireOp",EDGE,"E532.trimOffspring");var subQ1=sQuery(id+"F25.wireOp",EDGE,"E510.trimOffspring");var subQ2=makeQuery(id+"F25.imprint","INTERSECT",VERTEX,{"derivedFrom":[subQ1,subQ0]});Q259=makeQuery(id+"F25.imprint","IMPRINT",FACE,{"disambiguationData":[TD([[makeQuery(id+"F25.imprint","IMPRINT",EDGE,{"disambiguationData":[TD([[subQ2,-1.0]])],"derivedFrom":subQ1}),1.0]])]});}
            var Q260;
            {var subQ0=sQuery(id+"F25.wireOp",EDGE,"E527.trimOffspring");var subQ1=sQuery(id+"F25.wireOp",EDGE,"E510.trimOffspring");var subQ2=makeQuery(id+"F25.imprint","INTERSECT",VERTEX,{"derivedFrom":[subQ1,subQ0]});Q260=makeQuery(id+"F25.imprint","IMPRINT",FACE,{"disambiguationData":[TD([[makeQuery(id+"F25.imprint","IMPRINT",EDGE,{"disambiguationData":[TD([[subQ2,-1.0]])],"derivedFrom":subQ1}),1.0]])]});}
            var Q261;
            {var subQ0=sQuery(id+"F25.wireOp",EDGE,"E532.trimOffspring");var subQ1=sQuery(id+"F25.wireOp",EDGE,"E509.trimOffspring");var subQ2=makeQuery(id+"F25.imprint","INTERSECT",VERTEX,{"derivedFrom":[subQ1,subQ0]});Q261=makeQuery(id+"F25.imprint","IMPRINT",FACE,{"disambiguationData":[TD([[makeQuery(id+"F25.imprint","IMPRINT",EDGE,{"disambiguationData":[TD([[subQ2,-1.0]])],"derivedFrom":subQ1}),-1.0]])]});}
            var Q262;
            {var subQ0=sQuery(id+"F25.wireOp",EDGE,"E533.trimOffspring");var subQ1=sQuery(id+"F25.wireOp",EDGE,"E509.trimOffspring");var subQ2=makeQuery(id+"F25.imprint","INTERSECT",VERTEX,{"derivedFrom":[subQ1,subQ0]});Q262=makeQuery(id+"F25.imprint","IMPRINT",FACE,{"disambiguationData":[TD([[makeQuery(id+"F25.imprint","IMPRINT",EDGE,{"disambiguationData":[TD([[subQ2,1.0]])],"derivedFrom":subQ1}),-1.0]])]});}
            var Q263;
            {var subQ0=sQuery(id+"F25.wireOp",EDGE,"E533.trimOffspring");var subQ1=sQuery(id+"F25.wireOp",EDGE,"E509.trimOffspring");var subQ2=makeQuery(id+"F25.imprint","INTERSECT",VERTEX,{"derivedFrom":[subQ1,subQ0]});Q263=makeQuery(id+"F25.imprint","IMPRINT",FACE,{"disambiguationData":[TD([[makeQuery(id+"F25.imprint","IMPRINT",EDGE,{"disambiguationData":[TD([[subQ2,1.0]])],"derivedFrom":subQ1}),1.0]])]});}
            var Q264;
            {var subQ0=sQuery(id+"F25.wireOp",EDGE,"E532.trimOffspring");var subQ1=sQuery(id+"F25.wireOp",EDGE,"E509.trimOffspring");var subQ2=makeQuery(id+"F25.imprint","INTERSECT",VERTEX,{"derivedFrom":[subQ1,subQ0]});Q264=makeQuery(id+"F25.imprint","IMPRINT",FACE,{"disambiguationData":[TD([[makeQuery(id+"F25.imprint","IMPRINT",EDGE,{"disambiguationData":[TD([[subQ2,-1.0]])],"derivedFrom":subQ1}),1.0]])]});}
            var Q265;
            {var subQ0=sQuery(id+"F25.wireOp",EDGE,"E516.trimOffspring");var subQ1=sQuery(id+"F25.wireOp",EDGE,"E509.trimOffspring");var subQ2=makeQuery(id+"F25.imprint","INTERSECT",VERTEX,{"derivedFrom":[subQ1,subQ0]});Q265=makeQuery(id+"F25.imprint","IMPRINT",FACE,{"disambiguationData":[TD([[makeQuery(id+"F25.imprint","IMPRINT",EDGE,{"disambiguationData":[TD([[subQ2,-1.0]])],"derivedFrom":subQ1}),-1.0]])]});}
            var Q266;
            {var subQ3=sQuery(id+"F25.wireOp",EDGE,"E516.trimOffspring");var subQ5=sQuery(id+"F25.wireOp",EDGE,"E509.trimOffspring");var subQ6=makeQuery(id+"F25.imprint","INTERSECT",VERTEX,{"derivedFrom":[subQ5,subQ3]});Q266=makeQuery(id+"F25.imprint","IMPRINT",FACE,{"disambiguationData":[TD([[makeQuery(id+"F25.imprint","IMPRINT",EDGE,{"disambiguationData":[TD([[subQ6,-1.0]])],"derivedFrom":subQ5}),1.0]])]});}
            var Q267;
            {var subQ0=sQuery(id+"F25.wireOp",EDGE,"E514.trimOffspring");var subQ1=sQuery(id+"F25.wireOp",EDGE,"E508.trimOffspring");var subQ2=makeQuery(id+"F25.imprint","INTERSECT",VERTEX,{"derivedFrom":[subQ1,subQ0]});Q267=makeQuery(id+"F25.imprint","IMPRINT",FACE,{"disambiguationData":[TD([[makeQuery(id+"F25.imprint","IMPRINT",EDGE,{"disambiguationData":[TD([[subQ2,-1.0]])],"derivedFrom":subQ1}),-1.0]])]});}
            var Q268;
            {var subQ0=sQuery(id+"F25.wireOp",EDGE,"E514.trimOffspring");var subQ1=sQuery(id+"F25.wireOp",EDGE,"E509.trimOffspring");var subQ2=makeQuery(id+"F25.imprint","INTERSECT",VERTEX,{"derivedFrom":[subQ1,subQ0]});Q268=makeQuery(id+"F25.imprint","IMPRINT",FACE,{"disambiguationData":[TD([[makeQuery(id+"F25.imprint","IMPRINT",EDGE,{"disambiguationData":[TD([[subQ2,-1.0]])],"derivedFrom":subQ1}),-1.0]])]});}
            var Q269;
            {var subQ0=sQuery(id+"F25.wireOp",EDGE,"E515.trimOffspring");var subQ1=sQuery(id+"F25.wireOp",EDGE,"E509.trimOffspring");var subQ2=makeQuery(id+"F25.imprint","INTERSECT",VERTEX,{"derivedFrom":[subQ1,subQ0]});Q269=makeQuery(id+"F25.imprint","IMPRINT",FACE,{"disambiguationData":[TD([[makeQuery(id+"F25.imprint","IMPRINT",EDGE,{"disambiguationData":[TD([[subQ2,-1.0]])],"derivedFrom":subQ1}),-1.0]])]});}
            var Q270;
            {var subQ0=sQuery(id+"F25.wireOp",EDGE,"E515.trimOffspring");var subQ1=sQuery(id+"F25.wireOp",EDGE,"E508.trimOffspring");var subQ2=makeQuery(id+"F25.imprint","INTERSECT",VERTEX,{"derivedFrom":[subQ1,subQ0]});Q270=makeQuery(id+"F25.imprint","IMPRINT",FACE,{"disambiguationData":[TD([[makeQuery(id+"F25.imprint","IMPRINT",EDGE,{"disambiguationData":[TD([[subQ2,-1.0]])],"derivedFrom":subQ1}),-1.0]])]});}
            var Q271;
            {var subQ0=sQuery(id+"F25.wireOp",EDGE,"E263.trimOffspring");Q271=makeQuery(id+"F25.imprint","IMPRINT",FACE,{"disambiguationData":[TD([[makeQuery(id+"F25.imprint","IMPRINT",EDGE,{"derivedFrom":subQ0}),-1.0]])]});}
            var Q272;
            {var subQ0=sQuery(id+"F25.wireOp",EDGE,"E515.trimOffspring");var subQ1=sQuery(id+"F25.wireOp",EDGE,"E508.trimOffspring");var subQ2=makeQuery(id+"F25.imprint","INTERSECT",VERTEX,{"derivedFrom":[subQ1,subQ0]});Q272=makeQuery(id+"F25.imprint","IMPRINT",FACE,{"disambiguationData":[TD([[makeQuery(id+"F25.imprint","IMPRINT",EDGE,{"disambiguationData":[TD([[subQ2,-1.0]])],"derivedFrom":subQ1}),1.0]])]});}
            var Q273;
            {var subQ0=sQuery(id+"F25.wireOp",EDGE,"E263.trimOffspring");Q273=makeQuery(id+"F25.imprint","IMPRINT",FACE,{"disambiguationData":[TD([[makeQuery(id+"F25.imprint","IMPRINT",EDGE,{"derivedFrom":subQ0}),1.0]])]});}
            var Q274;
            {var subQ0=sQuery(id+"F25.wireOp",EDGE,"E514.trimOffspring");var subQ1=sQuery(id+"F25.wireOp",EDGE,"E264.trimOffspring");var subQ2=makeQuery(id+"F25.imprint","INTERSECT",VERTEX,{"derivedFrom":[subQ1,subQ0]});Q274=makeQuery(id+"F25.imprint","IMPRINT",FACE,{"disambiguationData":[TD([[makeQuery(id+"F25.imprint","IMPRINT",EDGE,{"disambiguationData":[TD([[subQ2,-1.0]])],"derivedFrom":subQ1}),-1.0]])]});}
            var Q275;
            {var subQ0=sQuery(id+"F25.wireOp",EDGE,"E515.trimOffspring");var subQ1=sQuery(id+"F25.wireOp",EDGE,"E266.trimOffspring");var subQ2=makeQuery(id+"F25.imprint","INTERSECT",VERTEX,{"derivedFrom":[subQ1,subQ0]});Q275=makeQuery(id+"F25.imprint","IMPRINT",FACE,{"disambiguationData":[TD([[makeQuery(id+"F25.imprint","IMPRINT",EDGE,{"disambiguationData":[TD([[subQ2,-1.0]])],"derivedFrom":subQ1}),-1.0]])]});}
            var Q276;
            {var subQ0=sQuery(id+"F25.wireOp",EDGE,"E515.trimOffspring");var subQ1=sQuery(id+"F25.wireOp",EDGE,"E264.trimOffspring");var subQ2=makeQuery(id+"F25.imprint","INTERSECT",VERTEX,{"derivedFrom":[subQ1,subQ0]});Q276=makeQuery(id+"F25.imprint","IMPRINT",FACE,{"disambiguationData":[TD([[makeQuery(id+"F25.imprint","IMPRINT",EDGE,{"disambiguationData":[TD([[subQ2,-1.0]])],"derivedFrom":subQ1}),-1.0]])]});}
            var Q277;
            {var subQ0=sQuery(id+"F25.wireOp",EDGE,"E516.trimOffspring");var subQ1=sQuery(id+"F25.wireOp",EDGE,"E266.trimOffspring");var subQ2=makeQuery(id+"F25.imprint","INTERSECT",VERTEX,{"derivedFrom":[subQ1,subQ0]});Q277=makeQuery(id+"F25.imprint","IMPRINT",FACE,{"disambiguationData":[TD([[makeQuery(id+"F25.imprint","IMPRINT",EDGE,{"disambiguationData":[TD([[subQ2,-1.0]])],"derivedFrom":subQ1}),-1.0]])]});}
            var Q278;
            {var subQ0=sQuery(id+"F25.wireOp",EDGE,"E516.trimOffspring");var subQ1=sQuery(id+"F25.wireOp",EDGE,"E264.trimOffspring");var subQ2=makeQuery(id+"F25.imprint","INTERSECT",VERTEX,{"derivedFrom":[subQ1,subQ0]});Q278=makeQuery(id+"F25.imprint","IMPRINT",FACE,{"disambiguationData":[TD([[makeQuery(id+"F25.imprint","IMPRINT",EDGE,{"disambiguationData":[TD([[subQ2,-1.0]])],"derivedFrom":subQ1}),-1.0]])]});}
            var Q279;
            {var subQ0=sQuery(id+"F25.wireOp",EDGE,"E532.trimOffspring");var subQ1=sQuery(id+"F25.wireOp",EDGE,"E266.trimOffspring");var subQ2=makeQuery(id+"F25.imprint","INTERSECT",VERTEX,{"derivedFrom":[subQ1,subQ0]});Q279=makeQuery(id+"F25.imprint","IMPRINT",FACE,{"disambiguationData":[TD([[makeQuery(id+"F25.imprint","IMPRINT",EDGE,{"disambiguationData":[TD([[subQ2,-1.0]])],"derivedFrom":subQ1}),-1.0]])]});}
            var Q280;
            {var subQ0=sQuery(id+"F25.wireOp",EDGE,"E532.trimOffspring");var subQ1=sQuery(id+"F25.wireOp",EDGE,"E264.trimOffspring");var subQ2=makeQuery(id+"F25.imprint","INTERSECT",VERTEX,{"derivedFrom":[subQ1,subQ0]});Q280=makeQuery(id+"F25.imprint","IMPRINT",FACE,{"disambiguationData":[TD([[makeQuery(id+"F25.imprint","IMPRINT",EDGE,{"disambiguationData":[TD([[subQ2,-1.0]])],"derivedFrom":subQ1}),-1.0]])]});}
            var Q281;
            {var subQ0=sQuery(id+"F25.wireOp",EDGE,"E527.trimOffspring");var subQ1=sQuery(id+"F25.wireOp",EDGE,"E266.trimOffspring");var subQ2=makeQuery(id+"F25.imprint","INTERSECT",VERTEX,{"derivedFrom":[subQ1,subQ0]});Q281=makeQuery(id+"F25.imprint","IMPRINT",FACE,{"disambiguationData":[TD([[makeQuery(id+"F25.imprint","IMPRINT",EDGE,{"disambiguationData":[TD([[subQ2,-1.0]])],"derivedFrom":subQ1}),-1.0]])]});}
            var Q282;
            {var subQ0=sQuery(id+"F25.wireOp",EDGE,"E527.trimOffspring");var subQ1=sQuery(id+"F25.wireOp",EDGE,"E264.trimOffspring");var subQ2=makeQuery(id+"F25.imprint","INTERSECT",VERTEX,{"derivedFrom":[subQ1,subQ0]});Q282=makeQuery(id+"F25.imprint","IMPRINT",FACE,{"disambiguationData":[TD([[makeQuery(id+"F25.imprint","IMPRINT",EDGE,{"disambiguationData":[TD([[subQ2,-1.0]])],"derivedFrom":subQ1}),-1.0]])]});}
            var Q283;
            {var subQ0=sQuery(id+"F25.wireOp",EDGE,"E533.trimOffspring");var subQ1=sQuery(id+"F25.wireOp",EDGE,"E266.trimOffspring");var subQ2=makeQuery(id+"F25.imprint","INTERSECT",VERTEX,{"derivedFrom":[subQ1,subQ0]});Q283=makeQuery(id+"F25.imprint","IMPRINT",FACE,{"disambiguationData":[TD([[makeQuery(id+"F25.imprint","IMPRINT",EDGE,{"disambiguationData":[TD([[subQ2,-1.0]])],"derivedFrom":subQ1}),-1.0]])]});}
            var Q284;
            {var subQ0=sQuery(id+"F25.wireOp",EDGE,"E533.trimOffspring");var subQ1=sQuery(id+"F25.wireOp",EDGE,"E264.trimOffspring");var subQ2=makeQuery(id+"F25.imprint","INTERSECT",VERTEX,{"derivedFrom":[subQ1,subQ0]});Q284=makeQuery(id+"F25.imprint","IMPRINT",FACE,{"disambiguationData":[TD([[makeQuery(id+"F25.imprint","IMPRINT",EDGE,{"disambiguationData":[TD([[subQ2,-1.0]])],"derivedFrom":subQ1}),-1.0]])]});}
            var Q285;
            {var subQ0=sQuery(id+"F25.wireOp",EDGE,"E538.trimOffspring");var subQ1=sQuery(id+"F25.wireOp",EDGE,"E266.trimOffspring");var subQ2=makeQuery(id+"F25.imprint","INTERSECT",VERTEX,{"derivedFrom":[subQ1,subQ0]});Q285=makeQuery(id+"F25.imprint","IMPRINT",FACE,{"disambiguationData":[TD([[makeQuery(id+"F25.imprint","IMPRINT",EDGE,{"disambiguationData":[TD([[subQ2,-1.0]])],"derivedFrom":subQ1}),-1.0]])]});}
            var Q286;
            {var subQ0=sQuery(id+"F25.wireOp",EDGE,"E542.trimOffspring");var subQ1=sQuery(id+"F25.wireOp",EDGE,"E266.trimOffspring");var subQ2=makeQuery(id+"F25.imprint","INTERSECT",VERTEX,{"derivedFrom":[subQ1,subQ0]});Q286=makeQuery(id+"F25.imprint","IMPRINT",FACE,{"disambiguationData":[TD([[makeQuery(id+"F25.imprint","IMPRINT",EDGE,{"disambiguationData":[TD([[subQ2,1.0]])],"derivedFrom":subQ1}),-1.0]])]});}
            var Q287;
            {var subQ0=sQuery(id+"F25.wireOp",EDGE,"E538.trimOffspring");var subQ1=sQuery(id+"F25.wireOp",EDGE,"E264.trimOffspring");var subQ2=makeQuery(id+"F25.imprint","INTERSECT",VERTEX,{"derivedFrom":[subQ1,subQ0]});Q287=makeQuery(id+"F25.imprint","IMPRINT",FACE,{"disambiguationData":[TD([[makeQuery(id+"F25.imprint","IMPRINT",EDGE,{"disambiguationData":[TD([[subQ2,-1.0]])],"derivedFrom":subQ1}),-1.0]])]});}
            var Q288;
            {var subQ0=sQuery(id+"F25.wireOp",EDGE,"E542.trimOffspring");var subQ1=sQuery(id+"F25.wireOp",EDGE,"E264.trimOffspring");var subQ2=makeQuery(id+"F25.imprint","INTERSECT",VERTEX,{"derivedFrom":[subQ1,subQ0]});Q288=makeQuery(id+"F25.imprint","IMPRINT",FACE,{"disambiguationData":[TD([[makeQuery(id+"F25.imprint","IMPRINT",EDGE,{"disambiguationData":[TD([[subQ2,1.0]])],"derivedFrom":subQ1}),-1.0]])]});}
            var Q289;
            {var subQ0=sQuery(id+"F25.wireOp",EDGE,"E243.top");Q289=makeQuery(id+"F25.imprint","IMPRINT",FACE,{"disambiguationData":[TD([[makeQuery(id+"F25.imprint","IMPRINT",EDGE,{"derivedFrom":subQ0}),1.0]])]});}
            var Q290;
            {var subQ0=sQuery(id+"F25.wireOp",EDGE,"E244.top");Q290=makeQuery(id+"F25.imprint","IMPRINT",FACE,{"disambiguationData":[TD([[makeQuery(id+"F25.imprint","IMPRINT",EDGE,{"derivedFrom":subQ0}),-1.0]])]});}
            var Q291;
            {var subQ0=sQuery(id+"F25.wireOp",EDGE,"E516.trimOffspring");var subQ5=sQuery(id+"F25.wireOp",EDGE,"E265.trimOffspring");var subQ6=makeQuery(id+"F25.imprint","INTERSECT",VERTEX,{"derivedFrom":[subQ5,subQ0]});Q291=makeQuery(id+"F25.imprint","IMPRINT",FACE,{"disambiguationData":[TD([[makeQuery(id+"F25.imprint","IMPRINT",EDGE,{"disambiguationData":[TD([[subQ6,-1.0]])],"derivedFrom":subQ5}),1.0]])]});}
            var Q292;
            {var subQ0=sQuery(id+"F25.wireOp",EDGE,"E243.top");Q292=makeQuery(id+"F25.imprint","IMPRINT",FACE,{"disambiguationData":[TD([[makeQuery(id+"F25.imprint","IMPRINT",EDGE,{"derivedFrom":subQ0}),-1.0]])]});}
            var Q293;
            {var subQ0=sQuery(id+"F25.wireOp",EDGE,"E244.top");Q293=makeQuery(id+"F25.imprint","IMPRINT",FACE,{"disambiguationData":[TD([[makeQuery(id+"F25.imprint","IMPRINT",EDGE,{"derivedFrom":subQ0}),1.0]])]});}
            var Q294;
            {var subQ0=sQuery(id+"F25.wireOp",EDGE,"E574.trimOffspring");var subQ5=sQuery(id+"F25.wireOp",EDGE,"E414.MirrorCS");var subQ6=makeQuery(id+"F25.imprint","INTERSECT",VERTEX,{"derivedFrom":[subQ5,subQ0]});Q294=makeQuery(id+"F25.imprint","IMPRINT",FACE,{"disambiguationData":[TD([[makeQuery(id+"F25.imprint","IMPRINT",EDGE,{"disambiguationData":[TD([[subQ6,-1.0]])],"derivedFrom":subQ5}),-1.0]])]});}
            var Q295;
            {var subQ0=sQuery(id+"F25.wireOp",EDGE,"E245.top");Q295=makeQuery(id+"F25.imprint","IMPRINT",FACE,{"disambiguationData":[TD([[makeQuery(id+"F25.imprint","IMPRINT",EDGE,{"derivedFrom":subQ0}),1.0]])]});}
            var Q296;
            {var subQ0=sQuery(id+"F25.wireOp",EDGE,"E245.top");Q296=makeQuery(id+"F25.imprint","IMPRINT",FACE,{"disambiguationData":[TD([[makeQuery(id+"F25.imprint","IMPRINT",EDGE,{"derivedFrom":subQ0}),-1.0]])]});}
            var Q297;
            {var subQ0=sQuery(id+"F25.wireOp",EDGE,"E246.top");Q297=makeQuery(id+"F25.imprint","IMPRINT",FACE,{"disambiguationData":[TD([[makeQuery(id+"F25.imprint","IMPRINT",EDGE,{"derivedFrom":subQ0}),-1.0]])]});}
            var Q298;
            {var subQ0=sQuery(id+"F25.wireOp",EDGE,"E246.top");Q298=makeQuery(id+"F25.imprint","IMPRINT",FACE,{"disambiguationData":[TD([[makeQuery(id+"F25.imprint","IMPRINT",EDGE,{"derivedFrom":subQ0}),1.0]])]});}
            var Q299;
            {var subQ0=sQuery(id+"F25.wireOp",EDGE,"E533.trimOffspring");var subQ5=sQuery(id+"F25.wireOp",EDGE,"E265.trimOffspring");var subQ6=makeQuery(id+"F25.imprint","INTERSECT",VERTEX,{"derivedFrom":[subQ5,subQ0]});Q299=makeQuery(id+"F25.imprint","IMPRINT",FACE,{"disambiguationData":[TD([[makeQuery(id+"F25.imprint","IMPRINT",EDGE,{"disambiguationData":[TD([[subQ6,-1.0]])],"derivedFrom":subQ5}),1.0]])]});}
            var Q300;
            {var subQ0=sQuery(id+"F25.wireOp",EDGE,"E581.trimOffspring");var subQ5=sQuery(id+"F25.wireOp",EDGE,"E414.MirrorCS");var subQ6=makeQuery(id+"F25.imprint","INTERSECT",VERTEX,{"derivedFrom":[subQ5,subQ0]});Q300=makeQuery(id+"F25.imprint","IMPRINT",FACE,{"disambiguationData":[TD([[makeQuery(id+"F25.imprint","IMPRINT",EDGE,{"disambiguationData":[TD([[subQ6,-1.0]])],"derivedFrom":subQ5}),-1.0]])]});}
            var Q301;
            {var subQ0=sQuery(id+"F25.wireOp",EDGE,"E247.top");Q301=makeQuery(id+"F25.imprint","IMPRINT",FACE,{"disambiguationData":[TD([[makeQuery(id+"F25.imprint","IMPRINT",EDGE,{"derivedFrom":subQ0}),-1.0]])]});}
            var Q302;
            {var subQ0=sQuery(id+"F25.wireOp",EDGE,"E247.top");Q302=makeQuery(id+"F25.imprint","IMPRINT",FACE,{"disambiguationData":[TD([[makeQuery(id+"F25.imprint","IMPRINT",EDGE,{"derivedFrom":subQ0}),1.0]])]});}
            var Q303;
            {var subQ5=sQuery(id+"F25.wireOp",EDGE,"E248.top");Q303=makeQuery(id+"F25.imprint","IMPRINT",FACE,{"disambiguationData":[TD([[makeQuery(id+"F25.imprint","IMPRINT",EDGE,{"derivedFrom":subQ5}),-1.0]])]});}
            var Q304;
            {var subQ0=sQuery(id+"F25.wireOp",EDGE,"E410.MirrorCS");Q304=makeQuery(id+"F25.imprint","IMPRINT",FACE,{"disambiguationData":[TD([[makeQuery(id+"F25.imprint","IMPRINT",EDGE,{"derivedFrom":subQ0}),1.0]])]});}
            var Q305;
            {var subQ0=sQuery(id+"F25.wireOp",EDGE,"E470.MirrorCS");var subQ1=sQuery(id+"F25.wireOp",EDGE,"E428.MirrorCS");var subQ2=makeQuery(id+"F25.imprint","INTERSECT",VERTEX,{"derivedFrom":[subQ1,subQ0]});Q305=makeQuery(id+"F25.imprint","IMPRINT",FACE,{"disambiguationData":[TD([[makeQuery(id+"F25.imprint","IMPRINT",EDGE,{"disambiguationData":[TD([[subQ2,-1.0]])],"derivedFrom":subQ1}),1.0]])]});}
            var Q306;
            {var subQ0=sQuery(id+"F25.wireOp",EDGE,"E452.MirrorCS");var subQ1=sQuery(id+"F25.wireOp",EDGE,"E428.MirrorCS");var subQ2=makeQuery(id+"F25.imprint","INTERSECT",VERTEX,{"derivedFrom":[subQ1,subQ0]});Q306=makeQuery(id+"F25.imprint","IMPRINT",FACE,{"disambiguationData":[TD([[makeQuery(id+"F25.imprint","IMPRINT",EDGE,{"disambiguationData":[TD([[subQ2,1.0]])],"derivedFrom":subQ1}),1.0]])]});}
            var Q307;
            {var subQ3=sQuery(id+"F25.wireOp",EDGE,"E471.MirrorCS");Q307=makeQuery(id+"F25.imprint","IMPRINT",FACE,{"disambiguationData":[TD([[makeQuery(id+"F25.imprint","IMPRINT",EDGE,{"derivedFrom":subQ3}),1.0]])]});}
            var Q308;
            {var subQ3=sQuery(id+"F25.wireOp",EDGE,"E471.MirrorCS");Q308=makeQuery(id+"F25.imprint","IMPRINT",FACE,{"disambiguationData":[TD([[makeQuery(id+"F25.imprint","IMPRINT",EDGE,{"derivedFrom":subQ3}),-1.0]])]});}
            var Q309;
            {var subQ0=sQuery(id+"F25.wireOp",EDGE,"E460.MirrorCS");var subQ1=sQuery(id+"F25.wireOp",EDGE,"E428.MirrorCS");var subQ2=makeQuery(id+"F25.imprint","INTERSECT",VERTEX,{"derivedFrom":[subQ1,subQ0]});Q309=makeQuery(id+"F25.imprint","IMPRINT",FACE,{"disambiguationData":[TD([[makeQuery(id+"F25.imprint","IMPRINT",EDGE,{"disambiguationData":[TD([[subQ2,1.0]])],"derivedFrom":subQ1}),1.0]])]});}
            var Q310;
            {var subQ0=sQuery(id+"F25.wireOp",EDGE,"E432.MirrorCS");Q310=makeQuery(id+"F25.imprint","IMPRINT",FACE,{"disambiguationData":[TD([[makeQuery(id+"F25.imprint","IMPRINT",EDGE,{"derivedFrom":subQ0}),-1.0]])]});}
            var Q311;
            {var subQ0=sQuery(id+"F25.wireOp",EDGE,"E453.MirrorCS");Q311=makeQuery(id+"F25.imprint","IMPRINT",FACE,{"disambiguationData":[TD([[makeQuery(id+"F25.imprint","IMPRINT",EDGE,{"derivedFrom":subQ0}),-1.0]])]});}
            var Q312;
            {var subQ0=sQuery(id+"F25.wireOp",EDGE,"E452.MirrorCS");var subQ1=sQuery(id+"F25.wireOp",EDGE,"E425.MirrorCS");var subQ2=makeQuery(id+"F25.imprint","INTERSECT",VERTEX,{"derivedFrom":[subQ1,subQ0]});Q312=makeQuery(id+"F25.imprint","IMPRINT",FACE,{"disambiguationData":[TD([[makeQuery(id+"F25.imprint","IMPRINT",EDGE,{"disambiguationData":[TD([[subQ2,1.0]])],"derivedFrom":subQ1}),-1.0]])]});}
            var Q313;
            {var subQ0=sQuery(id+"F25.wireOp",EDGE,"E430.MirrorCS");Q313=makeQuery(id+"F25.imprint","IMPRINT",FACE,{"disambiguationData":[TD([[makeQuery(id+"F25.imprint","IMPRINT",EDGE,{"derivedFrom":subQ0}),1.0]])]});}
            var Q314;
            {var subQ0=sQuery(id+"F25.wireOp",EDGE,"E430.MirrorCS");Q314=makeQuery(id+"F25.imprint","IMPRINT",FACE,{"disambiguationData":[TD([[makeQuery(id+"F25.imprint","IMPRINT",EDGE,{"derivedFrom":subQ0}),-1.0]])]});}
            var Q315;
            {var subQ0=sQuery(id+"F25.wireOp",EDGE,"E442.MirrorCS");var subQ1=sQuery(id+"F25.wireOp",EDGE,"E425.MirrorCS");var subQ2=makeQuery(id+"F25.imprint","INTERSECT",VERTEX,{"derivedFrom":[subQ1,subQ0]});Q315=makeQuery(id+"F25.imprint","IMPRINT",FACE,{"disambiguationData":[TD([[makeQuery(id+"F25.imprint","IMPRINT",EDGE,{"disambiguationData":[TD([[subQ2,-1.0]])],"derivedFrom":subQ1}),-1.0]])]});}
            var Q316;
            {var subQ0=sQuery(id+"F25.wireOp",EDGE,"E464.MirrorCS");var subQ1=sQuery(id+"F25.wireOp",EDGE,"E428.MirrorCS");var subQ2=makeQuery(id+"F25.imprint","INTERSECT",VERTEX,{"derivedFrom":[subQ1,subQ0]});Q316=makeQuery(id+"F25.imprint","IMPRINT",FACE,{"disambiguationData":[TD([[makeQuery(id+"F25.imprint","IMPRINT",EDGE,{"disambiguationData":[TD([[subQ2,1.0]])],"derivedFrom":subQ1}),1.0]])]});}
            var Q317;
            {var subQ0=sQuery(id+"F25.wireOp",EDGE,"E460.MirrorCS");var subQ1=sQuery(id+"F25.wireOp",EDGE,"E428.MirrorCS");var subQ2=makeQuery(id+"F25.imprint","INTERSECT",VERTEX,{"derivedFrom":[subQ1,subQ0]});Q317=makeQuery(id+"F25.imprint","IMPRINT",FACE,{"disambiguationData":[TD([[makeQuery(id+"F25.imprint","IMPRINT",EDGE,{"disambiguationData":[TD([[subQ2,-1.0]])],"derivedFrom":subQ1}),1.0]])]});}
            var Q318;
            {var subQ0=sQuery(id+"F25.wireOp",EDGE,"E460.MirrorCS");var subQ1=sQuery(id+"F25.wireOp",EDGE,"E425.MirrorCS");var subQ2=makeQuery(id+"F25.imprint","INTERSECT",VERTEX,{"derivedFrom":[subQ1,subQ0]});Q318=makeQuery(id+"F25.imprint","IMPRINT",FACE,{"disambiguationData":[TD([[makeQuery(id+"F25.imprint","IMPRINT",EDGE,{"disambiguationData":[TD([[subQ2,-1.0]])],"derivedFrom":subQ1}),-1.0]])]});}
            var Q319;
            {var subQ0=sQuery(id+"F25.wireOp",EDGE,"E464.MirrorCS");var subQ1=sQuery(id+"F25.wireOp",EDGE,"E425.MirrorCS");var subQ2=makeQuery(id+"F25.imprint","INTERSECT",VERTEX,{"derivedFrom":[subQ1,subQ0]});Q319=makeQuery(id+"F25.imprint","IMPRINT",FACE,{"disambiguationData":[TD([[makeQuery(id+"F25.imprint","IMPRINT",EDGE,{"disambiguationData":[TD([[subQ2,1.0]])],"derivedFrom":subQ1}),-1.0]])]});}
            var Q320;
            {var subQ0=sQuery(id+"F25.wireOp",EDGE,"E555.trimOffspring");var subQ5=sQuery(id+"F25.wireOp",EDGE,"E439.MirrorCS");var subQ6=makeQuery(id+"F25.imprint","INTERSECT",VERTEX,{"derivedFrom":[subQ5,subQ0]});Q320=makeQuery(id+"F25.imprint","IMPRINT",FACE,{"disambiguationData":[TD([[makeQuery(id+"F25.imprint","IMPRINT",EDGE,{"disambiguationData":[TD([[subQ6,-1.0]])],"derivedFrom":subQ5}),-1.0]])]});}
            var Q321;
            {var subQ0=sQuery(id+"F25.wireOp",EDGE,"E555.trimOffspring");var subQ1=sQuery(id+"F25.wireOp",EDGE,"E429.MirrorCS");var subQ2=makeQuery(id+"F25.imprint","INTERSECT",VERTEX,{"derivedFrom":[subQ1,subQ0]});Q321=makeQuery(id+"F25.imprint","IMPRINT",FACE,{"disambiguationData":[TD([[makeQuery(id+"F25.imprint","IMPRINT",EDGE,{"disambiguationData":[TD([[subQ2,-1.0]])],"derivedFrom":subQ1}),-1.0]])]});}
            var Q322;
            {var subQ0=sQuery(id+"F25.wireOp",EDGE,"E555.trimOffspring");var subQ1=sQuery(id+"F25.wireOp",EDGE,"E429.MirrorCS");var subQ2=makeQuery(id+"F25.imprint","INTERSECT",VERTEX,{"derivedFrom":[subQ1,subQ0]});Q322=makeQuery(id+"F25.imprint","IMPRINT",FACE,{"disambiguationData":[TD([[makeQuery(id+"F25.imprint","IMPRINT",EDGE,{"disambiguationData":[TD([[subQ2,-1.0]])],"derivedFrom":subQ1}),1.0]])]});}
            var Q323;
            {var subQ0=sQuery(id+"F25.wireOp",EDGE,"E552.trimOffspring");var subQ5=sQuery(id+"F25.wireOp",EDGE,"E439.MirrorCS");var subQ6=makeQuery(id+"F25.imprint","INTERSECT",VERTEX,{"derivedFrom":[subQ5,subQ0]});Q323=makeQuery(id+"F25.imprint","IMPRINT",FACE,{"disambiguationData":[TD([[makeQuery(id+"F25.imprint","IMPRINT",EDGE,{"disambiguationData":[TD([[subQ6,-1.0]])],"derivedFrom":subQ5}),-1.0]])]});}
            var Q324;
            {var subQ0=sQuery(id+"F25.wireOp",EDGE,"E554.trimOffspring");var subQ1=sQuery(id+"F25.wireOp",EDGE,"E429.MirrorCS");var subQ2=makeQuery(id+"F25.imprint","INTERSECT",VERTEX,{"derivedFrom":[subQ1,subQ0]});Q324=makeQuery(id+"F25.imprint","IMPRINT",FACE,{"disambiguationData":[TD([[makeQuery(id+"F25.imprint","IMPRINT",EDGE,{"disambiguationData":[TD([[subQ2,1.0]])],"derivedFrom":subQ1}),-1.0]])]});}
            var Q325;
            {var subQ0=sQuery(id+"F25.wireOp",EDGE,"E545.trimOffspring");var subQ1=sQuery(id+"F25.wireOp",EDGE,"E424.MirrorCS");var subQ2=makeQuery(id+"F25.imprint","INTERSECT",VERTEX,{"derivedFrom":[subQ1,subQ0]});Q325=makeQuery(id+"F25.imprint","IMPRINT",FACE,{"disambiguationData":[TD([[makeQuery(id+"F25.imprint","IMPRINT",EDGE,{"disambiguationData":[TD([[subQ2,1.0]])],"derivedFrom":subQ1}),1.0]])]});}
            var Q326;
            {var subQ0=sQuery(id+"F25.wireOp",EDGE,"E545.trimOffspring");var subQ1=sQuery(id+"F25.wireOp",EDGE,"E429.MirrorCS");var subQ2=makeQuery(id+"F25.imprint","INTERSECT",VERTEX,{"derivedFrom":[subQ1,subQ0]});Q326=makeQuery(id+"F25.imprint","IMPRINT",FACE,{"disambiguationData":[TD([[makeQuery(id+"F25.imprint","IMPRINT",EDGE,{"disambiguationData":[TD([[subQ2,1.0]])],"derivedFrom":subQ1}),-1.0]])]});}
            var Q327;
            {var subQ0=sQuery(id+"F25.wireOp",EDGE,"E545.trimOffspring");var subQ1=sQuery(id+"F25.wireOp",EDGE,"E424.MirrorCS");var subQ2=makeQuery(id+"F25.imprint","INTERSECT",VERTEX,{"derivedFrom":[subQ1,subQ0]});Q327=makeQuery(id+"F25.imprint","IMPRINT",FACE,{"disambiguationData":[TD([[makeQuery(id+"F25.imprint","IMPRINT",EDGE,{"disambiguationData":[TD([[subQ2,-1.0]])],"derivedFrom":subQ1}),1.0]])]});}
            var Q328;
            {var subQ0=sQuery(id+"F25.wireOp",EDGE,"E545.trimOffspring");var subQ1=sQuery(id+"F25.wireOp",EDGE,"E429.MirrorCS");var subQ2=makeQuery(id+"F25.imprint","INTERSECT",VERTEX,{"derivedFrom":[subQ1,subQ0]});Q328=makeQuery(id+"F25.imprint","IMPRINT",FACE,{"disambiguationData":[TD([[makeQuery(id+"F25.imprint","IMPRINT",EDGE,{"disambiguationData":[TD([[subQ2,-1.0]])],"derivedFrom":subQ1}),-1.0]])]});}
            var Q329;
            {var subQ0=sQuery(id+"F25.wireOp",EDGE,"E553.trimOffspring");var subQ1=sQuery(id+"F25.wireOp",EDGE,"E424.MirrorCS");var subQ2=makeQuery(id+"F25.imprint","INTERSECT",VERTEX,{"derivedFrom":[subQ1,subQ0]});Q329=makeQuery(id+"F25.imprint","IMPRINT",FACE,{"disambiguationData":[TD([[makeQuery(id+"F25.imprint","IMPRINT",EDGE,{"disambiguationData":[TD([[subQ2,-1.0]])],"derivedFrom":subQ1}),1.0]])]});}
            var Q330;
            {var subQ3=sQuery(id+"F25.wireOp",EDGE,"E553.trimOffspring");var subQ5=sQuery(id+"F25.wireOp",EDGE,"E439.MirrorCS");var subQ6=makeQuery(id+"F25.imprint","INTERSECT",VERTEX,{"derivedFrom":[subQ5,subQ3]});Q330=makeQuery(id+"F25.imprint","IMPRINT",FACE,{"disambiguationData":[TD([[makeQuery(id+"F25.imprint","IMPRINT",EDGE,{"disambiguationData":[TD([[subQ6,-1.0]])],"derivedFrom":subQ5}),1.0]])]});}
            var Q331;
            {var subQ0=sQuery(id+"F25.wireOp",EDGE,"E460.MirrorCS");var subQ1=sQuery(id+"F25.wireOp",EDGE,"E424.MirrorCS");var subQ2=makeQuery(id+"F25.imprint","INTERSECT",VERTEX,{"derivedFrom":[subQ1,subQ0]});Q331=makeQuery(id+"F25.imprint","IMPRINT",FACE,{"disambiguationData":[TD([[makeQuery(id+"F25.imprint","IMPRINT",EDGE,{"disambiguationData":[TD([[subQ2,-1.0]])],"derivedFrom":subQ1}),1.0]])]});}
            var Q332;
            {var subQ3=sQuery(id+"F25.wireOp",EDGE,"E460.MirrorCS");var subQ5=sQuery(id+"F25.wireOp",EDGE,"E439.MirrorCS");var subQ6=makeQuery(id+"F25.imprint","INTERSECT",VERTEX,{"derivedFrom":[subQ5,subQ3]});Q332=makeQuery(id+"F25.imprint","IMPRINT",FACE,{"disambiguationData":[TD([[makeQuery(id+"F25.imprint","IMPRINT",EDGE,{"disambiguationData":[TD([[subQ6,-1.0]])],"derivedFrom":subQ5}),1.0]])]});}
            var Q333;
            {var subQ0=sQuery(id+"F25.wireOp",EDGE,"E464.MirrorCS");var subQ1=sQuery(id+"F25.wireOp",EDGE,"E424.MirrorCS");var subQ2=makeQuery(id+"F25.imprint","INTERSECT",VERTEX,{"derivedFrom":[subQ1,subQ0]});Q333=makeQuery(id+"F25.imprint","IMPRINT",FACE,{"disambiguationData":[TD([[makeQuery(id+"F25.imprint","IMPRINT",EDGE,{"disambiguationData":[TD([[subQ2,1.0]])],"derivedFrom":subQ1}),1.0]])]});}
            var Q334;
            {var subQ3=sQuery(id+"F25.wireOp",EDGE,"E464.MirrorCS");var subQ5=sQuery(id+"F25.wireOp",EDGE,"E439.MirrorCS");var subQ6=makeQuery(id+"F25.imprint","INTERSECT",VERTEX,{"derivedFrom":[subQ5,subQ3]});Q334=makeQuery(id+"F25.imprint","IMPRINT",FACE,{"disambiguationData":[TD([[makeQuery(id+"F25.imprint","IMPRINT",EDGE,{"disambiguationData":[TD([[subQ6,1.0]])],"derivedFrom":subQ5}),1.0]])]});}
            var Q335;
            {var subQ0=sQuery(id+"F25.wireOp",EDGE,"E555.trimOffspring");var subQ1=sQuery(id+"F25.wireOp",EDGE,"E445.MirrorCS");var subQ2=makeQuery(id+"F25.imprint","INTERSECT",VERTEX,{"derivedFrom":[subQ1,subQ0]});Q335=makeQuery(id+"F25.imprint","IMPRINT",FACE,{"disambiguationData":[TD([[makeQuery(id+"F25.imprint","IMPRINT",EDGE,{"disambiguationData":[TD([[subQ2,-1.0]])],"derivedFrom":subQ1}),1.0]])]});}
            var Q336;
            {var subQ0=sQuery(id+"F25.wireOp",EDGE,"E564.trimOffspring");var subQ1=sQuery(id+"F25.wireOp",EDGE,"E445.MirrorCS");var subQ2=makeQuery(id+"F25.imprint","INTERSECT",VERTEX,{"derivedFrom":[subQ1,subQ0]});Q336=makeQuery(id+"F25.imprint","IMPRINT",FACE,{"disambiguationData":[TD([[makeQuery(id+"F25.imprint","IMPRINT",EDGE,{"disambiguationData":[TD([[subQ2,1.0]])],"derivedFrom":subQ1}),1.0]])]});}
            var Q337;
            {var subQ0=sQuery(id+"F25.wireOp",EDGE,"E547.trimOffspring");var subQ1=sQuery(id+"F25.wireOp",EDGE,"E445.MirrorCS");var subQ2=makeQuery(id+"F25.imprint","INTERSECT",VERTEX,{"derivedFrom":[subQ1,subQ0]});Q337=makeQuery(id+"F25.imprint","IMPRINT",FACE,{"disambiguationData":[TD([[makeQuery(id+"F25.imprint","IMPRINT",EDGE,{"disambiguationData":[TD([[subQ2,1.0]])],"derivedFrom":subQ1}),1.0]])]});}
            var Q338;
            {var subQ3=sQuery(id+"F25.wireOp",EDGE,"E563.trimOffspring");Q338=makeQuery(id+"F25.imprint","IMPRINT",FACE,{"disambiguationData":[TD([[makeQuery(id+"F25.imprint","IMPRINT",EDGE,{"derivedFrom":subQ3}),1.0]])]});}
            var Q339;
            {var subQ3=sQuery(id+"F25.wireOp",EDGE,"E563.trimOffspring");Q339=makeQuery(id+"F25.imprint","IMPRINT",FACE,{"disambiguationData":[TD([[makeQuery(id+"F25.imprint","IMPRINT",EDGE,{"derivedFrom":subQ3}),-1.0]])]});}
            var Q340;
            {var subQ3=sQuery(id+"F25.wireOp",EDGE,"E560.trimOffspring");var subQ5=sQuery(id+"F25.wireOp",EDGE,"E434.MirrorCS");var subQ6=makeQuery(id+"F25.imprint","INTERSECT",VERTEX,{"derivedFrom":[subQ5,subQ3]});Q340=makeQuery(id+"F25.imprint","IMPRINT",FACE,{"disambiguationData":[TD([[makeQuery(id+"F25.imprint","IMPRINT",EDGE,{"disambiguationData":[TD([[subQ6,-1.0]])],"derivedFrom":subQ5}),-1.0]])]});}
            var Q341;
            {var subQ3=sQuery(id+"F25.wireOp",EDGE,"E559.trimOffspring");var subQ5=sQuery(id+"F25.wireOp",EDGE,"E434.MirrorCS");var subQ6=makeQuery(id+"F25.imprint","INTERSECT",VERTEX,{"derivedFrom":[subQ5,subQ3]});Q341=makeQuery(id+"F25.imprint","IMPRINT",FACE,{"disambiguationData":[TD([[makeQuery(id+"F25.imprint","IMPRINT",EDGE,{"disambiguationData":[TD([[subQ6,1.0]])],"derivedFrom":subQ5}),-1.0]])]});}
            var Q342;
            {var subQ0=sQuery(id+"F25.wireOp",EDGE,"E559.trimOffspring");var subQ1=sQuery(id+"F25.wireOp",EDGE,"E443.MirrorCS");var subQ2=makeQuery(id+"F25.imprint","INTERSECT",VERTEX,{"derivedFrom":[subQ1,subQ0]});Q342=makeQuery(id+"F25.imprint","IMPRINT",FACE,{"disambiguationData":[TD([[makeQuery(id+"F25.imprint","IMPRINT",EDGE,{"disambiguationData":[TD([[subQ2,1.0]])],"derivedFrom":subQ1}),-1.0]])]});}
            var Q343;
            {var subQ0=sQuery(id+"F25.wireOp",EDGE,"E559.trimOffspring");var subQ1=sQuery(id+"F25.wireOp",EDGE,"E443.MirrorCS");var subQ2=makeQuery(id+"F25.imprint","INTERSECT",VERTEX,{"derivedFrom":[subQ1,subQ0]});Q343=makeQuery(id+"F25.imprint","IMPRINT",FACE,{"disambiguationData":[TD([[makeQuery(id+"F25.imprint","IMPRINT",EDGE,{"disambiguationData":[TD([[subQ2,1.0]])],"derivedFrom":subQ1}),1.0]])]});}
            var Q344;
            {var subQ0=sQuery(id+"F25.wireOp",EDGE,"E571.trimOffspring");var subQ1=sQuery(id+"F25.wireOp",EDGE,"E559.trimOffspring");var subQ2=makeQuery(id+"F25.imprint","INTERSECT",VERTEX,{"derivedFrom":[subQ1,subQ0]});Q344=makeQuery(id+"F25.imprint","IMPRINT",FACE,{"disambiguationData":[TD([[makeQuery(id+"F25.imprint","IMPRINT",EDGE,{"disambiguationData":[TD([[subQ2,-1.0]])],"derivedFrom":subQ1}),1.0]])]});}
            var Q345;
            {var subQ0=sQuery(id+"F25.wireOp",EDGE,"E583.trimOffspring");var subQ1=sQuery(id+"F25.wireOp",EDGE,"E559.trimOffspring");var subQ2=makeQuery(id+"F25.imprint","INTERSECT",VERTEX,{"derivedFrom":[subQ1,subQ0]});Q345=makeQuery(id+"F25.imprint","IMPRINT",FACE,{"disambiguationData":[TD([[makeQuery(id+"F25.imprint","IMPRINT",EDGE,{"disambiguationData":[TD([[subQ2,1.0]])],"derivedFrom":subQ1}),1.0]])]});}
            var Q346;
            {var subQ0=sQuery(id+"F25.wireOp",EDGE,"E583.trimOffspring");var subQ1=sQuery(id+"F25.wireOp",EDGE,"E560.trimOffspring");var subQ2=makeQuery(id+"F25.imprint","INTERSECT",VERTEX,{"derivedFrom":[subQ1,subQ0]});Q346=makeQuery(id+"F25.imprint","IMPRINT",FACE,{"disambiguationData":[TD([[makeQuery(id+"F25.imprint","IMPRINT",EDGE,{"disambiguationData":[TD([[subQ2,1.0]])],"derivedFrom":subQ1}),-1.0]])]});}
            var Q347;
            {var subQ0=sQuery(id+"F25.wireOp",EDGE,"E583.trimOffspring");var subQ1=sQuery(id+"F25.wireOp",EDGE,"E560.trimOffspring");var subQ2=makeQuery(id+"F25.imprint","INTERSECT",VERTEX,{"derivedFrom":[subQ1,subQ0]});Q347=makeQuery(id+"F25.imprint","IMPRINT",FACE,{"disambiguationData":[TD([[makeQuery(id+"F25.imprint","IMPRINT",EDGE,{"disambiguationData":[TD([[subQ2,1.0]])],"derivedFrom":subQ1}),1.0]])]});}
            var Q348;
            {var subQ0=sQuery(id+"F25.wireOp",EDGE,"E572.trimOffspring");var subQ1=sQuery(id+"F25.wireOp",EDGE,"E568.trimOffspring");var subQ2=makeQuery(id+"F25.imprint","INTERSECT",VERTEX,{"derivedFrom":[subQ1,subQ0]});Q348=makeQuery(id+"F25.imprint","IMPRINT",FACE,{"disambiguationData":[TD([[makeQuery(id+"F25.imprint","IMPRINT",EDGE,{"disambiguationData":[TD([[subQ2,-1.0]])],"derivedFrom":subQ1}),1.0]])]});}
            var Q349;
            {var subQ0=sQuery(id+"F25.wireOp",EDGE,"E583.trimOffspring");var subQ1=sQuery(id+"F25.wireOp",EDGE,"E568.trimOffspring");var subQ2=makeQuery(id+"F25.imprint","INTERSECT",VERTEX,{"derivedFrom":[subQ1,subQ0]});Q349=makeQuery(id+"F25.imprint","IMPRINT",FACE,{"disambiguationData":[TD([[makeQuery(id+"F25.imprint","IMPRINT",EDGE,{"disambiguationData":[TD([[subQ2,-1.0]])],"derivedFrom":subQ1}),1.0]])]});}
            var Q350;
            {var subQ0=sQuery(id+"F25.wireOp",EDGE,"E596.trimOffspring");var subQ1=sQuery(id+"F25.wireOp",EDGE,"E568.trimOffspring");var subQ2=makeQuery(id+"F25.imprint","INTERSECT",VERTEX,{"derivedFrom":[subQ1,subQ0]});Q350=makeQuery(id+"F25.imprint","IMPRINT",FACE,{"disambiguationData":[TD([[makeQuery(id+"F25.imprint","IMPRINT",EDGE,{"disambiguationData":[TD([[subQ2,-1.0]])],"derivedFrom":subQ1}),1.0]])]});}
            var Q351;
            {var subQ0=sQuery(id+"F25.wireOp",EDGE,"E598.trimOffspring");var subQ1=sQuery(id+"F25.wireOp",EDGE,"E568.trimOffspring");var subQ2=makeQuery(id+"F25.imprint","INTERSECT",VERTEX,{"derivedFrom":[subQ1,subQ0]});Q351=makeQuery(id+"F25.imprint","IMPRINT",FACE,{"disambiguationData":[TD([[makeQuery(id+"F25.imprint","IMPRINT",EDGE,{"disambiguationData":[TD([[subQ2,-1.0]])],"derivedFrom":subQ1}),1.0]])]});}
            var Q352;
            {var subQ1=sQuery(id+"F25.wireOp",EDGE,"E481.trimOffspring");var subQ3=sQuery(id+"F25.wireOp",EDGE,"E567.trimOffspring");var subQ4=makeQuery(id+"F25.imprint","INTERSECT",VERTEX,{"derivedFrom":[subQ1,subQ3]});Q352=makeQuery(id+"F25.imprint","IMPRINT",FACE,{"disambiguationData":[TD([[makeQuery(id+"F25.imprint","IMPRINT",EDGE,{"disambiguationData":[TD([[subQ4,1.0]])],"derivedFrom":subQ3}),-1.0]])]});}
            var Q353;
            {var subQ0=sQuery(id+"F25.wireOp",EDGE,"E608.trimOffspring");var subQ1=sQuery(id+"F25.wireOp",EDGE,"E423.MirrorCS");var subQ2=makeQuery(id+"F25.imprint","INTERSECT",VERTEX,{"derivedFrom":[subQ1,subQ0]});Q353=makeQuery(id+"F25.imprint","IMPRINT",FACE,{"disambiguationData":[TD([[makeQuery(id+"F25.imprint","IMPRINT",EDGE,{"disambiguationData":[TD([[subQ2,-1.0]])],"derivedFrom":subQ1}),-1.0]])]});}
            var Q354;
            {var subQ0=sQuery(id+"F25.wireOp",EDGE,"E608.trimOffspring");var subQ1=sQuery(id+"F25.wireOp",EDGE,"E483.trimOffspring");var subQ2=makeQuery(id+"F25.imprint","INTERSECT",VERTEX,{"derivedFrom":[subQ1,subQ0]});Q354=makeQuery(id+"F25.imprint","IMPRINT",FACE,{"disambiguationData":[TD([[makeQuery(id+"F25.imprint","IMPRINT",EDGE,{"disambiguationData":[TD([[subQ2,-1.0]])],"derivedFrom":subQ1}),-1.0]])]});}
            var Q355;
            {var subQ3=sQuery(id+"F25.wireOp",EDGE,"E599.trimOffspring");var subQ5=sQuery(id+"F25.wireOp",EDGE,"E484.trimOffspring");var subQ6=makeQuery(id+"F25.imprint","INTERSECT",VERTEX,{"derivedFrom":[subQ5,subQ3]});Q355=makeQuery(id+"F25.imprint","IMPRINT",FACE,{"disambiguationData":[TD([[makeQuery(id+"F25.imprint","IMPRINT",EDGE,{"disambiguationData":[TD([[subQ6,-1.0]])],"derivedFrom":subQ5}),1.0]])]});}
            var Q356;
            {var subQ0=sQuery(id+"F25.wireOp",EDGE,"E570.trimOffspring");var subQ5=sQuery(id+"F25.wireOp",EDGE,"E484.trimOffspring");var subQ6=makeQuery(id+"F25.imprint","INTERSECT",VERTEX,{"derivedFrom":[subQ5,subQ0]});Q356=makeQuery(id+"F25.imprint","IMPRINT",FACE,{"disambiguationData":[TD([[makeQuery(id+"F25.imprint","IMPRINT",EDGE,{"disambiguationData":[TD([[subQ6,-1.0]])],"derivedFrom":subQ5}),1.0]])]});}
            var Q357;
            {var subQ0=sQuery(id+"F25.wireOp",EDGE,"E565.trimOffspring");var subQ1=sQuery(id+"F25.wireOp",EDGE,"E483.trimOffspring");var subQ2=makeQuery(id+"F25.imprint","INTERSECT",VERTEX,{"derivedFrom":[subQ1,subQ0]});Q357=makeQuery(id+"F25.imprint","IMPRINT",FACE,{"disambiguationData":[TD([[makeQuery(id+"F25.imprint","IMPRINT",EDGE,{"disambiguationData":[TD([[subQ2,1.0]])],"derivedFrom":subQ1}),-1.0]])]});}
            var Q358;
            {var subQ0=sQuery(id+"F25.wireOp",EDGE,"E565.trimOffspring");var subQ5=sQuery(id+"F25.wireOp",EDGE,"E484.trimOffspring");var subQ6=makeQuery(id+"F25.imprint","INTERSECT",VERTEX,{"derivedFrom":[subQ5,subQ0]});Q358=makeQuery(id+"F25.imprint","IMPRINT",FACE,{"disambiguationData":[TD([[makeQuery(id+"F25.imprint","IMPRINT",EDGE,{"disambiguationData":[TD([[subQ6,1.0]])],"derivedFrom":subQ5}),-1.0]])]});}
            var Q359;
            {var subQ0=sQuery(id+"F25.wireOp",EDGE,"E570.trimOffspring");var subQ5=sQuery(id+"F25.wireOp",EDGE,"E484.trimOffspring");var subQ6=makeQuery(id+"F25.imprint","INTERSECT",VERTEX,{"derivedFrom":[subQ5,subQ0]});Q359=makeQuery(id+"F25.imprint","IMPRINT",FACE,{"disambiguationData":[TD([[makeQuery(id+"F25.imprint","IMPRINT",EDGE,{"disambiguationData":[TD([[subQ6,-1.0]])],"derivedFrom":subQ5}),1.0]])]});}
            var Q360;
            {var subQ0=sQuery(id+"F25.wireOp",EDGE,"E565.trimOffspring");var subQ1=sQuery(id+"F25.wireOp",EDGE,"E483.trimOffspring");var subQ2=makeQuery(id+"F25.imprint","INTERSECT",VERTEX,{"derivedFrom":[subQ1,subQ0]});Q360=makeQuery(id+"F25.imprint","IMPRINT",FACE,{"disambiguationData":[TD([[makeQuery(id+"F25.imprint","IMPRINT",EDGE,{"disambiguationData":[TD([[subQ2,1.0]])],"derivedFrom":subQ1}),-1.0]])]});}
            var Q361;
            {var subQ0=sQuery(id+"F25.wireOp",EDGE,"E598.trimOffspring");var subQ1=sQuery(id+"F25.wireOp",EDGE,"E568.trimOffspring");var subQ2=makeQuery(id+"F25.imprint","INTERSECT",VERTEX,{"derivedFrom":[subQ1,subQ0]});Q361=makeQuery(id+"F25.imprint","IMPRINT",FACE,{"disambiguationData":[TD([[makeQuery(id+"F25.imprint","IMPRINT",EDGE,{"disambiguationData":[TD([[subQ2,-1.0]])],"derivedFrom":subQ1}),-1.0]])]});}
            var Q362;
            {var subQ0=sQuery(id+"F25.wireOp",EDGE,"E596.trimOffspring");var subQ1=sQuery(id+"F25.wireOp",EDGE,"E568.trimOffspring");var subQ2=makeQuery(id+"F25.imprint","INTERSECT",VERTEX,{"derivedFrom":[subQ1,subQ0]});Q362=makeQuery(id+"F25.imprint","IMPRINT",FACE,{"disambiguationData":[TD([[makeQuery(id+"F25.imprint","IMPRINT",EDGE,{"disambiguationData":[TD([[subQ2,-1.0]])],"derivedFrom":subQ1}),-1.0]])]});}
            var Q363;
            {var subQ0=sQuery(id+"F25.wireOp",EDGE,"E577.trimOffspring");var subQ1=sQuery(id+"F25.wireOp",EDGE,"E454.MirrorCS");var subQ2=makeQuery(id+"F25.imprint","INTERSECT",VERTEX,{"derivedFrom":[subQ1,subQ0]});Q363=makeQuery(id+"F25.imprint","IMPRINT",FACE,{"disambiguationData":[TD([[makeQuery(id+"F25.imprint","IMPRINT",EDGE,{"disambiguationData":[TD([[subQ2,-1.0]])],"derivedFrom":subQ1}),1.0]])]});}
            var Q364;
            {var subQ0=sQuery(id+"F25.wireOp",EDGE,"E577.trimOffspring");var subQ1=sQuery(id+"F25.wireOp",EDGE,"E456.MirrorCS");var subQ2=makeQuery(id+"F25.imprint","INTERSECT",VERTEX,{"derivedFrom":[subQ1,subQ0]});Q364=makeQuery(id+"F25.imprint","IMPRINT",FACE,{"disambiguationData":[TD([[makeQuery(id+"F25.imprint","IMPRINT",EDGE,{"disambiguationData":[TD([[subQ2,-1.0]])],"derivedFrom":subQ1}),-1.0]])]});}
            var Q365;
            {var subQ0=sQuery(id+"F25.wireOp",EDGE,"E596.trimOffspring");var subQ1=sQuery(id+"F25.wireOp",EDGE,"E582.trimOffspring");var subQ2=makeQuery(id+"F25.imprint","INTERSECT",VERTEX,{"derivedFrom":[subQ1,subQ0]});Q365=makeQuery(id+"F25.imprint","IMPRINT",FACE,{"disambiguationData":[TD([[makeQuery(id+"F25.imprint","IMPRINT",EDGE,{"disambiguationData":[TD([[subQ2,-1.0]])],"derivedFrom":subQ1}),-1.0]])]});}
            var Q366;
            {var subQ0=sQuery(id+"F25.wireOp",EDGE,"E596.trimOffspring");var subQ1=sQuery(id+"F25.wireOp",EDGE,"E576.trimOffspring");var subQ2=makeQuery(id+"F25.imprint","INTERSECT",VERTEX,{"derivedFrom":[subQ1,subQ0]});Q366=makeQuery(id+"F25.imprint","IMPRINT",FACE,{"disambiguationData":[TD([[makeQuery(id+"F25.imprint","IMPRINT",EDGE,{"disambiguationData":[TD([[subQ2,-1.0]])],"derivedFrom":subQ1}),1.0]])]});}
            var Q367;
            {var subQ0=sQuery(id+"F25.wireOp",EDGE,"E598.trimOffspring");var subQ1=sQuery(id+"F25.wireOp",EDGE,"E582.trimOffspring");var subQ2=makeQuery(id+"F25.imprint","INTERSECT",VERTEX,{"derivedFrom":[subQ1,subQ0]});Q367=makeQuery(id+"F25.imprint","IMPRINT",FACE,{"disambiguationData":[TD([[makeQuery(id+"F25.imprint","IMPRINT",EDGE,{"disambiguationData":[TD([[subQ2,-1.0]])],"derivedFrom":subQ1}),-1.0]])]});}
            var Q368;
            {var subQ0=sQuery(id+"F25.wireOp",EDGE,"E597.trimOffspring");var subQ1=sQuery(id+"F25.wireOp",EDGE,"E576.trimOffspring");var subQ2=makeQuery(id+"F25.imprint","INTERSECT",VERTEX,{"derivedFrom":[subQ1,subQ0]});Q368=makeQuery(id+"F25.imprint","IMPRINT",FACE,{"disambiguationData":[TD([[makeQuery(id+"F25.imprint","IMPRINT",EDGE,{"disambiguationData":[TD([[subQ2,1.0]])],"derivedFrom":subQ1}),1.0]])]});}
            var Q369;
            {var subQ0=sQuery(id+"F25.wireOp",EDGE,"E597.trimOffspring");var subQ1=sQuery(id+"F25.wireOp",EDGE,"E576.trimOffspring");var subQ2=makeQuery(id+"F25.imprint","INTERSECT",VERTEX,{"derivedFrom":[subQ1,subQ0]});Q369=makeQuery(id+"F25.imprint","IMPRINT",FACE,{"disambiguationData":[TD([[makeQuery(id+"F25.imprint","IMPRINT",EDGE,{"disambiguationData":[TD([[subQ2,-1.0]])],"derivedFrom":subQ1}),1.0]])]});}
            var Q370;
            {var subQ0=sQuery(id+"F25.wireOp",EDGE,"E582.trimOffspring");var subQ1=sQuery(id+"F25.wireOp",EDGE,"E585.trimOffspring");var subQ2=makeQuery(id+"F25.imprint","INTERSECT",VERTEX,{"derivedFrom":[subQ1,subQ0]});Q370=makeQuery(id+"F25.imprint","IMPRINT",FACE,{"disambiguationData":[TD([[makeQuery(id+"F25.imprint","IMPRINT",EDGE,{"disambiguationData":[TD([[subQ2,-1.0]])],"derivedFrom":subQ1}),-1.0]])]});}
            var Q371;
            {var subQ0=sQuery(id+"F25.wireOp",EDGE,"E582.trimOffspring");var subQ1=sQuery(id+"F25.wireOp",EDGE,"E585.trimOffspring");var subQ2=makeQuery(id+"F25.imprint","INTERSECT",VERTEX,{"derivedFrom":[subQ1,subQ0]});Q371=makeQuery(id+"F25.imprint","IMPRINT",FACE,{"disambiguationData":[TD([[makeQuery(id+"F25.imprint","IMPRINT",EDGE,{"disambiguationData":[TD([[subQ2,-1.0]])],"derivedFrom":subQ1}),1.0]])]});}
            var Q372;
            {var subQ0=sQuery(id+"F25.wireOp",EDGE,"E585.trimOffspring");var subQ1=sQuery(id+"F25.wireOp",EDGE,"E576.trimOffspring");var subQ2=makeQuery(id+"F25.imprint","INTERSECT",VERTEX,{"derivedFrom":[subQ1,subQ0]});Q372=makeQuery(id+"F25.imprint","IMPRINT",FACE,{"disambiguationData":[TD([[makeQuery(id+"F25.imprint","IMPRINT",EDGE,{"disambiguationData":[TD([[subQ2,-1.0]])],"derivedFrom":subQ1}),1.0]])]});}
            var Q373;
            {var subQ0=sQuery(id+"F25.wireOp",EDGE,"E589.trimOffspring");var subQ1=sQuery(id+"F25.wireOp",EDGE,"E576.trimOffspring");var subQ2=makeQuery(id+"F25.imprint","INTERSECT",VERTEX,{"derivedFrom":[subQ1,subQ0]});Q373=makeQuery(id+"F25.imprint","IMPRINT",FACE,{"disambiguationData":[TD([[makeQuery(id+"F25.imprint","IMPRINT",EDGE,{"disambiguationData":[TD([[subQ2,1.0]])],"derivedFrom":subQ1}),1.0]])]});}
            var Q374;
            {var subQ0=sQuery(id+"F25.wireOp",EDGE,"E433.MirrorCS");Q374=makeQuery(id+"F25.imprint","IMPRINT",FACE,{"disambiguationData":[TD([[makeQuery(id+"F25.imprint","IMPRINT",EDGE,{"derivedFrom":subQ0}),1.0]])]});}
            var Q375;
            {var subQ3=sQuery(id+"F25.wireOp",EDGE,"E585.trimOffspring");var subQ5=sQuery(id+"F25.wireOp",EDGE,"E576.trimOffspring");var subQ6=makeQuery(id+"F25.imprint","INTERSECT",VERTEX,{"derivedFrom":[subQ5,subQ3]});Q375=makeQuery(id+"F25.imprint","IMPRINT",FACE,{"disambiguationData":[TD([[makeQuery(id+"F25.imprint","IMPRINT",EDGE,{"disambiguationData":[TD([[subQ6,-1.0]])],"derivedFrom":subQ5}),-1.0]])]});}
            var Q376;
            {var subQ0=sQuery(id+"F25.wireOp",EDGE,"E589.trimOffspring");var subQ1=sQuery(id+"F25.wireOp",EDGE,"E582.trimOffspring");var subQ2=makeQuery(id+"F25.imprint","INTERSECT",VERTEX,{"derivedFrom":[subQ1,subQ0]});Q376=makeQuery(id+"F25.imprint","IMPRINT",FACE,{"disambiguationData":[TD([[makeQuery(id+"F25.imprint","IMPRINT",EDGE,{"disambiguationData":[TD([[subQ2,1.0]])],"derivedFrom":subQ1}),-1.0]])]});}
            var Q377;
            {var subQ0=sQuery(id+"F25.wireOp",EDGE,"E578.trimOffspring");var subQ1=sQuery(id+"F25.wireOp",EDGE,"E454.MirrorCS");var subQ2=makeQuery(id+"F25.imprint","INTERSECT",VERTEX,{"derivedFrom":[subQ1,subQ0]});Q377=makeQuery(id+"F25.imprint","IMPRINT",FACE,{"disambiguationData":[TD([[makeQuery(id+"F25.imprint","IMPRINT",EDGE,{"disambiguationData":[TD([[subQ2,-1.0]])],"derivedFrom":subQ1}),1.0]])]});}
            var Q378;
            {var subQ0=sQuery(id+"F25.wireOp",EDGE,"E574.trimOffspring");var subQ1=sQuery(id+"F25.wireOp",EDGE,"E456.MirrorCS");var subQ2=makeQuery(id+"F25.imprint","INTERSECT",VERTEX,{"derivedFrom":[subQ1,subQ0]});Q378=makeQuery(id+"F25.imprint","IMPRINT",FACE,{"disambiguationData":[TD([[makeQuery(id+"F25.imprint","IMPRINT",EDGE,{"disambiguationData":[TD([[subQ2,1.0]])],"derivedFrom":subQ1}),-1.0]])]});}
            var Q379;
            {var subQ0=sQuery(id+"F25.wireOp",EDGE,"E574.trimOffspring");var subQ1=sQuery(id+"F25.wireOp",EDGE,"E454.MirrorCS");var subQ2=makeQuery(id+"F25.imprint","INTERSECT",VERTEX,{"derivedFrom":[subQ1,subQ0]});Q379=makeQuery(id+"F25.imprint","IMPRINT",FACE,{"disambiguationData":[TD([[makeQuery(id+"F25.imprint","IMPRINT",EDGE,{"disambiguationData":[TD([[subQ2,-1.0]])],"derivedFrom":subQ1}),1.0]])]});}
            var Q380;
            {var subQ0=sQuery(id+"F25.wireOp",EDGE,"E574.trimOffspring");var subQ1=sQuery(id+"F25.wireOp",EDGE,"E456.MirrorCS");var subQ2=makeQuery(id+"F25.imprint","INTERSECT",VERTEX,{"derivedFrom":[subQ1,subQ0]});Q380=makeQuery(id+"F25.imprint","IMPRINT",FACE,{"disambiguationData":[TD([[makeQuery(id+"F25.imprint","IMPRINT",EDGE,{"disambiguationData":[TD([[subQ2,-1.0]])],"derivedFrom":subQ1}),-1.0]])]});}
            var Q381;
            {var subQ0=sQuery(id+"F25.wireOp",EDGE,"E580.trimOffspring");var subQ1=sQuery(id+"F25.wireOp",EDGE,"E454.MirrorCS");var subQ2=makeQuery(id+"F25.imprint","INTERSECT",VERTEX,{"derivedFrom":[subQ1,subQ0]});Q381=makeQuery(id+"F25.imprint","IMPRINT",FACE,{"disambiguationData":[TD([[makeQuery(id+"F25.imprint","IMPRINT",EDGE,{"disambiguationData":[TD([[subQ2,-1.0]])],"derivedFrom":subQ1}),1.0]])]});}
            var Q382;
            {var subQ0=sQuery(id+"F25.wireOp",EDGE,"E580.trimOffspring");var subQ1=sQuery(id+"F25.wireOp",EDGE,"E456.MirrorCS");var subQ2=makeQuery(id+"F25.imprint","INTERSECT",VERTEX,{"derivedFrom":[subQ1,subQ0]});Q382=makeQuery(id+"F25.imprint","IMPRINT",FACE,{"disambiguationData":[TD([[makeQuery(id+"F25.imprint","IMPRINT",EDGE,{"disambiguationData":[TD([[subQ2,-1.0]])],"derivedFrom":subQ1}),-1.0]])]});}
            var Q383;
            {var subQ0=sQuery(id+"F25.wireOp",EDGE,"E579.trimOffspring");var subQ1=sQuery(id+"F25.wireOp",EDGE,"E454.MirrorCS");var subQ2=makeQuery(id+"F25.imprint","INTERSECT",VERTEX,{"derivedFrom":[subQ1,subQ0]});Q383=makeQuery(id+"F25.imprint","IMPRINT",FACE,{"disambiguationData":[TD([[makeQuery(id+"F25.imprint","IMPRINT",EDGE,{"disambiguationData":[TD([[subQ2,-1.0]])],"derivedFrom":subQ1}),1.0]])]});}
            var Q384;
            {var subQ0=sQuery(id+"F25.wireOp",EDGE,"E581.trimOffspring");var subQ1=sQuery(id+"F25.wireOp",EDGE,"E456.MirrorCS");var subQ2=makeQuery(id+"F25.imprint","INTERSECT",VERTEX,{"derivedFrom":[subQ1,subQ0]});Q384=makeQuery(id+"F25.imprint","IMPRINT",FACE,{"disambiguationData":[TD([[makeQuery(id+"F25.imprint","IMPRINT",EDGE,{"disambiguationData":[TD([[subQ2,1.0]])],"derivedFrom":subQ1}),-1.0]])]});}
            var Q385;
            {var subQ0=sQuery(id+"F25.wireOp",EDGE,"E581.trimOffspring");var subQ1=sQuery(id+"F25.wireOp",EDGE,"E454.MirrorCS");var subQ2=makeQuery(id+"F25.imprint","INTERSECT",VERTEX,{"derivedFrom":[subQ1,subQ0]});Q385=makeQuery(id+"F25.imprint","IMPRINT",FACE,{"disambiguationData":[TD([[makeQuery(id+"F25.imprint","IMPRINT",EDGE,{"disambiguationData":[TD([[subQ2,-1.0]])],"derivedFrom":subQ1}),1.0]])]});}
            var Q386;
            {var subQ0=sQuery(id+"F25.wireOp",EDGE,"E581.trimOffspring");var subQ1=sQuery(id+"F25.wireOp",EDGE,"E456.MirrorCS");var subQ2=makeQuery(id+"F25.imprint","INTERSECT",VERTEX,{"derivedFrom":[subQ1,subQ0]});Q386=makeQuery(id+"F25.imprint","IMPRINT",FACE,{"disambiguationData":[TD([[makeQuery(id+"F25.imprint","IMPRINT",EDGE,{"disambiguationData":[TD([[subQ2,-1.0]])],"derivedFrom":subQ1}),-1.0]])]});}
            var Q387;
            {var subQ0=sQuery(id+"F25.wireOp",EDGE,"E585.trimOffspring");var subQ1=sQuery(id+"F25.wireOp",EDGE,"E454.MirrorCS");var subQ2=makeQuery(id+"F25.imprint","INTERSECT",VERTEX,{"derivedFrom":[subQ1,subQ0]});Q387=makeQuery(id+"F25.imprint","IMPRINT",FACE,{"disambiguationData":[TD([[makeQuery(id+"F25.imprint","IMPRINT",EDGE,{"disambiguationData":[TD([[subQ2,-1.0]])],"derivedFrom":subQ1}),1.0]])]});}
            var Q388;
            {var subQ3=sQuery(id+"F25.wireOp",EDGE,"E585.trimOffspring");var subQ5=sQuery(id+"F25.wireOp",EDGE,"E441.MirrorCS");var subQ6=makeQuery(id+"F25.imprint","INTERSECT",VERTEX,{"derivedFrom":[subQ5,subQ3]});Q388=makeQuery(id+"F25.imprint","IMPRINT",FACE,{"disambiguationData":[TD([[makeQuery(id+"F25.imprint","IMPRINT",EDGE,{"disambiguationData":[TD([[subQ6,-1.0]])],"derivedFrom":subQ5}),1.0]])]});}
            var Q389;
            {var subQ0=sQuery(id+"F25.wireOp",EDGE,"E433.MirrorCS");Q389=makeQuery(id+"F25.imprint","IMPRINT",FACE,{"disambiguationData":[TD([[makeQuery(id+"F25.imprint","IMPRINT",EDGE,{"derivedFrom":subQ0}),-1.0]])]});}
            var Q390;
            {var subQ0=sQuery(id+"F25.wireOp",EDGE,"E589.trimOffspring");var subQ1=sQuery(id+"F25.wireOp",EDGE,"E454.MirrorCS");var subQ2=makeQuery(id+"F25.imprint","INTERSECT",VERTEX,{"derivedFrom":[subQ1,subQ0]});Q390=makeQuery(id+"F25.imprint","IMPRINT",FACE,{"disambiguationData":[TD([[makeQuery(id+"F25.imprint","IMPRINT",EDGE,{"disambiguationData":[TD([[subQ2,1.0]])],"derivedFrom":subQ1}),1.0]])]});}
            var Q391;
            {var subQ0=sQuery(id+"F25.wireOp",EDGE,"E608.trimOffspring");var subQ1=sQuery(id+"F25.wireOp",EDGE,"E423.MirrorCS");var subQ2=makeQuery(id+"F25.imprint","INTERSECT",VERTEX,{"derivedFrom":[subQ1,subQ0]});Q391=makeQuery(id+"F25.imprint","IMPRINT",FACE,{"disambiguationData":[TD([[makeQuery(id+"F25.imprint","IMPRINT",EDGE,{"disambiguationData":[TD([[subQ2,-1.0]])],"derivedFrom":subQ1}),1.0]])]});}
            var Q392;
            {var subQ0=sQuery(id+"F25.wireOp",EDGE,"E608.trimOffspring");var subQ1=sQuery(id+"F25.wireOp",EDGE,"E427.MirrorCS");var subQ2=makeQuery(id+"F25.imprint","INTERSECT",VERTEX,{"derivedFrom":[subQ1,subQ0]});Q392=makeQuery(id+"F25.imprint","IMPRINT",FACE,{"disambiguationData":[TD([[makeQuery(id+"F25.imprint","IMPRINT",EDGE,{"disambiguationData":[TD([[subQ2,-1.0]])],"derivedFrom":subQ1}),1.0]])]});}
            var Q393;
            {var subQ0=sQuery(id+"F25.wireOp",EDGE,"E584.trimOffspring");Q393=makeQuery(id+"F25.imprint","IMPRINT",FACE,{"disambiguationData":[TD([[makeQuery(id+"F25.imprint","IMPRINT",EDGE,{"derivedFrom":subQ0}),1.0]])]});}
            var Q394;
            {var subQ3=sQuery(id+"F25.wireOp",EDGE,"E608.trimOffspring");var subQ5=sQuery(id+"F25.wireOp",EDGE,"E448.MirrorCS");var subQ6=makeQuery(id+"F25.imprint","INTERSECT",VERTEX,{"derivedFrom":[subQ5,subQ3]});Q394=makeQuery(id+"F25.imprint","IMPRINT",FACE,{"disambiguationData":[TD([[makeQuery(id+"F25.imprint","IMPRINT",EDGE,{"disambiguationData":[TD([[subQ6,-1.0]])],"derivedFrom":subQ5}),-1.0]])]});}
            var Q395;
            {var subQ0=sQuery(id+"F25.wireOp",EDGE,"E608.trimOffspring");var subQ1=sQuery(id+"F25.wireOp",EDGE,"E431.MirrorCS");var subQ2=makeQuery(id+"F25.imprint","INTERSECT",VERTEX,{"derivedFrom":[subQ1,subQ0]});Q395=makeQuery(id+"F25.imprint","IMPRINT",FACE,{"disambiguationData":[TD([[makeQuery(id+"F25.imprint","IMPRINT",EDGE,{"disambiguationData":[TD([[subQ2,-1.0]])],"derivedFrom":subQ1}),-1.0]])]});}
            var Q396;
            {var subQ0=sQuery(id+"F25.wireOp",EDGE,"E608.trimOffspring");var subQ1=sQuery(id+"F25.wireOp",EDGE,"E431.MirrorCS");var subQ2=makeQuery(id+"F25.imprint","INTERSECT",VERTEX,{"derivedFrom":[subQ1,subQ0]});Q396=makeQuery(id+"F25.imprint","IMPRINT",FACE,{"disambiguationData":[TD([[makeQuery(id+"F25.imprint","IMPRINT",EDGE,{"disambiguationData":[TD([[subQ2,-1.0]])],"derivedFrom":subQ1}),1.0]])]});}
            var Q397;
            {var subQ0=sQuery(id+"F25.wireOp",EDGE,"E608.trimOffspring");var subQ1=sQuery(id+"F25.wireOp",EDGE,"E446.MirrorCS");var subQ2=makeQuery(id+"F25.imprint","INTERSECT",VERTEX,{"derivedFrom":[subQ1,subQ0]});Q397=makeQuery(id+"F25.imprint","IMPRINT",FACE,{"disambiguationData":[TD([[makeQuery(id+"F25.imprint","IMPRINT",EDGE,{"disambiguationData":[TD([[subQ2,-1.0]])],"derivedFrom":subQ1}),1.0]])]});}
            var Q398;
            {var subQ0=sQuery(id+"F25.wireOp",EDGE,"E608.trimOffspring");var subQ1=sQuery(id+"F25.wireOp",EDGE,"E444.MirrorCS");var subQ2=makeQuery(id+"F25.imprint","INTERSECT",VERTEX,{"derivedFrom":[subQ1,subQ0]});Q398=makeQuery(id+"F25.imprint","IMPRINT",FACE,{"disambiguationData":[TD([[makeQuery(id+"F25.imprint","IMPRINT",EDGE,{"disambiguationData":[TD([[subQ2,-1.0]])],"derivedFrom":subQ1}),-1.0]])]});}
            var Q399;
            {var subQ0=sQuery(id+"F25.wireOp",EDGE,"E603.trimOffspring");var subQ1=sQuery(id+"F25.wireOp",EDGE,"E444.MirrorCS");var subQ2=makeQuery(id+"F25.imprint","INTERSECT",VERTEX,{"derivedFrom":[subQ1,subQ0]});Q399=makeQuery(id+"F25.imprint","IMPRINT",FACE,{"disambiguationData":[TD([[makeQuery(id+"F25.imprint","IMPRINT",EDGE,{"disambiguationData":[TD([[subQ2,-1.0]])],"derivedFrom":subQ1}),-1.0]])]});}
            var Q400;
            {var subQ0=sQuery(id+"F25.wireOp",EDGE,"E603.trimOffspring");var subQ1=sQuery(id+"F25.wireOp",EDGE,"E446.MirrorCS");var subQ2=makeQuery(id+"F25.imprint","INTERSECT",VERTEX,{"derivedFrom":[subQ1,subQ0]});Q400=makeQuery(id+"F25.imprint","IMPRINT",FACE,{"disambiguationData":[TD([[makeQuery(id+"F25.imprint","IMPRINT",EDGE,{"disambiguationData":[TD([[subQ2,-1.0]])],"derivedFrom":subQ1}),1.0]])]});}
            var Q401;
            {var subQ0=sQuery(id+"F25.wireOp",EDGE,"E602.trimOffspring");var subQ1=sQuery(id+"F25.wireOp",EDGE,"E446.MirrorCS");var subQ2=makeQuery(id+"F25.imprint","INTERSECT",VERTEX,{"derivedFrom":[subQ1,subQ0]});Q401=makeQuery(id+"F25.imprint","IMPRINT",FACE,{"disambiguationData":[TD([[makeQuery(id+"F25.imprint","IMPRINT",EDGE,{"disambiguationData":[TD([[subQ2,-1.0]])],"derivedFrom":subQ1}),1.0]])]});}
            var Q402;
            {var subQ0=sQuery(id+"F25.wireOp",EDGE,"E601.trimOffspring");var subQ1=sQuery(id+"F25.wireOp",EDGE,"E446.MirrorCS");var subQ2=makeQuery(id+"F25.imprint","INTERSECT",VERTEX,{"derivedFrom":[subQ1,subQ0]});Q402=makeQuery(id+"F25.imprint","IMPRINT",FACE,{"disambiguationData":[TD([[makeQuery(id+"F25.imprint","IMPRINT",EDGE,{"disambiguationData":[TD([[subQ2,-1.0]])],"derivedFrom":subQ1}),1.0]])]});}
            var Q403;
            {var subQ0=sQuery(id+"F25.wireOp",EDGE,"E590.trimOffspring");var subQ1=sQuery(id+"F25.wireOp",EDGE,"E446.MirrorCS");var subQ2=makeQuery(id+"F25.imprint","INTERSECT",VERTEX,{"derivedFrom":[subQ1,subQ0]});Q403=makeQuery(id+"F25.imprint","IMPRINT",FACE,{"disambiguationData":[TD([[makeQuery(id+"F25.imprint","IMPRINT",EDGE,{"disambiguationData":[TD([[subQ2,-1.0]])],"derivedFrom":subQ1}),1.0]])]});}
            var Q404;
            {var subQ0=sQuery(id+"F25.wireOp",EDGE,"E593.trimOffspring");var subQ1=sQuery(id+"F25.wireOp",EDGE,"E446.MirrorCS");var subQ2=makeQuery(id+"F25.imprint","INTERSECT",VERTEX,{"derivedFrom":[subQ1,subQ0]});Q404=makeQuery(id+"F25.imprint","IMPRINT",FACE,{"disambiguationData":[TD([[makeQuery(id+"F25.imprint","IMPRINT",EDGE,{"disambiguationData":[TD([[subQ2,-1.0]])],"derivedFrom":subQ1}),1.0]])]});}
            var Q405;
            {var subQ0=sQuery(id+"F25.wireOp",EDGE,"E591.trimOffspring");var subQ1=sQuery(id+"F25.wireOp",EDGE,"E446.MirrorCS");var subQ2=makeQuery(id+"F25.imprint","INTERSECT",VERTEX,{"derivedFrom":[subQ1,subQ0]});Q405=makeQuery(id+"F25.imprint","IMPRINT",FACE,{"disambiguationData":[TD([[makeQuery(id+"F25.imprint","IMPRINT",EDGE,{"disambiguationData":[TD([[subQ2,1.0]])],"derivedFrom":subQ1}),1.0]])]});}
            var Q406;
            {var subQ0=sQuery(id+"F25.wireOp",EDGE,"E591.trimOffspring");var subQ1=sQuery(id+"F25.wireOp",EDGE,"E444.MirrorCS");var subQ2=makeQuery(id+"F25.imprint","INTERSECT",VERTEX,{"derivedFrom":[subQ1,subQ0]});Q406=makeQuery(id+"F25.imprint","IMPRINT",FACE,{"disambiguationData":[TD([[makeQuery(id+"F25.imprint","IMPRINT",EDGE,{"disambiguationData":[TD([[subQ2,1.0]])],"derivedFrom":subQ1}),-1.0]])]});}
            var Q407;
            {var subQ0=sQuery(id+"F25.wireOp",EDGE,"E591.trimOffspring");var subQ1=sQuery(id+"F25.wireOp",EDGE,"E444.MirrorCS");var subQ2=makeQuery(id+"F25.imprint","INTERSECT",VERTEX,{"derivedFrom":[subQ1,subQ0]});Q407=makeQuery(id+"F25.imprint","IMPRINT",FACE,{"disambiguationData":[TD([[makeQuery(id+"F25.imprint","IMPRINT",EDGE,{"disambiguationData":[TD([[subQ2,1.0]])],"derivedFrom":subQ1}),1.0]])]});}
            var Q408;
            {var subQ0=sQuery(id+"F25.wireOp",EDGE,"E591.trimOffspring");var subQ5=sQuery(id+"F25.wireOp",EDGE,"E427.MirrorCS");var subQ6=makeQuery(id+"F25.imprint","INTERSECT",VERTEX,{"derivedFrom":[subQ5,subQ0]});Q408=makeQuery(id+"F25.imprint","IMPRINT",FACE,{"disambiguationData":[TD([[makeQuery(id+"F25.imprint","IMPRINT",EDGE,{"disambiguationData":[TD([[subQ6,1.0]])],"derivedFrom":subQ5}),-1.0]])]});}
            var Q409;
            {var subQ0=sQuery(id+"F25.wireOp",EDGE,"E593.trimOffspring");var subQ5=sQuery(id+"F25.wireOp",EDGE,"E427.MirrorCS");var subQ7=makeQuery(id+"F25.imprint","INTERSECT",VERTEX,{"derivedFrom":[subQ5,subQ0]});Q409=makeQuery(id+"F25.imprint","IMPRINT",FACE,{"disambiguationData":[TD([[makeQuery(id+"F25.imprint","IMPRINT",EDGE,{"disambiguationData":[TD([[subQ7,-1.0]])],"derivedFrom":subQ5}),-1.0]])]});}
            var Q410;
            {var subQ0=sQuery(id+"F25.wireOp",EDGE,"E590.trimOffspring");var subQ5=sQuery(id+"F25.wireOp",EDGE,"E427.MirrorCS");var subQ6=makeQuery(id+"F25.imprint","INTERSECT",VERTEX,{"derivedFrom":[subQ5,subQ0]});Q410=makeQuery(id+"F25.imprint","IMPRINT",FACE,{"disambiguationData":[TD([[makeQuery(id+"F25.imprint","IMPRINT",EDGE,{"disambiguationData":[TD([[subQ6,-1.0]])],"derivedFrom":subQ5}),-1.0]])]});}
            var Q411;
            {var subQ3=sQuery(id+"F25.wireOp",EDGE,"E567.trimOffspring");var subQ5=sQuery(id+"F25.wireOp",EDGE,"E427.MirrorCS");var subQ6=makeQuery(id+"F25.imprint","INTERSECT",VERTEX,{"derivedFrom":[subQ5,subQ3]});Q411=makeQuery(id+"F25.imprint","IMPRINT",FACE,{"disambiguationData":[TD([[makeQuery(id+"F25.imprint","IMPRINT",EDGE,{"disambiguationData":[TD([[subQ6,-1.0]])],"derivedFrom":subQ5}),-1.0]])]});}
            var Q412;
            {var subQ0=sQuery(id+"F25.wireOp",EDGE,"E594.trimOffspring");var subQ5=sQuery(id+"F25.wireOp",EDGE,"E427.MirrorCS");var subQ6=makeQuery(id+"F25.imprint","INTERSECT",VERTEX,{"derivedFrom":[subQ5,subQ0]});Q412=makeQuery(id+"F25.imprint","IMPRINT",FACE,{"disambiguationData":[TD([[makeQuery(id+"F25.imprint","IMPRINT",EDGE,{"disambiguationData":[TD([[subQ6,-1.0]])],"derivedFrom":subQ5}),-1.0]])]});}
            var Q413;
            {var subQ3=sQuery(id+"F25.wireOp",EDGE,"E599.trimOffspring");var subQ5=sQuery(id+"F25.wireOp",EDGE,"E427.MirrorCS");var subQ6=makeQuery(id+"F25.imprint","INTERSECT",VERTEX,{"derivedFrom":[subQ5,subQ3]});Q413=makeQuery(id+"F25.imprint","IMPRINT",FACE,{"disambiguationData":[TD([[makeQuery(id+"F25.imprint","IMPRINT",EDGE,{"disambiguationData":[TD([[subQ6,-1.0]])],"derivedFrom":subQ5}),-1.0]])]});}
            var Q414;
            {var subQ0=sQuery(id+"F25.wireOp",EDGE,"E599.trimOffspring");var subQ1=sQuery(id+"F25.wireOp",EDGE,"E427.MirrorCS");var subQ2=makeQuery(id+"F25.imprint","INTERSECT",VERTEX,{"derivedFrom":[subQ1,subQ0]});Q414=makeQuery(id+"F25.imprint","IMPRINT",FACE,{"disambiguationData":[TD([[makeQuery(id+"F25.imprint","IMPRINT",EDGE,{"disambiguationData":[TD([[subQ2,-1.0]])],"derivedFrom":subQ1}),1.0]])]});}
            var Q415;
            {var subQ0=sQuery(id+"F25.wireOp",EDGE,"E594.trimOffspring");var subQ1=sQuery(id+"F25.wireOp",EDGE,"E427.MirrorCS");var subQ2=makeQuery(id+"F25.imprint","INTERSECT",VERTEX,{"derivedFrom":[subQ1,subQ0]});Q415=makeQuery(id+"F25.imprint","IMPRINT",FACE,{"disambiguationData":[TD([[makeQuery(id+"F25.imprint","IMPRINT",EDGE,{"disambiguationData":[TD([[subQ2,-1.0]])],"derivedFrom":subQ1}),1.0]])]});}
            var Q416;
            {var subQ0=sQuery(id+"F25.wireOp",EDGE,"E567.trimOffspring");var subQ1=sQuery(id+"F25.wireOp",EDGE,"E427.MirrorCS");var subQ2=makeQuery(id+"F25.imprint","INTERSECT",VERTEX,{"derivedFrom":[subQ1,subQ0]});Q416=makeQuery(id+"F25.imprint","IMPRINT",FACE,{"disambiguationData":[TD([[makeQuery(id+"F25.imprint","IMPRINT",EDGE,{"disambiguationData":[TD([[subQ2,-1.0]])],"derivedFrom":subQ1}),1.0]])]});}
            var Q417;
            {var subQ0=sQuery(id+"F25.wireOp",EDGE,"E590.trimOffspring");var subQ1=sQuery(id+"F25.wireOp",EDGE,"E427.MirrorCS");var subQ2=makeQuery(id+"F25.imprint","INTERSECT",VERTEX,{"derivedFrom":[subQ1,subQ0]});Q417=makeQuery(id+"F25.imprint","IMPRINT",FACE,{"disambiguationData":[TD([[makeQuery(id+"F25.imprint","IMPRINT",EDGE,{"disambiguationData":[TD([[subQ2,-1.0]])],"derivedFrom":subQ1}),1.0]])]});}
            var Q418;
            {var subQ0=sQuery(id+"F25.wireOp",EDGE,"E593.trimOffspring");var subQ1=sQuery(id+"F25.wireOp",EDGE,"E427.MirrorCS");var subQ2=makeQuery(id+"F25.imprint","INTERSECT",VERTEX,{"derivedFrom":[subQ1,subQ0]});Q418=makeQuery(id+"F25.imprint","IMPRINT",FACE,{"disambiguationData":[TD([[makeQuery(id+"F25.imprint","IMPRINT",EDGE,{"disambiguationData":[TD([[subQ2,-1.0]])],"derivedFrom":subQ1}),1.0]])]});}
            var Q419;
            {var subQ0=sQuery(id+"F25.wireOp",EDGE,"E591.trimOffspring");var subQ1=sQuery(id+"F25.wireOp",EDGE,"E427.MirrorCS");var subQ2=makeQuery(id+"F25.imprint","INTERSECT",VERTEX,{"derivedFrom":[subQ1,subQ0]});Q419=makeQuery(id+"F25.imprint","IMPRINT",FACE,{"disambiguationData":[TD([[makeQuery(id+"F25.imprint","IMPRINT",EDGE,{"disambiguationData":[TD([[subQ2,1.0]])],"derivedFrom":subQ1}),1.0]])]});}
            var Q420;
            {var subQ0=sQuery(id+"F25.wireOp",EDGE,"E591.trimOffspring");var subQ1=sQuery(id+"F25.wireOp",EDGE,"E440.MirrorCS");var subQ2=makeQuery(id+"F25.imprint","INTERSECT",VERTEX,{"derivedFrom":[subQ1,subQ0]});Q420=makeQuery(id+"F25.imprint","IMPRINT",FACE,{"disambiguationData":[TD([[makeQuery(id+"F25.imprint","IMPRINT",EDGE,{"disambiguationData":[TD([[subQ2,1.0]])],"derivedFrom":subQ1}),1.0]])]});}
            var Q421;
            {var subQ0=sQuery(id+"F25.wireOp",EDGE,"E591.trimOffspring");var subQ1=sQuery(id+"F25.wireOp",EDGE,"E431.MirrorCS");var subQ2=makeQuery(id+"F25.imprint","INTERSECT",VERTEX,{"derivedFrom":[subQ1,subQ0]});Q421=makeQuery(id+"F25.imprint","IMPRINT",FACE,{"disambiguationData":[TD([[makeQuery(id+"F25.imprint","IMPRINT",EDGE,{"disambiguationData":[TD([[subQ2,1.0]])],"derivedFrom":subQ1}),-1.0]])]});}
            var Q422;
            {var subQ0=sQuery(id+"F25.wireOp",EDGE,"E593.trimOffspring");var subQ1=sQuery(id+"F25.wireOp",EDGE,"E440.MirrorCS");var subQ2=makeQuery(id+"F25.imprint","INTERSECT",VERTEX,{"derivedFrom":[subQ1,subQ0]});Q422=makeQuery(id+"F25.imprint","IMPRINT",FACE,{"disambiguationData":[TD([[makeQuery(id+"F25.imprint","IMPRINT",EDGE,{"disambiguationData":[TD([[subQ2,-1.0]])],"derivedFrom":subQ1}),1.0]])]});}
            var Q423;
            {var subQ0=sQuery(id+"F25.wireOp",EDGE,"E593.trimOffspring");var subQ1=sQuery(id+"F25.wireOp",EDGE,"E431.MirrorCS");var subQ2=makeQuery(id+"F25.imprint","INTERSECT",VERTEX,{"derivedFrom":[subQ1,subQ0]});Q423=makeQuery(id+"F25.imprint","IMPRINT",FACE,{"disambiguationData":[TD([[makeQuery(id+"F25.imprint","IMPRINT",EDGE,{"disambiguationData":[TD([[subQ2,-1.0]])],"derivedFrom":subQ1}),-1.0]])]});}
            var Q424;
            {var subQ0=sQuery(id+"F25.wireOp",EDGE,"E590.trimOffspring");var subQ1=sQuery(id+"F25.wireOp",EDGE,"E440.MirrorCS");var subQ2=makeQuery(id+"F25.imprint","INTERSECT",VERTEX,{"derivedFrom":[subQ1,subQ0]});Q424=makeQuery(id+"F25.imprint","IMPRINT",FACE,{"disambiguationData":[TD([[makeQuery(id+"F25.imprint","IMPRINT",EDGE,{"disambiguationData":[TD([[subQ2,-1.0]])],"derivedFrom":subQ1}),1.0]])]});}
            var Q425;
            {var subQ0=sQuery(id+"F25.wireOp",EDGE,"E590.trimOffspring");var subQ1=sQuery(id+"F25.wireOp",EDGE,"E431.MirrorCS");var subQ2=makeQuery(id+"F25.imprint","INTERSECT",VERTEX,{"derivedFrom":[subQ1,subQ0]});Q425=makeQuery(id+"F25.imprint","IMPRINT",FACE,{"disambiguationData":[TD([[makeQuery(id+"F25.imprint","IMPRINT",EDGE,{"disambiguationData":[TD([[subQ2,-1.0]])],"derivedFrom":subQ1}),-1.0]])]});}
            var Q426;
            {var subQ0=sQuery(id+"F25.wireOp",EDGE,"E601.trimOffspring");var subQ5=sQuery(id+"F25.wireOp",EDGE,"E448.MirrorCS");var subQ6=makeQuery(id+"F25.imprint","INTERSECT",VERTEX,{"derivedFrom":[subQ5,subQ0]});Q426=makeQuery(id+"F25.imprint","IMPRINT",FACE,{"disambiguationData":[TD([[makeQuery(id+"F25.imprint","IMPRINT",EDGE,{"disambiguationData":[TD([[subQ6,-1.0]])],"derivedFrom":subQ5}),-1.0]])]});}
            var Q427;
            {var subQ0=sQuery(id+"F25.wireOp",EDGE,"E601.trimOffspring");var subQ1=sQuery(id+"F25.wireOp",EDGE,"E431.MirrorCS");var subQ2=makeQuery(id+"F25.imprint","INTERSECT",VERTEX,{"derivedFrom":[subQ1,subQ0]});Q427=makeQuery(id+"F25.imprint","IMPRINT",FACE,{"disambiguationData":[TD([[makeQuery(id+"F25.imprint","IMPRINT",EDGE,{"disambiguationData":[TD([[subQ2,-1.0]])],"derivedFrom":subQ1}),-1.0]])]});}
            var Q428;
            {var subQ0=sQuery(id+"F25.wireOp",EDGE,"E602.trimOffspring");var subQ5=sQuery(id+"F25.wireOp",EDGE,"E448.MirrorCS");var subQ6=makeQuery(id+"F25.imprint","INTERSECT",VERTEX,{"derivedFrom":[subQ5,subQ0]});Q428=makeQuery(id+"F25.imprint","IMPRINT",FACE,{"disambiguationData":[TD([[makeQuery(id+"F25.imprint","IMPRINT",EDGE,{"disambiguationData":[TD([[subQ6,-1.0]])],"derivedFrom":subQ5}),-1.0]])]});}
            var Q429;
            {var subQ0=sQuery(id+"F25.wireOp",EDGE,"E602.trimOffspring");var subQ1=sQuery(id+"F25.wireOp",EDGE,"E431.MirrorCS");var subQ2=makeQuery(id+"F25.imprint","INTERSECT",VERTEX,{"derivedFrom":[subQ1,subQ0]});Q429=makeQuery(id+"F25.imprint","IMPRINT",FACE,{"disambiguationData":[TD([[makeQuery(id+"F25.imprint","IMPRINT",EDGE,{"disambiguationData":[TD([[subQ2,-1.0]])],"derivedFrom":subQ1}),-1.0]])]});}
            var Q430;
            {var subQ3=sQuery(id+"F25.wireOp",EDGE,"E603.trimOffspring");var subQ5=sQuery(id+"F25.wireOp",EDGE,"E448.MirrorCS");var subQ7=makeQuery(id+"F25.imprint","INTERSECT",VERTEX,{"derivedFrom":[subQ5,subQ3]});Q430=makeQuery(id+"F25.imprint","IMPRINT",FACE,{"disambiguationData":[TD([[makeQuery(id+"F25.imprint","IMPRINT",EDGE,{"disambiguationData":[TD([[subQ7,-1.0]])],"derivedFrom":subQ5}),-1.0]])]});}
            var Q431;
            {var subQ0=sQuery(id+"F25.wireOp",EDGE,"E603.trimOffspring");var subQ1=sQuery(id+"F25.wireOp",EDGE,"E431.MirrorCS");var subQ2=makeQuery(id+"F25.imprint","INTERSECT",VERTEX,{"derivedFrom":[subQ1,subQ0]});Q431=makeQuery(id+"F25.imprint","IMPRINT",FACE,{"disambiguationData":[TD([[makeQuery(id+"F25.imprint","IMPRINT",EDGE,{"disambiguationData":[TD([[subQ2,-1.0]])],"derivedFrom":subQ1}),-1.0]])]});}
            var Q432;
            {var subQ0=sQuery(id+"F25.wireOp",EDGE,"E595.trimOffspring");var subQ1=sQuery(id+"F25.wireOp",EDGE,"E473.trimOffspring");var subQ2=makeQuery(id+"F25.imprint","INTERSECT",VERTEX,{"derivedFrom":[subQ1,subQ0]});Q432=makeQuery(id+"F25.imprint","IMPRINT",FACE,{"disambiguationData":[TD([[makeQuery(id+"F25.imprint","IMPRINT",EDGE,{"disambiguationData":[TD([[subQ2,-1.0]])],"derivedFrom":subQ1}),1.0]])]});}
            var Q433;
            {var subQ0=sQuery(id+"F25.wireOp",EDGE,"E595.trimOffspring");var subQ1=sQuery(id+"F25.wireOp",EDGE,"E474.trimOffspring");var subQ2=makeQuery(id+"F25.imprint","INTERSECT",VERTEX,{"derivedFrom":[subQ1,subQ0]});Q433=makeQuery(id+"F25.imprint","IMPRINT",FACE,{"disambiguationData":[TD([[makeQuery(id+"F25.imprint","IMPRINT",EDGE,{"disambiguationData":[TD([[subQ2,-1.0]])],"derivedFrom":subQ1}),1.0]])]});}
            var Q434;
            {var subQ0=sQuery(id+"F25.wireOp",EDGE,"E593.trimOffspring");var subQ1=sQuery(id+"F25.wireOp",EDGE,"E474.trimOffspring");var subQ2=makeQuery(id+"F25.imprint","INTERSECT",VERTEX,{"derivedFrom":[subQ1,subQ0]});Q434=makeQuery(id+"F25.imprint","IMPRINT",FACE,{"disambiguationData":[TD([[makeQuery(id+"F25.imprint","IMPRINT",EDGE,{"disambiguationData":[TD([[subQ2,-1.0]])],"derivedFrom":subQ1}),1.0]])]});}
            var Q435;
            {var subQ0=sQuery(id+"F25.wireOp",EDGE,"E590.trimOffspring");var subQ1=sQuery(id+"F25.wireOp",EDGE,"E474.trimOffspring");var subQ2=makeQuery(id+"F25.imprint","INTERSECT",VERTEX,{"derivedFrom":[subQ1,subQ0]});Q435=makeQuery(id+"F25.imprint","IMPRINT",FACE,{"disambiguationData":[TD([[makeQuery(id+"F25.imprint","IMPRINT",EDGE,{"disambiguationData":[TD([[subQ2,-1.0]])],"derivedFrom":subQ1}),1.0]])]});}
            var Q436;
            {var subQ0=sQuery(id+"F25.wireOp",EDGE,"E601.trimOffspring");var subQ1=sQuery(id+"F25.wireOp",EDGE,"E474.trimOffspring");var subQ2=makeQuery(id+"F25.imprint","INTERSECT",VERTEX,{"derivedFrom":[subQ1,subQ0]});Q436=makeQuery(id+"F25.imprint","IMPRINT",FACE,{"disambiguationData":[TD([[makeQuery(id+"F25.imprint","IMPRINT",EDGE,{"disambiguationData":[TD([[subQ2,-1.0]])],"derivedFrom":subQ1}),1.0]])]});}
            var Q437;
            {var subQ0=sQuery(id+"F25.wireOp",EDGE,"E601.trimOffspring");var subQ1=sQuery(id+"F25.wireOp",EDGE,"E475.trimOffspring");var subQ2=makeQuery(id+"F25.imprint","INTERSECT",VERTEX,{"derivedFrom":[subQ1,subQ0]});Q437=makeQuery(id+"F25.imprint","IMPRINT",FACE,{"disambiguationData":[TD([[makeQuery(id+"F25.imprint","IMPRINT",EDGE,{"disambiguationData":[TD([[subQ2,-1.0]])],"derivedFrom":subQ1}),-1.0]])]});}
            var Q438;
            {var subQ3=sQuery(id+"F25.wireOp",EDGE,"E601.trimOffspring");var subQ5=sQuery(id+"F25.wireOp",EDGE,"E475.trimOffspring");var subQ6=makeQuery(id+"F25.imprint","INTERSECT",VERTEX,{"derivedFrom":[subQ5,subQ3]});Q438=makeQuery(id+"F25.imprint","IMPRINT",FACE,{"disambiguationData":[TD([[makeQuery(id+"F25.imprint","IMPRINT",EDGE,{"disambiguationData":[TD([[subQ6,-1.0]])],"derivedFrom":subQ5}),1.0]])]});}
            var Q439;
            {var subQ0=sQuery(id+"F25.wireOp",EDGE,"E590.trimOffspring");var subQ5=sQuery(id+"F25.wireOp",EDGE,"E475.trimOffspring");var subQ6=makeQuery(id+"F25.imprint","INTERSECT",VERTEX,{"derivedFrom":[subQ5,subQ0]});Q439=makeQuery(id+"F25.imprint","IMPRINT",FACE,{"disambiguationData":[TD([[makeQuery(id+"F25.imprint","IMPRINT",EDGE,{"disambiguationData":[TD([[subQ6,-1.0]])],"derivedFrom":subQ5}),1.0]])]});}
            var Q440;
            {var subQ3=sQuery(id+"F25.wireOp",EDGE,"E593.trimOffspring");var subQ5=sQuery(id+"F25.wireOp",EDGE,"E475.trimOffspring");var subQ6=makeQuery(id+"F25.imprint","INTERSECT",VERTEX,{"derivedFrom":[subQ5,subQ3]});Q440=makeQuery(id+"F25.imprint","IMPRINT",FACE,{"disambiguationData":[TD([[makeQuery(id+"F25.imprint","IMPRINT",EDGE,{"disambiguationData":[TD([[subQ6,-1.0]])],"derivedFrom":subQ5}),1.0]])]});}
            var Q441;
            {var subQ0=sQuery(id+"F25.wireOp",EDGE,"E458.MirrorCS");var subQ5=sQuery(id+"F25.wireOp",EDGE,"E477.trimOffspring");var subQ6=makeQuery(id+"F25.imprint","INTERSECT",VERTEX,{"derivedFrom":[subQ0,subQ5]});Q441=makeQuery(id+"F25.imprint","IMPRINT",FACE,{"disambiguationData":[TD([[makeQuery(id+"F25.imprint","IMPRINT",EDGE,{"disambiguationData":[TD([[subQ6,-1.0]])],"derivedFrom":subQ5}),-1.0]])]});}
            var Q442;
            {var subQ0=sQuery(id+"F25.wireOp",EDGE,"E616.trimOffspring");var subQ1=sQuery(id+"F25.wireOp",EDGE,"E458.MirrorCS");var subQ2=makeQuery(id+"F25.imprint","INTERSECT",VERTEX,{"derivedFrom":[subQ1,subQ0]});Q442=makeQuery(id+"F25.imprint","IMPRINT",FACE,{"disambiguationData":[TD([[makeQuery(id+"F25.imprint","IMPRINT",EDGE,{"disambiguationData":[TD([[subQ2,-1.0]])],"derivedFrom":subQ1}),1.0]])]});}
            var Q443;
            {var subQ0=sQuery(id+"F25.wireOp",EDGE,"E595.trimOffspring");var subQ5=sQuery(id+"F25.wireOp",EDGE,"E475.trimOffspring");var subQ6=makeQuery(id+"F25.imprint","INTERSECT",VERTEX,{"derivedFrom":[subQ5,subQ0]});Q443=makeQuery(id+"F25.imprint","IMPRINT",FACE,{"disambiguationData":[TD([[makeQuery(id+"F25.imprint","IMPRINT",EDGE,{"disambiguationData":[TD([[subQ6,-1.0]])],"derivedFrom":subQ5}),1.0]])]});}
            var Q444;
            {var subQ0=sQuery(id+"F25.wireOp",EDGE,"E617.trimOffspring");var subQ1=sQuery(id+"F25.wireOp",EDGE,"E458.MirrorCS");var subQ2=makeQuery(id+"F25.imprint","INTERSECT",VERTEX,{"derivedFrom":[subQ1,subQ0]});Q444=makeQuery(id+"F25.imprint","IMPRINT",FACE,{"disambiguationData":[TD([[makeQuery(id+"F25.imprint","IMPRINT",EDGE,{"disambiguationData":[TD([[subQ2,-1.0]])],"derivedFrom":subQ1}),1.0]])]});}
            var Q445;
            {var subQ0=sQuery(id+"F25.wireOp",EDGE,"E617.trimOffspring");var subQ1=sQuery(id+"F25.wireOp",EDGE,"E419.MirrorCS");var subQ2=makeQuery(id+"F25.imprint","INTERSECT",VERTEX,{"derivedFrom":[subQ1,subQ0]});Q445=makeQuery(id+"F25.imprint","IMPRINT",FACE,{"disambiguationData":[TD([[makeQuery(id+"F25.imprint","IMPRINT",EDGE,{"disambiguationData":[TD([[subQ2,-1.0]])],"derivedFrom":subQ1}),-1.0]])]});}
            var Q446;
            {var subQ0=sQuery(id+"F25.wireOp",EDGE,"E617.trimOffspring");var subQ1=sQuery(id+"F25.wireOp",EDGE,"E417.MirrorCS");var subQ2=makeQuery(id+"F25.imprint","INTERSECT",VERTEX,{"derivedFrom":[subQ1,subQ0]});Q446=makeQuery(id+"F25.imprint","IMPRINT",FACE,{"disambiguationData":[TD([[makeQuery(id+"F25.imprint","IMPRINT",EDGE,{"disambiguationData":[TD([[subQ2,-1.0]])],"derivedFrom":subQ1}),-1.0]])]});}
            var Q447;
            {var subQ0=sQuery(id+"F25.wireOp",EDGE,"E617.trimOffspring");var subQ1=sQuery(id+"F25.wireOp",EDGE,"E417.MirrorCS");var subQ2=makeQuery(id+"F25.imprint","INTERSECT",VERTEX,{"derivedFrom":[subQ1,subQ0]});Q447=makeQuery(id+"F25.imprint","IMPRINT",FACE,{"disambiguationData":[TD([[makeQuery(id+"F25.imprint","IMPRINT",EDGE,{"disambiguationData":[TD([[subQ2,-1.0]])],"derivedFrom":subQ1}),1.0]])]});}
            var Q448;
            {var subQ0=sQuery(id+"F25.wireOp",EDGE,"E617.trimOffspring");var subQ1=sQuery(id+"F25.wireOp",EDGE,"E409.MirrorCS");var subQ2=makeQuery(id+"F25.imprint","INTERSECT",VERTEX,{"derivedFrom":[subQ1,subQ0]});Q448=makeQuery(id+"F25.imprint","IMPRINT",FACE,{"disambiguationData":[TD([[makeQuery(id+"F25.imprint","IMPRINT",EDGE,{"disambiguationData":[TD([[subQ2,-1.0]])],"derivedFrom":subQ1}),-1.0]])]});}
            var Q449;
            {var subQ0=sQuery(id+"F25.wireOp",EDGE,"E473.trimOffspring");var subQ1=sQuery(id+"F25.wireOp",EDGE,"E421.MirrorCS");var subQ2=makeQuery(id+"F25.imprint","INTERSECT",VERTEX,{"derivedFrom":[subQ1,subQ0]});Q449=makeQuery(id+"F25.imprint","IMPRINT",FACE,{"disambiguationData":[TD([[makeQuery(id+"F25.imprint","IMPRINT",EDGE,{"disambiguationData":[TD([[subQ2,-1.0]])],"derivedFrom":subQ1}),1.0]])]});}
            var Q450;
            {var subQ0=sQuery(id+"F25.wireOp",EDGE,"E473.trimOffspring");var subQ1=sQuery(id+"F25.wireOp",EDGE,"E416.MirrorCS");var subQ2=makeQuery(id+"F25.imprint","INTERSECT",VERTEX,{"derivedFrom":[subQ1,subQ0]});Q450=makeQuery(id+"F25.imprint","IMPRINT",FACE,{"disambiguationData":[TD([[makeQuery(id+"F25.imprint","IMPRINT",EDGE,{"disambiguationData":[TD([[subQ2,-1.0]])],"derivedFrom":subQ1}),-1.0]])]});}
            var Q451;
            {var subQ0=sQuery(id+"F25.wireOp",EDGE,"E474.trimOffspring");var subQ1=sQuery(id+"F25.wireOp",EDGE,"E421.MirrorCS");var subQ2=makeQuery(id+"F25.imprint","INTERSECT",VERTEX,{"derivedFrom":[subQ1,subQ0]});Q451=makeQuery(id+"F25.imprint","IMPRINT",FACE,{"disambiguationData":[TD([[makeQuery(id+"F25.imprint","IMPRINT",EDGE,{"disambiguationData":[TD([[subQ2,-1.0]])],"derivedFrom":subQ1}),1.0]])]});}
            var Q452;
            {var subQ0=sQuery(id+"F25.wireOp",EDGE,"E474.trimOffspring");var subQ1=sQuery(id+"F25.wireOp",EDGE,"E416.MirrorCS");var subQ2=makeQuery(id+"F25.imprint","INTERSECT",VERTEX,{"derivedFrom":[subQ1,subQ0]});Q452=makeQuery(id+"F25.imprint","IMPRINT",FACE,{"disambiguationData":[TD([[makeQuery(id+"F25.imprint","IMPRINT",EDGE,{"disambiguationData":[TD([[subQ2,-1.0]])],"derivedFrom":subQ1}),-1.0]])]});}
            var Q453;
            {var subQ0=sQuery(id+"F25.wireOp",EDGE,"E476.trimOffspring");var subQ1=sQuery(id+"F25.wireOp",EDGE,"E421.MirrorCS");var subQ2=makeQuery(id+"F25.imprint","INTERSECT",VERTEX,{"derivedFrom":[subQ1,subQ0]});Q453=makeQuery(id+"F25.imprint","IMPRINT",FACE,{"disambiguationData":[TD([[makeQuery(id+"F25.imprint","IMPRINT",EDGE,{"disambiguationData":[TD([[subQ2,-1.0]])],"derivedFrom":subQ1}),1.0]])]});}
            var Q454;
            {var subQ0=sQuery(id+"F25.wireOp",EDGE,"E476.trimOffspring");var subQ1=sQuery(id+"F25.wireOp",EDGE,"E416.MirrorCS");var subQ2=makeQuery(id+"F25.imprint","INTERSECT",VERTEX,{"derivedFrom":[subQ1,subQ0]});Q454=makeQuery(id+"F25.imprint","IMPRINT",FACE,{"disambiguationData":[TD([[makeQuery(id+"F25.imprint","IMPRINT",EDGE,{"disambiguationData":[TD([[subQ2,-1.0]])],"derivedFrom":subQ1}),-1.0]])]});}
            var Q455;
            {var subQ1=sQuery(id+"F25.wireOp",EDGE,"E421.MirrorCS");var subQ3=sQuery(id+"F25.wireOp",EDGE,"E475.trimOffspring");var subQ4=makeQuery(id+"F25.imprint","INTERSECT",VERTEX,{"derivedFrom":[subQ1,subQ3]});Q455=makeQuery(id+"F25.imprint","IMPRINT",FACE,{"disambiguationData":[TD([[makeQuery(id+"F25.imprint","IMPRINT",EDGE,{"disambiguationData":[TD([[subQ4,1.0]])],"derivedFrom":subQ3}),1.0]])]});}
            var Q456;
            {var subQ1=sQuery(id+"F25.wireOp",EDGE,"E416.MirrorCS");var subQ3=sQuery(id+"F25.wireOp",EDGE,"E475.trimOffspring");var subQ4=makeQuery(id+"F25.imprint","INTERSECT",VERTEX,{"derivedFrom":[subQ1,subQ3]});Q456=makeQuery(id+"F25.imprint","IMPRINT",FACE,{"disambiguationData":[TD([[makeQuery(id+"F25.imprint","IMPRINT",EDGE,{"disambiguationData":[TD([[subQ4,-1.0]])],"derivedFrom":subQ3}),1.0]])]});}
            var Q457;
            {var subQ1=sQuery(id+"F25.wireOp",EDGE,"E417.MirrorCS");var subQ3=sQuery(id+"F25.wireOp",EDGE,"E477.trimOffspring");var subQ4=makeQuery(id+"F25.imprint","INTERSECT",VERTEX,{"derivedFrom":[subQ1,subQ3]});Q457=makeQuery(id+"F25.imprint","IMPRINT",FACE,{"disambiguationData":[TD([[makeQuery(id+"F25.imprint","IMPRINT",EDGE,{"disambiguationData":[TD([[subQ4,-1.0]])],"derivedFrom":subQ3}),-1.0]])]});}
            var Q458;
            {var subQ1=sQuery(id+"F25.wireOp",EDGE,"E417.MirrorCS");var subQ3=sQuery(id+"F25.wireOp",EDGE,"E477.trimOffspring");var subQ4=makeQuery(id+"F25.imprint","INTERSECT",VERTEX,{"derivedFrom":[subQ1,subQ3]});Q458=makeQuery(id+"F25.imprint","IMPRINT",FACE,{"disambiguationData":[TD([[makeQuery(id+"F25.imprint","IMPRINT",EDGE,{"disambiguationData":[TD([[subQ4,1.0]])],"derivedFrom":subQ3}),-1.0]])]});}
            var Q459;
            {var subQ0=sQuery(id+"F25.wireOp",EDGE,"E616.trimOffspring");var subQ1=sQuery(id+"F25.wireOp",EDGE,"E417.MirrorCS");var subQ2=makeQuery(id+"F25.imprint","INTERSECT",VERTEX,{"derivedFrom":[subQ1,subQ0]});Q459=makeQuery(id+"F25.imprint","IMPRINT",FACE,{"disambiguationData":[TD([[makeQuery(id+"F25.imprint","IMPRINT",EDGE,{"disambiguationData":[TD([[subQ2,-1.0]])],"derivedFrom":subQ1}),-1.0]])]});}
            var Q460;
            {var subQ0=sQuery(id+"F25.wireOp",EDGE,"E616.trimOffspring");var subQ1=sQuery(id+"F25.wireOp",EDGE,"E417.MirrorCS");var subQ2=makeQuery(id+"F25.imprint","INTERSECT",VERTEX,{"derivedFrom":[subQ1,subQ0]});Q460=makeQuery(id+"F25.imprint","IMPRINT",FACE,{"disambiguationData":[TD([[makeQuery(id+"F25.imprint","IMPRINT",EDGE,{"disambiguationData":[TD([[subQ2,-1.0]])],"derivedFrom":subQ1}),1.0]])]});}
            var Q461;
            {var subQ0=sQuery(id+"F25.wireOp",EDGE,"E334.MirrorCS");var subQ1=sQuery(id+"F25.wireOp",EDGE,"E324.MirrorCS");var subQ2=makeQuery(id+"F25.imprint","INTERSECT",VERTEX,{"derivedFrom":[subQ1,subQ0]});Q461=makeQuery(id+"F25.imprint","IMPRINT",FACE,{"disambiguationData":[TD([[makeQuery(id+"F25.imprint","IMPRINT",EDGE,{"disambiguationData":[TD([[subQ2,-1.0]])],"derivedFrom":subQ1}),-1.0]])]});}
            var Q462;
            {var subQ0=sQuery(id+"F25.wireOp",EDGE,"E315.MirrorCS");Q462=makeQuery(id+"F25.imprint","IMPRINT",FACE,{"disambiguationData":[TD([[makeQuery(id+"F25.imprint","IMPRINT",EDGE,{"derivedFrom":subQ0}),1.0]])]});}
            var Q463;
            {var subQ5=sQuery(id+"F25.wireOp",EDGE,"E315.MirrorCS");Q463=makeQuery(id+"F25.imprint","IMPRINT",FACE,{"disambiguationData":[TD([[makeQuery(id+"F25.imprint","IMPRINT",EDGE,{"derivedFrom":subQ5}),-1.0]])]});}
            var Q464;
            {var subQ5=sQuery(id+"F25.wireOp",EDGE,"E616.trimOffspring");var subQ6=sQuery(id+"F25.wireOp",EDGE,"E409.MirrorCS");var subQ7=makeQuery(id+"F25.imprint","INTERSECT",VERTEX,{"derivedFrom":[subQ6,subQ5]});Q464=makeQuery(id+"F25.imprint","IMPRINT",FACE,{"disambiguationData":[TD([[makeQuery(id+"F25.imprint","IMPRINT",EDGE,{"disambiguationData":[TD([[subQ7,-1.0]])],"derivedFrom":subQ6}),1.0]])]});}
            var Q465;
            {var subQ4=sQuery(id+"F25.wireOp",EDGE,"E222.right");Q465=makeQuery(id+"F25.imprint","IMPRINT",FACE,{"disambiguationData":[TD([[makeQuery(id+"F25.imprint","IMPRINT",EDGE,{"derivedFrom":subQ4}),1.0]])]});}
            var Q466;
            {var subQ0=sQuery(id+"F25.wireOp",EDGE,"E311.MirrorCS");Q466=makeQuery(id+"F25.imprint","IMPRINT",FACE,{"disambiguationData":[TD([[makeQuery(id+"F25.imprint","IMPRINT",EDGE,{"derivedFrom":subQ0}),1.0]])]});}
            var Q467;
            {var subQ1=sQuery(id+"F25.wireOp",EDGE,"E415.MirrorCS");var subQ3=sQuery(id+"F25.wireOp",EDGE,"E475.trimOffspring");var subQ4=makeQuery(id+"F25.imprint","INTERSECT",VERTEX,{"derivedFrom":[subQ1,subQ3]});Q467=makeQuery(id+"F25.imprint","IMPRINT",FACE,{"disambiguationData":[TD([[makeQuery(id+"F25.imprint","IMPRINT",EDGE,{"disambiguationData":[TD([[subQ4,-1.0]])],"derivedFrom":subQ1}),-1.0]])]});}
            var Q468;
            {var subQ5=sQuery(id+"F25.wireOp",EDGE,"E222.right");Q468=makeQuery(id+"F25.imprint","IMPRINT",FACE,{"disambiguationData":[TD([[makeQuery(id+"F25.imprint","IMPRINT",EDGE,{"derivedFrom":subQ5}),-1.0]])]});}
            var Q469;
            {var subQ1=sQuery(id+"F25.wireOp",EDGE,"E249.right");var subQ3=sQuery(id+"F25.wireOp",EDGE,"E284.trimOffspring");var subQ4=makeQuery(id+"F25.imprint","INTERSECT",VERTEX,{"derivedFrom":[subQ1,subQ3]});Q469=makeQuery(id+"F25.imprint","IMPRINT",FACE,{"disambiguationData":[TD([[makeQuery(id+"F25.imprint","IMPRINT",EDGE,{"disambiguationData":[TD([[subQ4,1.0]])],"derivedFrom":subQ3}),1.0]])]});}
            var Q470;
            {var subQ0=sQuery(id+"F25.wireOp",EDGE,"E476.trimOffspring");var subQ1=sQuery(id+"F25.wireOp",EDGE,"E415.MirrorCS");var subQ2=makeQuery(id+"F25.imprint","INTERSECT",VERTEX,{"derivedFrom":[subQ1,subQ0]});Q470=makeQuery(id+"F25.imprint","IMPRINT",FACE,{"disambiguationData":[TD([[makeQuery(id+"F25.imprint","IMPRINT",EDGE,{"disambiguationData":[TD([[subQ2,-1.0]])],"derivedFrom":subQ1}),-1.0]])]});}
            var Q471;
            {var subQ0=sQuery(id+"F25.wireOp",EDGE,"E474.trimOffspring");var subQ1=sQuery(id+"F25.wireOp",EDGE,"E415.MirrorCS");var subQ2=makeQuery(id+"F25.imprint","INTERSECT",VERTEX,{"derivedFrom":[subQ1,subQ0]});Q471=makeQuery(id+"F25.imprint","IMPRINT",FACE,{"disambiguationData":[TD([[makeQuery(id+"F25.imprint","IMPRINT",EDGE,{"disambiguationData":[TD([[subQ2,-1.0]])],"derivedFrom":subQ1}),-1.0]])]});}
            var Q472;
            {var subQ0=sQuery(id+"F25.wireOp",EDGE,"E473.trimOffspring");var subQ1=sQuery(id+"F25.wireOp",EDGE,"E415.MirrorCS");var subQ2=makeQuery(id+"F25.imprint","INTERSECT",VERTEX,{"derivedFrom":[subQ1,subQ0]});Q472=makeQuery(id+"F25.imprint","IMPRINT",FACE,{"disambiguationData":[TD([[makeQuery(id+"F25.imprint","IMPRINT",EDGE,{"disambiguationData":[TD([[subQ2,-1.0]])],"derivedFrom":subQ1}),-1.0]])]});}
            var Q473;
            {var subQ1=sQuery(id+"F25.wireOp",EDGE,"E250.right");var subQ3=sQuery(id+"F25.wireOp",EDGE,"E284.trimOffspring");var subQ4=makeQuery(id+"F25.imprint","INTERSECT",VERTEX,{"derivedFrom":[subQ1,subQ3]});Q473=makeQuery(id+"F25.imprint","IMPRINT",FACE,{"disambiguationData":[TD([[makeQuery(id+"F25.imprint","IMPRINT",EDGE,{"disambiguationData":[TD([[subQ4,1.0]])],"derivedFrom":subQ3}),1.0]])]});}
            var Q474;
            {var subQ3=sQuery(id+"F25.wireOp",EDGE,"E284.trimOffspring");var subQ5=sQuery(id+"F25.wireOp",EDGE,"E251.right");var subQ7=makeQuery(id+"F25.imprint","INTERSECT",VERTEX,{"derivedFrom":[subQ5,subQ3]});Q474=makeQuery(id+"F25.imprint","IMPRINT",FACE,{"disambiguationData":[TD([[makeQuery(id+"F25.imprint","IMPRINT",EDGE,{"disambiguationData":[TD([[subQ7,-1.0]])],"derivedFrom":subQ3}),1.0]])]});}
            var Q475;
            {var subQ3=sQuery(id+"F25.wireOp",EDGE,"E510.trimOffspring");var subQ5=sQuery(id+"F25.wireOp",EDGE,"E249.right");var subQ6=makeQuery(id+"F25.imprint","INTERSECT",VERTEX,{"derivedFrom":[subQ5,subQ3]});Q475=makeQuery(id+"F25.imprint","IMPRINT",FACE,{"disambiguationData":[TD([[makeQuery(id+"F25.imprint","IMPRINT",EDGE,{"disambiguationData":[TD([[subQ6,-1.0]])],"derivedFrom":subQ5}),-1.0]])]});}
            var Q476;
            {var subQ0=sQuery(id+"F25.wireOp",EDGE,"E335.MirrorCS");var subQ5=sQuery(id+"F25.wireOp",EDGE,"E387.MirrorCS");var subQ6=makeQuery(id+"F25.imprint","INTERSECT",VERTEX,{"derivedFrom":[subQ0,subQ5]});Q476=makeQuery(id+"F25.imprint","IMPRINT",FACE,{"disambiguationData":[TD([[makeQuery(id+"F25.imprint","IMPRINT",EDGE,{"disambiguationData":[TD([[subQ6,1.0]])],"derivedFrom":subQ5}),1.0]])]});}
            var Q477;
            {var subQ0=sQuery(id+"F25.wireOp",EDGE,"E234.right");Q477=makeQuery(id+"F25.imprint","IMPRINT",FACE,{"disambiguationData":[TD([[makeQuery(id+"F25.imprint","IMPRINT",EDGE,{"derivedFrom":subQ0}),1.0]])]});}
            var Q478;
            {var subQ0=sQuery(id+"F25.wireOp",EDGE,"E232.right");Q478=makeQuery(id+"F25.imprint","IMPRINT",FACE,{"disambiguationData":[TD([[makeQuery(id+"F25.imprint","IMPRINT",EDGE,{"derivedFrom":subQ0}),-1.0]])]});}
            var Q479;
            {var subQ5=sQuery(id+"F25.wireOp",EDGE,"E234.right");Q479=makeQuery(id+"F25.imprint","IMPRINT",FACE,{"disambiguationData":[TD([[makeQuery(id+"F25.imprint","IMPRINT",EDGE,{"derivedFrom":subQ5}),-1.0]])]});}
            var Q480;
            {var subQ5=sQuery(id+"F25.wireOp",EDGE,"E232.right");Q480=makeQuery(id+"F25.imprint","IMPRINT",FACE,{"disambiguationData":[TD([[makeQuery(id+"F25.imprint","IMPRINT",EDGE,{"derivedFrom":subQ5}),1.0]])]});}
            var Q481;
            {var subQ0=sQuery(id+"F25.wireOp",EDGE,"E522.trimOffspring");var subQ1=sQuery(id+"F25.wireOp",EDGE,"E249.right");var subQ2=makeQuery(id+"F25.imprint","INTERSECT",VERTEX,{"derivedFrom":[subQ1,subQ0]});Q481=makeQuery(id+"F25.imprint","IMPRINT",FACE,{"disambiguationData":[TD([[makeQuery(id+"F25.imprint","IMPRINT",EDGE,{"disambiguationData":[TD([[subQ2,-1.0]])],"derivedFrom":subQ1}),1.0]])]});}
            var Q482;
            {var subQ0=sQuery(id+"F25.wireOp",EDGE,"E524.trimOffspring");var subQ1=sQuery(id+"F25.wireOp",EDGE,"E249.right");var subQ2=makeQuery(id+"F25.imprint","INTERSECT",VERTEX,{"derivedFrom":[subQ1,subQ0]});Q482=makeQuery(id+"F25.imprint","IMPRINT",FACE,{"disambiguationData":[TD([[makeQuery(id+"F25.imprint","IMPRINT",EDGE,{"disambiguationData":[TD([[subQ2,-1.0]])],"derivedFrom":subQ1}),1.0]])]});}
            var Q483;
            {var subQ0=sQuery(id+"F25.wireOp",EDGE,"E522.trimOffspring");var subQ1=sQuery(id+"F25.wireOp",EDGE,"E250.right");var subQ2=makeQuery(id+"F25.imprint","INTERSECT",VERTEX,{"derivedFrom":[subQ1,subQ0]});Q483=makeQuery(id+"F25.imprint","IMPRINT",FACE,{"disambiguationData":[TD([[makeQuery(id+"F25.imprint","IMPRINT",EDGE,{"disambiguationData":[TD([[subQ2,-1.0]])],"derivedFrom":subQ1}),1.0]])]});}
            var Q484;
            {var subQ0=sQuery(id+"F25.wireOp",EDGE,"E522.trimOffspring");var subQ1=sQuery(id+"F25.wireOp",EDGE,"E250.left");var subQ2=makeQuery(id+"F25.imprint","INTERSECT",VERTEX,{"derivedFrom":[subQ1,subQ0]});Q484=makeQuery(id+"F25.imprint","IMPRINT",FACE,{"disambiguationData":[TD([[makeQuery(id+"F25.imprint","IMPRINT",EDGE,{"disambiguationData":[TD([[subQ2,-1.0]])],"derivedFrom":subQ1}),1.0]])]});}
            var Q485;
            {var subQ0=sQuery(id+"F25.wireOp",EDGE,"E524.trimOffspring");var subQ1=sQuery(id+"F25.wireOp",EDGE,"E250.left");var subQ2=makeQuery(id+"F25.imprint","INTERSECT",VERTEX,{"derivedFrom":[subQ1,subQ0]});Q485=makeQuery(id+"F25.imprint","IMPRINT",FACE,{"disambiguationData":[TD([[makeQuery(id+"F25.imprint","IMPRINT",EDGE,{"disambiguationData":[TD([[subQ2,-1.0]])],"derivedFrom":subQ1}),1.0]])]});}
            var Q486;
            {var subQ0=sQuery(id+"F25.wireOp",EDGE,"E524.trimOffspring");var subQ1=sQuery(id+"F25.wireOp",EDGE,"E250.right");var subQ2=makeQuery(id+"F25.imprint","INTERSECT",VERTEX,{"derivedFrom":[subQ1,subQ0]});Q486=makeQuery(id+"F25.imprint","IMPRINT",FACE,{"disambiguationData":[TD([[makeQuery(id+"F25.imprint","IMPRINT",EDGE,{"disambiguationData":[TD([[subQ2,-1.0]])],"derivedFrom":subQ1}),1.0]])]});}
            var Q487;
            {var subQ0=sQuery(id+"F25.wireOp",EDGE,"E525.trimOffspring");var subQ1=sQuery(id+"F25.wireOp",EDGE,"E250.right");var subQ2=makeQuery(id+"F25.imprint","INTERSECT",VERTEX,{"derivedFrom":[subQ1,subQ0]});Q487=makeQuery(id+"F25.imprint","IMPRINT",FACE,{"disambiguationData":[TD([[makeQuery(id+"F25.imprint","IMPRINT",EDGE,{"disambiguationData":[TD([[subQ2,-1.0]])],"derivedFrom":subQ1}),1.0]])]});}
            var Q488;
            {var subQ0=sQuery(id+"F25.wireOp",EDGE,"E334.MirrorCS");var subQ1=sQuery(id+"F25.wireOp",EDGE,"E324.MirrorCS");var subQ2=makeQuery(id+"F25.imprint","INTERSECT",VERTEX,{"derivedFrom":[subQ1,subQ0]});Q488=makeQuery(id+"F25.imprint","IMPRINT",FACE,{"disambiguationData":[TD([[makeQuery(id+"F25.imprint","IMPRINT",EDGE,{"disambiguationData":[TD([[subQ2,-1.0]])],"derivedFrom":subQ1}),1.0]])]});}
            var Q489;
            {var subQ0=sQuery(id+"F25.wireOp",EDGE,"E365.MirrorCS");var subQ1=sQuery(id+"F25.wireOp",EDGE,"E324.MirrorCS");var subQ2=makeQuery(id+"F25.imprint","INTERSECT",VERTEX,{"derivedFrom":[subQ1,subQ0]});Q489=makeQuery(id+"F25.imprint","IMPRINT",FACE,{"disambiguationData":[TD([[makeQuery(id+"F25.imprint","IMPRINT",EDGE,{"disambiguationData":[TD([[subQ2,-1.0]])],"derivedFrom":subQ1}),1.0]])]});}
            var Q490;
            {var subQ0=sQuery(id+"F25.wireOp",EDGE,"E334.MirrorCS");var subQ1=sQuery(id+"F25.wireOp",EDGE,"E349.MirrorCS");var subQ2=makeQuery(id+"F25.imprint","INTERSECT",VERTEX,{"derivedFrom":[subQ1,subQ0]});Q490=makeQuery(id+"F25.imprint","IMPRINT",FACE,{"disambiguationData":[TD([[makeQuery(id+"F25.imprint","IMPRINT",EDGE,{"disambiguationData":[TD([[subQ2,-1.0]])],"derivedFrom":subQ1}),-1.0]])]});}
            var Q491;
            {var subQ0=sQuery(id+"F25.wireOp",EDGE,"E365.MirrorCS");var subQ1=sQuery(id+"F25.wireOp",EDGE,"E349.MirrorCS");var subQ2=makeQuery(id+"F25.imprint","INTERSECT",VERTEX,{"derivedFrom":[subQ1,subQ0]});Q491=makeQuery(id+"F25.imprint","IMPRINT",FACE,{"disambiguationData":[TD([[makeQuery(id+"F25.imprint","IMPRINT",EDGE,{"disambiguationData":[TD([[subQ2,-1.0]])],"derivedFrom":subQ1}),-1.0]])]});}
            var Q492;
            {var subQ0=sQuery(id+"F25.wireOp",EDGE,"E525.trimOffspring");var subQ1=sQuery(id+"F25.wireOp",EDGE,"E250.left");var subQ2=makeQuery(id+"F25.imprint","INTERSECT",VERTEX,{"derivedFrom":[subQ1,subQ0]});Q492=makeQuery(id+"F25.imprint","IMPRINT",FACE,{"disambiguationData":[TD([[makeQuery(id+"F25.imprint","IMPRINT",EDGE,{"disambiguationData":[TD([[subQ2,-1.0]])],"derivedFrom":subQ1}),1.0]])]});}
            var Q493;
            {var subQ0=sQuery(id+"F25.wireOp",EDGE,"E285.trimOffspring");var subQ1=sQuery(id+"F25.wireOp",EDGE,"E250.left");var subQ2=makeQuery(id+"F25.imprint","INTERSECT",VERTEX,{"derivedFrom":[subQ1,subQ0]});Q493=makeQuery(id+"F25.imprint","IMPRINT",FACE,{"disambiguationData":[TD([[makeQuery(id+"F25.imprint","IMPRINT",EDGE,{"disambiguationData":[TD([[subQ2,-1.0]])],"derivedFrom":subQ1}),1.0]])]});}
            var Q494;
            {var subQ0=sQuery(id+"F25.wireOp",EDGE,"E286.trimOffspring");var subQ1=sQuery(id+"F25.wireOp",EDGE,"E250.left");var subQ2=makeQuery(id+"F25.imprint","INTERSECT",VERTEX,{"derivedFrom":[subQ1,subQ0]});Q494=makeQuery(id+"F25.imprint","IMPRINT",FACE,{"disambiguationData":[TD([[makeQuery(id+"F25.imprint","IMPRINT",EDGE,{"disambiguationData":[TD([[subQ2,-1.0]])],"derivedFrom":subQ1}),1.0]])]});}
            var Q495;
            {var subQ0=sQuery(id+"F25.wireOp",EDGE,"E285.trimOffspring");var subQ1=sQuery(id+"F25.wireOp",EDGE,"E250.right");var subQ2=makeQuery(id+"F25.imprint","INTERSECT",VERTEX,{"derivedFrom":[subQ1,subQ0]});Q495=makeQuery(id+"F25.imprint","IMPRINT",FACE,{"disambiguationData":[TD([[makeQuery(id+"F25.imprint","IMPRINT",EDGE,{"disambiguationData":[TD([[subQ2,-1.0]])],"derivedFrom":subQ1}),1.0]])]});}
            var Q496;
            {var subQ0=sQuery(id+"F25.wireOp",EDGE,"E286.trimOffspring");var subQ1=sQuery(id+"F25.wireOp",EDGE,"E250.right");var subQ2=makeQuery(id+"F25.imprint","INTERSECT",VERTEX,{"derivedFrom":[subQ1,subQ0]});Q496=makeQuery(id+"F25.imprint","IMPRINT",FACE,{"disambiguationData":[TD([[makeQuery(id+"F25.imprint","IMPRINT",EDGE,{"disambiguationData":[TD([[subQ2,-1.0]])],"derivedFrom":subQ1}),1.0]])]});}
            var Q497;
            {var subQ0=sQuery(id+"F25.wireOp",EDGE,"E223.right");Q497=makeQuery(id+"F25.imprint","IMPRINT",FACE,{"disambiguationData":[TD([[makeQuery(id+"F25.imprint","IMPRINT",EDGE,{"derivedFrom":subQ0}),1.0]])]});}
            var Q498;
            {var subQ0=sQuery(id+"F25.wireOp",EDGE,"E224.right");Q498=makeQuery(id+"F25.imprint","IMPRINT",FACE,{"disambiguationData":[TD([[makeQuery(id+"F25.imprint","IMPRINT",EDGE,{"derivedFrom":subQ0}),-1.0]])]});}
            var Q499;
            {var subQ5=sQuery(id+"F25.wireOp",EDGE,"E224.right");Q499=makeQuery(id+"F25.imprint","IMPRINT",FACE,{"disambiguationData":[TD([[makeQuery(id+"F25.imprint","IMPRINT",EDGE,{"derivedFrom":subQ5}),1.0]])]});}
            var Q500;
            {var subQ5=sQuery(id+"F25.wireOp",EDGE,"E223.right");Q500=makeQuery(id+"F25.imprint","IMPRINT",FACE,{"disambiguationData":[TD([[makeQuery(id+"F25.imprint","IMPRINT",EDGE,{"derivedFrom":subQ5}),-1.0]])]});}
            var Q501;
            {var subQ0=sQuery(id+"F25.wireOp",EDGE,"E285.trimOffspring");var subQ1=sQuery(id+"F25.wireOp",EDGE,"E249.right");var subQ2=makeQuery(id+"F25.imprint","INTERSECT",VERTEX,{"derivedFrom":[subQ1,subQ0]});Q501=makeQuery(id+"F25.imprint","IMPRINT",FACE,{"disambiguationData":[TD([[makeQuery(id+"F25.imprint","IMPRINT",EDGE,{"disambiguationData":[TD([[subQ2,-1.0]])],"derivedFrom":subQ1}),1.0]])]});}
            var Q502;
            {var subQ0=sQuery(id+"F25.wireOp",EDGE,"E286.trimOffspring");var subQ1=sQuery(id+"F25.wireOp",EDGE,"E249.right");var subQ2=makeQuery(id+"F25.imprint","INTERSECT",VERTEX,{"derivedFrom":[subQ1,subQ0]});Q502=makeQuery(id+"F25.imprint","IMPRINT",FACE,{"disambiguationData":[TD([[makeQuery(id+"F25.imprint","IMPRINT",EDGE,{"disambiguationData":[TD([[subQ2,-1.0]])],"derivedFrom":subQ1}),1.0]])]});}
            var Q503;
            {var subQ0=sQuery(id+"F25.wireOp",EDGE,"E235.right");Q503=makeQuery(id+"F25.imprint","IMPRINT",FACE,{"disambiguationData":[TD([[makeQuery(id+"F25.imprint","IMPRINT",EDGE,{"derivedFrom":subQ0}),-1.0]])]});}
            var Q504;
            {var subQ0=sQuery(id+"F25.wireOp",EDGE,"E299.MirrorCS");Q504=makeQuery(id+"F25.imprint","IMPRINT",FACE,{"disambiguationData":[TD([[makeQuery(id+"F25.imprint","IMPRINT",EDGE,{"derivedFrom":subQ0}),1.0]])]});}
            var Q505;
            {var subQ0=sQuery(id+"F25.wireOp",EDGE,"E364.MirrorCS");var subQ1=sQuery(id+"F25.wireOp",EDGE,"E332.MirrorCS");var subQ2=makeQuery(id+"F25.imprint","INTERSECT",VERTEX,{"derivedFrom":[subQ1,subQ0]});Q505=makeQuery(id+"F25.imprint","IMPRINT",FACE,{"disambiguationData":[TD([[makeQuery(id+"F25.imprint","IMPRINT",EDGE,{"disambiguationData":[TD([[subQ2,-1.0]])],"derivedFrom":subQ1}),-1.0]])]});}
            var Q506;
            {var subQ0=sQuery(id+"F25.wireOp",EDGE,"E340.MirrorCS");var subQ1=sQuery(id+"F25.wireOp",EDGE,"E364.MirrorCS");var subQ2=makeQuery(id+"F25.imprint","INTERSECT",VERTEX,{"derivedFrom":[subQ1,subQ0]});Q506=makeQuery(id+"F25.imprint","IMPRINT",FACE,{"disambiguationData":[TD([[makeQuery(id+"F25.imprint","IMPRINT",EDGE,{"disambiguationData":[TD([[subQ2,-1.0]])],"derivedFrom":subQ1}),1.0]])]});}
            var Q507;
            {var subQ0=sQuery(id+"F25.wireOp",EDGE,"E364.MirrorCS");var subQ1=sQuery(id+"F25.wireOp",EDGE,"E363.MirrorCS");var subQ2=makeQuery(id+"F25.imprint","INTERSECT",VERTEX,{"derivedFrom":[subQ1,subQ0]});Q507=makeQuery(id+"F25.imprint","IMPRINT",FACE,{"disambiguationData":[TD([[makeQuery(id+"F25.imprint","IMPRINT",EDGE,{"disambiguationData":[TD([[subQ2,-1.0]])],"derivedFrom":subQ1}),1.0]])]});}
            var Q508;
            {var subQ0=sQuery(id+"F25.wireOp",EDGE,"E388.MirrorCS");var subQ1=sQuery(id+"F25.wireOp",EDGE,"E332.MirrorCS");var subQ2=makeQuery(id+"F25.imprint","INTERSECT",VERTEX,{"derivedFrom":[subQ1,subQ0]});Q508=makeQuery(id+"F25.imprint","IMPRINT",FACE,{"disambiguationData":[TD([[makeQuery(id+"F25.imprint","IMPRINT",EDGE,{"disambiguationData":[TD([[subQ2,-1.0]])],"derivedFrom":subQ1}),-1.0]])]});}
            var Q509;
            {var subQ0=sQuery(id+"F25.wireOp",EDGE,"E340.MirrorCS");var subQ1=sQuery(id+"F25.wireOp",EDGE,"E364.MirrorCS");var subQ2=makeQuery(id+"F25.imprint","INTERSECT",VERTEX,{"derivedFrom":[subQ1,subQ0]});Q509=makeQuery(id+"F25.imprint","IMPRINT",FACE,{"disambiguationData":[TD([[makeQuery(id+"F25.imprint","IMPRINT",EDGE,{"disambiguationData":[TD([[subQ2,-1.0]])],"derivedFrom":subQ1}),-1.0]])]});}
            var Q510;
            {var subQ0=sQuery(id+"F25.wireOp",EDGE,"E359.MirrorCS");var subQ1=sQuery(id+"F25.wireOp",EDGE,"E332.MirrorCS");var subQ2=makeQuery(id+"F25.imprint","INTERSECT",VERTEX,{"derivedFrom":[subQ1,subQ0]});Q510=makeQuery(id+"F25.imprint","IMPRINT",FACE,{"disambiguationData":[TD([[makeQuery(id+"F25.imprint","IMPRINT",EDGE,{"disambiguationData":[TD([[subQ2,-1.0]])],"derivedFrom":subQ1}),-1.0]])]});}
            var Q511;
            {var subQ0=sQuery(id+"F25.wireOp",EDGE,"E340.MirrorCS");var subQ1=sQuery(id+"F25.wireOp",EDGE,"E359.MirrorCS");var subQ2=makeQuery(id+"F25.imprint","INTERSECT",VERTEX,{"derivedFrom":[subQ1,subQ0]});Q511=makeQuery(id+"F25.imprint","IMPRINT",FACE,{"disambiguationData":[TD([[makeQuery(id+"F25.imprint","IMPRINT",EDGE,{"disambiguationData":[TD([[subQ2,-1.0]])],"derivedFrom":subQ1}),1.0]])]});}
            var Q512;
            {var subQ0=sQuery(id+"F25.wireOp",EDGE,"E342.MirrorCS");var subQ1=sQuery(id+"F25.wireOp",EDGE,"E332.MirrorCS");var subQ2=makeQuery(id+"F25.imprint","INTERSECT",VERTEX,{"derivedFrom":[subQ1,subQ0]});Q512=makeQuery(id+"F25.imprint","IMPRINT",FACE,{"disambiguationData":[TD([[makeQuery(id+"F25.imprint","IMPRINT",EDGE,{"disambiguationData":[TD([[subQ2,-1.0]])],"derivedFrom":subQ1}),-1.0]])]});}
            var Q513;
            {var subQ0=sQuery(id+"F25.wireOp",EDGE,"E340.MirrorCS");var subQ1=sQuery(id+"F25.wireOp",EDGE,"E342.MirrorCS");var subQ2=makeQuery(id+"F25.imprint","INTERSECT",VERTEX,{"derivedFrom":[subQ1,subQ0]});Q513=makeQuery(id+"F25.imprint","IMPRINT",FACE,{"disambiguationData":[TD([[makeQuery(id+"F25.imprint","IMPRINT",EDGE,{"disambiguationData":[TD([[subQ2,-1.0]])],"derivedFrom":subQ1}),1.0]])]});}
            var Q514;
            {var subQ0=sQuery(id+"F25.wireOp",EDGE,"E332.MirrorCS");var subQ1=sQuery(id+"F25.wireOp",EDGE,"E328.MirrorCS");var subQ2=makeQuery(id+"F25.imprint","INTERSECT",VERTEX,{"derivedFrom":[subQ1,subQ0]});Q514=makeQuery(id+"F25.imprint","IMPRINT",FACE,{"disambiguationData":[TD([[makeQuery(id+"F25.imprint","IMPRINT",EDGE,{"disambiguationData":[TD([[subQ2,-1.0]])],"derivedFrom":subQ1}),1.0]])]});}
            var Q515;
            {var subQ0=sQuery(id+"F25.wireOp",EDGE,"E340.MirrorCS");var subQ1=sQuery(id+"F25.wireOp",EDGE,"E328.MirrorCS");var subQ2=makeQuery(id+"F25.imprint","INTERSECT",VERTEX,{"derivedFrom":[subQ1,subQ0]});Q515=makeQuery(id+"F25.imprint","IMPRINT",FACE,{"disambiguationData":[TD([[makeQuery(id+"F25.imprint","IMPRINT",EDGE,{"disambiguationData":[TD([[subQ2,-1.0]])],"derivedFrom":subQ1}),1.0]])]});}
            var Q516;
            {var subQ0=sQuery(id+"F25.wireOp",EDGE,"E340.MirrorCS");var subQ1=sQuery(id+"F25.wireOp",EDGE,"E328.MirrorCS");var subQ2=makeQuery(id+"F25.imprint","INTERSECT",VERTEX,{"derivedFrom":[subQ1,subQ0]});Q516=makeQuery(id+"F25.imprint","IMPRINT",FACE,{"disambiguationData":[TD([[makeQuery(id+"F25.imprint","IMPRINT",EDGE,{"disambiguationData":[TD([[subQ2,-1.0]])],"derivedFrom":subQ1}),-1.0]])]});}
            var Q517;
            {var subQ0=sQuery(id+"F25.wireOp",EDGE,"E332.MirrorCS");var subQ1=sQuery(id+"F25.wireOp",EDGE,"E328.MirrorCS");var subQ2=makeQuery(id+"F25.imprint","INTERSECT",VERTEX,{"derivedFrom":[subQ1,subQ0]});Q517=makeQuery(id+"F25.imprint","IMPRINT",FACE,{"disambiguationData":[TD([[makeQuery(id+"F25.imprint","IMPRINT",EDGE,{"disambiguationData":[TD([[subQ2,-1.0]])],"derivedFrom":subQ1}),-1.0]])]});}
            var Q518;
            {var subQ0=sQuery(id+"F25.wireOp",EDGE,"E358.MirrorCS");var subQ1=sQuery(id+"F25.wireOp",EDGE,"E332.MirrorCS");var subQ2=makeQuery(id+"F25.imprint","INTERSECT",VERTEX,{"derivedFrom":[subQ1,subQ0]});Q518=makeQuery(id+"F25.imprint","IMPRINT",FACE,{"disambiguationData":[TD([[makeQuery(id+"F25.imprint","IMPRINT",EDGE,{"disambiguationData":[TD([[subQ2,-1.0]])],"derivedFrom":subQ1}),-1.0]])]});}
            var Q519;
            {var subQ0=sQuery(id+"F25.wireOp",EDGE,"E340.MirrorCS");var subQ1=sQuery(id+"F25.wireOp",EDGE,"E358.MirrorCS");var subQ2=makeQuery(id+"F25.imprint","INTERSECT",VERTEX,{"derivedFrom":[subQ1,subQ0]});Q519=makeQuery(id+"F25.imprint","IMPRINT",FACE,{"disambiguationData":[TD([[makeQuery(id+"F25.imprint","IMPRINT",EDGE,{"disambiguationData":[TD([[subQ2,-1.0]])],"derivedFrom":subQ1}),1.0]])]});}
            var Q520;
            {var subQ0=sQuery(id+"F25.wireOp",EDGE,"E364.MirrorCS");var subQ1=sQuery(id+"F25.wireOp",EDGE,"E331.MirrorCS");var subQ2=makeQuery(id+"F25.imprint","INTERSECT",VERTEX,{"derivedFrom":[subQ1,subQ0]});Q520=makeQuery(id+"F25.imprint","IMPRINT",FACE,{"disambiguationData":[TD([[makeQuery(id+"F25.imprint","IMPRINT",EDGE,{"disambiguationData":[TD([[subQ2,-1.0]])],"derivedFrom":subQ1}),1.0]])]});}
            var Q521;
            {var subQ0=sQuery(id+"F25.wireOp",EDGE,"E388.MirrorCS");var subQ1=sQuery(id+"F25.wireOp",EDGE,"E331.MirrorCS");var subQ2=makeQuery(id+"F25.imprint","INTERSECT",VERTEX,{"derivedFrom":[subQ1,subQ0]});Q521=makeQuery(id+"F25.imprint","IMPRINT",FACE,{"disambiguationData":[TD([[makeQuery(id+"F25.imprint","IMPRINT",EDGE,{"disambiguationData":[TD([[subQ2,-1.0]])],"derivedFrom":subQ1}),1.0]])]});}
            var Q522;
            {var subQ0=sQuery(id+"F25.wireOp",EDGE,"E364.MirrorCS");var subQ1=sQuery(id+"F25.wireOp",EDGE,"E331.MirrorCS");var subQ2=makeQuery(id+"F25.imprint","INTERSECT",VERTEX,{"derivedFrom":[subQ1,subQ0]});Q522=makeQuery(id+"F25.imprint","IMPRINT",FACE,{"disambiguationData":[TD([[makeQuery(id+"F25.imprint","IMPRINT",EDGE,{"disambiguationData":[TD([[subQ2,-1.0]])],"derivedFrom":subQ1}),-1.0]])]});}
            var Q523;
            {var subQ0=sQuery(id+"F25.wireOp",EDGE,"E388.MirrorCS");var subQ1=sQuery(id+"F25.wireOp",EDGE,"E331.MirrorCS");var subQ2=makeQuery(id+"F25.imprint","INTERSECT",VERTEX,{"derivedFrom":[subQ1,subQ0]});Q523=makeQuery(id+"F25.imprint","IMPRINT",FACE,{"disambiguationData":[TD([[makeQuery(id+"F25.imprint","IMPRINT",EDGE,{"disambiguationData":[TD([[subQ2,-1.0]])],"derivedFrom":subQ1}),-1.0]])]});}
            var Q524;
            {var subQ0=sQuery(id+"F25.wireOp",EDGE,"E359.MirrorCS");var subQ1=sQuery(id+"F25.wireOp",EDGE,"E331.MirrorCS");var subQ2=makeQuery(id+"F25.imprint","INTERSECT",VERTEX,{"derivedFrom":[subQ1,subQ0]});Q524=makeQuery(id+"F25.imprint","IMPRINT",FACE,{"disambiguationData":[TD([[makeQuery(id+"F25.imprint","IMPRINT",EDGE,{"disambiguationData":[TD([[subQ2,-1.0]])],"derivedFrom":subQ1}),1.0]])]});}
            var Q525;
            {var subQ0=sQuery(id+"F25.wireOp",EDGE,"E363.MirrorCS");var subQ1=sQuery(id+"F25.wireOp",EDGE,"E342.MirrorCS");var subQ2=makeQuery(id+"F25.imprint","INTERSECT",VERTEX,{"derivedFrom":[subQ1,subQ0]});Q525=makeQuery(id+"F25.imprint","IMPRINT",FACE,{"disambiguationData":[TD([[makeQuery(id+"F25.imprint","IMPRINT",EDGE,{"disambiguationData":[TD([[subQ2,-1.0]])],"derivedFrom":subQ1}),1.0]])]});}
            var Q526;
            {var subQ0=sQuery(id+"F25.wireOp",EDGE,"E363.MirrorCS");var subQ1=sQuery(id+"F25.wireOp",EDGE,"E328.MirrorCS");var subQ2=makeQuery(id+"F25.imprint","INTERSECT",VERTEX,{"derivedFrom":[subQ1,subQ0]});Q526=makeQuery(id+"F25.imprint","IMPRINT",FACE,{"disambiguationData":[TD([[makeQuery(id+"F25.imprint","IMPRINT",EDGE,{"disambiguationData":[TD([[subQ2,-1.0]])],"derivedFrom":subQ1}),1.0]])]});}
            var Q527;
            {var subQ0=sQuery(id+"F25.wireOp",EDGE,"E363.MirrorCS");var subQ1=sQuery(id+"F25.wireOp",EDGE,"E328.MirrorCS");var subQ2=makeQuery(id+"F25.imprint","INTERSECT",VERTEX,{"derivedFrom":[subQ1,subQ0]});Q527=makeQuery(id+"F25.imprint","IMPRINT",FACE,{"disambiguationData":[TD([[makeQuery(id+"F25.imprint","IMPRINT",EDGE,{"disambiguationData":[TD([[subQ2,-1.0]])],"derivedFrom":subQ1}),-1.0]])]});}
            var Q528;
            {var subQ0=sQuery(id+"F25.wireOp",EDGE,"E358.MirrorCS");var subQ1=sQuery(id+"F25.wireOp",EDGE,"E331.MirrorCS");var subQ2=makeQuery(id+"F25.imprint","INTERSECT",VERTEX,{"derivedFrom":[subQ1,subQ0]});Q528=makeQuery(id+"F25.imprint","IMPRINT",FACE,{"disambiguationData":[TD([[makeQuery(id+"F25.imprint","IMPRINT",EDGE,{"disambiguationData":[TD([[subQ2,-1.0]])],"derivedFrom":subQ1}),1.0]])]});}
            var Q529;
            {var subQ0=sQuery(id+"F25.wireOp",EDGE,"E359.MirrorCS");var subQ1=sQuery(id+"F25.wireOp",EDGE,"E331.MirrorCS");var subQ2=makeQuery(id+"F25.imprint","INTERSECT",VERTEX,{"derivedFrom":[subQ1,subQ0]});Q529=makeQuery(id+"F25.imprint","IMPRINT",FACE,{"disambiguationData":[TD([[makeQuery(id+"F25.imprint","IMPRINT",EDGE,{"disambiguationData":[TD([[subQ2,-1.0]])],"derivedFrom":subQ1}),-1.0]])]});}
            var Q530;
            {var subQ0=sQuery(id+"F25.wireOp",EDGE,"E331.MirrorCS");var subQ1=sQuery(id+"F25.wireOp",EDGE,"E342.MirrorCS");var subQ2=makeQuery(id+"F25.imprint","INTERSECT",VERTEX,{"derivedFrom":[subQ1,subQ0]});Q530=makeQuery(id+"F25.imprint","IMPRINT",FACE,{"disambiguationData":[TD([[makeQuery(id+"F25.imprint","IMPRINT",EDGE,{"disambiguationData":[TD([[subQ2,-1.0]])],"derivedFrom":subQ1}),1.0]])]});}
            var Q531;
            {var subQ0=sQuery(id+"F25.wireOp",EDGE,"E331.MirrorCS");var subQ1=sQuery(id+"F25.wireOp",EDGE,"E328.MirrorCS");var subQ2=makeQuery(id+"F25.imprint","INTERSECT",VERTEX,{"derivedFrom":[subQ1,subQ0]});Q531=makeQuery(id+"F25.imprint","IMPRINT",FACE,{"disambiguationData":[TD([[makeQuery(id+"F25.imprint","IMPRINT",EDGE,{"disambiguationData":[TD([[subQ2,-1.0]])],"derivedFrom":subQ1}),1.0]])]});}
            var Q532;
            {var subQ0=sQuery(id+"F25.wireOp",EDGE,"E331.MirrorCS");var subQ1=sQuery(id+"F25.wireOp",EDGE,"E328.MirrorCS");var subQ2=makeQuery(id+"F25.imprint","INTERSECT",VERTEX,{"derivedFrom":[subQ1,subQ0]});Q532=makeQuery(id+"F25.imprint","IMPRINT",FACE,{"disambiguationData":[TD([[makeQuery(id+"F25.imprint","IMPRINT",EDGE,{"disambiguationData":[TD([[subQ2,-1.0]])],"derivedFrom":subQ1}),-1.0]])]});}
            var Q533;
            {var subQ0=sQuery(id+"F25.wireOp",EDGE,"E358.MirrorCS");var subQ1=sQuery(id+"F25.wireOp",EDGE,"E331.MirrorCS");var subQ2=makeQuery(id+"F25.imprint","INTERSECT",VERTEX,{"derivedFrom":[subQ1,subQ0]});Q533=makeQuery(id+"F25.imprint","IMPRINT",FACE,{"disambiguationData":[TD([[makeQuery(id+"F25.imprint","IMPRINT",EDGE,{"disambiguationData":[TD([[subQ2,-1.0]])],"derivedFrom":subQ1}),-1.0]])]});}
            var Q534;
            {var subQ0=sQuery(id+"F25.wireOp",EDGE,"E364.MirrorCS");var subQ1=sQuery(id+"F25.wireOp",EDGE,"E329.MirrorCS");var subQ2=makeQuery(id+"F25.imprint","INTERSECT",VERTEX,{"derivedFrom":[subQ1,subQ0]});Q534=makeQuery(id+"F25.imprint","IMPRINT",FACE,{"disambiguationData":[TD([[makeQuery(id+"F25.imprint","IMPRINT",EDGE,{"disambiguationData":[TD([[subQ2,-1.0]])],"derivedFrom":subQ1}),1.0]])]});}
            var Q535;
            {var subQ0=sQuery(id+"F25.wireOp",EDGE,"E364.MirrorCS");var subQ1=sQuery(id+"F25.wireOp",EDGE,"E329.MirrorCS");var subQ2=makeQuery(id+"F25.imprint","INTERSECT",VERTEX,{"derivedFrom":[subQ1,subQ0]});Q535=makeQuery(id+"F25.imprint","IMPRINT",FACE,{"disambiguationData":[TD([[makeQuery(id+"F25.imprint","IMPRINT",EDGE,{"disambiguationData":[TD([[subQ2,-1.0]])],"derivedFrom":subQ1}),-1.0]])]});}
            var Q536;
            {var subQ0=sQuery(id+"F25.wireOp",EDGE,"E364.MirrorCS");var subQ1=sQuery(id+"F25.wireOp",EDGE,"E354.MirrorCS");var subQ2=makeQuery(id+"F25.imprint","INTERSECT",VERTEX,{"derivedFrom":[subQ1,subQ0]});Q536=makeQuery(id+"F25.imprint","IMPRINT",FACE,{"disambiguationData":[TD([[makeQuery(id+"F25.imprint","IMPRINT",EDGE,{"disambiguationData":[TD([[subQ2,-1.0]])],"derivedFrom":subQ1}),1.0]])]});}
            var Q537;
            {var subQ0=sQuery(id+"F25.wireOp",EDGE,"E388.MirrorCS");var subQ1=sQuery(id+"F25.wireOp",EDGE,"E329.MirrorCS");var subQ2=makeQuery(id+"F25.imprint","INTERSECT",VERTEX,{"derivedFrom":[subQ1,subQ0]});Q537=makeQuery(id+"F25.imprint","IMPRINT",FACE,{"disambiguationData":[TD([[makeQuery(id+"F25.imprint","IMPRINT",EDGE,{"disambiguationData":[TD([[subQ2,-1.0]])],"derivedFrom":subQ1}),-1.0]])]});}
            var Q538;
            {var subQ0=sQuery(id+"F25.wireOp",EDGE,"E388.MirrorCS");var subQ1=sQuery(id+"F25.wireOp",EDGE,"E354.MirrorCS");var subQ2=makeQuery(id+"F25.imprint","INTERSECT",VERTEX,{"derivedFrom":[subQ1,subQ0]});Q538=makeQuery(id+"F25.imprint","IMPRINT",FACE,{"disambiguationData":[TD([[makeQuery(id+"F25.imprint","IMPRINT",EDGE,{"disambiguationData":[TD([[subQ2,-1.0]])],"derivedFrom":subQ1}),1.0]])]});}
            var Q539;
            {var subQ0=sQuery(id+"F25.wireOp",EDGE,"E359.MirrorCS");var subQ1=sQuery(id+"F25.wireOp",EDGE,"E329.MirrorCS");var subQ2=makeQuery(id+"F25.imprint","INTERSECT",VERTEX,{"derivedFrom":[subQ1,subQ0]});Q539=makeQuery(id+"F25.imprint","IMPRINT",FACE,{"disambiguationData":[TD([[makeQuery(id+"F25.imprint","IMPRINT",EDGE,{"disambiguationData":[TD([[subQ2,-1.0]])],"derivedFrom":subQ1}),-1.0]])]});}
            var Q540;
            {var subQ0=sQuery(id+"F25.wireOp",EDGE,"E359.MirrorCS");var subQ1=sQuery(id+"F25.wireOp",EDGE,"E354.MirrorCS");var subQ2=makeQuery(id+"F25.imprint","INTERSECT",VERTEX,{"derivedFrom":[subQ1,subQ0]});Q540=makeQuery(id+"F25.imprint","IMPRINT",FACE,{"disambiguationData":[TD([[makeQuery(id+"F25.imprint","IMPRINT",EDGE,{"disambiguationData":[TD([[subQ2,-1.0]])],"derivedFrom":subQ1}),1.0]])]});}
            var Q541;
            {var subQ0=sQuery(id+"F25.wireOp",EDGE,"E342.MirrorCS");var subQ1=sQuery(id+"F25.wireOp",EDGE,"E329.MirrorCS");var subQ2=makeQuery(id+"F25.imprint","INTERSECT",VERTEX,{"derivedFrom":[subQ1,subQ0]});Q541=makeQuery(id+"F25.imprint","IMPRINT",FACE,{"disambiguationData":[TD([[makeQuery(id+"F25.imprint","IMPRINT",EDGE,{"disambiguationData":[TD([[subQ2,-1.0]])],"derivedFrom":subQ1}),-1.0]])]});}
            var Q542;
            {var subQ0=sQuery(id+"F25.wireOp",EDGE,"E345.MirrorCS");var subQ1=sQuery(id+"F25.wireOp",EDGE,"E342.MirrorCS");var subQ2=makeQuery(id+"F25.imprint","INTERSECT",VERTEX,{"derivedFrom":[subQ1,subQ0]});Q542=makeQuery(id+"F25.imprint","IMPRINT",FACE,{"disambiguationData":[TD([[makeQuery(id+"F25.imprint","IMPRINT",EDGE,{"disambiguationData":[TD([[subQ2,-1.0]])],"derivedFrom":subQ1}),1.0]])]});}
            var Q543;
            {var subQ0=sQuery(id+"F25.wireOp",EDGE,"E329.MirrorCS");var subQ1=sQuery(id+"F25.wireOp",EDGE,"E328.MirrorCS");var subQ2=makeQuery(id+"F25.imprint","INTERSECT",VERTEX,{"derivedFrom":[subQ1,subQ0]});Q543=makeQuery(id+"F25.imprint","IMPRINT",FACE,{"disambiguationData":[TD([[makeQuery(id+"F25.imprint","IMPRINT",EDGE,{"disambiguationData":[TD([[subQ2,-1.0]])],"derivedFrom":subQ1}),1.0]])]});}
            var Q544;
            {var subQ0=sQuery(id+"F25.wireOp",EDGE,"E345.MirrorCS");var subQ1=sQuery(id+"F25.wireOp",EDGE,"E328.MirrorCS");var subQ2=makeQuery(id+"F25.imprint","INTERSECT",VERTEX,{"derivedFrom":[subQ1,subQ0]});Q544=makeQuery(id+"F25.imprint","IMPRINT",FACE,{"disambiguationData":[TD([[makeQuery(id+"F25.imprint","IMPRINT",EDGE,{"disambiguationData":[TD([[subQ2,-1.0]])],"derivedFrom":subQ1}),1.0]])]});}
            var Q545;
            {var subQ0=sQuery(id+"F25.wireOp",EDGE,"E329.MirrorCS");var subQ1=sQuery(id+"F25.wireOp",EDGE,"E328.MirrorCS");var subQ2=makeQuery(id+"F25.imprint","INTERSECT",VERTEX,{"derivedFrom":[subQ1,subQ0]});Q545=makeQuery(id+"F25.imprint","IMPRINT",FACE,{"disambiguationData":[TD([[makeQuery(id+"F25.imprint","IMPRINT",EDGE,{"disambiguationData":[TD([[subQ2,-1.0]])],"derivedFrom":subQ1}),-1.0]])]});}
            var Q546;
            {var subQ0=sQuery(id+"F25.wireOp",EDGE,"E345.MirrorCS");var subQ1=sQuery(id+"F25.wireOp",EDGE,"E328.MirrorCS");var subQ2=makeQuery(id+"F25.imprint","INTERSECT",VERTEX,{"derivedFrom":[subQ1,subQ0]});Q546=makeQuery(id+"F25.imprint","IMPRINT",FACE,{"disambiguationData":[TD([[makeQuery(id+"F25.imprint","IMPRINT",EDGE,{"disambiguationData":[TD([[subQ2,-1.0]])],"derivedFrom":subQ1}),-1.0]])]});}
            var Q547;
            {var subQ0=sQuery(id+"F25.wireOp",EDGE,"E358.MirrorCS");var subQ1=sQuery(id+"F25.wireOp",EDGE,"E329.MirrorCS");var subQ2=makeQuery(id+"F25.imprint","INTERSECT",VERTEX,{"derivedFrom":[subQ1,subQ0]});Q547=makeQuery(id+"F25.imprint","IMPRINT",FACE,{"disambiguationData":[TD([[makeQuery(id+"F25.imprint","IMPRINT",EDGE,{"disambiguationData":[TD([[subQ2,-1.0]])],"derivedFrom":subQ1}),-1.0]])]});}
            var Q548;
            {var subQ0=sQuery(id+"F25.wireOp",EDGE,"E358.MirrorCS");var subQ1=sQuery(id+"F25.wireOp",EDGE,"E354.MirrorCS");var subQ2=makeQuery(id+"F25.imprint","INTERSECT",VERTEX,{"derivedFrom":[subQ1,subQ0]});Q548=makeQuery(id+"F25.imprint","IMPRINT",FACE,{"disambiguationData":[TD([[makeQuery(id+"F25.imprint","IMPRINT",EDGE,{"disambiguationData":[TD([[subQ2,-1.0]])],"derivedFrom":subQ1}),1.0]])]});}
            var Q549;
            {var subQ0=sQuery(id+"F25.wireOp",EDGE,"E358.MirrorCS");var subQ1=sQuery(id+"F25.wireOp",EDGE,"E354.MirrorCS");var subQ2=makeQuery(id+"F25.imprint","INTERSECT",VERTEX,{"derivedFrom":[subQ1,subQ0]});Q549=makeQuery(id+"F25.imprint","IMPRINT",FACE,{"disambiguationData":[TD([[makeQuery(id+"F25.imprint","IMPRINT",EDGE,{"disambiguationData":[TD([[subQ2,-1.0]])],"derivedFrom":subQ1}),-1.0]])]});}
            var Q550;
            {var subQ0=sQuery(id+"F25.wireOp",EDGE,"E384.MirrorCS");var subQ1=sQuery(id+"F25.wireOp",EDGE,"E358.MirrorCS");var subQ2=makeQuery(id+"F25.imprint","INTERSECT",VERTEX,{"derivedFrom":[subQ1,subQ0]});Q550=makeQuery(id+"F25.imprint","IMPRINT",FACE,{"disambiguationData":[TD([[makeQuery(id+"F25.imprint","IMPRINT",EDGE,{"disambiguationData":[TD([[subQ2,-1.0]])],"derivedFrom":subQ1}),1.0]])]});}
            var Q551;
            {var subQ0=sQuery(id+"F25.wireOp",EDGE,"E373.MirrorCS");var subQ1=sQuery(id+"F25.wireOp",EDGE,"E342.MirrorCS");var subQ2=makeQuery(id+"F25.imprint","INTERSECT",VERTEX,{"derivedFrom":[subQ1,subQ0]});Q551=makeQuery(id+"F25.imprint","IMPRINT",FACE,{"disambiguationData":[TD([[makeQuery(id+"F25.imprint","IMPRINT",EDGE,{"disambiguationData":[TD([[subQ2,-1.0]])],"derivedFrom":subQ1}),1.0]])]});}
            var Q552;
            {var subQ0=sQuery(id+"F25.wireOp",EDGE,"E344.MirrorCS");var subQ1=sQuery(id+"F25.wireOp",EDGE,"E342.MirrorCS");var subQ2=makeQuery(id+"F25.imprint","INTERSECT",VERTEX,{"derivedFrom":[subQ1,subQ0]});Q552=makeQuery(id+"F25.imprint","IMPRINT",FACE,{"disambiguationData":[TD([[makeQuery(id+"F25.imprint","IMPRINT",EDGE,{"disambiguationData":[TD([[subQ2,-1.0]])],"derivedFrom":subQ1}),1.0]])]});}
            var Q553;
            {var subQ0=sQuery(id+"F25.wireOp",EDGE,"E344.MirrorCS");var subQ1=sQuery(id+"F25.wireOp",EDGE,"E328.MirrorCS");var subQ2=makeQuery(id+"F25.imprint","INTERSECT",VERTEX,{"derivedFrom":[subQ1,subQ0]});Q553=makeQuery(id+"F25.imprint","IMPRINT",FACE,{"disambiguationData":[TD([[makeQuery(id+"F25.imprint","IMPRINT",EDGE,{"disambiguationData":[TD([[subQ2,-1.0]])],"derivedFrom":subQ1}),1.0]])]});}
            var Q554;
            {var subQ0=sQuery(id+"F25.wireOp",EDGE,"E344.MirrorCS");var subQ1=sQuery(id+"F25.wireOp",EDGE,"E328.MirrorCS");var subQ2=makeQuery(id+"F25.imprint","INTERSECT",VERTEX,{"derivedFrom":[subQ1,subQ0]});Q554=makeQuery(id+"F25.imprint","IMPRINT",FACE,{"disambiguationData":[TD([[makeQuery(id+"F25.imprint","IMPRINT",EDGE,{"disambiguationData":[TD([[subQ2,-1.0]])],"derivedFrom":subQ1}),-1.0]])]});}
            var Q555;
            {var subQ0=sQuery(id+"F25.wireOp",EDGE,"E344.MirrorCS");var subQ1=sQuery(id+"F25.wireOp",EDGE,"E358.MirrorCS");var subQ2=makeQuery(id+"F25.imprint","INTERSECT",VERTEX,{"derivedFrom":[subQ1,subQ0]});Q555=makeQuery(id+"F25.imprint","IMPRINT",FACE,{"disambiguationData":[TD([[makeQuery(id+"F25.imprint","IMPRINT",EDGE,{"disambiguationData":[TD([[subQ2,-1.0]])],"derivedFrom":subQ1}),1.0]])]});}
            var Q556;
            {var subQ0=sQuery(id+"F25.wireOp",EDGE,"E378.MirrorCS");var subQ1=sQuery(id+"F25.wireOp",EDGE,"E342.MirrorCS");var subQ2=makeQuery(id+"F25.imprint","INTERSECT",VERTEX,{"derivedFrom":[subQ1,subQ0]});Q556=makeQuery(id+"F25.imprint","IMPRINT",FACE,{"disambiguationData":[TD([[makeQuery(id+"F25.imprint","IMPRINT",EDGE,{"disambiguationData":[TD([[subQ2,-1.0]])],"derivedFrom":subQ1}),1.0]])]});}
            var Q557;
            {var subQ0=sQuery(id+"F25.wireOp",EDGE,"E378.MirrorCS");var subQ1=sQuery(id+"F25.wireOp",EDGE,"E328.MirrorCS");var subQ2=makeQuery(id+"F25.imprint","INTERSECT",VERTEX,{"derivedFrom":[subQ1,subQ0]});Q557=makeQuery(id+"F25.imprint","IMPRINT",FACE,{"disambiguationData":[TD([[makeQuery(id+"F25.imprint","IMPRINT",EDGE,{"disambiguationData":[TD([[subQ2,-1.0]])],"derivedFrom":subQ1}),1.0]])]});}
            var Q558;
            {var subQ0=sQuery(id+"F25.wireOp",EDGE,"E378.MirrorCS");var subQ1=sQuery(id+"F25.wireOp",EDGE,"E328.MirrorCS");var subQ2=makeQuery(id+"F25.imprint","INTERSECT",VERTEX,{"derivedFrom":[subQ1,subQ0]});Q558=makeQuery(id+"F25.imprint","IMPRINT",FACE,{"disambiguationData":[TD([[makeQuery(id+"F25.imprint","IMPRINT",EDGE,{"disambiguationData":[TD([[subQ2,-1.0]])],"derivedFrom":subQ1}),-1.0]])]});}
            var Q559;
            {var subQ0=sQuery(id+"F25.wireOp",EDGE,"E378.MirrorCS");var subQ1=sQuery(id+"F25.wireOp",EDGE,"E358.MirrorCS");var subQ2=makeQuery(id+"F25.imprint","INTERSECT",VERTEX,{"derivedFrom":[subQ1,subQ0]});Q559=makeQuery(id+"F25.imprint","IMPRINT",FACE,{"disambiguationData":[TD([[makeQuery(id+"F25.imprint","IMPRINT",EDGE,{"disambiguationData":[TD([[subQ2,-1.0]])],"derivedFrom":subQ1}),1.0]])]});}
            var Q560;
            {var subQ0=sQuery(id+"F25.wireOp",EDGE,"E348.MirrorCS");var subQ1=sQuery(id+"F25.wireOp",EDGE,"E358.MirrorCS");var subQ2=makeQuery(id+"F25.imprint","INTERSECT",VERTEX,{"derivedFrom":[subQ1,subQ0]});Q560=makeQuery(id+"F25.imprint","IMPRINT",FACE,{"disambiguationData":[TD([[makeQuery(id+"F25.imprint","IMPRINT",EDGE,{"disambiguationData":[TD([[subQ2,-1.0]])],"derivedFrom":subQ1}),1.0]])]});}
            var Q561;
            {var subQ0=sQuery(id+"F25.wireOp",EDGE,"E358.MirrorCS");var subQ1=sQuery(id+"F25.wireOp",EDGE,"E335.MirrorCS");var subQ2=makeQuery(id+"F25.imprint","INTERSECT",VERTEX,{"derivedFrom":[subQ1,subQ0]});Q561=makeQuery(id+"F25.imprint","IMPRINT",FACE,{"disambiguationData":[TD([[makeQuery(id+"F25.imprint","IMPRINT",EDGE,{"disambiguationData":[TD([[subQ2,-1.0]])],"derivedFrom":subQ1}),1.0]])]});}
            var Q562;
            {var subQ0=sQuery(id+"F25.wireOp",EDGE,"E358.MirrorCS");var subQ1=sQuery(id+"F25.wireOp",EDGE,"E335.MirrorCS");var subQ2=makeQuery(id+"F25.imprint","INTERSECT",VERTEX,{"derivedFrom":[subQ1,subQ0]});Q562=makeQuery(id+"F25.imprint","IMPRINT",FACE,{"disambiguationData":[TD([[makeQuery(id+"F25.imprint","IMPRINT",EDGE,{"disambiguationData":[TD([[subQ2,-1.0]])],"derivedFrom":subQ1}),-1.0]])]});}
            var Q563;
            {var subQ0=sQuery(id+"F25.wireOp",EDGE,"E393.MirrorCS");var subQ1=sQuery(id+"F25.wireOp",EDGE,"E335.MirrorCS");var subQ2=makeQuery(id+"F25.imprint","INTERSECT",VERTEX,{"derivedFrom":[subQ1,subQ0]});Q563=makeQuery(id+"F25.imprint","IMPRINT",FACE,{"disambiguationData":[TD([[makeQuery(id+"F25.imprint","IMPRINT",EDGE,{"disambiguationData":[TD([[subQ2,-1.0]])],"derivedFrom":subQ1}),-1.0]])]});}
            var Q564;
            {var subQ0=sQuery(id+"F25.wireOp",EDGE,"E335.MirrorCS");var subQ1=sQuery(id+"F25.wireOp",EDGE,"E326.MirrorCS");var subQ2=makeQuery(id+"F25.imprint","INTERSECT",VERTEX,{"derivedFrom":[subQ1,subQ0]});Q564=makeQuery(id+"F25.imprint","IMPRINT",FACE,{"disambiguationData":[TD([[makeQuery(id+"F25.imprint","IMPRINT",EDGE,{"disambiguationData":[TD([[subQ2,-1.0]])],"derivedFrom":subQ1}),1.0]])]});}
            var Q565;
            {var subQ0=sQuery(id+"F25.wireOp",EDGE,"E394.MirrorCS");var subQ1=sQuery(id+"F25.wireOp",EDGE,"E335.MirrorCS");var subQ2=makeQuery(id+"F25.imprint","INTERSECT",VERTEX,{"derivedFrom":[subQ1,subQ0]});Q565=makeQuery(id+"F25.imprint","IMPRINT",FACE,{"disambiguationData":[TD([[makeQuery(id+"F25.imprint","IMPRINT",EDGE,{"disambiguationData":[TD([[subQ2,-1.0]])],"derivedFrom":subQ1}),-1.0]])]});}
            var Q566;
            {var subQ0=sQuery(id+"F25.wireOp",EDGE,"E360.MirrorCS");var subQ1=sQuery(id+"F25.wireOp",EDGE,"E335.MirrorCS");var subQ2=makeQuery(id+"F25.imprint","INTERSECT",VERTEX,{"derivedFrom":[subQ1,subQ0]});Q566=makeQuery(id+"F25.imprint","IMPRINT",FACE,{"disambiguationData":[TD([[makeQuery(id+"F25.imprint","IMPRINT",EDGE,{"disambiguationData":[TD([[subQ2,-1.0]])],"derivedFrom":subQ1}),-1.0]])]});}
            var Q567;
            {var subQ0=sQuery(id+"F25.wireOp",EDGE,"E336.MirrorCS");var subQ1=sQuery(id+"F25.wireOp",EDGE,"E335.MirrorCS");var subQ2=makeQuery(id+"F25.imprint","INTERSECT",VERTEX,{"derivedFrom":[subQ1,subQ0]});Q567=makeQuery(id+"F25.imprint","IMPRINT",FACE,{"disambiguationData":[TD([[makeQuery(id+"F25.imprint","IMPRINT",EDGE,{"disambiguationData":[TD([[subQ2,-1.0]])],"derivedFrom":subQ1}),-1.0]])]});}
            var Q568;
            {var subQ0=sQuery(id+"F25.wireOp",EDGE,"E383.MirrorCS");var subQ1=sQuery(id+"F25.wireOp",EDGE,"E335.MirrorCS");var subQ2=makeQuery(id+"F25.imprint","INTERSECT",VERTEX,{"derivedFrom":[subQ1,subQ0]});Q568=makeQuery(id+"F25.imprint","IMPRINT",FACE,{"disambiguationData":[TD([[makeQuery(id+"F25.imprint","IMPRINT",EDGE,{"disambiguationData":[TD([[subQ2,-1.0]])],"derivedFrom":subQ1}),-1.0]])]});}
            var Q569;
            {var subQ0=sQuery(id+"F25.wireOp",EDGE,"E350.MirrorCS");var subQ1=sQuery(id+"F25.wireOp",EDGE,"E335.MirrorCS");var subQ2=makeQuery(id+"F25.imprint","INTERSECT",VERTEX,{"derivedFrom":[subQ1,subQ0]});Q569=makeQuery(id+"F25.imprint","IMPRINT",FACE,{"disambiguationData":[TD([[makeQuery(id+"F25.imprint","IMPRINT",EDGE,{"disambiguationData":[TD([[subQ2,-1.0]])],"derivedFrom":subQ1}),-1.0]])]});}
            var Q570;
            {var subQ0=sQuery(id+"F25.wireOp",EDGE,"E383.MirrorCS");var subQ1=sQuery(id+"F25.wireOp",EDGE,"E335.MirrorCS");var subQ2=makeQuery(id+"F25.imprint","INTERSECT",VERTEX,{"derivedFrom":[subQ1,subQ0]});Q570=makeQuery(id+"F25.imprint","IMPRINT",FACE,{"disambiguationData":[TD([[makeQuery(id+"F25.imprint","IMPRINT",EDGE,{"disambiguationData":[TD([[subQ2,-1.0]])],"derivedFrom":subQ1}),1.0]])]});}
            var Q571;
            {var subQ0=sQuery(id+"F25.wireOp",EDGE,"E350.MirrorCS");var subQ1=sQuery(id+"F25.wireOp",EDGE,"E335.MirrorCS");var subQ2=makeQuery(id+"F25.imprint","INTERSECT",VERTEX,{"derivedFrom":[subQ1,subQ0]});Q571=makeQuery(id+"F25.imprint","IMPRINT",FACE,{"disambiguationData":[TD([[makeQuery(id+"F25.imprint","IMPRINT",EDGE,{"disambiguationData":[TD([[subQ2,-1.0]])],"derivedFrom":subQ1}),1.0]])]});}
            var Q572;
            {var subQ0=sQuery(id+"F25.wireOp",EDGE,"E350.MirrorCS");var subQ1=sQuery(id+"F25.wireOp",EDGE,"E344.MirrorCS");var subQ2=makeQuery(id+"F25.imprint","INTERSECT",VERTEX,{"derivedFrom":[subQ1,subQ0]});Q572=makeQuery(id+"F25.imprint","IMPRINT",FACE,{"disambiguationData":[TD([[makeQuery(id+"F25.imprint","IMPRINT",EDGE,{"disambiguationData":[TD([[subQ2,-1.0]])],"derivedFrom":subQ1}),1.0]])]});}
            var Q573;
            {var subQ0=sQuery(id+"F25.wireOp",EDGE,"E383.MirrorCS");var subQ1=sQuery(id+"F25.wireOp",EDGE,"E344.MirrorCS");var subQ2=makeQuery(id+"F25.imprint","INTERSECT",VERTEX,{"derivedFrom":[subQ1,subQ0]});Q573=makeQuery(id+"F25.imprint","IMPRINT",FACE,{"disambiguationData":[TD([[makeQuery(id+"F25.imprint","IMPRINT",EDGE,{"disambiguationData":[TD([[subQ2,-1.0]])],"derivedFrom":subQ1}),1.0]])]});}
            var Q574;
            {var subQ0=sQuery(id+"F25.wireOp",EDGE,"E350.MirrorCS");var subQ1=sQuery(id+"F25.wireOp",EDGE,"E344.MirrorCS");var subQ2=makeQuery(id+"F25.imprint","INTERSECT",VERTEX,{"derivedFrom":[subQ1,subQ0]});Q574=makeQuery(id+"F25.imprint","IMPRINT",FACE,{"disambiguationData":[TD([[makeQuery(id+"F25.imprint","IMPRINT",EDGE,{"disambiguationData":[TD([[subQ2,-1.0]])],"derivedFrom":subQ1}),-1.0]])]});}
            var Q575;
            {var subQ0=sQuery(id+"F25.wireOp",EDGE,"E383.MirrorCS");var subQ1=sQuery(id+"F25.wireOp",EDGE,"E344.MirrorCS");var subQ2=makeQuery(id+"F25.imprint","INTERSECT",VERTEX,{"derivedFrom":[subQ1,subQ0]});Q575=makeQuery(id+"F25.imprint","IMPRINT",FACE,{"disambiguationData":[TD([[makeQuery(id+"F25.imprint","IMPRINT",EDGE,{"disambiguationData":[TD([[subQ2,-1.0]])],"derivedFrom":subQ1}),-1.0]])]});}
            var Q576;
            {var subQ0=sQuery(id+"F25.wireOp",EDGE,"E373.MirrorCS");var subQ1=sQuery(id+"F25.wireOp",EDGE,"E350.MirrorCS");var subQ2=makeQuery(id+"F25.imprint","INTERSECT",VERTEX,{"derivedFrom":[subQ1,subQ0]});Q576=makeQuery(id+"F25.imprint","IMPRINT",FACE,{"disambiguationData":[TD([[makeQuery(id+"F25.imprint","IMPRINT",EDGE,{"disambiguationData":[TD([[subQ2,-1.0]])],"derivedFrom":subQ1}),1.0]])]});}
            var Q577;
            {var subQ0=sQuery(id+"F25.wireOp",EDGE,"E373.MirrorCS");var subQ1=sQuery(id+"F25.wireOp",EDGE,"E350.MirrorCS");var subQ2=makeQuery(id+"F25.imprint","INTERSECT",VERTEX,{"derivedFrom":[subQ1,subQ0]});Q577=makeQuery(id+"F25.imprint","IMPRINT",FACE,{"disambiguationData":[TD([[makeQuery(id+"F25.imprint","IMPRINT",EDGE,{"disambiguationData":[TD([[subQ2,-1.0]])],"derivedFrom":subQ1}),-1.0]])]});}
            var Q578;
            {var subQ0=sQuery(id+"F25.wireOp",EDGE,"E360.MirrorCS");var subQ1=sQuery(id+"F25.wireOp",EDGE,"E335.MirrorCS");var subQ2=makeQuery(id+"F25.imprint","INTERSECT",VERTEX,{"derivedFrom":[subQ1,subQ0]});Q578=makeQuery(id+"F25.imprint","IMPRINT",FACE,{"disambiguationData":[TD([[makeQuery(id+"F25.imprint","IMPRINT",EDGE,{"disambiguationData":[TD([[subQ2,-1.0]])],"derivedFrom":subQ1}),1.0]])]});}
            var Q579;
            {var subQ0=sQuery(id+"F25.wireOp",EDGE,"E394.MirrorCS");var subQ1=sQuery(id+"F25.wireOp",EDGE,"E335.MirrorCS");var subQ2=makeQuery(id+"F25.imprint","INTERSECT",VERTEX,{"derivedFrom":[subQ1,subQ0]});Q579=makeQuery(id+"F25.imprint","IMPRINT",FACE,{"disambiguationData":[TD([[makeQuery(id+"F25.imprint","IMPRINT",EDGE,{"disambiguationData":[TD([[subQ2,-1.0]])],"derivedFrom":subQ1}),1.0]])]});}
            var Q580;
            {var subQ0=sQuery(id+"F25.wireOp",EDGE,"E350.MirrorCS");var subQ1=sQuery(id+"F25.wireOp",EDGE,"E348.MirrorCS");var subQ2=makeQuery(id+"F25.imprint","INTERSECT",VERTEX,{"derivedFrom":[subQ1,subQ0]});Q580=makeQuery(id+"F25.imprint","IMPRINT",FACE,{"disambiguationData":[TD([[makeQuery(id+"F25.imprint","IMPRINT",EDGE,{"disambiguationData":[TD([[subQ2,-1.0]])],"derivedFrom":subQ1}),-1.0]])]});}
            var Q581;
            {var subQ0=sQuery(id+"F25.wireOp",EDGE,"E383.MirrorCS");var subQ1=sQuery(id+"F25.wireOp",EDGE,"E348.MirrorCS");var subQ2=makeQuery(id+"F25.imprint","INTERSECT",VERTEX,{"derivedFrom":[subQ1,subQ0]});Q581=makeQuery(id+"F25.imprint","IMPRINT",FACE,{"disambiguationData":[TD([[makeQuery(id+"F25.imprint","IMPRINT",EDGE,{"disambiguationData":[TD([[subQ2,-1.0]])],"derivedFrom":subQ1}),-1.0]])]});}
            var Q582;
            {var subQ0=sQuery(id+"F25.wireOp",EDGE,"E383.MirrorCS");var subQ1=sQuery(id+"F25.wireOp",EDGE,"E348.MirrorCS");var subQ2=makeQuery(id+"F25.imprint","INTERSECT",VERTEX,{"derivedFrom":[subQ1,subQ0]});Q582=makeQuery(id+"F25.imprint","IMPRINT",FACE,{"disambiguationData":[TD([[makeQuery(id+"F25.imprint","IMPRINT",EDGE,{"disambiguationData":[TD([[subQ2,-1.0]])],"derivedFrom":subQ1}),1.0]])]});}
            var Q583;
            {var subQ0=sQuery(id+"F25.wireOp",EDGE,"E350.MirrorCS");var subQ1=sQuery(id+"F25.wireOp",EDGE,"E348.MirrorCS");var subQ2=makeQuery(id+"F25.imprint","INTERSECT",VERTEX,{"derivedFrom":[subQ1,subQ0]});Q583=makeQuery(id+"F25.imprint","IMPRINT",FACE,{"disambiguationData":[TD([[makeQuery(id+"F25.imprint","IMPRINT",EDGE,{"disambiguationData":[TD([[subQ2,-1.0]])],"derivedFrom":subQ1}),1.0]])]});}
            var Q584;
            {var subQ0=sQuery(id+"F25.wireOp",EDGE,"E310.MirrorCS");Q584=makeQuery(id+"F25.imprint","IMPRINT",FACE,{"disambiguationData":[TD([[makeQuery(id+"F25.imprint","IMPRINT",EDGE,{"derivedFrom":subQ0}),-1.0]])]});}
            var Q585;
            {var subQ0=sQuery(id+"F25.wireOp",EDGE,"E384.MirrorCS");var subQ1=sQuery(id+"F25.wireOp",EDGE,"E351.MirrorCS");var subQ2=makeQuery(id+"F25.imprint","INTERSECT",VERTEX,{"derivedFrom":[subQ1,subQ0]});Q585=makeQuery(id+"F25.imprint","IMPRINT",FACE,{"disambiguationData":[TD([[makeQuery(id+"F25.imprint","IMPRINT",EDGE,{"disambiguationData":[TD([[subQ2,-1.0]])],"derivedFrom":subQ1}),1.0]])]});}
            var Q586;
            {var subQ0=sQuery(id+"F25.wireOp",EDGE,"E384.MirrorCS");var subQ1=sQuery(id+"F25.wireOp",EDGE,"E326.MirrorCS");var subQ2=makeQuery(id+"F25.imprint","INTERSECT",VERTEX,{"derivedFrom":[subQ1,subQ0]});Q586=makeQuery(id+"F25.imprint","IMPRINT",FACE,{"disambiguationData":[TD([[makeQuery(id+"F25.imprint","IMPRINT",EDGE,{"disambiguationData":[TD([[subQ2,-1.0]])],"derivedFrom":subQ1}),-1.0]])]});}
            var Q587;
            {var subQ0=sQuery(id+"F25.wireOp",EDGE,"E344.MirrorCS");var subQ1=sQuery(id+"F25.wireOp",EDGE,"E326.MirrorCS");var subQ2=makeQuery(id+"F25.imprint","INTERSECT",VERTEX,{"derivedFrom":[subQ1,subQ0]});Q587=makeQuery(id+"F25.imprint","IMPRINT",FACE,{"disambiguationData":[TD([[makeQuery(id+"F25.imprint","IMPRINT",EDGE,{"disambiguationData":[TD([[subQ2,-1.0]])],"derivedFrom":subQ1}),-1.0]])]});}
            var Q588;
            {var subQ0=sQuery(id+"F25.wireOp",EDGE,"E373.MirrorCS");var subQ1=sQuery(id+"F25.wireOp",EDGE,"E326.MirrorCS");var subQ2=makeQuery(id+"F25.imprint","INTERSECT",VERTEX,{"derivedFrom":[subQ1,subQ0]});Q588=makeQuery(id+"F25.imprint","IMPRINT",FACE,{"disambiguationData":[TD([[makeQuery(id+"F25.imprint","IMPRINT",EDGE,{"disambiguationData":[TD([[subQ2,-1.0]])],"derivedFrom":subQ1}),-1.0]])]});}
            var Q589;
            {var subQ0=sQuery(id+"F25.wireOp",EDGE,"E378.MirrorCS");var subQ1=sQuery(id+"F25.wireOp",EDGE,"E326.MirrorCS");var subQ2=makeQuery(id+"F25.imprint","INTERSECT",VERTEX,{"derivedFrom":[subQ1,subQ0]});Q589=makeQuery(id+"F25.imprint","IMPRINT",FACE,{"disambiguationData":[TD([[makeQuery(id+"F25.imprint","IMPRINT",EDGE,{"disambiguationData":[TD([[subQ2,-1.0]])],"derivedFrom":subQ1}),-1.0]])]});}
            var Q590;
            {var subQ0=sQuery(id+"F25.wireOp",EDGE,"E348.MirrorCS");var subQ1=sQuery(id+"F25.wireOp",EDGE,"E326.MirrorCS");var subQ2=makeQuery(id+"F25.imprint","INTERSECT",VERTEX,{"derivedFrom":[subQ1,subQ0]});Q590=makeQuery(id+"F25.imprint","IMPRINT",FACE,{"disambiguationData":[TD([[makeQuery(id+"F25.imprint","IMPRINT",EDGE,{"disambiguationData":[TD([[subQ2,-1.0]])],"derivedFrom":subQ1}),-1.0]])]});}
            var Q591;
            {var subQ0=sQuery(id+"F25.wireOp",EDGE,"E369.MirrorCS");var subQ1=sQuery(id+"F25.wireOp",EDGE,"E326.MirrorCS");var subQ2=makeQuery(id+"F25.imprint","INTERSECT",VERTEX,{"derivedFrom":[subQ1,subQ0]});Q591=makeQuery(id+"F25.imprint","IMPRINT",FACE,{"disambiguationData":[TD([[makeQuery(id+"F25.imprint","IMPRINT",EDGE,{"disambiguationData":[TD([[subQ2,-1.0]])],"derivedFrom":subQ1}),-1.0]])]});}
            var Q592;
            {var subQ0=sQuery(id+"F25.wireOp",EDGE,"E335.MirrorCS");var subQ1=sQuery(id+"F25.wireOp",EDGE,"E326.MirrorCS");var subQ2=makeQuery(id+"F25.imprint","INTERSECT",VERTEX,{"derivedFrom":[subQ1,subQ0]});Q592=makeQuery(id+"F25.imprint","IMPRINT",FACE,{"disambiguationData":[TD([[makeQuery(id+"F25.imprint","IMPRINT",EDGE,{"disambiguationData":[TD([[subQ2,-1.0]])],"derivedFrom":subQ1}),-1.0]])]});}
            var Q593;
            {var subQ0=sQuery(id+"F25.wireOp",EDGE,"E394.MirrorCS");var subQ1=sQuery(id+"F25.wireOp",EDGE,"E348.MirrorCS");var subQ2=makeQuery(id+"F25.imprint","INTERSECT",VERTEX,{"derivedFrom":[subQ1,subQ0]});Q593=makeQuery(id+"F25.imprint","IMPRINT",FACE,{"disambiguationData":[TD([[makeQuery(id+"F25.imprint","IMPRINT",EDGE,{"disambiguationData":[TD([[subQ2,-1.0]])],"derivedFrom":subQ1}),-1.0]])]});}
            var Q594;
            {var subQ0=sQuery(id+"F25.wireOp",EDGE,"E348.MirrorCS");var subQ1=sQuery(id+"F25.wireOp",EDGE,"E336.MirrorCS");var subQ2=makeQuery(id+"F25.imprint","INTERSECT",VERTEX,{"derivedFrom":[subQ1,subQ0]});Q594=makeQuery(id+"F25.imprint","IMPRINT",FACE,{"disambiguationData":[TD([[makeQuery(id+"F25.imprint","IMPRINT",EDGE,{"disambiguationData":[TD([[subQ2,-1.0]])],"derivedFrom":subQ1}),-1.0]])]});}
            var Q595;
            {var subQ0=sQuery(id+"F25.wireOp",EDGE,"E378.MirrorCS");var subQ1=sQuery(id+"F25.wireOp",EDGE,"E336.MirrorCS");var subQ2=makeQuery(id+"F25.imprint","INTERSECT",VERTEX,{"derivedFrom":[subQ1,subQ0]});Q595=makeQuery(id+"F25.imprint","IMPRINT",FACE,{"disambiguationData":[TD([[makeQuery(id+"F25.imprint","IMPRINT",EDGE,{"disambiguationData":[TD([[subQ2,-1.0]])],"derivedFrom":subQ1}),-1.0]])]});}
            var Q596;
            {var subQ0=sQuery(id+"F25.wireOp",EDGE,"E394.MirrorCS");var subQ1=sQuery(id+"F25.wireOp",EDGE,"E348.MirrorCS");var subQ2=makeQuery(id+"F25.imprint","INTERSECT",VERTEX,{"derivedFrom":[subQ1,subQ0]});Q596=makeQuery(id+"F25.imprint","IMPRINT",FACE,{"disambiguationData":[TD([[makeQuery(id+"F25.imprint","IMPRINT",EDGE,{"disambiguationData":[TD([[subQ2,-1.0]])],"derivedFrom":subQ1}),1.0]])]});}
            var Q597;
            {var subQ0=sQuery(id+"F25.wireOp",EDGE,"E394.MirrorCS");var subQ1=sQuery(id+"F25.wireOp",EDGE,"E373.MirrorCS");var subQ2=makeQuery(id+"F25.imprint","INTERSECT",VERTEX,{"derivedFrom":[subQ1,subQ0]});Q597=makeQuery(id+"F25.imprint","IMPRINT",FACE,{"disambiguationData":[TD([[makeQuery(id+"F25.imprint","IMPRINT",EDGE,{"disambiguationData":[TD([[subQ2,-1.0]])],"derivedFrom":subQ1}),-1.0]])]});}
            var Q598;
            {var subQ0=sQuery(id+"F25.wireOp",EDGE,"E373.MirrorCS");var subQ1=sQuery(id+"F25.wireOp",EDGE,"E336.MirrorCS");var subQ2=makeQuery(id+"F25.imprint","INTERSECT",VERTEX,{"derivedFrom":[subQ1,subQ0]});Q598=makeQuery(id+"F25.imprint","IMPRINT",FACE,{"disambiguationData":[TD([[makeQuery(id+"F25.imprint","IMPRINT",EDGE,{"disambiguationData":[TD([[subQ2,-1.0]])],"derivedFrom":subQ1}),-1.0]])]});}
            var Q599;
            {var subQ0=sQuery(id+"F25.wireOp",EDGE,"E344.MirrorCS");var subQ1=sQuery(id+"F25.wireOp",EDGE,"E336.MirrorCS");var subQ2=makeQuery(id+"F25.imprint","INTERSECT",VERTEX,{"derivedFrom":[subQ1,subQ0]});Q599=makeQuery(id+"F25.imprint","IMPRINT",FACE,{"disambiguationData":[TD([[makeQuery(id+"F25.imprint","IMPRINT",EDGE,{"disambiguationData":[TD([[subQ2,-1.0]])],"derivedFrom":subQ1}),-1.0]])]});}
            var Q600;
            {var subQ0=sQuery(id+"F25.wireOp",EDGE,"E394.MirrorCS");var subQ1=sQuery(id+"F25.wireOp",EDGE,"E344.MirrorCS");var subQ2=makeQuery(id+"F25.imprint","INTERSECT",VERTEX,{"derivedFrom":[subQ1,subQ0]});Q600=makeQuery(id+"F25.imprint","IMPRINT",FACE,{"disambiguationData":[TD([[makeQuery(id+"F25.imprint","IMPRINT",EDGE,{"disambiguationData":[TD([[subQ2,-1.0]])],"derivedFrom":subQ1}),-1.0]])]});}
            var Q601;
            {var subQ0=sQuery(id+"F25.wireOp",EDGE,"E394.MirrorCS");var subQ1=sQuery(id+"F25.wireOp",EDGE,"E344.MirrorCS");var subQ2=makeQuery(id+"F25.imprint","INTERSECT",VERTEX,{"derivedFrom":[subQ1,subQ0]});Q601=makeQuery(id+"F25.imprint","IMPRINT",FACE,{"disambiguationData":[TD([[makeQuery(id+"F25.imprint","IMPRINT",EDGE,{"disambiguationData":[TD([[subQ2,-1.0]])],"derivedFrom":subQ1}),1.0]])]});}
            var Q602;
            {var subQ0=sQuery(id+"F25.wireOp",EDGE,"E384.MirrorCS");var subQ1=sQuery(id+"F25.wireOp",EDGE,"E336.MirrorCS");var subQ2=makeQuery(id+"F25.imprint","INTERSECT",VERTEX,{"derivedFrom":[subQ1,subQ0]});Q602=makeQuery(id+"F25.imprint","IMPRINT",FACE,{"disambiguationData":[TD([[makeQuery(id+"F25.imprint","IMPRINT",EDGE,{"disambiguationData":[TD([[subQ2,-1.0]])],"derivedFrom":subQ1}),-1.0]])]});}
            extrude(context, id + "F34", {"entities" : qUnion([Q0, Q1, Q2, Q3, Q4, Q5, Q6, Q7, Q8, Q9, Q10, Q11, Q12, Q13, Q14, Q15, Q16, Q17, Q18, Q19, Q20, Q21, Q22, Q23, Q24, Q25, Q26, Q27, Q28, Q29, Q30, Q31, Q32, Q33, Q34, Q35, Q36, Q37, Q38, Q39, Q40, Q41, Q42, Q43, Q44, Q45, Q46, Q47, Q48, Q49, Q50, Q51, Q52, Q53, Q54, Q55, Q56, Q57, Q58, Q59, Q60, Q61, Q62, Q63, Q64, Q65, Q66, Q67, Q68, Q69, Q70, Q71, Q72, Q73, Q74, Q75, Q76, Q77, Q78, Q79, Q80, Q81, Q82, Q83, Q84, Q85, Q86, Q87, Q88, Q89, Q90, Q91, Q92, Q93, Q94, Q95, Q96, Q97, Q98, Q99, Q100, Q101, Q102, Q103, Q104, Q105, Q106, Q107, Q108, Q109, Q110, Q111, Q112, Q113, Q114, Q115, Q116, Q117, Q118, Q119, Q120, Q121, Q122, Q123, Q124, Q125, Q126, Q127, Q128, Q129, Q130, Q131, Q132, Q133, Q134, Q135, Q136, Q137, Q138, Q139, Q140, Q141, Q142, Q143, Q144, Q145, Q146, Q147, Q148, Q149, Q150, Q151, Q152, Q153, Q154, Q155, Q156, Q157, Q158, Q159, Q160, Q161, Q162, Q163, Q164, Q165, Q166, Q167, Q168, Q169, Q170, Q171, Q172, Q173, Q174, Q175, Q176, Q177, Q178, Q179, Q180, Q181, Q182, Q183, Q184, Q185, Q186, Q187, Q188, Q189, Q190, Q191, Q192, Q193, Q194, Q195, Q196, Q197, Q198, Q199, Q200, Q201, Q202, Q203, Q204, Q205, Q206, Q207, Q208, Q209, Q210, Q211, Q212, Q213, Q214, Q215, Q216, Q217, Q218, Q219, Q220, Q221, Q222, Q223, Q224, Q225, Q226, Q227, Q228, Q229, Q230, Q231, Q232, Q233, Q234, Q235, Q236, Q237, Q238, Q239, Q240, Q241, Q242, Q243, Q244, Q245, Q246, Q247, Q248, Q249, Q250, Q251, Q252, Q253, Q254, Q255, Q256, Q257, Q258, Q259, Q260, Q261, Q262, Q263, Q264, Q265, Q266, Q267, Q268, Q269, Q270, Q271, Q272, Q273, Q274, Q275, Q276, Q277, Q278, Q279, Q280, Q281, Q282, Q283, Q284, Q285, Q286, Q287, Q288, Q289, Q290, Q291, Q292, Q293, Q294, Q295, Q296, Q297, Q298, Q299, Q300, Q301, Q302, Q303, Q304, Q305, Q306, Q307, Q308, Q309, Q310, Q311, Q312, Q313, Q314, Q315, Q316, Q317, Q318, Q319, Q320, Q321, Q322, Q323, Q324, Q325, Q326, Q327, Q328, Q329, Q330, Q331, Q332, Q333, Q334, Q335, Q336, Q337, Q338, Q339, Q340, Q341, Q342, Q343, Q344, Q345, Q346, Q347, Q348, Q349, Q350, Q351, Q352, Q353, Q354, Q355, Q356, Q357, Q358, Q359, Q360, Q361, Q362, Q363, Q364, Q365, Q366, Q367, Q368, Q369, Q370, Q371, Q372, Q373, Q374, Q375, Q376, Q377, Q378, Q379, Q380, Q381, Q382, Q383, Q384, Q385, Q386, Q387, Q388, Q389, Q390, Q391, Q392, Q393, Q394, Q395, Q396, Q397, Q398, Q399, Q400, Q401, Q402, Q403, Q404, Q405, Q406, Q407, Q408, Q409, Q410, Q411, Q412, Q413, Q414, Q415, Q416, Q417, Q418, Q419, Q420, Q421, Q422, Q423, Q424, Q425, Q426, Q427, Q428, Q429, Q430, Q431, Q432, Q433, Q434, Q435, Q436, Q437, Q438, Q439, Q440, Q441, Q442, Q443, Q444, Q445, Q446, Q447, Q448, Q449, Q450, Q451, Q452, Q453, Q454, Q455, Q456, Q457, Q458, Q459, Q460, Q461, Q462, Q463, Q464, Q465, Q466, Q467, Q468, Q469, Q470, Q471, Q472, Q473, Q474, Q475, Q476, Q477, Q478, Q479, Q480, Q481, Q482, Q483, Q484, Q485, Q486, Q487, Q488, Q489, Q490, Q491, Q492, Q493, Q494, Q495, Q496, Q497, Q498, Q499, Q500, Q501, Q502, Q503, Q504, Q505, Q506, Q507, Q508, Q509, Q510, Q511, Q512, Q513, Q514, Q515, Q516, Q517, Q518, Q519, Q520, Q521, Q522, Q523, Q524, Q525, Q526, Q527, Q528, Q529, Q530, Q531, Q532, Q533, Q534, Q535, Q536, Q537, Q538, Q539, Q540, Q541, Q542, Q543, Q544, Q545, Q546, Q547, Q548, Q549, Q550, Q551, Q552, Q553, Q554, Q555, Q556, Q557, Q558, Q559, Q560, Q561, Q562, Q563, Q564, Q565, Q566, Q567, Q568, Q569, Q570, Q571, Q572, Q573, Q574, Q575, Q576, Q577, Q578, Q579, Q580, Q581, Q582, Q583, Q584, Q585, Q586, Q587, Q588, Q589, Q590, Q591, Q592, Q593, Q594, Q595, Q596, Q597, Q598, Q599, Q600, Q601, Q602]), "operationType" : NewBodyOperationType.REMOVE, "depth" : 25 * mm, "offsetDistance" : 25 * mm});
        }
        {
            var Q0;
            Q0=makeQuery(id+"F34.boolean.opBoolean","SPLIT",BODY,{"disambiguationData":[OD(4.0)],"derivedFrom":makeQuery(id+"F5.opExtrude","SWEPT_BODY",BODY,{"disambiguationData":[OSD([sQuery(id+"F2.wireOp",EDGE,"E74.top"),sQuery(id+"F2.wireOp",EDGE,"E75"),sQuery(id+"F2.wireOp",EDGE,"E76"),sQuery(id+"F2.wireOp",EDGE,"E77"),sQuery(id+"F2.wireOp",EDGE,"E89"),sQuery(id+"F2.wireOp",EDGE,"E90.trimOffspring"),sQuery(id+"F2.wireOp",EDGE,"E91"),sQuery(id+"F2.wireOp",EDGE,"E97.MirrorCS"),sQuery(id+"F2.wireOp",EDGE,"E98.MirrorCS"),sQuery(id+"F2.wireOp",EDGE,"E99.MirrorCS"),sQuery(id+"F2.wireOp",EDGE,"E100.MirrorCS"),sQuery(id+"F2.wireOp",EDGE,"E102.MirrorCS"),sQuery(id+"F2.wireOp",EDGE,"E103.MirrorCS"),sQuery(id+"F2.wireOp",EDGE,"E107.MirrorCS"),sQuery(id+"F2.wireOp",EDGE,"E108.MirrorCS"),sQuery(id+"F2.wireOp",EDGE,"E109.MirrorCS"),sQuery(id+"F2.wireOp",EDGE,"E110.MirrorCS"),sQuery(id+"F2.wireOp",EDGE,"E111.MirrorCS"),sQuery(id+"F2.wireOp",EDGE,"E115.MirrorCS"),sQuery(id+"F2.wireOp",EDGE,"E117.MirrorCS"),sQuery(id+"F2.wireOp",EDGE,"E121.MirrorCS"),sQuery(id+"F2.wireOp",EDGE,"E122.MirrorCS"),sQuery(id+"F2.wireOp",EDGE,"E123.MirrorCS"),sQuery(id+"F2.wireOp",EDGE,"E124.MirrorCS"),sQuery(id+"F2.wireOp",EDGE,"E126.MirrorCS"),sQuery(id+"F2.wireOp",EDGE,"E127.MirrorCS"),sQuery(id+"F2.wireOp",EDGE,"E128.MirrorCS"),sQuery(id+"F2.wireOp",EDGE,"E129.MirrorCS")])]})});
            var Q1;
            Q1=makeQuery(id+"F34.boolean.opBoolean","SPLIT",BODY,{"disambiguationData":[OD(3.0)],"derivedFrom":makeQuery(id+"F5.opExtrude","SWEPT_BODY",BODY,{"disambiguationData":[OSD([sQuery(id+"F2.wireOp",EDGE,"E74.top"),sQuery(id+"F2.wireOp",EDGE,"E75"),sQuery(id+"F2.wireOp",EDGE,"E76"),sQuery(id+"F2.wireOp",EDGE,"E77"),sQuery(id+"F2.wireOp",EDGE,"E89"),sQuery(id+"F2.wireOp",EDGE,"E90.trimOffspring"),sQuery(id+"F2.wireOp",EDGE,"E91"),sQuery(id+"F2.wireOp",EDGE,"E97.MirrorCS"),sQuery(id+"F2.wireOp",EDGE,"E98.MirrorCS"),sQuery(id+"F2.wireOp",EDGE,"E99.MirrorCS"),sQuery(id+"F2.wireOp",EDGE,"E100.MirrorCS"),sQuery(id+"F2.wireOp",EDGE,"E102.MirrorCS"),sQuery(id+"F2.wireOp",EDGE,"E103.MirrorCS"),sQuery(id+"F2.wireOp",EDGE,"E107.MirrorCS"),sQuery(id+"F2.wireOp",EDGE,"E108.MirrorCS"),sQuery(id+"F2.wireOp",EDGE,"E109.MirrorCS"),sQuery(id+"F2.wireOp",EDGE,"E110.MirrorCS"),sQuery(id+"F2.wireOp",EDGE,"E111.MirrorCS"),sQuery(id+"F2.wireOp",EDGE,"E115.MirrorCS"),sQuery(id+"F2.wireOp",EDGE,"E117.MirrorCS"),sQuery(id+"F2.wireOp",EDGE,"E121.MirrorCS"),sQuery(id+"F2.wireOp",EDGE,"E122.MirrorCS"),sQuery(id+"F2.wireOp",EDGE,"E123.MirrorCS"),sQuery(id+"F2.wireOp",EDGE,"E124.MirrorCS"),sQuery(id+"F2.wireOp",EDGE,"E126.MirrorCS"),sQuery(id+"F2.wireOp",EDGE,"E127.MirrorCS"),sQuery(id+"F2.wireOp",EDGE,"E128.MirrorCS"),sQuery(id+"F2.wireOp",EDGE,"E129.MirrorCS")])]})});
            var Q2;
            Q2=makeQuery(id+"F34.boolean.opBoolean","SPLIT",BODY,{"disambiguationData":[OD(1.0)],"derivedFrom":makeQuery(id+"F5.opExtrude","SWEPT_BODY",BODY,{"disambiguationData":[OSD([sQuery(id+"F2.wireOp",EDGE,"E74.top"),sQuery(id+"F2.wireOp",EDGE,"E75"),sQuery(id+"F2.wireOp",EDGE,"E76"),sQuery(id+"F2.wireOp",EDGE,"E77"),sQuery(id+"F2.wireOp",EDGE,"E89"),sQuery(id+"F2.wireOp",EDGE,"E90.trimOffspring"),sQuery(id+"F2.wireOp",EDGE,"E91"),sQuery(id+"F2.wireOp",EDGE,"E97.MirrorCS"),sQuery(id+"F2.wireOp",EDGE,"E98.MirrorCS"),sQuery(id+"F2.wireOp",EDGE,"E99.MirrorCS"),sQuery(id+"F2.wireOp",EDGE,"E100.MirrorCS"),sQuery(id+"F2.wireOp",EDGE,"E102.MirrorCS"),sQuery(id+"F2.wireOp",EDGE,"E103.MirrorCS"),sQuery(id+"F2.wireOp",EDGE,"E107.MirrorCS"),sQuery(id+"F2.wireOp",EDGE,"E108.MirrorCS"),sQuery(id+"F2.wireOp",EDGE,"E109.MirrorCS"),sQuery(id+"F2.wireOp",EDGE,"E110.MirrorCS"),sQuery(id+"F2.wireOp",EDGE,"E111.MirrorCS"),sQuery(id+"F2.wireOp",EDGE,"E115.MirrorCS"),sQuery(id+"F2.wireOp",EDGE,"E117.MirrorCS"),sQuery(id+"F2.wireOp",EDGE,"E121.MirrorCS"),sQuery(id+"F2.wireOp",EDGE,"E122.MirrorCS"),sQuery(id+"F2.wireOp",EDGE,"E123.MirrorCS"),sQuery(id+"F2.wireOp",EDGE,"E124.MirrorCS"),sQuery(id+"F2.wireOp",EDGE,"E126.MirrorCS"),sQuery(id+"F2.wireOp",EDGE,"E127.MirrorCS"),sQuery(id+"F2.wireOp",EDGE,"E128.MirrorCS"),sQuery(id+"F2.wireOp",EDGE,"E129.MirrorCS")])]})});
            var Q3;
            Q3=makeQuery(id+"F34.boolean.opBoolean","SPLIT",BODY,{"disambiguationData":[OD(0.0)],"derivedFrom":makeQuery(id+"F5.opExtrude","SWEPT_BODY",BODY,{"disambiguationData":[OSD([sQuery(id+"F2.wireOp",EDGE,"E74.top"),sQuery(id+"F2.wireOp",EDGE,"E75"),sQuery(id+"F2.wireOp",EDGE,"E76"),sQuery(id+"F2.wireOp",EDGE,"E77"),sQuery(id+"F2.wireOp",EDGE,"E89"),sQuery(id+"F2.wireOp",EDGE,"E90.trimOffspring"),sQuery(id+"F2.wireOp",EDGE,"E91"),sQuery(id+"F2.wireOp",EDGE,"E97.MirrorCS"),sQuery(id+"F2.wireOp",EDGE,"E98.MirrorCS"),sQuery(id+"F2.wireOp",EDGE,"E99.MirrorCS"),sQuery(id+"F2.wireOp",EDGE,"E100.MirrorCS"),sQuery(id+"F2.wireOp",EDGE,"E102.MirrorCS"),sQuery(id+"F2.wireOp",EDGE,"E103.MirrorCS"),sQuery(id+"F2.wireOp",EDGE,"E107.MirrorCS"),sQuery(id+"F2.wireOp",EDGE,"E108.MirrorCS"),sQuery(id+"F2.wireOp",EDGE,"E109.MirrorCS"),sQuery(id+"F2.wireOp",EDGE,"E110.MirrorCS"),sQuery(id+"F2.wireOp",EDGE,"E111.MirrorCS"),sQuery(id+"F2.wireOp",EDGE,"E115.MirrorCS"),sQuery(id+"F2.wireOp",EDGE,"E117.MirrorCS"),sQuery(id+"F2.wireOp",EDGE,"E121.MirrorCS"),sQuery(id+"F2.wireOp",EDGE,"E122.MirrorCS"),sQuery(id+"F2.wireOp",EDGE,"E123.MirrorCS"),sQuery(id+"F2.wireOp",EDGE,"E124.MirrorCS"),sQuery(id+"F2.wireOp",EDGE,"E126.MirrorCS"),sQuery(id+"F2.wireOp",EDGE,"E127.MirrorCS"),sQuery(id+"F2.wireOp",EDGE,"E128.MirrorCS"),sQuery(id+"F2.wireOp",EDGE,"E129.MirrorCS")])]})});
            deleteBodies(context, id + "F35", {"entities" : qUnion([Q0, Q1, Q2, Q3])});
        }
        {
            var Q0;
            {var subQ0=sQuery(id+"F25.wireOp",EDGE,"E388.MirrorCS");var subQ1=sQuery(id+"F25.wireOp",EDGE,"E363.MirrorCS");var subQ2=makeQuery(id+"F25.imprint","INTERSECT",VERTEX,{"derivedFrom":[subQ1,subQ0]});Q0=makeQuery(id+"F25.imprint","IMPRINT",FACE,{"disambiguationData":[TD([[makeQuery(id+"F25.imprint","IMPRINT",EDGE,{"disambiguationData":[TD([[subQ2,-1.0]])],"derivedFrom":subQ1}),1.0]])]});}
            var Q1;
            {var subQ0=sQuery(id+"F25.wireOp",EDGE,"E367.MirrorCS");var subQ1=sQuery(id+"F25.wireOp",EDGE,"E359.MirrorCS");var subQ2=makeQuery(id+"F25.imprint","INTERSECT",VERTEX,{"derivedFrom":[subQ1,subQ0]});Q1=makeQuery(id+"F25.imprint","IMPRINT",FACE,{"disambiguationData":[TD([[makeQuery(id+"F25.imprint","IMPRINT",EDGE,{"disambiguationData":[TD([[subQ2,-1.0]])],"derivedFrom":subQ1}),1.0]])]});}
            var Q2;
            {var subQ0=sQuery(id+"F25.wireOp",EDGE,"E336.MirrorCS");var subQ1=sQuery(id+"F25.wireOp",EDGE,"E335.MirrorCS");var subQ2=makeQuery(id+"F25.imprint","INTERSECT",VERTEX,{"derivedFrom":[subQ1,subQ0]});Q2=makeQuery(id+"F25.imprint","IMPRINT",FACE,{"disambiguationData":[TD([[makeQuery(id+"F25.imprint","IMPRINT",EDGE,{"disambiguationData":[TD([[subQ2,-1.0]])],"derivedFrom":subQ1}),1.0]])]});}
            var Q3;
            {var subQ0=sQuery(id+"F25.wireOp",EDGE,"E348.MirrorCS");var subQ1=sQuery(id+"F25.wireOp",EDGE,"E336.MirrorCS");var subQ2=makeQuery(id+"F25.imprint","INTERSECT",VERTEX,{"derivedFrom":[subQ1,subQ0]});Q3=makeQuery(id+"F25.imprint","IMPRINT",FACE,{"disambiguationData":[TD([[makeQuery(id+"F25.imprint","IMPRINT",EDGE,{"disambiguationData":[TD([[subQ2,-1.0]])],"derivedFrom":subQ1}),1.0]])]});}
            var Q4;
            {var subQ0=sQuery(id+"F25.wireOp",EDGE,"E378.MirrorCS");var subQ1=sQuery(id+"F25.wireOp",EDGE,"E336.MirrorCS");var subQ2=makeQuery(id+"F25.imprint","INTERSECT",VERTEX,{"derivedFrom":[subQ1,subQ0]});Q4=makeQuery(id+"F25.imprint","IMPRINT",FACE,{"disambiguationData":[TD([[makeQuery(id+"F25.imprint","IMPRINT",EDGE,{"disambiguationData":[TD([[subQ2,-1.0]])],"derivedFrom":subQ1}),1.0]])]});}
            var Q5;
            {var subQ0=sQuery(id+"F25.wireOp",EDGE,"E373.MirrorCS");var subQ1=sQuery(id+"F25.wireOp",EDGE,"E336.MirrorCS");var subQ2=makeQuery(id+"F25.imprint","INTERSECT",VERTEX,{"derivedFrom":[subQ1,subQ0]});Q5=makeQuery(id+"F25.imprint","IMPRINT",FACE,{"disambiguationData":[TD([[makeQuery(id+"F25.imprint","IMPRINT",EDGE,{"disambiguationData":[TD([[subQ2,-1.0]])],"derivedFrom":subQ1}),1.0]])]});}
            var Q6;
            {var subQ0=sQuery(id+"F25.wireOp",EDGE,"E344.MirrorCS");var subQ1=sQuery(id+"F25.wireOp",EDGE,"E336.MirrorCS");var subQ2=makeQuery(id+"F25.imprint","INTERSECT",VERTEX,{"derivedFrom":[subQ1,subQ0]});Q6=makeQuery(id+"F25.imprint","IMPRINT",FACE,{"disambiguationData":[TD([[makeQuery(id+"F25.imprint","IMPRINT",EDGE,{"disambiguationData":[TD([[subQ2,-1.0]])],"derivedFrom":subQ1}),1.0]])]});}
            var Q7;
            {var subQ0=sQuery(id+"F25.wireOp",EDGE,"E384.MirrorCS");var subQ1=sQuery(id+"F25.wireOp",EDGE,"E336.MirrorCS");var subQ2=makeQuery(id+"F25.imprint","INTERSECT",VERTEX,{"derivedFrom":[subQ1,subQ0]});Q7=makeQuery(id+"F25.imprint","IMPRINT",FACE,{"disambiguationData":[TD([[makeQuery(id+"F25.imprint","IMPRINT",EDGE,{"disambiguationData":[TD([[subQ2,-1.0]])],"derivedFrom":subQ1}),1.0]])]});}
            var Q8;
            {var subQ0=sQuery(id+"F25.wireOp",EDGE,"E367.MirrorCS");var subQ1=sQuery(id+"F25.wireOp",EDGE,"E342.MirrorCS");var subQ2=makeQuery(id+"F25.imprint","INTERSECT",VERTEX,{"derivedFrom":[subQ1,subQ0]});Q8=makeQuery(id+"F25.imprint","IMPRINT",FACE,{"disambiguationData":[TD([[makeQuery(id+"F25.imprint","IMPRINT",EDGE,{"disambiguationData":[TD([[subQ2,-1.0]])],"derivedFrom":subQ1}),1.0]])]});}
            var Q9;
            {var subQ0=sQuery(id+"F25.wireOp",EDGE,"E367.MirrorCS");var subQ1=sQuery(id+"F25.wireOp",EDGE,"E328.MirrorCS");var subQ2=makeQuery(id+"F25.imprint","INTERSECT",VERTEX,{"derivedFrom":[subQ1,subQ0]});Q9=makeQuery(id+"F25.imprint","IMPRINT",FACE,{"disambiguationData":[TD([[makeQuery(id+"F25.imprint","IMPRINT",EDGE,{"disambiguationData":[TD([[subQ2,-1.0]])],"derivedFrom":subQ1}),1.0]])]});}
            var Q10;
            {var subQ0=sQuery(id+"F25.wireOp",EDGE,"E367.MirrorCS");var subQ1=sQuery(id+"F25.wireOp",EDGE,"E328.MirrorCS");var subQ2=makeQuery(id+"F25.imprint","INTERSECT",VERTEX,{"derivedFrom":[subQ1,subQ0]});Q10=makeQuery(id+"F25.imprint","IMPRINT",FACE,{"disambiguationData":[TD([[makeQuery(id+"F25.imprint","IMPRINT",EDGE,{"disambiguationData":[TD([[subQ2,-1.0]])],"derivedFrom":subQ1}),-1.0]])]});}
            var Q11;
            {var subQ0=sQuery(id+"F25.wireOp",EDGE,"E363.MirrorCS");var subQ1=sQuery(id+"F25.wireOp",EDGE,"E358.MirrorCS");var subQ2=makeQuery(id+"F25.imprint","INTERSECT",VERTEX,{"derivedFrom":[subQ1,subQ0]});Q11=makeQuery(id+"F25.imprint","IMPRINT",FACE,{"disambiguationData":[TD([[makeQuery(id+"F25.imprint","IMPRINT",EDGE,{"disambiguationData":[TD([[subQ2,1.0]])],"derivedFrom":subQ1}),1.0]])]});}
            extrude(context, id + "F36", {"entities" : qUnion([Q0, Q1, Q2, Q3, Q4, Q5, Q6, Q7, Q8, Q9, Q10, Q11]), "operationType" : NewBodyOperationType.REMOVE, "depth" : 19.5 * mm, "offsetDistance" : 25 * mm});
        }
        {
            var Q0;
            {var subQ0=sQuery(id+"F26.wireOp",EDGE,"E664.right");var subQ1=sQuery(id+"F26.wireOp",EDGE,"E654.bottom");var subQ2=makeQuery(id+"F26.imprint","INTERSECT",VERTEX,{"derivedFrom":[subQ1,subQ0]});Q0=makeQuery(id+"F26.imprint","IMPRINT",FACE,{"disambiguationData":[TD([[makeQuery(id+"F26.imprint","IMPRINT",EDGE,{"disambiguationData":[TD([[subQ2,-1.0]])],"derivedFrom":subQ1}),-1.0]])]});}
            var Q1;
            {var subQ0=sQuery(id+"F26.wireOp",EDGE,"E664.left");var subQ1=sQuery(id+"F26.wireOp",EDGE,"E654.bottom");var subQ2=makeQuery(id+"F26.imprint","INTERSECT",VERTEX,{"derivedFrom":[subQ1,subQ0]});Q1=makeQuery(id+"F26.imprint","IMPRINT",FACE,{"disambiguationData":[TD([[makeQuery(id+"F26.imprint","IMPRINT",EDGE,{"disambiguationData":[TD([[subQ2,-1.0]])],"derivedFrom":subQ1}),-1.0]])]});}
            var Q2;
            {var subQ0=sQuery(id+"F26.wireOp",EDGE,"E665.right");var subQ1=sQuery(id+"F26.wireOp",EDGE,"E654.bottom");var subQ2=makeQuery(id+"F26.imprint","INTERSECT",VERTEX,{"derivedFrom":[subQ1,subQ0]});Q2=makeQuery(id+"F26.imprint","IMPRINT",FACE,{"disambiguationData":[TD([[makeQuery(id+"F26.imprint","IMPRINT",EDGE,{"disambiguationData":[TD([[subQ2,-1.0]])],"derivedFrom":subQ1}),-1.0]])]});}
            var Q3;
            {var subQ0=sQuery(id+"F26.wireOp",EDGE,"E666.right");var subQ1=sQuery(id+"F26.wireOp",EDGE,"E654.bottom");var subQ2=makeQuery(id+"F26.imprint","INTERSECT",VERTEX,{"derivedFrom":[subQ1,subQ0]});Q3=makeQuery(id+"F26.imprint","IMPRINT",FACE,{"disambiguationData":[TD([[makeQuery(id+"F26.imprint","IMPRINT",EDGE,{"disambiguationData":[TD([[subQ2,-1.0]])],"derivedFrom":subQ1}),-1.0]])]});}
            var Q4;
            {var subQ0=sQuery(id+"F26.wireOp",EDGE,"E666.right");var subQ1=sQuery(id+"F26.wireOp",EDGE,"E655.top");var subQ2=makeQuery(id+"F26.imprint","INTERSECT",VERTEX,{"derivedFrom":[subQ1,subQ0]});Q4=makeQuery(id+"F26.imprint","IMPRINT",FACE,{"disambiguationData":[TD([[makeQuery(id+"F26.imprint","IMPRINT",EDGE,{"disambiguationData":[TD([[subQ2,-1.0]])],"derivedFrom":subQ1}),-1.0]])]});}
            var Q5;
            {var subQ0=sQuery(id+"F26.wireOp",EDGE,"E664.right");var subQ1=sQuery(id+"F26.wireOp",EDGE,"E655.top");var subQ2=makeQuery(id+"F26.imprint","INTERSECT",VERTEX,{"derivedFrom":[subQ1,subQ0]});Q5=makeQuery(id+"F26.imprint","IMPRINT",FACE,{"disambiguationData":[TD([[makeQuery(id+"F26.imprint","IMPRINT",EDGE,{"disambiguationData":[TD([[subQ2,-1.0]])],"derivedFrom":subQ1}),-1.0]])]});}
            var Q6;
            {var subQ0=sQuery(id+"F26.wireOp",EDGE,"E664.left");var subQ1=sQuery(id+"F26.wireOp",EDGE,"E655.top");var subQ2=makeQuery(id+"F26.imprint","INTERSECT",VERTEX,{"derivedFrom":[subQ1,subQ0]});Q6=makeQuery(id+"F26.imprint","IMPRINT",FACE,{"disambiguationData":[TD([[makeQuery(id+"F26.imprint","IMPRINT",EDGE,{"disambiguationData":[TD([[subQ2,-1.0]])],"derivedFrom":subQ1}),-1.0]])]});}
            var Q7;
            {var subQ0=sQuery(id+"F26.wireOp",EDGE,"E665.right");var subQ1=sQuery(id+"F26.wireOp",EDGE,"E655.top");var subQ2=makeQuery(id+"F26.imprint","INTERSECT",VERTEX,{"derivedFrom":[subQ1,subQ0]});Q7=makeQuery(id+"F26.imprint","IMPRINT",FACE,{"disambiguationData":[TD([[makeQuery(id+"F26.imprint","IMPRINT",EDGE,{"disambiguationData":[TD([[subQ2,-1.0]])],"derivedFrom":subQ1}),-1.0]])]});}
            var Q8;
            {var subQ0=sQuery(id+"F26.wireOp",EDGE,"E664.right");var subQ1=sQuery(id+"F26.wireOp",EDGE,"E656.top");var subQ2=makeQuery(id+"F26.imprint","INTERSECT",VERTEX,{"derivedFrom":[subQ1,subQ0]});Q8=makeQuery(id+"F26.imprint","IMPRINT",FACE,{"disambiguationData":[TD([[makeQuery(id+"F26.imprint","IMPRINT",EDGE,{"disambiguationData":[TD([[subQ2,-1.0]])],"derivedFrom":subQ1}),-1.0]])]});}
            var Q9;
            {var subQ0=sQuery(id+"F26.wireOp",EDGE,"E664.left");var subQ1=sQuery(id+"F26.wireOp",EDGE,"E656.top");var subQ2=makeQuery(id+"F26.imprint","INTERSECT",VERTEX,{"derivedFrom":[subQ1,subQ0]});Q9=makeQuery(id+"F26.imprint","IMPRINT",FACE,{"disambiguationData":[TD([[makeQuery(id+"F26.imprint","IMPRINT",EDGE,{"disambiguationData":[TD([[subQ2,-1.0]])],"derivedFrom":subQ1}),-1.0]])]});}
            var Q10;
            {var subQ0=sQuery(id+"F26.wireOp",EDGE,"E665.right");var subQ1=sQuery(id+"F26.wireOp",EDGE,"E656.top");var subQ2=makeQuery(id+"F26.imprint","INTERSECT",VERTEX,{"derivedFrom":[subQ1,subQ0]});Q10=makeQuery(id+"F26.imprint","IMPRINT",FACE,{"disambiguationData":[TD([[makeQuery(id+"F26.imprint","IMPRINT",EDGE,{"disambiguationData":[TD([[subQ2,-1.0]])],"derivedFrom":subQ1}),-1.0]])]});}
            var Q11;
            {var subQ0=sQuery(id+"F26.wireOp",EDGE,"E666.right");var subQ1=sQuery(id+"F26.wireOp",EDGE,"E656.top");var subQ2=makeQuery(id+"F26.imprint","INTERSECT",VERTEX,{"derivedFrom":[subQ1,subQ0]});Q11=makeQuery(id+"F26.imprint","IMPRINT",FACE,{"disambiguationData":[TD([[makeQuery(id+"F26.imprint","IMPRINT",EDGE,{"disambiguationData":[TD([[subQ2,-1.0]])],"derivedFrom":subQ1}),-1.0]])]});}
            var Q12;
            {var subQ0=sQuery(id+"F26.wireOp",EDGE,"E666.left");var subQ1=sQuery(id+"F26.wireOp",EDGE,"E656.top");var subQ2=makeQuery(id+"F26.imprint","INTERSECT",VERTEX,{"derivedFrom":[subQ1,subQ0]});Q12=makeQuery(id+"F26.imprint","IMPRINT",FACE,{"disambiguationData":[TD([[makeQuery(id+"F26.imprint","IMPRINT",EDGE,{"disambiguationData":[TD([[subQ2,-1.0]])],"derivedFrom":subQ1}),-1.0]])]});}
            var Q13;
            {var subQ0=sQuery(id+"F26.wireOp",EDGE,"E666.left");var subQ1=sQuery(id+"F26.wireOp",EDGE,"E655.top");var subQ2=makeQuery(id+"F26.imprint","INTERSECT",VERTEX,{"derivedFrom":[subQ1,subQ0]});Q13=makeQuery(id+"F26.imprint","IMPRINT",FACE,{"disambiguationData":[TD([[makeQuery(id+"F26.imprint","IMPRINT",EDGE,{"disambiguationData":[TD([[subQ2,-1.0]])],"derivedFrom":subQ1}),-1.0]])]});}
            var Q14;
            {var subQ0=sQuery(id+"F26.wireOp",EDGE,"E667.right");var subQ1=sQuery(id+"F26.wireOp",EDGE,"E655.top");var subQ2=makeQuery(id+"F26.imprint","INTERSECT",VERTEX,{"derivedFrom":[subQ1,subQ0]});Q14=makeQuery(id+"F26.imprint","IMPRINT",FACE,{"disambiguationData":[TD([[makeQuery(id+"F26.imprint","IMPRINT",EDGE,{"disambiguationData":[TD([[subQ2,-1.0]])],"derivedFrom":subQ1}),-1.0]])]});}
            var Q15;
            {var subQ0=sQuery(id+"F26.wireOp",EDGE,"E667.right");var subQ1=sQuery(id+"F26.wireOp",EDGE,"E656.top");var subQ2=makeQuery(id+"F26.imprint","INTERSECT",VERTEX,{"derivedFrom":[subQ1,subQ0]});Q15=makeQuery(id+"F26.imprint","IMPRINT",FACE,{"disambiguationData":[TD([[makeQuery(id+"F26.imprint","IMPRINT",EDGE,{"disambiguationData":[TD([[subQ2,-1.0]])],"derivedFrom":subQ1}),-1.0]])]});}
            var Q16;
            {var subQ0=sQuery(id+"F26.wireOp",EDGE,"E667.right");var subQ1=sQuery(id+"F26.wireOp",EDGE,"E654.bottom");var subQ2=makeQuery(id+"F26.imprint","INTERSECT",VERTEX,{"derivedFrom":[subQ1,subQ0]});Q16=makeQuery(id+"F26.imprint","IMPRINT",FACE,{"disambiguationData":[TD([[makeQuery(id+"F26.imprint","IMPRINT",EDGE,{"disambiguationData":[TD([[subQ2,-1.0]])],"derivedFrom":subQ1}),-1.0]])]});}
            var Q17;
            {var subQ0=sQuery(id+"F26.wireOp",EDGE,"E666.left");var subQ1=sQuery(id+"F26.wireOp",EDGE,"E654.bottom");var subQ2=makeQuery(id+"F26.imprint","INTERSECT",VERTEX,{"derivedFrom":[subQ1,subQ0]});Q17=makeQuery(id+"F26.imprint","IMPRINT",FACE,{"disambiguationData":[TD([[makeQuery(id+"F26.imprint","IMPRINT",EDGE,{"disambiguationData":[TD([[subQ2,-1.0]])],"derivedFrom":subQ1}),-1.0]])]});}
            var Q18;
            {var subQ0=sQuery(id+"F26.wireOp",EDGE,"E660.left");var subQ1=sQuery(id+"F26.wireOp",EDGE,"E647.top");var subQ2=makeQuery(id+"F26.imprint","INTERSECT",VERTEX,{"derivedFrom":[subQ1,subQ0]});Q18=makeQuery(id+"F26.imprint","IMPRINT",FACE,{"disambiguationData":[TD([[makeQuery(id+"F26.imprint","IMPRINT",EDGE,{"disambiguationData":[TD([[subQ2,-1.0]])],"derivedFrom":subQ1}),-1.0]])]});}
            var Q19;
            {var subQ0=sQuery(id+"F26.wireOp",EDGE,"E661.right");var subQ1=sQuery(id+"F26.wireOp",EDGE,"E647.top");var subQ2=makeQuery(id+"F26.imprint","INTERSECT",VERTEX,{"derivedFrom":[subQ1,subQ0]});Q19=makeQuery(id+"F26.imprint","IMPRINT",FACE,{"disambiguationData":[TD([[makeQuery(id+"F26.imprint","IMPRINT",EDGE,{"disambiguationData":[TD([[subQ2,-1.0]])],"derivedFrom":subQ1}),-1.0]])]});}
            var Q20;
            {var subQ0=sQuery(id+"F26.wireOp",EDGE,"E660.left");var subQ1=sQuery(id+"F26.wireOp",EDGE,"E648.top");var subQ2=makeQuery(id+"F26.imprint","INTERSECT",VERTEX,{"derivedFrom":[subQ1,subQ0]});Q20=makeQuery(id+"F26.imprint","IMPRINT",FACE,{"disambiguationData":[TD([[makeQuery(id+"F26.imprint","IMPRINT",EDGE,{"disambiguationData":[TD([[subQ2,-1.0]])],"derivedFrom":subQ1}),-1.0]])]});}
            var Q21;
            {var subQ0=sQuery(id+"F26.wireOp",EDGE,"E660.left");var subQ1=sQuery(id+"F26.wireOp",EDGE,"E648.bottom");var subQ2=makeQuery(id+"F26.imprint","INTERSECT",VERTEX,{"derivedFrom":[subQ1,subQ0]});Q21=makeQuery(id+"F26.imprint","IMPRINT",FACE,{"disambiguationData":[TD([[makeQuery(id+"F26.imprint","IMPRINT",EDGE,{"disambiguationData":[TD([[subQ2,-1.0]])],"derivedFrom":subQ1}),-1.0]])]});}
            var Q22;
            {var subQ0=sQuery(id+"F26.wireOp",EDGE,"E661.right");var subQ1=sQuery(id+"F26.wireOp",EDGE,"E648.top");var subQ2=makeQuery(id+"F26.imprint","INTERSECT",VERTEX,{"derivedFrom":[subQ1,subQ0]});Q22=makeQuery(id+"F26.imprint","IMPRINT",FACE,{"disambiguationData":[TD([[makeQuery(id+"F26.imprint","IMPRINT",EDGE,{"disambiguationData":[TD([[subQ2,-1.0]])],"derivedFrom":subQ1}),-1.0]])]});}
            var Q23;
            {var subQ0=sQuery(id+"F26.wireOp",EDGE,"E661.right");var subQ1=sQuery(id+"F26.wireOp",EDGE,"E648.bottom");var subQ2=makeQuery(id+"F26.imprint","INTERSECT",VERTEX,{"derivedFrom":[subQ1,subQ0]});Q23=makeQuery(id+"F26.imprint","IMPRINT",FACE,{"disambiguationData":[TD([[makeQuery(id+"F26.imprint","IMPRINT",EDGE,{"disambiguationData":[TD([[subQ2,-1.0]])],"derivedFrom":subQ1}),-1.0]])]});}
            var Q24;
            {var subQ0=sQuery(id+"F26.wireOp",EDGE,"E660.left");var subQ1=sQuery(id+"F26.wireOp",EDGE,"E649.top");var subQ2=makeQuery(id+"F26.imprint","INTERSECT",VERTEX,{"derivedFrom":[subQ1,subQ0]});Q24=makeQuery(id+"F26.imprint","IMPRINT",FACE,{"disambiguationData":[TD([[makeQuery(id+"F26.imprint","IMPRINT",EDGE,{"disambiguationData":[TD([[subQ2,-1.0]])],"derivedFrom":subQ1}),-1.0]])]});}
            var Q25;
            {var subQ0=sQuery(id+"F26.wireOp",EDGE,"E661.right");var subQ1=sQuery(id+"F26.wireOp",EDGE,"E649.top");var subQ2=makeQuery(id+"F26.imprint","INTERSECT",VERTEX,{"derivedFrom":[subQ1,subQ0]});Q25=makeQuery(id+"F26.imprint","IMPRINT",FACE,{"disambiguationData":[TD([[makeQuery(id+"F26.imprint","IMPRINT",EDGE,{"disambiguationData":[TD([[subQ2,-1.0]])],"derivedFrom":subQ1}),-1.0]])]});}
            var Q26;
            {var subQ0=sQuery(id+"F26.wireOp",EDGE,"E660.left");var subQ1=sQuery(id+"F26.wireOp",EDGE,"E650.top");var subQ2=makeQuery(id+"F26.imprint","INTERSECT",VERTEX,{"derivedFrom":[subQ1,subQ0]});Q26=makeQuery(id+"F26.imprint","IMPRINT",FACE,{"disambiguationData":[TD([[makeQuery(id+"F26.imprint","IMPRINT",EDGE,{"disambiguationData":[TD([[subQ2,-1.0]])],"derivedFrom":subQ1}),-1.0]])]});}
            var Q27;
            {var subQ0=sQuery(id+"F26.wireOp",EDGE,"E660.left");var subQ1=sQuery(id+"F26.wireOp",EDGE,"E650.bottom");var subQ2=makeQuery(id+"F26.imprint","INTERSECT",VERTEX,{"derivedFrom":[subQ1,subQ0]});Q27=makeQuery(id+"F26.imprint","IMPRINT",FACE,{"disambiguationData":[TD([[makeQuery(id+"F26.imprint","IMPRINT",EDGE,{"disambiguationData":[TD([[subQ2,-1.0]])],"derivedFrom":subQ1}),-1.0]])]});}
            var Q28;
            {var subQ0=sQuery(id+"F26.wireOp",EDGE,"E661.right");var subQ1=sQuery(id+"F26.wireOp",EDGE,"E650.top");var subQ2=makeQuery(id+"F26.imprint","INTERSECT",VERTEX,{"derivedFrom":[subQ1,subQ0]});Q28=makeQuery(id+"F26.imprint","IMPRINT",FACE,{"disambiguationData":[TD([[makeQuery(id+"F26.imprint","IMPRINT",EDGE,{"disambiguationData":[TD([[subQ2,-1.0]])],"derivedFrom":subQ1}),-1.0]])]});}
            var Q29;
            {var subQ0=sQuery(id+"F26.wireOp",EDGE,"E661.right");var subQ1=sQuery(id+"F26.wireOp",EDGE,"E650.bottom");var subQ2=makeQuery(id+"F26.imprint","INTERSECT",VERTEX,{"derivedFrom":[subQ1,subQ0]});Q29=makeQuery(id+"F26.imprint","IMPRINT",FACE,{"disambiguationData":[TD([[makeQuery(id+"F26.imprint","IMPRINT",EDGE,{"disambiguationData":[TD([[subQ2,-1.0]])],"derivedFrom":subQ1}),-1.0]])]});}
            var Q30;
            {var subQ0=sQuery(id+"F26.wireOp",EDGE,"E662.right");var subQ1=sQuery(id+"F26.wireOp",EDGE,"E647.top");var subQ2=makeQuery(id+"F26.imprint","INTERSECT",VERTEX,{"derivedFrom":[subQ1,subQ0]});Q30=makeQuery(id+"F26.imprint","IMPRINT",FACE,{"disambiguationData":[TD([[makeQuery(id+"F26.imprint","IMPRINT",EDGE,{"disambiguationData":[TD([[subQ2,-1.0]])],"derivedFrom":subQ1}),-1.0]])]});}
            var Q31;
            {var subQ0=sQuery(id+"F26.wireOp",EDGE,"E662.right");var subQ1=sQuery(id+"F26.wireOp",EDGE,"E648.top");var subQ2=makeQuery(id+"F26.imprint","INTERSECT",VERTEX,{"derivedFrom":[subQ1,subQ0]});Q31=makeQuery(id+"F26.imprint","IMPRINT",FACE,{"disambiguationData":[TD([[makeQuery(id+"F26.imprint","IMPRINT",EDGE,{"disambiguationData":[TD([[subQ2,-1.0]])],"derivedFrom":subQ1}),-1.0]])]});}
            var Q32;
            {var subQ0=sQuery(id+"F26.wireOp",EDGE,"E662.right");var subQ1=sQuery(id+"F26.wireOp",EDGE,"E648.bottom");var subQ2=makeQuery(id+"F26.imprint","INTERSECT",VERTEX,{"derivedFrom":[subQ1,subQ0]});Q32=makeQuery(id+"F26.imprint","IMPRINT",FACE,{"disambiguationData":[TD([[makeQuery(id+"F26.imprint","IMPRINT",EDGE,{"disambiguationData":[TD([[subQ2,-1.0]])],"derivedFrom":subQ1}),-1.0]])]});}
            var Q33;
            {var subQ0=sQuery(id+"F26.wireOp",EDGE,"E662.right");var subQ1=sQuery(id+"F26.wireOp",EDGE,"E649.top");var subQ2=makeQuery(id+"F26.imprint","INTERSECT",VERTEX,{"derivedFrom":[subQ1,subQ0]});Q33=makeQuery(id+"F26.imprint","IMPRINT",FACE,{"disambiguationData":[TD([[makeQuery(id+"F26.imprint","IMPRINT",EDGE,{"disambiguationData":[TD([[subQ2,-1.0]])],"derivedFrom":subQ1}),-1.0]])]});}
            var Q34;
            {var subQ0=sQuery(id+"F26.wireOp",EDGE,"E662.right");var subQ1=sQuery(id+"F26.wireOp",EDGE,"E650.top");var subQ2=makeQuery(id+"F26.imprint","INTERSECT",VERTEX,{"derivedFrom":[subQ1,subQ0]});Q34=makeQuery(id+"F26.imprint","IMPRINT",FACE,{"disambiguationData":[TD([[makeQuery(id+"F26.imprint","IMPRINT",EDGE,{"disambiguationData":[TD([[subQ2,-1.0]])],"derivedFrom":subQ1}),-1.0]])]});}
            var Q35;
            {var subQ0=sQuery(id+"F26.wireOp",EDGE,"E662.right");var subQ1=sQuery(id+"F26.wireOp",EDGE,"E650.bottom");var subQ2=makeQuery(id+"F26.imprint","INTERSECT",VERTEX,{"derivedFrom":[subQ1,subQ0]});Q35=makeQuery(id+"F26.imprint","IMPRINT",FACE,{"disambiguationData":[TD([[makeQuery(id+"F26.imprint","IMPRINT",EDGE,{"disambiguationData":[TD([[subQ2,-1.0]])],"derivedFrom":subQ1}),-1.0]])]});}
            var Q36;
            {var subQ0=sQuery(id+"F26.wireOp",EDGE,"E660.right");var subQ1=sQuery(id+"F26.wireOp",EDGE,"E647.top");var subQ2=makeQuery(id+"F26.imprint","INTERSECT",VERTEX,{"derivedFrom":[subQ1,subQ0]});Q36=makeQuery(id+"F26.imprint","IMPRINT",FACE,{"disambiguationData":[TD([[makeQuery(id+"F26.imprint","IMPRINT",EDGE,{"disambiguationData":[TD([[subQ2,-1.0]])],"derivedFrom":subQ1}),-1.0]])]});}
            var Q37;
            {var subQ0=sQuery(id+"F26.wireOp",EDGE,"E660.right");var subQ1=sQuery(id+"F26.wireOp",EDGE,"E648.top");var subQ2=makeQuery(id+"F26.imprint","INTERSECT",VERTEX,{"derivedFrom":[subQ1,subQ0]});Q37=makeQuery(id+"F26.imprint","IMPRINT",FACE,{"disambiguationData":[TD([[makeQuery(id+"F26.imprint","IMPRINT",EDGE,{"disambiguationData":[TD([[subQ2,-1.0]])],"derivedFrom":subQ1}),-1.0]])]});}
            var Q38;
            {var subQ0=sQuery(id+"F26.wireOp",EDGE,"E660.right");var subQ1=sQuery(id+"F26.wireOp",EDGE,"E648.bottom");var subQ2=makeQuery(id+"F26.imprint","INTERSECT",VERTEX,{"derivedFrom":[subQ1,subQ0]});Q38=makeQuery(id+"F26.imprint","IMPRINT",FACE,{"disambiguationData":[TD([[makeQuery(id+"F26.imprint","IMPRINT",EDGE,{"disambiguationData":[TD([[subQ2,-1.0]])],"derivedFrom":subQ1}),-1.0]])]});}
            var Q39;
            {var subQ0=sQuery(id+"F26.wireOp",EDGE,"E660.right");var subQ1=sQuery(id+"F26.wireOp",EDGE,"E649.top");var subQ2=makeQuery(id+"F26.imprint","INTERSECT",VERTEX,{"derivedFrom":[subQ1,subQ0]});Q39=makeQuery(id+"F26.imprint","IMPRINT",FACE,{"disambiguationData":[TD([[makeQuery(id+"F26.imprint","IMPRINT",EDGE,{"disambiguationData":[TD([[subQ2,-1.0]])],"derivedFrom":subQ1}),-1.0]])]});}
            var Q40;
            {var subQ0=sQuery(id+"F26.wireOp",EDGE,"E660.right");var subQ1=sQuery(id+"F26.wireOp",EDGE,"E650.top");var subQ2=makeQuery(id+"F26.imprint","INTERSECT",VERTEX,{"derivedFrom":[subQ1,subQ0]});Q40=makeQuery(id+"F26.imprint","IMPRINT",FACE,{"disambiguationData":[TD([[makeQuery(id+"F26.imprint","IMPRINT",EDGE,{"disambiguationData":[TD([[subQ2,-1.0]])],"derivedFrom":subQ1}),-1.0]])]});}
            var Q41;
            {var subQ0=sQuery(id+"F26.wireOp",EDGE,"E660.right");var subQ1=sQuery(id+"F26.wireOp",EDGE,"E650.bottom");var subQ2=makeQuery(id+"F26.imprint","INTERSECT",VERTEX,{"derivedFrom":[subQ1,subQ0]});Q41=makeQuery(id+"F26.imprint","IMPRINT",FACE,{"disambiguationData":[TD([[makeQuery(id+"F26.imprint","IMPRINT",EDGE,{"disambiguationData":[TD([[subQ2,-1.0]])],"derivedFrom":subQ1}),-1.0]])]});}
            var Q42;
            {var subQ0=sQuery(id+"F26.wireOp",EDGE,"E664.right");var subQ1=sQuery(id+"F26.wireOp",EDGE,"E654.top");var subQ2=makeQuery(id+"F26.imprint","INTERSECT",VERTEX,{"derivedFrom":[subQ1,subQ0]});Q42=makeQuery(id+"F26.imprint","IMPRINT",FACE,{"disambiguationData":[TD([[makeQuery(id+"F26.imprint","IMPRINT",EDGE,{"disambiguationData":[TD([[subQ2,-1.0]])],"derivedFrom":subQ1}),-1.0]])]});}
            var Q43;
            {var subQ0=sQuery(id+"F26.wireOp",EDGE,"E664.left");var subQ1=sQuery(id+"F26.wireOp",EDGE,"E654.top");var subQ2=makeQuery(id+"F26.imprint","INTERSECT",VERTEX,{"derivedFrom":[subQ1,subQ0]});Q43=makeQuery(id+"F26.imprint","IMPRINT",FACE,{"disambiguationData":[TD([[makeQuery(id+"F26.imprint","IMPRINT",EDGE,{"disambiguationData":[TD([[subQ2,-1.0]])],"derivedFrom":subQ1}),-1.0]])]});}
            var Q44;
            {var subQ0=sQuery(id+"F26.wireOp",EDGE,"E665.right");var subQ1=sQuery(id+"F26.wireOp",EDGE,"E654.top");var subQ2=makeQuery(id+"F26.imprint","INTERSECT",VERTEX,{"derivedFrom":[subQ1,subQ0]});Q44=makeQuery(id+"F26.imprint","IMPRINT",FACE,{"disambiguationData":[TD([[makeQuery(id+"F26.imprint","IMPRINT",EDGE,{"disambiguationData":[TD([[subQ2,-1.0]])],"derivedFrom":subQ1}),-1.0]])]});}
            var Q45;
            {var subQ0=sQuery(id+"F26.wireOp",EDGE,"E666.right");var subQ1=sQuery(id+"F26.wireOp",EDGE,"E654.top");var subQ2=makeQuery(id+"F26.imprint","INTERSECT",VERTEX,{"derivedFrom":[subQ1,subQ0]});Q45=makeQuery(id+"F26.imprint","IMPRINT",FACE,{"disambiguationData":[TD([[makeQuery(id+"F26.imprint","IMPRINT",EDGE,{"disambiguationData":[TD([[subQ2,-1.0]])],"derivedFrom":subQ1}),-1.0]])]});}
            var Q46;
            {var subQ0=sQuery(id+"F26.wireOp",EDGE,"E666.left");var subQ1=sQuery(id+"F26.wireOp",EDGE,"E654.top");var subQ2=makeQuery(id+"F26.imprint","INTERSECT",VERTEX,{"derivedFrom":[subQ1,subQ0]});Q46=makeQuery(id+"F26.imprint","IMPRINT",FACE,{"disambiguationData":[TD([[makeQuery(id+"F26.imprint","IMPRINT",EDGE,{"disambiguationData":[TD([[subQ2,-1.0]])],"derivedFrom":subQ1}),-1.0]])]});}
            var Q47;
            {var subQ0=sQuery(id+"F26.wireOp",EDGE,"E667.right");var subQ1=sQuery(id+"F26.wireOp",EDGE,"E654.top");var subQ2=makeQuery(id+"F26.imprint","INTERSECT",VERTEX,{"derivedFrom":[subQ1,subQ0]});Q47=makeQuery(id+"F26.imprint","IMPRINT",FACE,{"disambiguationData":[TD([[makeQuery(id+"F26.imprint","IMPRINT",EDGE,{"disambiguationData":[TD([[subQ2,-1.0]])],"derivedFrom":subQ1}),-1.0]])]});}
            var Q48;
            {var subQ0=sQuery(id+"F26.wireOp",EDGE,"E664.right");var subQ1=sQuery(id+"F26.wireOp",EDGE,"E656.bottom");var subQ2=makeQuery(id+"F26.imprint","INTERSECT",VERTEX,{"derivedFrom":[subQ1,subQ0]});Q48=makeQuery(id+"F26.imprint","IMPRINT",FACE,{"disambiguationData":[TD([[makeQuery(id+"F26.imprint","IMPRINT",EDGE,{"disambiguationData":[TD([[subQ2,-1.0]])],"derivedFrom":subQ1}),-1.0]])]});}
            var Q49;
            {var subQ0=sQuery(id+"F26.wireOp",EDGE,"E664.left");var subQ1=sQuery(id+"F26.wireOp",EDGE,"E656.bottom");var subQ2=makeQuery(id+"F26.imprint","INTERSECT",VERTEX,{"derivedFrom":[subQ1,subQ0]});Q49=makeQuery(id+"F26.imprint","IMPRINT",FACE,{"disambiguationData":[TD([[makeQuery(id+"F26.imprint","IMPRINT",EDGE,{"disambiguationData":[TD([[subQ2,-1.0]])],"derivedFrom":subQ1}),-1.0]])]});}
            var Q50;
            {var subQ0=sQuery(id+"F26.wireOp",EDGE,"E665.right");var subQ1=sQuery(id+"F26.wireOp",EDGE,"E656.bottom");var subQ2=makeQuery(id+"F26.imprint","INTERSECT",VERTEX,{"derivedFrom":[subQ1,subQ0]});Q50=makeQuery(id+"F26.imprint","IMPRINT",FACE,{"disambiguationData":[TD([[makeQuery(id+"F26.imprint","IMPRINT",EDGE,{"disambiguationData":[TD([[subQ2,-1.0]])],"derivedFrom":subQ1}),-1.0]])]});}
            var Q51;
            {var subQ0=sQuery(id+"F26.wireOp",EDGE,"E666.right");var subQ1=sQuery(id+"F26.wireOp",EDGE,"E656.bottom");var subQ2=makeQuery(id+"F26.imprint","INTERSECT",VERTEX,{"derivedFrom":[subQ1,subQ0]});Q51=makeQuery(id+"F26.imprint","IMPRINT",FACE,{"disambiguationData":[TD([[makeQuery(id+"F26.imprint","IMPRINT",EDGE,{"disambiguationData":[TD([[subQ2,-1.0]])],"derivedFrom":subQ1}),-1.0]])]});}
            var Q52;
            {var subQ0=sQuery(id+"F26.wireOp",EDGE,"E666.left");var subQ1=sQuery(id+"F26.wireOp",EDGE,"E656.bottom");var subQ2=makeQuery(id+"F26.imprint","INTERSECT",VERTEX,{"derivedFrom":[subQ1,subQ0]});Q52=makeQuery(id+"F26.imprint","IMPRINT",FACE,{"disambiguationData":[TD([[makeQuery(id+"F26.imprint","IMPRINT",EDGE,{"disambiguationData":[TD([[subQ2,-1.0]])],"derivedFrom":subQ1}),-1.0]])]});}
            var Q53;
            {var subQ0=sQuery(id+"F26.wireOp",EDGE,"E667.right");var subQ1=sQuery(id+"F26.wireOp",EDGE,"E656.bottom");var subQ2=makeQuery(id+"F26.imprint","INTERSECT",VERTEX,{"derivedFrom":[subQ1,subQ0]});Q53=makeQuery(id+"F26.imprint","IMPRINT",FACE,{"disambiguationData":[TD([[makeQuery(id+"F26.imprint","IMPRINT",EDGE,{"disambiguationData":[TD([[subQ2,-1.0]])],"derivedFrom":subQ1}),-1.0]])]});}
            var Q54;
            {var subQ0=sQuery(id+"F26.wireOp",EDGE,"E662.left");var subQ1=sQuery(id+"F26.wireOp",EDGE,"E650.bottom");var subQ2=makeQuery(id+"F26.imprint","INTERSECT",VERTEX,{"derivedFrom":[subQ1,subQ0]});Q54=makeQuery(id+"F26.imprint","IMPRINT",FACE,{"disambiguationData":[TD([[makeQuery(id+"F26.imprint","IMPRINT",EDGE,{"disambiguationData":[TD([[subQ2,-1.0]])],"derivedFrom":subQ1}),-1.0]])]});}
            var Q55;
            {var subQ0=sQuery(id+"F26.wireOp",EDGE,"E662.left");var subQ1=sQuery(id+"F26.wireOp",EDGE,"E650.top");var subQ2=makeQuery(id+"F26.imprint","INTERSECT",VERTEX,{"derivedFrom":[subQ1,subQ0]});Q55=makeQuery(id+"F26.imprint","IMPRINT",FACE,{"disambiguationData":[TD([[makeQuery(id+"F26.imprint","IMPRINT",EDGE,{"disambiguationData":[TD([[subQ2,-1.0]])],"derivedFrom":subQ1}),-1.0]])]});}
            var Q56;
            {var subQ0=sQuery(id+"F26.wireOp",EDGE,"E662.left");var subQ1=sQuery(id+"F26.wireOp",EDGE,"E649.top");var subQ2=makeQuery(id+"F26.imprint","INTERSECT",VERTEX,{"derivedFrom":[subQ1,subQ0]});Q56=makeQuery(id+"F26.imprint","IMPRINT",FACE,{"disambiguationData":[TD([[makeQuery(id+"F26.imprint","IMPRINT",EDGE,{"disambiguationData":[TD([[subQ2,-1.0]])],"derivedFrom":subQ1}),-1.0]])]});}
            var Q57;
            {var subQ0=sQuery(id+"F26.wireOp",EDGE,"E662.left");var subQ1=sQuery(id+"F26.wireOp",EDGE,"E648.bottom");var subQ2=makeQuery(id+"F26.imprint","INTERSECT",VERTEX,{"derivedFrom":[subQ1,subQ0]});Q57=makeQuery(id+"F26.imprint","IMPRINT",FACE,{"disambiguationData":[TD([[makeQuery(id+"F26.imprint","IMPRINT",EDGE,{"disambiguationData":[TD([[subQ2,-1.0]])],"derivedFrom":subQ1}),-1.0]])]});}
            var Q58;
            {var subQ0=sQuery(id+"F26.wireOp",EDGE,"E662.left");var subQ1=sQuery(id+"F26.wireOp",EDGE,"E648.top");var subQ2=makeQuery(id+"F26.imprint","INTERSECT",VERTEX,{"derivedFrom":[subQ1,subQ0]});Q58=makeQuery(id+"F26.imprint","IMPRINT",FACE,{"disambiguationData":[TD([[makeQuery(id+"F26.imprint","IMPRINT",EDGE,{"disambiguationData":[TD([[subQ2,-1.0]])],"derivedFrom":subQ1}),-1.0]])]});}
            var Q59;
            {var subQ0=sQuery(id+"F26.wireOp",EDGE,"E662.left");var subQ1=sQuery(id+"F26.wireOp",EDGE,"E647.top");var subQ2=makeQuery(id+"F26.imprint","INTERSECT",VERTEX,{"derivedFrom":[subQ1,subQ0]});Q59=makeQuery(id+"F26.imprint","IMPRINT",FACE,{"disambiguationData":[TD([[makeQuery(id+"F26.imprint","IMPRINT",EDGE,{"disambiguationData":[TD([[subQ2,-1.0]])],"derivedFrom":subQ1}),-1.0]])]});}
            var Q60;
            {var subQ0=sQuery(id+"F26.wireOp",EDGE,"E725.MirrorCS");var subQ1=sQuery(id+"F26.wireOp",EDGE,"E687.MirrorCS");var subQ2=makeQuery(id+"F26.imprint","INTERSECT",VERTEX,{"derivedFrom":[subQ1,subQ0]});Q60=makeQuery(id+"F26.imprint","IMPRINT",FACE,{"disambiguationData":[TD([[makeQuery(id+"F26.imprint","IMPRINT",EDGE,{"disambiguationData":[TD([[subQ2,-1.0]])],"derivedFrom":subQ1}),1.0]])]});}
            var Q61;
            {var subQ0=sQuery(id+"F26.wireOp",EDGE,"E725.MirrorCS");var subQ1=sQuery(id+"F26.wireOp",EDGE,"E688.MirrorCS");var subQ2=makeQuery(id+"F26.imprint","INTERSECT",VERTEX,{"derivedFrom":[subQ1,subQ0]});Q61=makeQuery(id+"F26.imprint","IMPRINT",FACE,{"disambiguationData":[TD([[makeQuery(id+"F26.imprint","IMPRINT",EDGE,{"disambiguationData":[TD([[subQ2,-1.0]])],"derivedFrom":subQ1}),1.0]])]});}
            var Q62;
            {var subQ0=sQuery(id+"F26.wireOp",EDGE,"E725.MirrorCS");var subQ1=sQuery(id+"F26.wireOp",EDGE,"E690.MirrorCS");var subQ2=makeQuery(id+"F26.imprint","INTERSECT",VERTEX,{"derivedFrom":[subQ1,subQ0]});Q62=makeQuery(id+"F26.imprint","IMPRINT",FACE,{"disambiguationData":[TD([[makeQuery(id+"F26.imprint","IMPRINT",EDGE,{"disambiguationData":[TD([[subQ2,-1.0]])],"derivedFrom":subQ1}),1.0]])]});}
            var Q63;
            {var subQ0=sQuery(id+"F26.wireOp",EDGE,"E725.MirrorCS");var subQ1=sQuery(id+"F26.wireOp",EDGE,"E691.MirrorCS");var subQ2=makeQuery(id+"F26.imprint","INTERSECT",VERTEX,{"derivedFrom":[subQ1,subQ0]});Q63=makeQuery(id+"F26.imprint","IMPRINT",FACE,{"disambiguationData":[TD([[makeQuery(id+"F26.imprint","IMPRINT",EDGE,{"disambiguationData":[TD([[subQ2,-1.0]])],"derivedFrom":subQ1}),1.0]])]});}
            var Q64;
            {var subQ0=sQuery(id+"F26.wireOp",EDGE,"E725.MirrorCS");var subQ1=sQuery(id+"F26.wireOp",EDGE,"E692.MirrorCS");var subQ2=makeQuery(id+"F26.imprint","INTERSECT",VERTEX,{"derivedFrom":[subQ1,subQ0]});Q64=makeQuery(id+"F26.imprint","IMPRINT",FACE,{"disambiguationData":[TD([[makeQuery(id+"F26.imprint","IMPRINT",EDGE,{"disambiguationData":[TD([[subQ2,-1.0]])],"derivedFrom":subQ1}),1.0]])]});}
            var Q65;
            {var subQ0=sQuery(id+"F26.wireOp",EDGE,"E722.MirrorCS");var subQ1=sQuery(id+"F26.wireOp",EDGE,"E696.MirrorCS");var subQ2=makeQuery(id+"F26.imprint","INTERSECT",VERTEX,{"derivedFrom":[subQ1,subQ0]});Q65=makeQuery(id+"F26.imprint","IMPRINT",FACE,{"disambiguationData":[TD([[makeQuery(id+"F26.imprint","IMPRINT",EDGE,{"disambiguationData":[TD([[subQ2,-1.0]])],"derivedFrom":subQ1}),1.0]])]});}
            var Q66;
            {var subQ0=sQuery(id+"F26.wireOp",EDGE,"E721.MirrorCS");var subQ1=sQuery(id+"F26.wireOp",EDGE,"E696.MirrorCS");var subQ2=makeQuery(id+"F26.imprint","INTERSECT",VERTEX,{"derivedFrom":[subQ1,subQ0]});Q66=makeQuery(id+"F26.imprint","IMPRINT",FACE,{"disambiguationData":[TD([[makeQuery(id+"F26.imprint","IMPRINT",EDGE,{"disambiguationData":[TD([[subQ2,-1.0]])],"derivedFrom":subQ1}),1.0]])]});}
            var Q67;
            {var subQ0=sQuery(id+"F26.wireOp",EDGE,"E720.MirrorCS");var subQ1=sQuery(id+"F26.wireOp",EDGE,"E696.MirrorCS");var subQ2=makeQuery(id+"F26.imprint","INTERSECT",VERTEX,{"derivedFrom":[subQ1,subQ0]});Q67=makeQuery(id+"F26.imprint","IMPRINT",FACE,{"disambiguationData":[TD([[makeQuery(id+"F26.imprint","IMPRINT",EDGE,{"disambiguationData":[TD([[subQ2,-1.0]])],"derivedFrom":subQ1}),1.0]])]});}
            var Q68;
            {var subQ0=sQuery(id+"F26.wireOp",EDGE,"E719.MirrorCS");var subQ1=sQuery(id+"F26.wireOp",EDGE,"E696.MirrorCS");var subQ2=makeQuery(id+"F26.imprint","INTERSECT",VERTEX,{"derivedFrom":[subQ1,subQ0]});Q68=makeQuery(id+"F26.imprint","IMPRINT",FACE,{"disambiguationData":[TD([[makeQuery(id+"F26.imprint","IMPRINT",EDGE,{"disambiguationData":[TD([[subQ2,-1.0]])],"derivedFrom":subQ1}),1.0]])]});}
            var Q69;
            {var subQ0=sQuery(id+"F26.wireOp",EDGE,"E718.MirrorCS");var subQ1=sQuery(id+"F26.wireOp",EDGE,"E696.MirrorCS");var subQ2=makeQuery(id+"F26.imprint","INTERSECT",VERTEX,{"derivedFrom":[subQ1,subQ0]});Q69=makeQuery(id+"F26.imprint","IMPRINT",FACE,{"disambiguationData":[TD([[makeQuery(id+"F26.imprint","IMPRINT",EDGE,{"disambiguationData":[TD([[subQ2,-1.0]])],"derivedFrom":subQ1}),1.0]])]});}
            extrude(context, id + "F37", {"entities" : qUnion([Q0, Q1, Q2, Q3, Q4, Q5, Q6, Q7, Q8, Q9, Q10, Q11, Q12, Q13, Q14, Q15, Q16, Q17, Q18, Q19, Q20, Q21, Q22, Q23, Q24, Q25, Q26, Q27, Q28, Q29, Q30, Q31, Q32, Q33, Q34, Q35, Q36, Q37, Q38, Q39, Q40, Q41, Q42, Q43, Q44, Q45, Q46, Q47, Q48, Q49, Q50, Q51, Q52, Q53, Q54, Q55, Q56, Q57, Q58, Q59, Q60, Q61, Q62, Q63, Q64, Q65, Q66, Q67, Q68, Q69]), "operationType" : NewBodyOperationType.REMOVE, "oppositeDirection" : true, "depth" : 1.5 * mm, "offsetDistance" : 25 * mm});
        }
    });
